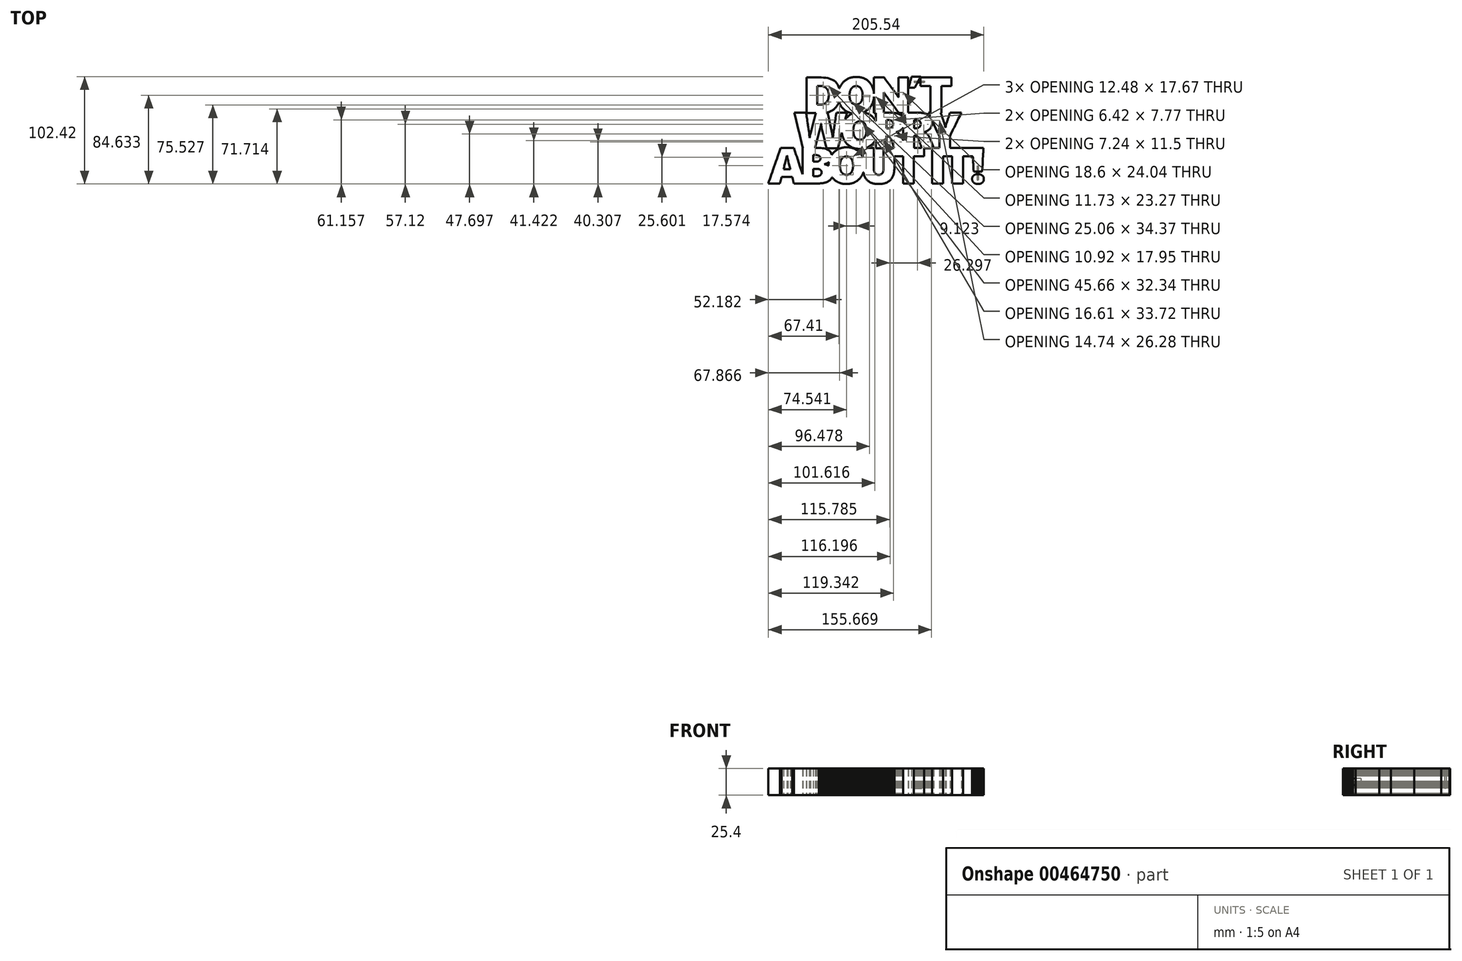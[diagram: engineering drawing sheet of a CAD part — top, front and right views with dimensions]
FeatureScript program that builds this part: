
annotation { "Feature Type Name" : "Feature", "Feature Type Description" : "" }
export const myFeature = defineFeature(function(context is Context, id is Id, definition is map)
    precondition{}
    {
        {
            var Q0;
            Q0=qCreatedBy(makeId("Top.planeOp"),FACE);
            cPlane(context, id + "F0", {"entities" : qUnion([Q0]), "cplaneType" : CPlaneType.OFFSET, "offset" : 12.7 * mm, "width" : 152.4 * mm, "height" : 152.4 * mm});
        }
        {
            var Q0;
            Q0=qCreatedBy(makeId("Top.planeOp"),FACE);
            var sketch = newSketch(context, id + "F1", { "sketchPlane" : qUnion([Q0])});
            skLineSegment(sketch, "E0", {"start": v(31.67, 40.7) * mm, "end": v(32.04, 40.7) * mm});
            skLineSegment(sketch, "E1", {"start": v(32.04, 40.7) * mm, "end": v(32.4, 40.7) * mm});
            skLineSegment(sketch, "E2", {"start": v(32.4, 40.7) * mm, "end": v(32.77, 40.7) * mm});
            skLineSegment(sketch, "E3", {"start": v(32.77, 40.7) * mm, "end": v(33.14, 40.7) * mm});
            skLineSegment(sketch, "E4", {"start": v(33.14, 40.7) * mm, "end": v(33.5, 40.7) * mm});
            skLineSegment(sketch, "E5", {"start": v(33.5, 40.7) * mm, "end": v(33.88, 40.7) * mm});
            skLineSegment(sketch, "E6", {"start": v(33.88, 40.7) * mm, "end": v(34.24, 40.7) * mm});
            skLineSegment(sketch, "E7", {"start": v(34.24, 40.7) * mm, "end": v(34.61, 40.7) * mm});
            skLineSegment(sketch, "E8", {"start": v(34.61, 40.7) * mm, "end": v(34.98, 40.7) * mm});
            skLineSegment(sketch, "E9", {"start": v(34.98, 40.7) * mm, "end": v(35.34, 40.7) * mm});
            skLineSegment(sketch, "E10", {"start": v(35.34, 40.7) * mm, "end": v(35.71, 40.7) * mm});
            skLineSegment(sketch, "E11", {"start": v(35.71, 40.7) * mm, "end": v(36.08, 40.7) * mm});
            skLineSegment(sketch, "E12", {"start": v(36.08, 40.7) * mm, "end": v(36.45, 40.7) * mm});
            skLineSegment(sketch, "E13", {"start": v(36.45, 40.7) * mm, "end": v(36.81, 40.7) * mm});
            skLineSegment(sketch, "E14", {"start": v(36.81, 40.7) * mm, "end": v(37.17, 41.35) * mm});
            skLineSegment(sketch, "E15", {"start": v(37.17, 41.35) * mm, "end": v(37.53, 42) * mm});
            skLineSegment(sketch, "E16", {"start": v(37.53, 42) * mm, "end": v(37.88, 42.67) * mm});
            skLineSegment(sketch, "E17", {"start": v(37.88, 42.67) * mm, "end": v(38.24, 43.32) * mm});
            skLineSegment(sketch, "E18", {"start": v(38.24, 43.32) * mm, "end": v(38.6, 43.98) * mm});
            skLineSegment(sketch, "E19", {"start": v(38.6, 43.98) * mm, "end": v(38.95, 44.64) * mm});
            skLineSegment(sketch, "E20", {"start": v(38.95, 44.64) * mm, "end": v(39.31, 45.3) * mm});
            skLineSegment(sketch, "E21", {"start": v(39.31, 45.3) * mm, "end": v(39.67, 45.95) * mm});
            skLineSegment(sketch, "E22", {"start": v(39.67, 45.95) * mm, "end": v(40.02, 46.6) * mm});
            skLineSegment(sketch, "E23", {"start": v(40.02, 46.6) * mm, "end": v(40.38, 47.27) * mm});
            skLineSegment(sketch, "E24", {"start": v(40.38, 47.27) * mm, "end": v(40.74, 47.92) * mm});
            skLineSegment(sketch, "E25", {"start": v(40.74, 47.92) * mm, "end": v(41.1, 48.58) * mm});
            skLineSegment(sketch, "E26", {"start": v(41.1, 48.58) * mm, "end": v(41.45, 49.24) * mm});
            skLineSegment(sketch, "E27", {"start": v(41.45, 49.24) * mm, "end": v(41.8, 49.9) * mm});
            skLineSegment(sketch, "E28", {"start": v(41.8, 49.9) * mm, "end": v(42.16, 50.55) * mm});
            skLineSegment(sketch, "E29", {"start": v(42.16, 50.55) * mm, "end": v(42.52, 51.21) * mm});
            skLineSegment(sketch, "E30", {"start": v(42.52, 51.21) * mm, "end": v(41.98, 51.21) * mm});
            skLineSegment(sketch, "E31", {"start": v(41.98, 51.21) * mm, "end": v(41.44, 51.21) * mm});
            skLineSegment(sketch, "E32", {"start": v(41.44, 51.21) * mm, "end": v(40.9, 51.21) * mm});
            skLineSegment(sketch, "E33", {"start": v(40.9, 51.21) * mm, "end": v(40.35, 51.21) * mm});
            skLineSegment(sketch, "E34", {"start": v(40.35, 51.21) * mm, "end": v(39.81, 51.21) * mm});
            skLineSegment(sketch, "E35", {"start": v(39.81, 51.21) * mm, "end": v(39.27, 51.21) * mm});
            skLineSegment(sketch, "E36", {"start": v(39.27, 51.21) * mm, "end": v(38.73, 51.21) * mm});
            skLineSegment(sketch, "E37", {"start": v(38.73, 51.21) * mm, "end": v(38.19, 51.21) * mm});
            skLineSegment(sketch, "E38", {"start": v(38.19, 51.21) * mm, "end": v(37.64, 51.21) * mm});
            skLineSegment(sketch, "E39", {"start": v(37.64, 51.21) * mm, "end": v(37.1, 51.21) * mm});
            skLineSegment(sketch, "E40", {"start": v(37.1, 51.21) * mm, "end": v(36.56, 51.21) * mm});
            skLineSegment(sketch, "E41", {"start": v(36.56, 51.21) * mm, "end": v(36.02, 51.21) * mm});
            skLineSegment(sketch, "E42", {"start": v(36.02, 51.21) * mm, "end": v(35.48, 51.21) * mm});
            skLineSegment(sketch, "E43", {"start": v(35.48, 51.21) * mm, "end": v(34.94, 51.21) * mm});
            skLineSegment(sketch, "E44", {"start": v(34.94, 51.21) * mm, "end": v(34.4, 51.21) * mm});
            skLineSegment(sketch, "E45", {"start": v(34.4, 51.21) * mm, "end": v(33.85, 51.21) * mm});
            skLineSegment(sketch, "E46", {"start": v(33.85, 51.21) * mm, "end": v(33.67, 50.55) * mm});
            skLineSegment(sketch, "E47", {"start": v(33.67, 50.55) * mm, "end": v(33.49, 49.9) * mm});
            skLineSegment(sketch, "E48", {"start": v(33.49, 49.9) * mm, "end": v(33.3, 49.24) * mm});
            skLineSegment(sketch, "E49", {"start": v(33.3, 49.24) * mm, "end": v(33.12, 48.58) * mm});
            skLineSegment(sketch, "E50", {"start": v(33.12, 48.58) * mm, "end": v(32.94, 47.92) * mm});
            skLineSegment(sketch, "E51", {"start": v(32.94, 47.92) * mm, "end": v(32.76, 47.27) * mm});
            skLineSegment(sketch, "E52", {"start": v(32.76, 47.27) * mm, "end": v(32.58, 46.6) * mm});
            skLineSegment(sketch, "E53", {"start": v(32.58, 46.6) * mm, "end": v(32.4, 45.95) * mm});
            skLineSegment(sketch, "E54", {"start": v(32.4, 45.95) * mm, "end": v(32.21, 45.3) * mm});
            skLineSegment(sketch, "E55", {"start": v(32.21, 45.3) * mm, "end": v(32.03, 44.64) * mm});
            skLineSegment(sketch, "E56", {"start": v(32.03, 44.64) * mm, "end": v(31.85, 43.98) * mm});
            skLineSegment(sketch, "E57", {"start": v(31.85, 43.98) * mm, "end": v(31.67, 43.32) * mm});
            skLineSegment(sketch, "E58", {"start": v(31.67, 43.32) * mm, "end": v(31.49, 42.67) * mm});
            skLineSegment(sketch, "E59", {"start": v(31.49, 42.67) * mm, "end": v(31.3, 42) * mm});
            skLineSegment(sketch, "E60", {"start": v(31.3, 42) * mm, "end": v(31.12, 41.35) * mm});
            skLineSegment(sketch, "E61", {"start": v(31.12, 41.35) * mm, "end": v(30.94, 40.7) * mm});
            skLineSegment(sketch, "E62", {"start": v(30.94, 40.7) * mm, "end": v(31.3, 40.7) * mm});
            skLineSegment(sketch, "E63", {"start": v(31.3, 40.7) * mm, "end": v(31.67, 40.7) * mm});
            skLineSegment(sketch, "E64", {"start": v(92.2, -24.66) * mm, "end": v(92.23, -25.1) * mm});
            skLineSegment(sketch, "E65", {"start": v(92.23, -25.1) * mm, "end": v(92.31, -26.5) * mm});
            skLineSegment(sketch, "E66", {"start": v(92.31, -26.5) * mm, "end": v(92.4, -27.92) * mm});
            skLineSegment(sketch, "E67", {"start": v(92.4, -27.92) * mm, "end": v(92.47, -29.32) * mm});
            skLineSegment(sketch, "E68", {"start": v(92.47, -29.32) * mm, "end": v(92.55, -30.73) * mm});
            skLineSegment(sketch, "E69", {"start": v(92.55, -30.73) * mm, "end": v(92.63, -32.14) * mm});
            skLineSegment(sketch, "E70", {"start": v(92.63, -32.14) * mm, "end": v(92.71, -33.55) * mm});
            skLineSegment(sketch, "E71", {"start": v(92.71, -33.55) * mm, "end": v(92.8, -34.95) * mm});
            skLineSegment(sketch, "E72", {"start": v(92.8, -34.95) * mm, "end": v(92.87, -36.36) * mm});
            skLineSegment(sketch, "E73", {"start": v(92.87, -36.36) * mm, "end": v(92.95, -37.77) * mm});
            skLineSegment(sketch, "E74", {"start": v(92.95, -37.77) * mm, "end": v(93.03, -39.18) * mm});
            skLineSegment(sketch, "E75", {"start": v(93.03, -39.18) * mm, "end": v(93.54, -39.18) * mm});
            skLineSegment(sketch, "E76", {"start": v(93.54, -39.18) * mm, "end": v(94.04, -39.18) * mm});
            skLineSegment(sketch, "E77", {"start": v(94.04, -39.18) * mm, "end": v(94.55, -39.18) * mm});
            skLineSegment(sketch, "E78", {"start": v(94.55, -39.18) * mm, "end": v(95.06, -39.18) * mm});
            skLineSegment(sketch, "E79", {"start": v(95.06, -39.18) * mm, "end": v(95.56, -39.18) * mm});
            skLineSegment(sketch, "E80", {"start": v(95.56, -39.18) * mm, "end": v(96.07, -39.18) * mm});
            skLineSegment(sketch, "E81", {"start": v(96.07, -39.18) * mm, "end": v(96.58, -39.18) * mm});
            skLineSegment(sketch, "E82", {"start": v(96.58, -39.18) * mm, "end": v(97.08, -39.18) * mm});
            skLineSegment(sketch, "E83", {"start": v(97.08, -39.18) * mm, "end": v(97.59, -39.18) * mm});
            skLineSegment(sketch, "E84", {"start": v(97.59, -39.18) * mm, "end": v(98.1, -39.18) * mm});
            skLineSegment(sketch, "E85", {"start": v(98.1, -39.18) * mm, "end": v(98.6, -39.18) * mm});
            skLineSegment(sketch, "E86", {"start": v(98.6, -39.18) * mm, "end": v(99.1, -39.18) * mm});
            skLineSegment(sketch, "E87", {"start": v(99.1, -39.18) * mm, "end": v(99.61, -39.18) * mm});
            skLineSegment(sketch, "E88", {"start": v(99.61, -39.18) * mm, "end": v(100.12, -39.18) * mm});
            skLineSegment(sketch, "E89", {"start": v(100.12, -39.18) * mm, "end": v(100.63, -39.18) * mm});
            skLineSegment(sketch, "E90", {"start": v(100.63, -39.18) * mm, "end": v(101.13, -39.18) * mm});
            skLineSegment(sketch, "E91", {"start": v(101.13, -39.18) * mm, "end": v(101.21, -37.77) * mm});
            skLineSegment(sketch, "E92", {"start": v(101.21, -37.77) * mm, "end": v(101.29, -36.36) * mm});
            skLineSegment(sketch, "E93", {"start": v(101.29, -36.36) * mm, "end": v(101.37, -34.95) * mm});
            skLineSegment(sketch, "E94", {"start": v(101.37, -34.95) * mm, "end": v(101.45, -33.55) * mm});
            skLineSegment(sketch, "E95", {"start": v(101.45, -33.55) * mm, "end": v(101.53, -32.14) * mm});
            skLineSegment(sketch, "E96", {"start": v(101.53, -32.14) * mm, "end": v(101.6, -30.73) * mm});
            skLineSegment(sketch, "E97", {"start": v(101.6, -30.73) * mm, "end": v(101.68, -29.32) * mm});
            skLineSegment(sketch, "E98", {"start": v(101.68, -29.32) * mm, "end": v(101.76, -27.92) * mm});
            skLineSegment(sketch, "E99", {"start": v(101.76, -27.92) * mm, "end": v(101.84, -26.5) * mm});
            skLineSegment(sketch, "E100", {"start": v(101.84, -26.5) * mm, "end": v(101.92, -25.1) * mm});
            skLineSegment(sketch, "E101", {"start": v(101.92, -25.1) * mm, "end": v(102, -23.7) * mm});
            skLineSegment(sketch, "E102", {"start": v(102, -23.7) * mm, "end": v(102.07, -22.28) * mm});
            skLineSegment(sketch, "E103", {"start": v(102.07, -22.28) * mm, "end": v(102.15, -20.88) * mm});
            skLineSegment(sketch, "E104", {"start": v(102.15, -20.88) * mm, "end": v(102.23, -19.47) * mm});
            skLineSegment(sketch, "E105", {"start": v(102.23, -19.47) * mm, "end": v(102.3, -18.06) * mm});
            skLineSegment(sketch, "E106", {"start": v(102.3, -18.06) * mm, "end": v(102.39, -16.65) * mm});
            skLineSegment(sketch, "E107", {"start": v(102.39, -16.65) * mm, "end": v(101.72, -16.65) * mm});
            skLineSegment(sketch, "E108", {"start": v(101.72, -16.65) * mm, "end": v(101.06, -16.65) * mm});
            skLineSegment(sketch, "E109", {"start": v(101.06, -16.65) * mm, "end": v(100.4, -16.65) * mm});
            skLineSegment(sketch, "E110", {"start": v(100.4, -16.65) * mm, "end": v(99.73, -16.65) * mm});
            skLineSegment(sketch, "E111", {"start": v(99.73, -16.65) * mm, "end": v(99.06, -16.65) * mm});
            skLineSegment(sketch, "E112", {"start": v(99.06, -16.65) * mm, "end": v(98.4, -16.65) * mm});
            skLineSegment(sketch, "E113", {"start": v(98.4, -16.65) * mm, "end": v(97.74, -16.65) * mm});
            skLineSegment(sketch, "E114", {"start": v(97.74, -16.65) * mm, "end": v(97.07, -16.65) * mm});
            skLineSegment(sketch, "E115", {"start": v(97.07, -16.65) * mm, "end": v(96.4, -16.65) * mm});
            skLineSegment(sketch, "E116", {"start": v(96.4, -16.65) * mm, "end": v(95.74, -16.65) * mm});
            skLineSegment(sketch, "E117", {"start": v(95.74, -16.65) * mm, "end": v(95.08, -16.65) * mm});
            skLineSegment(sketch, "E118", {"start": v(95.08, -16.65) * mm, "end": v(94.41, -16.65) * mm});
            skLineSegment(sketch, "E119", {"start": v(94.41, -16.65) * mm, "end": v(93.75, -16.65) * mm});
            skLineSegment(sketch, "E120", {"start": v(93.75, -16.65) * mm, "end": v(93.08, -16.65) * mm});
            skLineSegment(sketch, "E121", {"start": v(93.08, -16.65) * mm, "end": v(92.42, -16.65) * mm});
            skLineSegment(sketch, "E122", {"start": v(92.42, -16.65) * mm, "end": v(92.39, -16.65) * mm});
            skLineSegment(sketch, "E123", {"start": v(92.39, -16.65) * mm, "end": v(91.75, -16.65) * mm});
            skLineSegment(sketch, "E124", {"start": v(91.75, -16.65) * mm, "end": v(90.55, -16.65) * mm});
            skLineSegment(sketch, "E125", {"start": v(90.55, -16.65) * mm, "end": v(88.71, -16.65) * mm});
            skLineSegment(sketch, "E126", {"start": v(88.71, -16.65) * mm, "end": v(86.88, -16.65) * mm});
            skLineSegment(sketch, "E127", {"start": v(86.88, -16.65) * mm, "end": v(85.04, -16.65) * mm});
            skLineSegment(sketch, "E128", {"start": v(85.04, -16.65) * mm, "end": v(83.2, -16.65) * mm});
            skLineSegment(sketch, "E129", {"start": v(83.2, -16.65) * mm, "end": v(81.37, -16.65) * mm});
            skLineSegment(sketch, "E130", {"start": v(81.37, -16.65) * mm, "end": v(79.53, -16.65) * mm});
            skLineSegment(sketch, "E131", {"start": v(79.53, -16.65) * mm, "end": v(77.7, -16.65) * mm});
            skLineSegment(sketch, "E132", {"start": v(77.7, -16.65) * mm, "end": v(75.85, -16.65) * mm});
            skLineSegment(sketch, "E133", {"start": v(75.85, -16.65) * mm, "end": v(74.02, -16.65) * mm});
            skLineSegment(sketch, "E134", {"start": v(74.02, -16.65) * mm, "end": v(72.18, -16.65) * mm});
            skLineSegment(sketch, "E135", {"start": v(72.18, -16.65) * mm, "end": v(70.5, -16.65) * mm});
            skLineSegment(sketch, "E136", {"start": v(70.5, -16.65) * mm, "end": v(70.5, -16.35) * mm});
            skLineSegment(sketch, "E137", {"start": v(70.5, -16.35) * mm, "end": v(70.5, -15.61) * mm});
            skLineSegment(sketch, "E138", {"start": v(70.5, -15.61) * mm, "end": v(70.5, -14.88) * mm});
            skLineSegment(sketch, "E139", {"start": v(70.5, -14.88) * mm, "end": v(70.5, -14.14) * mm});
            skLineSegment(sketch, "E140", {"start": v(70.5, -14.14) * mm, "end": v(70.5, -13.4) * mm});
            skLineSegment(sketch, "E141", {"start": v(70.5, -13.4) * mm, "end": v(70.5, -12.67) * mm});
            skLineSegment(sketch, "E142", {"start": v(70.5, -12.67) * mm, "end": v(70.5, -11.93) * mm});
            skLineSegment(sketch, "E143", {"start": v(70.5, -11.93) * mm, "end": v(70.5, -11.2) * mm});
            skLineSegment(sketch, "E144", {"start": v(70.5, -11.2) * mm, "end": v(70.5, -10.45) * mm});
            skLineSegment(sketch, "E145", {"start": v(70.5, -10.45) * mm, "end": v(70.5, -9.72) * mm});
            skLineSegment(sketch, "E146", {"start": v(70.5, -9.72) * mm, "end": v(70.5, -8.98) * mm});
            skLineSegment(sketch, "E147", {"start": v(70.5, -8.98) * mm, "end": v(70.5, -8.24) * mm});
            skLineSegment(sketch, "E148", {"start": v(70.5, -8.24) * mm, "end": v(70.5, -7.5) * mm});
            skLineSegment(sketch, "E149", {"start": v(70.5, -7.5) * mm, "end": v(70.5, -6.77) * mm});
            skLineSegment(sketch, "E150", {"start": v(70.5, -6.77) * mm, "end": v(70.5, -6.03) * mm});
            skLineSegment(sketch, "E151", {"start": v(70.5, -6.03) * mm, "end": v(70.5, -5.3) * mm});
            skLineSegment(sketch, "E152", {"start": v(70.5, -5.3) * mm, "end": v(71.18, -3.9) * mm});
            skLineSegment(sketch, "E153", {"start": v(71.18, -3.9) * mm, "end": v(71.85, -2.52) * mm});
            skLineSegment(sketch, "E154", {"start": v(71.85, -2.52) * mm, "end": v(72.53, -1.14) * mm});
            skLineSegment(sketch, "E155", {"start": v(72.53, -1.14) * mm, "end": v(73.2, 0.25) * mm});
            skLineSegment(sketch, "E156", {"start": v(73.2, 0.25) * mm, "end": v(73.88, 1.63) * mm});
            skLineSegment(sketch, "E157", {"start": v(73.88, 1.63) * mm, "end": v(74.56, 3.02) * mm});
            skLineSegment(sketch, "E158", {"start": v(74.56, 3.02) * mm, "end": v(75.23, 4.4) * mm});
            skLineSegment(sketch, "E159", {"start": v(75.23, 4.4) * mm, "end": v(75.91, 5.8) * mm});
            skLineSegment(sketch, "E160", {"start": v(75.91, 5.8) * mm, "end": v(76.59, 7.18) * mm});
            skLineSegment(sketch, "E161", {"start": v(76.59, 7.18) * mm, "end": v(77.26, 8.56) * mm});
            skLineSegment(sketch, "E162", {"start": v(77.26, 8.56) * mm, "end": v(77.94, 9.95) * mm});
            skLineSegment(sketch, "E163", {"start": v(77.94, 9.95) * mm, "end": v(78.62, 11.33) * mm});
            skLineSegment(sketch, "E164", {"start": v(78.62, 11.33) * mm, "end": v(79.3, 12.72) * mm});
            skLineSegment(sketch, "E165", {"start": v(79.3, 12.72) * mm, "end": v(79.97, 14.1) * mm});
            skLineSegment(sketch, "E166", {"start": v(79.97, 14.1) * mm, "end": v(80.65, 15.5) * mm});
            skLineSegment(sketch, "E167", {"start": v(80.65, 15.5) * mm, "end": v(81.32, 16.88) * mm});
            skLineSegment(sketch, "E168", {"start": v(81.32, 16.88) * mm, "end": v(80.65, 16.88) * mm});
            skLineSegment(sketch, "E169", {"start": v(80.65, 16.88) * mm, "end": v(79.97, 16.88) * mm});
            skLineSegment(sketch, "E170", {"start": v(79.97, 16.88) * mm, "end": v(79.3, 16.88) * mm});
            skLineSegment(sketch, "E171", {"start": v(79.3, 16.88) * mm, "end": v(78.62, 16.88) * mm});
            skLineSegment(sketch, "E172", {"start": v(78.62, 16.88) * mm, "end": v(77.94, 16.88) * mm});
            skLineSegment(sketch, "E173", {"start": v(77.94, 16.88) * mm, "end": v(77.26, 16.88) * mm});
            skLineSegment(sketch, "E174", {"start": v(77.26, 16.88) * mm, "end": v(76.59, 16.88) * mm});
            skLineSegment(sketch, "E175", {"start": v(76.59, 16.88) * mm, "end": v(75.91, 16.88) * mm});
            skLineSegment(sketch, "E176", {"start": v(75.91, 16.88) * mm, "end": v(75.23, 16.88) * mm});
            skLineSegment(sketch, "E177", {"start": v(75.23, 16.88) * mm, "end": v(74.56, 16.88) * mm});
            skLineSegment(sketch, "E178", {"start": v(74.56, 16.88) * mm, "end": v(73.88, 16.88) * mm});
            skLineSegment(sketch, "E179", {"start": v(73.88, 16.88) * mm, "end": v(73.2, 16.88) * mm});
            skLineSegment(sketch, "E180", {"start": v(73.2, 16.88) * mm, "end": v(72.53, 16.88) * mm});
            skLineSegment(sketch, "E181", {"start": v(72.53, 16.88) * mm, "end": v(71.85, 16.88) * mm});
            skLineSegment(sketch, "E182", {"start": v(71.85, 16.88) * mm, "end": v(71.18, 16.88) * mm});
            skLineSegment(sketch, "E183", {"start": v(71.18, 16.88) * mm, "end": v(70.5, 16.88) * mm});
            skLineSegment(sketch, "E184", {"start": v(70.5, 16.88) * mm, "end": v(70.27, 16.2) * mm});
            skLineSegment(sketch, "E185", {"start": v(70.27, 16.2) * mm, "end": v(70.05, 15.52) * mm});
            skLineSegment(sketch, "E186", {"start": v(70.05, 15.52) * mm, "end": v(69.82, 14.84) * mm});
            skLineSegment(sketch, "E187", {"start": v(69.82, 14.84) * mm, "end": v(69.6, 14.16) * mm});
            skLineSegment(sketch, "E188", {"start": v(69.6, 14.16) * mm, "end": v(69.37, 13.48) * mm});
            skLineSegment(sketch, "E189", {"start": v(69.37, 13.48) * mm, "end": v(69.14, 12.8) * mm});
            skLineSegment(sketch, "E190", {"start": v(69.14, 12.8) * mm, "end": v(68.91, 12.12) * mm});
            skLineSegment(sketch, "E191", {"start": v(68.91, 12.12) * mm, "end": v(68.69, 11.44) * mm});
            skLineSegment(sketch, "E192", {"start": v(68.69, 11.44) * mm, "end": v(68.46, 10.76) * mm});
            skLineSegment(sketch, "E193", {"start": v(68.46, 10.76) * mm, "end": v(68.23, 10.08) * mm});
            skLineSegment(sketch, "E194", {"start": v(68.23, 10.08) * mm, "end": v(68, 9.4) * mm});
            skLineSegment(sketch, "E195", {"start": v(68, 9.4) * mm, "end": v(67.78, 8.72) * mm});
            skLineSegment(sketch, "E196", {"start": v(67.78, 8.72) * mm, "end": v(67.56, 8.04) * mm});
            skLineSegment(sketch, "E197", {"start": v(67.56, 8.04) * mm, "end": v(67.33, 7.36) * mm});
            skLineSegment(sketch, "E198", {"start": v(67.33, 7.36) * mm, "end": v(67.1, 6.68) * mm});
            skLineSegment(sketch, "E199", {"start": v(67.1, 6.68) * mm, "end": v(66.88, 6) * mm});
            skLineSegment(sketch, "E200", {"start": v(66.88, 6) * mm, "end": v(66.83, 5.85) * mm});
            skLineSegment(sketch, "E201", {"start": v(66.83, 5.85) * mm, "end": v(66.78, 5.7) * mm});
            skLineSegment(sketch, "E202", {"start": v(66.78, 5.7) * mm, "end": v(66.74, 5.53) * mm});
            skLineSegment(sketch, "E203", {"start": v(66.74, 5.53) * mm, "end": v(66.7, 5.35) * mm});
            skLineSegment(sketch, "E204", {"start": v(66.7, 5.35) * mm, "end": v(66.65, 5.17) * mm});
            skLineSegment(sketch, "E205", {"start": v(66.65, 5.17) * mm, "end": v(66.6, 4.98) * mm});
            skLineSegment(sketch, "E206", {"start": v(66.6, 4.98) * mm, "end": v(66.56, 4.78) * mm});
            skLineSegment(sketch, "E207", {"start": v(66.56, 4.78) * mm, "end": v(66.51, 4.58) * mm});
            skLineSegment(sketch, "E208", {"start": v(66.51, 4.58) * mm, "end": v(66.47, 4.36) * mm});
            skLineSegment(sketch, "E209", {"start": v(66.47, 4.36) * mm, "end": v(66.43, 4.14) * mm});
            skLineSegment(sketch, "E210", {"start": v(66.43, 4.14) * mm, "end": v(66.39, 3.92) * mm});
            skLineSegment(sketch, "E211", {"start": v(66.39, 3.92) * mm, "end": v(66.35, 3.68) * mm});
            skLineSegment(sketch, "E212", {"start": v(66.35, 3.68) * mm, "end": v(66.3, 3.44) * mm});
            skLineSegment(sketch, "E213", {"start": v(66.3, 3.44) * mm, "end": v(66.27, 3.19) * mm});
            skLineSegment(sketch, "E214", {"start": v(66.27, 3.19) * mm, "end": v(66.23, 2.93) * mm});
            skLineSegment(sketch, "E215", {"start": v(66.23, 2.93) * mm, "end": v(66.19, 2.66) * mm});
            skLineSegment(sketch, "E216", {"start": v(66.19, 2.66) * mm, "end": v(66.18, 2.66) * mm});
            skLineSegment(sketch, "E217", {"start": v(66.18, 2.66) * mm, "end": v(66.18, 2.66) * mm});
            skLineSegment(sketch, "E218", {"start": v(66.18, 2.66) * mm, "end": v(66.17, 2.66) * mm});
            skLineSegment(sketch, "E219", {"start": v(66.17, 2.66) * mm, "end": v(66.17, 2.66) * mm});
            skLineSegment(sketch, "E220", {"start": v(66.17, 2.66) * mm, "end": v(66.16, 2.66) * mm});
            skLineSegment(sketch, "E221", {"start": v(66.16, 2.66) * mm, "end": v(66.15, 2.66) * mm});
            skLineSegment(sketch, "E222", {"start": v(66.15, 2.66) * mm, "end": v(66.15, 2.66) * mm});
            skLineSegment(sketch, "E223", {"start": v(66.15, 2.66) * mm, "end": v(66.14, 2.66) * mm});
            skLineSegment(sketch, "E224", {"start": v(66.14, 2.66) * mm, "end": v(66.14, 2.66) * mm});
            skLineSegment(sketch, "E225", {"start": v(66.14, 2.66) * mm, "end": v(66.13, 2.66) * mm});
            skLineSegment(sketch, "E226", {"start": v(66.13, 2.66) * mm, "end": v(66.12, 2.66) * mm});
            skLineSegment(sketch, "E227", {"start": v(66.12, 2.66) * mm, "end": v(66.12, 2.66) * mm});
            skLineSegment(sketch, "E228", {"start": v(66.12, 2.66) * mm, "end": v(66.11, 2.66) * mm});
            skLineSegment(sketch, "E229", {"start": v(66.11, 2.66) * mm, "end": v(66.1, 2.66) * mm});
            skLineSegment(sketch, "E230", {"start": v(66.1, 2.66) * mm, "end": v(66.1, 2.66) * mm});
            skLineSegment(sketch, "E231", {"start": v(66.1, 2.66) * mm, "end": v(66.07, 2.77) * mm});
            skLineSegment(sketch, "E232", {"start": v(66.07, 2.77) * mm, "end": v(66.05, 2.87) * mm});
            skLineSegment(sketch, "E233", {"start": v(66.05, 2.87) * mm, "end": v(66.02, 2.97) * mm});
            skLineSegment(sketch, "E234", {"start": v(66.02, 2.97) * mm, "end": v(66, 3.08) * mm});
            skLineSegment(sketch, "E235", {"start": v(66, 3.08) * mm, "end": v(65.98, 3.18) * mm});
            skLineSegment(sketch, "E236", {"start": v(65.98, 3.18) * mm, "end": v(65.96, 3.28) * mm});
            skLineSegment(sketch, "E237", {"start": v(65.96, 3.28) * mm, "end": v(65.93, 3.39) * mm});
            skLineSegment(sketch, "E238", {"start": v(65.93, 3.39) * mm, "end": v(65.91, 3.49) * mm});
            skLineSegment(sketch, "E239", {"start": v(65.91, 3.49) * mm, "end": v(65.9, 3.59) * mm});
            skLineSegment(sketch, "E240", {"start": v(65.9, 3.59) * mm, "end": v(65.87, 3.7) * mm});
            skLineSegment(sketch, "E241", {"start": v(65.87, 3.7) * mm, "end": v(65.85, 3.8) * mm});
            skLineSegment(sketch, "E242", {"start": v(65.85, 3.8) * mm, "end": v(65.83, 3.9) * mm});
            skLineSegment(sketch, "E243", {"start": v(65.83, 3.9) * mm, "end": v(65.8, 4) * mm});
            skLineSegment(sketch, "E244", {"start": v(65.8, 4) * mm, "end": v(65.79, 4.1) * mm});
            skLineSegment(sketch, "E245", {"start": v(65.79, 4.1) * mm, "end": v(65.77, 4.2) * mm});
            skLineSegment(sketch, "E246", {"start": v(65.77, 4.2) * mm, "end": v(65.75, 4.3) * mm});
            skLineSegment(sketch, "E247", {"start": v(65.75, 4.3) * mm, "end": v(65.73, 4.4) * mm});
            skLineSegment(sketch, "E248", {"start": v(65.73, 4.4) * mm, "end": v(65.7, 4.5) * mm});
            skLineSegment(sketch, "E249", {"start": v(65.7, 4.5) * mm, "end": v(65.68, 4.61) * mm});
            skLineSegment(sketch, "E250", {"start": v(65.68, 4.61) * mm, "end": v(65.66, 4.72) * mm});
            skLineSegment(sketch, "E251", {"start": v(65.66, 4.72) * mm, "end": v(65.63, 4.83) * mm});
            skLineSegment(sketch, "E252", {"start": v(65.63, 4.83) * mm, "end": v(65.6, 4.94) * mm});
            skLineSegment(sketch, "E253", {"start": v(65.6, 4.94) * mm, "end": v(65.57, 5.06) * mm});
            skLineSegment(sketch, "E254", {"start": v(65.57, 5.06) * mm, "end": v(65.54, 5.18) * mm});
            skLineSegment(sketch, "E255", {"start": v(65.54, 5.18) * mm, "end": v(65.5, 5.3) * mm});
            skLineSegment(sketch, "E256", {"start": v(65.5, 5.3) * mm, "end": v(65.47, 5.42) * mm});
            skLineSegment(sketch, "E257", {"start": v(65.47, 5.42) * mm, "end": v(65.43, 5.54) * mm});
            skLineSegment(sketch, "E258", {"start": v(65.43, 5.54) * mm, "end": v(65.4, 5.67) * mm});
            skLineSegment(sketch, "E259", {"start": v(65.4, 5.67) * mm, "end": v(65.35, 5.8) * mm});
            skLineSegment(sketch, "E260", {"start": v(65.35, 5.8) * mm, "end": v(65.3, 5.93) * mm});
            skLineSegment(sketch, "E261", {"start": v(65.3, 5.93) * mm, "end": v(65.26, 6.06) * mm});
            skLineSegment(sketch, "E262", {"start": v(65.26, 6.06) * mm, "end": v(65.22, 6.2) * mm});
            skLineSegment(sketch, "E263", {"start": v(65.22, 6.2) * mm, "end": v(64.99, 6.86) * mm});
            skLineSegment(sketch, "E264", {"start": v(64.99, 6.86) * mm, "end": v(64.76, 7.53) * mm});
            skLineSegment(sketch, "E265", {"start": v(64.76, 7.53) * mm, "end": v(64.53, 8.2) * mm});
            skLineSegment(sketch, "E266", {"start": v(64.53, 8.2) * mm, "end": v(64.3, 8.86) * mm});
            skLineSegment(sketch, "E267", {"start": v(64.3, 8.86) * mm, "end": v(64.07, 9.53) * mm});
            skLineSegment(sketch, "E268", {"start": v(64.07, 9.53) * mm, "end": v(63.84, 10.2) * mm});
            skLineSegment(sketch, "E269", {"start": v(63.84, 10.2) * mm, "end": v(63.61, 10.87) * mm});
            skLineSegment(sketch, "E270", {"start": v(63.61, 10.87) * mm, "end": v(63.38, 11.53) * mm});
            skLineSegment(sketch, "E271", {"start": v(63.38, 11.53) * mm, "end": v(63.15, 12.2) * mm});
            skLineSegment(sketch, "E272", {"start": v(63.15, 12.2) * mm, "end": v(62.92, 12.87) * mm});
            skLineSegment(sketch, "E273", {"start": v(62.92, 12.87) * mm, "end": v(62.7, 13.54) * mm});
            skLineSegment(sketch, "E274", {"start": v(62.7, 13.54) * mm, "end": v(62.46, 14.2) * mm});
            skLineSegment(sketch, "E275", {"start": v(62.46, 14.2) * mm, "end": v(62.23, 14.87) * mm});
            skLineSegment(sketch, "E276", {"start": v(62.23, 14.87) * mm, "end": v(62, 15.54) * mm});
            skLineSegment(sketch, "E277", {"start": v(62, 15.54) * mm, "end": v(61.78, 16.2) * mm});
            skLineSegment(sketch, "E278", {"start": v(61.78, 16.2) * mm, "end": v(61.7, 16.44) * mm});
            skLineSegment(sketch, "E279", {"start": v(61.7, 16.44) * mm, "end": v(62.2, 16.44) * mm});
            skLineSegment(sketch, "E280", {"start": v(62.2, 16.44) * mm, "end": v(62.2, 18.06) * mm});
            skLineSegment(sketch, "E281", {"start": v(62.2, 18.06) * mm, "end": v(62.2, 19.69) * mm});
            skLineSegment(sketch, "E282", {"start": v(62.2, 19.69) * mm, "end": v(62.2, 21.3) * mm});
            skLineSegment(sketch, "E283", {"start": v(62.2, 21.3) * mm, "end": v(62.2, 22.93) * mm});
            skLineSegment(sketch, "E284", {"start": v(62.2, 22.93) * mm, "end": v(62.2, 24.55) * mm});
            skLineSegment(sketch, "E285", {"start": v(62.2, 24.55) * mm, "end": v(62.2, 26.18) * mm});
            skLineSegment(sketch, "E286", {"start": v(62.2, 26.18) * mm, "end": v(62.2, 27.8) * mm});
            skLineSegment(sketch, "E287", {"start": v(62.2, 27.8) * mm, "end": v(62.2, 29.42) * mm});
            skLineSegment(sketch, "E288", {"start": v(62.2, 29.42) * mm, "end": v(62.2, 31.04) * mm});
            skLineSegment(sketch, "E289", {"start": v(62.2, 31.04) * mm, "end": v(62.2, 32.66) * mm});
            skLineSegment(sketch, "E290", {"start": v(62.2, 32.66) * mm, "end": v(62.2, 34.29) * mm});
            skLineSegment(sketch, "E291", {"start": v(62.2, 34.29) * mm, "end": v(62.2, 35.9) * mm});
            skLineSegment(sketch, "E292", {"start": v(62.2, 35.9) * mm, "end": v(62.2, 37.53) * mm});
            skLineSegment(sketch, "E293", {"start": v(62.2, 37.53) * mm, "end": v(62.2, 39.15) * mm});
            skLineSegment(sketch, "E294", {"start": v(62.2, 39.15) * mm, "end": v(62.2, 40.78) * mm});
            skLineSegment(sketch, "E295", {"start": v(62.2, 40.78) * mm, "end": v(62.2, 42.4) * mm});
            skLineSegment(sketch, "E296", {"start": v(62.2, 42.4) * mm, "end": v(62.8, 42.4) * mm});
            skLineSegment(sketch, "E297", {"start": v(62.8, 42.4) * mm, "end": v(63.4, 42.4) * mm});
            skLineSegment(sketch, "E298", {"start": v(63.4, 42.4) * mm, "end": v(64, 42.4) * mm});
            skLineSegment(sketch, "E299", {"start": v(64, 42.4) * mm, "end": v(64.61, 42.4) * mm});
            skLineSegment(sketch, "E300", {"start": v(64.61, 42.4) * mm, "end": v(65.21, 42.4) * mm});
            skLineSegment(sketch, "E301", {"start": v(65.21, 42.4) * mm, "end": v(65.81, 42.4) * mm});
            skLineSegment(sketch, "E302", {"start": v(65.81, 42.4) * mm, "end": v(66.41, 42.4) * mm});
            skLineSegment(sketch, "E303", {"start": v(66.41, 42.4) * mm, "end": v(67.01, 42.4) * mm});
            skLineSegment(sketch, "E304", {"start": v(67.01, 42.4) * mm, "end": v(67.62, 42.4) * mm});
            skLineSegment(sketch, "E305", {"start": v(67.62, 42.4) * mm, "end": v(68.22, 42.4) * mm});
            skLineSegment(sketch, "E306", {"start": v(68.22, 42.4) * mm, "end": v(68.82, 42.4) * mm});
            skLineSegment(sketch, "E307", {"start": v(68.82, 42.4) * mm, "end": v(69.42, 42.4) * mm});
            skLineSegment(sketch, "E308", {"start": v(69.42, 42.4) * mm, "end": v(70.02, 42.4) * mm});
            skLineSegment(sketch, "E309", {"start": v(70.02, 42.4) * mm, "end": v(70.62, 42.4) * mm});
            skLineSegment(sketch, "E310", {"start": v(70.62, 42.4) * mm, "end": v(71.22, 42.4) * mm});
            skLineSegment(sketch, "E311", {"start": v(71.22, 42.4) * mm, "end": v(71.82, 42.4) * mm});
            skLineSegment(sketch, "E312", {"start": v(71.82, 42.4) * mm, "end": v(71.82, 42.9) * mm});
            skLineSegment(sketch, "E313", {"start": v(71.82, 42.9) * mm, "end": v(71.82, 43.4) * mm});
            skLineSegment(sketch, "E314", {"start": v(71.82, 43.4) * mm, "end": v(71.82, 43.9) * mm});
            skLineSegment(sketch, "E315", {"start": v(71.82, 43.9) * mm, "end": v(71.82, 44.4) * mm});
            skLineSegment(sketch, "E316", {"start": v(71.82, 44.4) * mm, "end": v(71.82, 44.9) * mm});
            skLineSegment(sketch, "E317", {"start": v(71.82, 44.9) * mm, "end": v(71.82, 45.4) * mm});
            skLineSegment(sketch, "E318", {"start": v(71.82, 45.4) * mm, "end": v(71.82, 45.9) * mm});
            skLineSegment(sketch, "E319", {"start": v(71.82, 45.9) * mm, "end": v(71.82, 46.4) * mm});
            skLineSegment(sketch, "E320", {"start": v(71.82, 46.4) * mm, "end": v(71.82, 46.9) * mm});
            skLineSegment(sketch, "E321", {"start": v(71.82, 46.9) * mm, "end": v(71.82, 47.4) * mm});
            skLineSegment(sketch, "E322", {"start": v(71.82, 47.4) * mm, "end": v(71.82, 47.9) * mm});
            skLineSegment(sketch, "E323", {"start": v(71.82, 47.9) * mm, "end": v(71.82, 48.4) * mm});
            skLineSegment(sketch, "E324", {"start": v(71.82, 48.4) * mm, "end": v(71.82, 48.9) * mm});
            skLineSegment(sketch, "E325", {"start": v(71.82, 48.9) * mm, "end": v(71.82, 49.4) * mm});
            skLineSegment(sketch, "E326", {"start": v(71.82, 49.4) * mm, "end": v(71.82, 49.9) * mm});
            skLineSegment(sketch, "E327", {"start": v(71.82, 49.9) * mm, "end": v(71.82, 50.4) * mm});
            skLineSegment(sketch, "E328", {"start": v(71.82, 50.4) * mm, "end": v(69.99, 50.4) * mm});
            skLineSegment(sketch, "E329", {"start": v(69.99, 50.4) * mm, "end": v(68.15, 50.4) * mm});
            skLineSegment(sketch, "E330", {"start": v(68.15, 50.4) * mm, "end": v(66.31, 50.4) * mm});
            skLineSegment(sketch, "E331", {"start": v(66.31, 50.4) * mm, "end": v(64.47, 50.4) * mm});
            skLineSegment(sketch, "E332", {"start": v(64.47, 50.4) * mm, "end": v(62.64, 50.4) * mm});
            skLineSegment(sketch, "E333", {"start": v(62.64, 50.4) * mm, "end": v(60.8, 50.4) * mm});
            skLineSegment(sketch, "E334", {"start": v(60.8, 50.4) * mm, "end": v(58.96, 50.4) * mm});
            skLineSegment(sketch, "E335", {"start": v(58.96, 50.4) * mm, "end": v(57.13, 50.4) * mm});
            skLineSegment(sketch, "E336", {"start": v(57.13, 50.4) * mm, "end": v(55.29, 50.4) * mm});
            skLineSegment(sketch, "E337", {"start": v(55.29, 50.4) * mm, "end": v(53.45, 50.4) * mm});
            skLineSegment(sketch, "E338", {"start": v(53.45, 50.4) * mm, "end": v(51.61, 50.4) * mm});
            skLineSegment(sketch, "E339", {"start": v(51.61, 50.4) * mm, "end": v(49.78, 50.4) * mm});
            skLineSegment(sketch, "E340", {"start": v(49.78, 50.4) * mm, "end": v(47.94, 50.4) * mm});
            skLineSegment(sketch, "E341", {"start": v(47.94, 50.4) * mm, "end": v(46.1, 50.4) * mm});
            skLineSegment(sketch, "E342", {"start": v(46.1, 50.4) * mm, "end": v(44.27, 50.4) * mm});
            skLineSegment(sketch, "E343", {"start": v(44.27, 50.4) * mm, "end": v(42.43, 50.4) * mm});
            skLineSegment(sketch, "E344", {"start": v(42.43, 50.4) * mm, "end": v(42.43, 49.9) * mm});
            skLineSegment(sketch, "E345", {"start": v(42.43, 49.9) * mm, "end": v(42.43, 49.4) * mm});
            skLineSegment(sketch, "E346", {"start": v(42.43, 49.4) * mm, "end": v(42.43, 48.9) * mm});
            skLineSegment(sketch, "E347", {"start": v(42.43, 48.9) * mm, "end": v(42.43, 48.4) * mm});
            skLineSegment(sketch, "E348", {"start": v(42.43, 48.4) * mm, "end": v(42.43, 47.9) * mm});
            skLineSegment(sketch, "E349", {"start": v(42.43, 47.9) * mm, "end": v(42.43, 47.4) * mm});
            skLineSegment(sketch, "E350", {"start": v(42.43, 47.4) * mm, "end": v(42.43, 46.9) * mm});
            skLineSegment(sketch, "E351", {"start": v(42.43, 46.9) * mm, "end": v(42.43, 46.4) * mm});
            skLineSegment(sketch, "E352", {"start": v(42.43, 46.4) * mm, "end": v(42.43, 45.9) * mm});
            skLineSegment(sketch, "E353", {"start": v(42.43, 45.9) * mm, "end": v(42.43, 45.4) * mm});
            skLineSegment(sketch, "E354", {"start": v(42.43, 45.4) * mm, "end": v(42.43, 44.9) * mm});
            skLineSegment(sketch, "E355", {"start": v(42.43, 44.9) * mm, "end": v(42.43, 44.4) * mm});
            skLineSegment(sketch, "E356", {"start": v(42.43, 44.4) * mm, "end": v(42.43, 43.9) * mm});
            skLineSegment(sketch, "E357", {"start": v(42.43, 43.9) * mm, "end": v(42.43, 43.4) * mm});
            skLineSegment(sketch, "E358", {"start": v(42.43, 43.4) * mm, "end": v(42.43, 42.9) * mm});
            skLineSegment(sketch, "E359", {"start": v(42.43, 42.9) * mm, "end": v(42.43, 42.4) * mm});
            skLineSegment(sketch, "E360", {"start": v(42.43, 42.4) * mm, "end": v(43.02, 42.4) * mm});
            skLineSegment(sketch, "E361", {"start": v(43.02, 42.4) * mm, "end": v(43.62, 42.4) * mm});
            skLineSegment(sketch, "E362", {"start": v(43.62, 42.4) * mm, "end": v(44.2, 42.4) * mm});
            skLineSegment(sketch, "E363", {"start": v(44.2, 42.4) * mm, "end": v(44.8, 42.4) * mm});
            skLineSegment(sketch, "E364", {"start": v(44.8, 42.4) * mm, "end": v(45.4, 42.4) * mm});
            skLineSegment(sketch, "E365", {"start": v(45.4, 42.4) * mm, "end": v(46, 42.4) * mm});
            skLineSegment(sketch, "E366", {"start": v(46, 42.4) * mm, "end": v(46.58, 42.4) * mm});
            skLineSegment(sketch, "E367", {"start": v(46.58, 42.4) * mm, "end": v(47.18, 42.4) * mm});
            skLineSegment(sketch, "E368", {"start": v(47.18, 42.4) * mm, "end": v(47.77, 42.4) * mm});
            skLineSegment(sketch, "E369", {"start": v(47.77, 42.4) * mm, "end": v(48.37, 42.4) * mm});
            skLineSegment(sketch, "E370", {"start": v(48.37, 42.4) * mm, "end": v(48.96, 42.4) * mm});
            skLineSegment(sketch, "E371", {"start": v(48.96, 42.4) * mm, "end": v(49.55, 42.4) * mm});
            skLineSegment(sketch, "E372", {"start": v(49.55, 42.4) * mm, "end": v(50.15, 42.4) * mm});
            skLineSegment(sketch, "E373", {"start": v(50.15, 42.4) * mm, "end": v(50.74, 42.4) * mm});
            skLineSegment(sketch, "E374", {"start": v(50.74, 42.4) * mm, "end": v(51.33, 42.4) * mm});
            skLineSegment(sketch, "E375", {"start": v(51.33, 42.4) * mm, "end": v(51.93, 42.4) * mm});
            skLineSegment(sketch, "E376", {"start": v(51.93, 42.4) * mm, "end": v(51.93, 40.78) * mm});
            skLineSegment(sketch, "E377", {"start": v(51.93, 40.78) * mm, "end": v(51.93, 39.15) * mm});
            skLineSegment(sketch, "E378", {"start": v(51.93, 39.15) * mm, "end": v(51.93, 37.53) * mm});
            skLineSegment(sketch, "E379", {"start": v(51.93, 37.53) * mm, "end": v(51.93, 35.9) * mm});
            skLineSegment(sketch, "E380", {"start": v(51.93, 35.9) * mm, "end": v(51.93, 34.29) * mm});
            skLineSegment(sketch, "E381", {"start": v(51.93, 34.29) * mm, "end": v(51.93, 32.66) * mm});
            skLineSegment(sketch, "E382", {"start": v(51.93, 32.66) * mm, "end": v(51.93, 31.04) * mm});
            skLineSegment(sketch, "E383", {"start": v(51.93, 31.04) * mm, "end": v(51.93, 29.42) * mm});
            skLineSegment(sketch, "E384", {"start": v(51.93, 29.42) * mm, "end": v(51.93, 27.8) * mm});
            skLineSegment(sketch, "E385", {"start": v(51.93, 27.8) * mm, "end": v(51.93, 26.18) * mm});
            skLineSegment(sketch, "E386", {"start": v(51.93, 26.18) * mm, "end": v(51.93, 24.55) * mm});
            skLineSegment(sketch, "E387", {"start": v(51.93, 24.55) * mm, "end": v(51.93, 22.93) * mm});
            skLineSegment(sketch, "E388", {"start": v(51.93, 22.93) * mm, "end": v(51.93, 21.3) * mm});
            skLineSegment(sketch, "E389", {"start": v(51.93, 21.3) * mm, "end": v(51.93, 19.69) * mm});
            skLineSegment(sketch, "E390", {"start": v(51.93, 19.69) * mm, "end": v(51.93, 18.06) * mm});
            skLineSegment(sketch, "E391", {"start": v(51.93, 18.06) * mm, "end": v(51.93, 16.88) * mm});
            skLineSegment(sketch, "E392", {"start": v(51.93, 16.88) * mm, "end": v(51.27, 16.88) * mm});
            skLineSegment(sketch, "E393", {"start": v(51.27, 16.88) * mm, "end": v(50.53, 16.88) * mm});
            skLineSegment(sketch, "E394", {"start": v(50.53, 16.88) * mm, "end": v(49.8, 16.88) * mm});
            skLineSegment(sketch, "E395", {"start": v(49.8, 16.88) * mm, "end": v(50.45, 15.48) * mm});
            skLineSegment(sketch, "E396", {"start": v(50.45, 15.48) * mm, "end": v(51.1, 14.09) * mm});
            skLineSegment(sketch, "E397", {"start": v(51.1, 14.09) * mm, "end": v(51.55, 13.15) * mm});
            skLineSegment(sketch, "E398", {"start": v(51.55, 13.15) * mm, "end": v(51.48, 13.23) * mm});
            skLineSegment(sketch, "E399", {"start": v(51.48, 13.23) * mm, "end": v(51.15, 13.59) * mm});
            skLineSegment(sketch, "E400", {"start": v(51.15, 13.59) * mm, "end": v(50.8, 13.92) * mm});
            skLineSegment(sketch, "E401", {"start": v(50.8, 13.92) * mm, "end": v(50.4, 14.24) * mm});
            skLineSegment(sketch, "E402", {"start": v(50.4, 14.24) * mm, "end": v(50, 14.54) * mm});
            skLineSegment(sketch, "E403", {"start": v(50, 14.54) * mm, "end": v(49.55, 14.83) * mm});
            skLineSegment(sketch, "E404", {"start": v(49.55, 14.83) * mm, "end": v(49.09, 15.09) * mm});
            skLineSegment(sketch, "E405", {"start": v(49.09, 15.09) * mm, "end": v(48.59, 15.34) * mm});
            skLineSegment(sketch, "E406", {"start": v(48.59, 15.34) * mm, "end": v(48.06, 15.56) * mm});
            skLineSegment(sketch, "E407", {"start": v(48.06, 15.56) * mm, "end": v(47.5, 15.77) * mm});
            skLineSegment(sketch, "E408", {"start": v(47.5, 15.77) * mm, "end": v(46.92, 15.96) * mm});
            skLineSegment(sketch, "E409", {"start": v(46.92, 15.96) * mm, "end": v(46.3, 16.14) * mm});
            skLineSegment(sketch, "E410", {"start": v(46.3, 16.14) * mm, "end": v(45.66, 16.3) * mm});
            skLineSegment(sketch, "E411", {"start": v(45.66, 16.3) * mm, "end": v(45, 16.43) * mm});
            skLineSegment(sketch, "E412", {"start": v(45, 16.43) * mm, "end": v(44.29, 16.55) * mm});
            skLineSegment(sketch, "E413", {"start": v(44.29, 16.55) * mm, "end": v(43.56, 16.65) * mm});
            skLineSegment(sketch, "E414", {"start": v(43.56, 16.65) * mm, "end": v(42.8, 16.73) * mm});
            skLineSegment(sketch, "E415", {"start": v(42.8, 16.73) * mm, "end": v(42, 16.8) * mm});
            skLineSegment(sketch, "E416", {"start": v(42, 16.8) * mm, "end": v(41.2, 16.84) * mm});
            skLineSegment(sketch, "E417", {"start": v(41.2, 16.84) * mm, "end": v(40.34, 16.87) * mm});
            skLineSegment(sketch, "E418", {"start": v(40.34, 16.87) * mm, "end": v(39.47, 16.88) * mm});
            skLineSegment(sketch, "E419", {"start": v(39.47, 16.88) * mm, "end": v(38.62, 16.88) * mm});
            skLineSegment(sketch, "E420", {"start": v(38.62, 16.88) * mm, "end": v(37.77, 16.88) * mm});
            skLineSegment(sketch, "E421", {"start": v(37.77, 16.88) * mm, "end": v(36.92, 16.88) * mm});
            skLineSegment(sketch, "E422", {"start": v(36.92, 16.88) * mm, "end": v(36.07, 16.88) * mm});
            skLineSegment(sketch, "E423", {"start": v(36.07, 16.88) * mm, "end": v(35.22, 16.88) * mm});
            skLineSegment(sketch, "E424", {"start": v(35.22, 16.88) * mm, "end": v(34.37, 16.88) * mm});
            skLineSegment(sketch, "E425", {"start": v(34.37, 16.88) * mm, "end": v(33.52, 16.88) * mm});
            skLineSegment(sketch, "E426", {"start": v(33.52, 16.88) * mm, "end": v(32.67, 16.88) * mm});
            skLineSegment(sketch, "E427", {"start": v(32.67, 16.88) * mm, "end": v(31.82, 16.88) * mm});
            skLineSegment(sketch, "E428", {"start": v(31.82, 16.88) * mm, "end": v(30.97, 16.88) * mm});
            skLineSegment(sketch, "E429", {"start": v(30.97, 16.88) * mm, "end": v(30.65, 16.88) * mm});
            skLineSegment(sketch, "E430", {"start": v(30.65, 16.88) * mm, "end": v(30.65, 18.56) * mm});
            skLineSegment(sketch, "E431", {"start": v(30.65, 18.56) * mm, "end": v(30.65, 20.69) * mm});
            skLineSegment(sketch, "E432", {"start": v(30.65, 20.69) * mm, "end": v(30.65, 22.8) * mm});
            skLineSegment(sketch, "E433", {"start": v(30.65, 22.8) * mm, "end": v(30.65, 24.93) * mm});
            skLineSegment(sketch, "E434", {"start": v(30.65, 24.93) * mm, "end": v(30.65, 27.05) * mm});
            skLineSegment(sketch, "E435", {"start": v(30.65, 27.05) * mm, "end": v(30.65, 29.18) * mm});
            skLineSegment(sketch, "E436", {"start": v(30.65, 29.18) * mm, "end": v(30.65, 31.3) * mm});
            skLineSegment(sketch, "E437", {"start": v(30.65, 31.3) * mm, "end": v(30.65, 33.42) * mm});
            skLineSegment(sketch, "E438", {"start": v(30.65, 33.42) * mm, "end": v(30.65, 35.55) * mm});
            skLineSegment(sketch, "E439", {"start": v(30.65, 35.55) * mm, "end": v(30.65, 37.67) * mm});
            skLineSegment(sketch, "E440", {"start": v(30.65, 37.67) * mm, "end": v(30.65, 39.8) * mm});
            skLineSegment(sketch, "E441", {"start": v(30.65, 39.8) * mm, "end": v(30.65, 41.91) * mm});
            skLineSegment(sketch, "E442", {"start": v(30.65, 41.91) * mm, "end": v(30.65, 44.04) * mm});
            skLineSegment(sketch, "E443", {"start": v(30.65, 44.04) * mm, "end": v(30.65, 46.16) * mm});
            skLineSegment(sketch, "E444", {"start": v(30.65, 46.16) * mm, "end": v(30.65, 48.28) * mm});
            skLineSegment(sketch, "E445", {"start": v(30.65, 48.28) * mm, "end": v(30.65, 50.4) * mm});
            skLineSegment(sketch, "E446", {"start": v(30.65, 50.4) * mm, "end": v(30.06, 50.4) * mm});
            skLineSegment(sketch, "E447", {"start": v(30.06, 50.4) * mm, "end": v(29.46, 50.4) * mm});
            skLineSegment(sketch, "E448", {"start": v(29.46, 50.4) * mm, "end": v(28.87, 50.4) * mm});
            skLineSegment(sketch, "E449", {"start": v(28.87, 50.4) * mm, "end": v(28.28, 50.4) * mm});
            skLineSegment(sketch, "E450", {"start": v(28.28, 50.4) * mm, "end": v(27.69, 50.4) * mm});
            skLineSegment(sketch, "E451", {"start": v(27.69, 50.4) * mm, "end": v(27.1, 50.4) * mm});
            skLineSegment(sketch, "E452", {"start": v(27.1, 50.4) * mm, "end": v(26.5, 50.4) * mm});
            skLineSegment(sketch, "E453", {"start": v(26.5, 50.4) * mm, "end": v(25.91, 50.4) * mm});
            skLineSegment(sketch, "E454", {"start": v(25.91, 50.4) * mm, "end": v(25.32, 50.4) * mm});
            skLineSegment(sketch, "E455", {"start": v(25.32, 50.4) * mm, "end": v(24.73, 50.4) * mm});
            skLineSegment(sketch, "E456", {"start": v(24.73, 50.4) * mm, "end": v(24.14, 50.4) * mm});
            skLineSegment(sketch, "E457", {"start": v(24.14, 50.4) * mm, "end": v(23.54, 50.4) * mm});
            skLineSegment(sketch, "E458", {"start": v(23.54, 50.4) * mm, "end": v(22.95, 50.4) * mm});
            skLineSegment(sketch, "E459", {"start": v(22.95, 50.4) * mm, "end": v(22.36, 50.4) * mm});
            skLineSegment(sketch, "E460", {"start": v(22.36, 50.4) * mm, "end": v(21.77, 50.4) * mm});
            skLineSegment(sketch, "E461", {"start": v(21.77, 50.4) * mm, "end": v(21.18, 50.4) * mm});
            skLineSegment(sketch, "E462", {"start": v(21.18, 50.4) * mm, "end": v(21.18, 49.45) * mm});
            skLineSegment(sketch, "E463", {"start": v(21.18, 49.45) * mm, "end": v(21.18, 48.5) * mm});
            skLineSegment(sketch, "E464", {"start": v(21.18, 48.5) * mm, "end": v(21.18, 47.55) * mm});
            skLineSegment(sketch, "E465", {"start": v(21.18, 47.55) * mm, "end": v(21.18, 46.6) * mm});
            skLineSegment(sketch, "E466", {"start": v(21.18, 46.6) * mm, "end": v(21.18, 45.65) * mm});
            skLineSegment(sketch, "E467", {"start": v(21.18, 45.65) * mm, "end": v(21.18, 44.7) * mm});
            skLineSegment(sketch, "E468", {"start": v(21.18, 44.7) * mm, "end": v(21.18, 43.74) * mm});
            skLineSegment(sketch, "E469", {"start": v(21.18, 43.74) * mm, "end": v(21.18, 42.8) * mm});
            skLineSegment(sketch, "E470", {"start": v(21.18, 42.8) * mm, "end": v(21.18, 41.84) * mm});
            skLineSegment(sketch, "E471", {"start": v(21.18, 41.84) * mm, "end": v(21.18, 40.89) * mm});
            skLineSegment(sketch, "E472", {"start": v(21.18, 40.89) * mm, "end": v(21.18, 39.93) * mm});
            skLineSegment(sketch, "E473", {"start": v(21.18, 39.93) * mm, "end": v(21.18, 38.98) * mm});
            skLineSegment(sketch, "E474", {"start": v(21.18, 38.98) * mm, "end": v(21.18, 38.03) * mm});
            skLineSegment(sketch, "E475", {"start": v(21.18, 38.03) * mm, "end": v(21.18, 37.08) * mm});
            skLineSegment(sketch, "E476", {"start": v(21.18, 37.08) * mm, "end": v(21.18, 36.13) * mm});
            skLineSegment(sketch, "E477", {"start": v(21.18, 36.13) * mm, "end": v(21.18, 35.18) * mm});
            skLineSegment(sketch, "E478", {"start": v(21.18, 35.18) * mm, "end": v(21.18, 34.86) * mm});
            skLineSegment(sketch, "E479", {"start": v(21.18, 34.86) * mm, "end": v(21.18, 34.56) * mm});
            skLineSegment(sketch, "E480", {"start": v(21.18, 34.56) * mm, "end": v(21.18, 34.27) * mm});
            skLineSegment(sketch, "E481", {"start": v(21.18, 34.27) * mm, "end": v(21.18, 34) * mm});
            skLineSegment(sketch, "E482", {"start": v(21.18, 34) * mm, "end": v(21.19, 33.72) * mm});
            skLineSegment(sketch, "E483", {"start": v(21.19, 33.72) * mm, "end": v(21.2, 33.47) * mm});
            skLineSegment(sketch, "E484", {"start": v(21.2, 33.47) * mm, "end": v(21.2, 33.23) * mm});
            skLineSegment(sketch, "E485", {"start": v(21.2, 33.23) * mm, "end": v(21.21, 33) * mm});
            skLineSegment(sketch, "E486", {"start": v(21.21, 33) * mm, "end": v(21.22, 32.78) * mm});
            skLineSegment(sketch, "E487", {"start": v(21.22, 32.78) * mm, "end": v(21.23, 32.57) * mm});
            skLineSegment(sketch, "E488", {"start": v(21.23, 32.57) * mm, "end": v(21.24, 32.37) * mm});
            skLineSegment(sketch, "E489", {"start": v(21.24, 32.37) * mm, "end": v(21.26, 32.2) * mm});
            skLineSegment(sketch, "E490", {"start": v(21.26, 32.2) * mm, "end": v(21.27, 32.02) * mm});
            skLineSegment(sketch, "E491", {"start": v(21.27, 32.02) * mm, "end": v(21.28, 31.86) * mm});
            skLineSegment(sketch, "E492", {"start": v(21.28, 31.86) * mm, "end": v(21.3, 31.71) * mm});
            skLineSegment(sketch, "E493", {"start": v(21.3, 31.71) * mm, "end": v(21.32, 31.58) * mm});
            skLineSegment(sketch, "E494", {"start": v(21.32, 31.58) * mm, "end": v(21.31, 31.58) * mm});
            skLineSegment(sketch, "E495", {"start": v(21.31, 31.58) * mm, "end": v(21.3, 31.58) * mm});
            skLineSegment(sketch, "E496", {"start": v(21.3, 31.58) * mm, "end": v(21.3, 31.58) * mm});
            skLineSegment(sketch, "E497", {"start": v(21.3, 31.58) * mm, "end": v(21.29, 31.58) * mm});
            skLineSegment(sketch, "E498", {"start": v(21.29, 31.58) * mm, "end": v(21.28, 31.58) * mm});
            skLineSegment(sketch, "E499", {"start": v(21.28, 31.58) * mm, "end": v(21.28, 31.58) * mm});
            skLineSegment(sketch, "E500", {"start": v(21.28, 31.58) * mm, "end": v(21.27, 31.58) * mm});
            skLineSegment(sketch, "E501", {"start": v(21.27, 31.58) * mm, "end": v(21.26, 31.58) * mm});
            skLineSegment(sketch, "E502", {"start": v(21.26, 31.58) * mm, "end": v(21.26, 31.58) * mm});
            skLineSegment(sketch, "E503", {"start": v(21.26, 31.58) * mm, "end": v(21.25, 31.58) * mm});
            skLineSegment(sketch, "E504", {"start": v(21.25, 31.58) * mm, "end": v(21.25, 31.58) * mm});
            skLineSegment(sketch, "E505", {"start": v(21.25, 31.58) * mm, "end": v(21.24, 31.58) * mm});
            skLineSegment(sketch, "E506", {"start": v(21.24, 31.58) * mm, "end": v(21.23, 31.58) * mm});
            skLineSegment(sketch, "E507", {"start": v(21.23, 31.58) * mm, "end": v(21.23, 31.58) * mm});
            skLineSegment(sketch, "E508", {"start": v(21.23, 31.58) * mm, "end": v(21.22, 31.58) * mm});
            skLineSegment(sketch, "E509", {"start": v(21.22, 31.58) * mm, "end": v(21.2, 31.62) * mm});
            skLineSegment(sketch, "E510", {"start": v(21.2, 31.62) * mm, "end": v(21.18, 31.66) * mm});
            skLineSegment(sketch, "E511", {"start": v(21.18, 31.66) * mm, "end": v(21.16, 31.7) * mm});
            skLineSegment(sketch, "E512", {"start": v(21.16, 31.7) * mm, "end": v(21.14, 31.75) * mm});
            skLineSegment(sketch, "E513", {"start": v(21.14, 31.75) * mm, "end": v(21.12, 31.8) * mm});
            skLineSegment(sketch, "E514", {"start": v(21.12, 31.8) * mm, "end": v(21.1, 31.84) * mm});
            skLineSegment(sketch, "E515", {"start": v(21.1, 31.84) * mm, "end": v(21.07, 31.88) * mm});
            skLineSegment(sketch, "E516", {"start": v(21.07, 31.88) * mm, "end": v(21.05, 31.93) * mm});
            skLineSegment(sketch, "E517", {"start": v(21.05, 31.93) * mm, "end": v(21.02, 31.98) * mm});
            skLineSegment(sketch, "E518", {"start": v(21.02, 31.98) * mm, "end": v(21, 32.03) * mm});
            skLineSegment(sketch, "E519", {"start": v(21, 32.03) * mm, "end": v(20.97, 32.08) * mm});
            skLineSegment(sketch, "E520", {"start": v(20.97, 32.08) * mm, "end": v(20.94, 32.13) * mm});
            skLineSegment(sketch, "E521", {"start": v(20.94, 32.13) * mm, "end": v(20.9, 32.18) * mm});
            skLineSegment(sketch, "E522", {"start": v(20.9, 32.18) * mm, "end": v(20.87, 32.23) * mm});
            skLineSegment(sketch, "E523", {"start": v(20.87, 32.23) * mm, "end": v(20.84, 32.28) * mm});
            skLineSegment(sketch, "E524", {"start": v(20.84, 32.28) * mm, "end": v(20.8, 32.33) * mm});
            skLineSegment(sketch, "E525", {"start": v(20.8, 32.33) * mm, "end": v(20.77, 32.39) * mm});
            skLineSegment(sketch, "E526", {"start": v(20.77, 32.39) * mm, "end": v(20.74, 32.44) * mm});
            skLineSegment(sketch, "E527", {"start": v(20.74, 32.44) * mm, "end": v(20.7, 32.5) * mm});
            skLineSegment(sketch, "E528", {"start": v(20.7, 32.5) * mm, "end": v(20.67, 32.55) * mm});
            skLineSegment(sketch, "E529", {"start": v(20.67, 32.55) * mm, "end": v(20.63, 32.6) * mm});
            skLineSegment(sketch, "E530", {"start": v(20.63, 32.6) * mm, "end": v(20.6, 32.66) * mm});
            skLineSegment(sketch, "E531", {"start": v(20.6, 32.66) * mm, "end": v(20.56, 32.71) * mm});
            skLineSegment(sketch, "E532", {"start": v(20.56, 32.71) * mm, "end": v(20.53, 32.77) * mm});
            skLineSegment(sketch, "E533", {"start": v(20.53, 32.77) * mm, "end": v(20.5, 32.82) * mm});
            skLineSegment(sketch, "E534", {"start": v(20.5, 32.82) * mm, "end": v(20.45, 32.88) * mm});
            skLineSegment(sketch, "E535", {"start": v(20.45, 32.88) * mm, "end": v(20.42, 32.93) * mm});
            skLineSegment(sketch, "E536", {"start": v(20.42, 32.93) * mm, "end": v(20.38, 32.99) * mm});
            skLineSegment(sketch, "E537", {"start": v(20.38, 32.99) * mm, "end": v(20.34, 33.04) * mm});
            skLineSegment(sketch, "E538", {"start": v(20.34, 33.04) * mm, "end": v(20.3, 33.1) * mm});
            skLineSegment(sketch, "E539", {"start": v(20.3, 33.1) * mm, "end": v(20.27, 33.15) * mm});
            skLineSegment(sketch, "E540", {"start": v(20.27, 33.15) * mm, "end": v(20.23, 33.2) * mm});
            skLineSegment(sketch, "E541", {"start": v(20.23, 33.2) * mm, "end": v(20.19, 33.27) * mm});
            skLineSegment(sketch, "E542", {"start": v(20.19, 33.27) * mm, "end": v(20.15, 33.32) * mm});
            skLineSegment(sketch, "E543", {"start": v(20.15, 33.32) * mm, "end": v(20.11, 33.38) * mm});
            skLineSegment(sketch, "E544", {"start": v(20.11, 33.38) * mm, "end": v(20.07, 33.43) * mm});
            skLineSegment(sketch, "E545", {"start": v(20.07, 33.43) * mm, "end": v(20.04, 33.49) * mm});
            skLineSegment(sketch, "E546", {"start": v(20.04, 33.49) * mm, "end": v(20, 33.54) * mm});
            skLineSegment(sketch, "E547", {"start": v(20, 33.54) * mm, "end": v(19.96, 33.6) * mm});
            skLineSegment(sketch, "E548", {"start": v(19.96, 33.6) * mm, "end": v(19.92, 33.65) * mm});
            skLineSegment(sketch, "E549", {"start": v(19.92, 33.65) * mm, "end": v(19.88, 33.7) * mm});
            skLineSegment(sketch, "E550", {"start": v(19.88, 33.7) * mm, "end": v(19.84, 33.76) * mm});
            skLineSegment(sketch, "E551", {"start": v(19.84, 33.76) * mm, "end": v(19.8, 33.82) * mm});
            skLineSegment(sketch, "E552", {"start": v(19.8, 33.82) * mm, "end": v(19.77, 33.87) * mm});
            skLineSegment(sketch, "E553", {"start": v(19.77, 33.87) * mm, "end": v(19.73, 33.93) * mm});
            skLineSegment(sketch, "E554", {"start": v(19.73, 33.93) * mm, "end": v(19.69, 33.98) * mm});
            skLineSegment(sketch, "E555", {"start": v(19.69, 33.98) * mm, "end": v(19.65, 34.03) * mm});
            skLineSegment(sketch, "E556", {"start": v(19.65, 34.03) * mm, "end": v(19.61, 34.09) * mm});
            skLineSegment(sketch, "E557", {"start": v(19.61, 34.09) * mm, "end": v(19.57, 34.14) * mm});
            skLineSegment(sketch, "E558", {"start": v(19.57, 34.14) * mm, "end": v(19.54, 34.2) * mm});
            skLineSegment(sketch, "E559", {"start": v(19.54, 34.2) * mm, "end": v(19.5, 34.24) * mm});
            skLineSegment(sketch, "E560", {"start": v(19.5, 34.24) * mm, "end": v(19.46, 34.3) * mm});
            skLineSegment(sketch, "E561", {"start": v(19.46, 34.3) * mm, "end": v(19.43, 34.34) * mm});
            skLineSegment(sketch, "E562", {"start": v(19.43, 34.34) * mm, "end": v(19.4, 34.39) * mm});
            skLineSegment(sketch, "E563", {"start": v(19.4, 34.39) * mm, "end": v(19.36, 34.44) * mm});
            skLineSegment(sketch, "E564", {"start": v(19.36, 34.44) * mm, "end": v(19.33, 34.48) * mm});
            skLineSegment(sketch, "E565", {"start": v(19.33, 34.48) * mm, "end": v(19.3, 34.53) * mm});
            skLineSegment(sketch, "E566", {"start": v(19.3, 34.53) * mm, "end": v(19.26, 34.57) * mm});
            skLineSegment(sketch, "E567", {"start": v(19.26, 34.57) * mm, "end": v(19.23, 34.62) * mm});
            skLineSegment(sketch, "E568", {"start": v(19.23, 34.62) * mm, "end": v(19.2, 34.66) * mm});
            skLineSegment(sketch, "E569", {"start": v(19.2, 34.66) * mm, "end": v(19.17, 34.7) * mm});
            skLineSegment(sketch, "E570", {"start": v(19.17, 34.7) * mm, "end": v(19.15, 34.74) * mm});
            skLineSegment(sketch, "E571", {"start": v(19.15, 34.74) * mm, "end": v(19.12, 34.78) * mm});
            skLineSegment(sketch, "E572", {"start": v(19.12, 34.78) * mm, "end": v(19.1, 34.82) * mm});
            skLineSegment(sketch, "E573", {"start": v(19.1, 34.82) * mm, "end": v(18.37, 35.8) * mm});
            skLineSegment(sketch, "E574", {"start": v(18.37, 35.8) * mm, "end": v(17.65, 36.77) * mm});
            skLineSegment(sketch, "E575", {"start": v(17.65, 36.77) * mm, "end": v(16.94, 37.74) * mm});
            skLineSegment(sketch, "E576", {"start": v(16.94, 37.74) * mm, "end": v(16.22, 38.72) * mm});
            skLineSegment(sketch, "E577", {"start": v(16.22, 38.72) * mm, "end": v(15.5, 39.7) * mm});
            skLineSegment(sketch, "E578", {"start": v(15.5, 39.7) * mm, "end": v(14.78, 40.66) * mm});
            skLineSegment(sketch, "E579", {"start": v(14.78, 40.66) * mm, "end": v(14.07, 41.64) * mm});
            skLineSegment(sketch, "E580", {"start": v(14.07, 41.64) * mm, "end": v(13.35, 42.61) * mm});
            skLineSegment(sketch, "E581", {"start": v(13.35, 42.61) * mm, "end": v(12.63, 43.59) * mm});
            skLineSegment(sketch, "E582", {"start": v(12.63, 43.59) * mm, "end": v(11.91, 44.56) * mm});
            skLineSegment(sketch, "E583", {"start": v(11.91, 44.56) * mm, "end": v(11.2, 45.53) * mm});
            skLineSegment(sketch, "E584", {"start": v(11.2, 45.53) * mm, "end": v(10.48, 46.5) * mm});
            skLineSegment(sketch, "E585", {"start": v(10.48, 46.5) * mm, "end": v(9.76, 47.48) * mm});
            skLineSegment(sketch, "E586", {"start": v(9.76, 47.48) * mm, "end": v(9.04, 48.46) * mm});
            skLineSegment(sketch, "E587", {"start": v(9.04, 48.46) * mm, "end": v(8.32, 49.43) * mm});
            skLineSegment(sketch, "E588", {"start": v(8.32, 49.43) * mm, "end": v(7.6, 50.4) * mm});
            skLineSegment(sketch, "E589", {"start": v(7.6, 50.4) * mm, "end": v(7, 50.4) * mm});
            skLineSegment(sketch, "E590", {"start": v(7, 50.4) * mm, "end": v(6.4, 50.4) * mm});
            skLineSegment(sketch, "E591", {"start": v(6.4, 50.4) * mm, "end": v(5.8, 50.4) * mm});
            skLineSegment(sketch, "E592", {"start": v(5.8, 50.4) * mm, "end": v(5.19, 50.4) * mm});
            skLineSegment(sketch, "E593", {"start": v(5.19, 50.4) * mm, "end": v(4.58, 50.4) * mm});
            skLineSegment(sketch, "E594", {"start": v(4.58, 50.4) * mm, "end": v(3.98, 50.4) * mm});
            skLineSegment(sketch, "E595", {"start": v(3.98, 50.4) * mm, "end": v(3.38, 50.4) * mm});
            skLineSegment(sketch, "E596", {"start": v(3.38, 50.4) * mm, "end": v(2.77, 50.4) * mm});
            skLineSegment(sketch, "E597", {"start": v(2.77, 50.4) * mm, "end": v(2.17, 50.4) * mm});
            skLineSegment(sketch, "E598", {"start": v(2.17, 50.4) * mm, "end": v(1.56, 50.4) * mm});
            skLineSegment(sketch, "E599", {"start": v(1.56, 50.4) * mm, "end": v(0.96, 50.4) * mm});
            skLineSegment(sketch, "E600", {"start": v(0.96, 50.4) * mm, "end": v(0.36, 50.4) * mm});
            skLineSegment(sketch, "E601", {"start": v(0.36, 50.4) * mm, "end": v(-0.25, 50.4) * mm});
            skLineSegment(sketch, "E602", {"start": v(-0.25, 50.4) * mm, "end": v(-0.85, 50.4) * mm});
            skLineSegment(sketch, "E603", {"start": v(-0.85, 50.4) * mm, "end": v(-1.46, 50.4) * mm});
            skLineSegment(sketch, "E604", {"start": v(-1.46, 50.4) * mm, "end": v(-2.06, 50.4) * mm});
            skLineSegment(sketch, "E605", {"start": v(-2.06, 50.4) * mm, "end": v(-2.06, 48.28) * mm});
            skLineSegment(sketch, "E606", {"start": v(-2.06, 48.28) * mm, "end": v(-2.06, 46.16) * mm});
            skLineSegment(sketch, "E607", {"start": v(-2.06, 46.16) * mm, "end": v(-2.06, 44.04) * mm});
            skLineSegment(sketch, "E608", {"start": v(-2.06, 44.04) * mm, "end": v(-2.06, 41.91) * mm});
            skLineSegment(sketch, "E609", {"start": v(-2.06, 41.91) * mm, "end": v(-2.06, 39.8) * mm});
            skLineSegment(sketch, "E610", {"start": v(-2.06, 39.8) * mm, "end": v(-2.06, 37.67) * mm});
            skLineSegment(sketch, "E611", {"start": v(-2.06, 37.67) * mm, "end": v(-2.06, 35.55) * mm});
            skLineSegment(sketch, "E612", {"start": v(-2.06, 35.55) * mm, "end": v(-2.06, 34.92) * mm});
            skLineSegment(sketch, "E613", {"start": v(-2.06, 34.92) * mm, "end": v(-2.1, 35.39) * mm});
            skLineSegment(sketch, "E614", {"start": v(-2.1, 35.39) * mm, "end": v(-2.15, 36) * mm});
            skLineSegment(sketch, "E615", {"start": v(-2.15, 36) * mm, "end": v(-2.22, 36.6) * mm});
            skLineSegment(sketch, "E616", {"start": v(-2.22, 36.6) * mm, "end": v(-2.31, 37.19) * mm});
            skLineSegment(sketch, "E617", {"start": v(-2.31, 37.19) * mm, "end": v(-2.42, 37.77) * mm});
            skLineSegment(sketch, "E618", {"start": v(-2.42, 37.77) * mm, "end": v(-2.54, 38.34) * mm});
            skLineSegment(sketch, "E619", {"start": v(-2.54, 38.34) * mm, "end": v(-2.68, 38.9) * mm});
            skLineSegment(sketch, "E620", {"start": v(-2.68, 38.9) * mm, "end": v(-2.84, 39.46) * mm});
            skLineSegment(sketch, "E621", {"start": v(-2.84, 39.46) * mm, "end": v(-3, 40.01) * mm});
            skLineSegment(sketch, "E622", {"start": v(-3, 40.01) * mm, "end": v(-3.2, 40.55) * mm});
            skLineSegment(sketch, "E623", {"start": v(-3.2, 40.55) * mm, "end": v(-3.4, 41.08) * mm});
            skLineSegment(sketch, "E624", {"start": v(-3.4, 41.08) * mm, "end": v(-3.62, 41.6) * mm});
            skLineSegment(sketch, "E625", {"start": v(-3.62, 41.6) * mm, "end": v(-3.86, 42.12) * mm});
            skLineSegment(sketch, "E626", {"start": v(-3.86, 42.12) * mm, "end": v(-4.11, 42.62) * mm});
            skLineSegment(sketch, "E627", {"start": v(-4.11, 42.62) * mm, "end": v(-4.38, 43.12) * mm});
            skLineSegment(sketch, "E628", {"start": v(-4.38, 43.12) * mm, "end": v(-4.66, 43.6) * mm});
            skLineSegment(sketch, "E629", {"start": v(-4.66, 43.6) * mm, "end": v(-4.96, 44.06) * mm});
            skLineSegment(sketch, "E630", {"start": v(-4.96, 44.06) * mm, "end": v(-5.27, 44.52) * mm});
            skLineSegment(sketch, "E631", {"start": v(-5.27, 44.52) * mm, "end": v(-5.6, 44.95) * mm});
            skLineSegment(sketch, "E632", {"start": v(-5.6, 44.95) * mm, "end": v(-5.93, 45.38) * mm});
            skLineSegment(sketch, "E633", {"start": v(-5.93, 45.38) * mm, "end": v(-6.28, 45.78) * mm});
            skLineSegment(sketch, "E634", {"start": v(-6.28, 45.78) * mm, "end": v(-6.65, 46.18) * mm});
            skLineSegment(sketch, "E635", {"start": v(-6.65, 46.18) * mm, "end": v(-7.03, 46.56) * mm});
            skLineSegment(sketch, "E636", {"start": v(-7.03, 46.56) * mm, "end": v(-7.42, 46.92) * mm});
            skLineSegment(sketch, "E637", {"start": v(-7.42, 46.92) * mm, "end": v(-7.82, 47.27) * mm});
            skLineSegment(sketch, "E638", {"start": v(-7.82, 47.27) * mm, "end": v(-8.24, 47.6) * mm});
            skLineSegment(sketch, "E639", {"start": v(-8.24, 47.6) * mm, "end": v(-8.68, 47.93) * mm});
            skLineSegment(sketch, "E640", {"start": v(-8.68, 47.93) * mm, "end": v(-9.12, 48.24) * mm});
            skLineSegment(sketch, "E641", {"start": v(-9.12, 48.24) * mm, "end": v(-9.58, 48.53) * mm});
            skLineSegment(sketch, "E642", {"start": v(-9.58, 48.53) * mm, "end": v(-10.06, 48.8) * mm});
            skLineSegment(sketch, "E643", {"start": v(-10.06, 48.8) * mm, "end": v(-10.54, 49.07) * mm});
            skLineSegment(sketch, "E644", {"start": v(-10.54, 49.07) * mm, "end": v(-11.04, 49.31) * mm});
            skLineSegment(sketch, "E645", {"start": v(-11.04, 49.31) * mm, "end": v(-11.54, 49.54) * mm});
            skLineSegment(sketch, "E646", {"start": v(-11.54, 49.54) * mm, "end": v(-12.05, 49.75) * mm});
            skLineSegment(sketch, "E647", {"start": v(-12.05, 49.75) * mm, "end": v(-12.56, 49.95) * mm});
            skLineSegment(sketch, "E648", {"start": v(-12.56, 49.95) * mm, "end": v(-13.09, 50.13) * mm});
            skLineSegment(sketch, "E649", {"start": v(-13.09, 50.13) * mm, "end": v(-13.62, 50.29) * mm});
            skLineSegment(sketch, "E650", {"start": v(-13.62, 50.29) * mm, "end": v(-14.16, 50.43) * mm});
            skLineSegment(sketch, "E651", {"start": v(-14.16, 50.43) * mm, "end": v(-14.71, 50.56) * mm});
            skLineSegment(sketch, "E652", {"start": v(-14.71, 50.56) * mm, "end": v(-15.27, 50.67) * mm});
            skLineSegment(sketch, "E653", {"start": v(-15.27, 50.67) * mm, "end": v(-15.84, 50.76) * mm});
            skLineSegment(sketch, "E654", {"start": v(-15.84, 50.76) * mm, "end": v(-16.41, 50.84) * mm});
            skLineSegment(sketch, "E655", {"start": v(-16.41, 50.84) * mm, "end": v(-17, 50.9) * mm});
            skLineSegment(sketch, "E656", {"start": v(-17, 50.9) * mm, "end": v(-17.58, 50.94) * mm});
            skLineSegment(sketch, "E657", {"start": v(-17.58, 50.94) * mm, "end": v(-18.18, 50.96) * mm});
            skLineSegment(sketch, "E658", {"start": v(-18.18, 50.96) * mm, "end": v(-18.79, 50.97) * mm});
            skLineSegment(sketch, "E659", {"start": v(-18.79, 50.97) * mm, "end": v(-19.42, 50.96) * mm});
            skLineSegment(sketch, "E660", {"start": v(-19.42, 50.96) * mm, "end": v(-20.04, 50.94) * mm});
            skLineSegment(sketch, "E661", {"start": v(-20.04, 50.94) * mm, "end": v(-20.65, 50.9) * mm});
            skLineSegment(sketch, "E662", {"start": v(-20.65, 50.9) * mm, "end": v(-21.25, 50.83) * mm});
            skLineSegment(sketch, "E663", {"start": v(-21.25, 50.83) * mm, "end": v(-21.85, 50.75) * mm});
            skLineSegment(sketch, "E664", {"start": v(-21.85, 50.75) * mm, "end": v(-22.43, 50.66) * mm});
            skLineSegment(sketch, "E665", {"start": v(-22.43, 50.66) * mm, "end": v(-23.01, 50.54) * mm});
            skLineSegment(sketch, "E666", {"start": v(-23.01, 50.54) * mm, "end": v(-23.58, 50.4) * mm});
            skLineSegment(sketch, "E667", {"start": v(-23.58, 50.4) * mm, "end": v(-24.14, 50.26) * mm});
            skLineSegment(sketch, "E668", {"start": v(-24.14, 50.26) * mm, "end": v(-24.7, 50.09) * mm});
            skLineSegment(sketch, "E669", {"start": v(-24.7, 50.09) * mm, "end": v(-25.24, 49.9) * mm});
            skLineSegment(sketch, "E670", {"start": v(-25.24, 49.9) * mm, "end": v(-25.78, 49.7) * mm});
            skLineSegment(sketch, "E671", {"start": v(-25.78, 49.7) * mm, "end": v(-26.3, 49.48) * mm});
            skLineSegment(sketch, "E672", {"start": v(-26.3, 49.48) * mm, "end": v(-26.82, 49.24) * mm});
            skLineSegment(sketch, "E673", {"start": v(-26.82, 49.24) * mm, "end": v(-27.33, 48.99) * mm});
            skLineSegment(sketch, "E674", {"start": v(-27.33, 48.99) * mm, "end": v(-27.83, 48.71) * mm});
            skLineSegment(sketch, "E675", {"start": v(-27.83, 48.71) * mm, "end": v(-28.32, 48.42) * mm});
            skLineSegment(sketch, "E676", {"start": v(-28.32, 48.42) * mm, "end": v(-28.8, 48.12) * mm});
            skLineSegment(sketch, "E677", {"start": v(-28.8, 48.12) * mm, "end": v(-29.26, 47.8) * mm});
            skLineSegment(sketch, "E678", {"start": v(-29.26, 47.8) * mm, "end": v(-29.71, 47.46) * mm});
            skLineSegment(sketch, "E679", {"start": v(-29.71, 47.46) * mm, "end": v(-30.15, 47.11) * mm});
            skLineSegment(sketch, "E680", {"start": v(-30.15, 47.11) * mm, "end": v(-30.57, 46.75) * mm});
            skLineSegment(sketch, "E681", {"start": v(-30.57, 46.75) * mm, "end": v(-30.98, 46.37) * mm});
            skLineSegment(sketch, "E682", {"start": v(-30.98, 46.37) * mm, "end": v(-31.37, 45.98) * mm});
            skLineSegment(sketch, "E683", {"start": v(-31.37, 45.98) * mm, "end": v(-31.75, 45.57) * mm});
            skLineSegment(sketch, "E684", {"start": v(-31.75, 45.57) * mm, "end": v(-32.11, 45.15) * mm});
            skLineSegment(sketch, "E685", {"start": v(-32.11, 45.15) * mm, "end": v(-32.47, 44.71) * mm});
            skLineSegment(sketch, "E686", {"start": v(-32.47, 44.71) * mm, "end": v(-32.8, 44.26) * mm});
            skLineSegment(sketch, "E687", {"start": v(-32.8, 44.26) * mm, "end": v(-33.13, 43.8) * mm});
            skLineSegment(sketch, "E688", {"start": v(-33.13, 43.8) * mm, "end": v(-33.44, 43.31) * mm});
            skLineSegment(sketch, "E689", {"start": v(-33.44, 43.31) * mm, "end": v(-33.73, 42.82) * mm});
            skLineSegment(sketch, "E690", {"start": v(-33.73, 42.82) * mm, "end": v(-34.02, 42.3) * mm});
            skLineSegment(sketch, "E691", {"start": v(-34.02, 42.3) * mm, "end": v(-34.28, 41.78) * mm});
            skLineSegment(sketch, "E692", {"start": v(-34.28, 41.78) * mm, "end": v(-34.53, 41.25) * mm});
            skLineSegment(sketch, "E693", {"start": v(-34.53, 41.25) * mm, "end": v(-34.76, 40.71) * mm});
            skLineSegment(sketch, "E694", {"start": v(-34.76, 40.71) * mm, "end": v(-34.98, 40.17) * mm});
            skLineSegment(sketch, "E695", {"start": v(-34.98, 40.17) * mm, "end": v(-35.04, 39.99) * mm});
            skLineSegment(sketch, "E696", {"start": v(-35.04, 39.99) * mm, "end": v(-35.38, 41.1) * mm});
            skLineSegment(sketch, "E697", {"start": v(-35.38, 41.1) * mm, "end": v(-36.01, 42.58) * mm});
            skLineSegment(sketch, "E698", {"start": v(-36.01, 42.58) * mm, "end": v(-36.78, 43.94) * mm});
            skLineSegment(sketch, "E699", {"start": v(-36.78, 43.94) * mm, "end": v(-37.7, 45.17) * mm});
            skLineSegment(sketch, "E700", {"start": v(-37.7, 45.17) * mm, "end": v(-38.75, 46.27) * mm});
            skLineSegment(sketch, "E701", {"start": v(-38.75, 46.27) * mm, "end": v(-39.94, 47.24) * mm});
            skLineSegment(sketch, "E702", {"start": v(-39.94, 47.24) * mm, "end": v(-41.27, 48.08) * mm});
            skLineSegment(sketch, "E703", {"start": v(-41.27, 48.08) * mm, "end": v(-42.74, 48.79) * mm});
            skLineSegment(sketch, "E704", {"start": v(-42.74, 48.79) * mm, "end": v(-44.36, 49.37) * mm});
            skLineSegment(sketch, "E705", {"start": v(-44.36, 49.37) * mm, "end": v(-46.1, 49.82) * mm});
            skLineSegment(sketch, "E706", {"start": v(-46.1, 49.82) * mm, "end": v(-48, 50.15) * mm});
            skLineSegment(sketch, "E707", {"start": v(-48, 50.15) * mm, "end": v(-50.04, 50.34) * mm});
            skLineSegment(sketch, "E708", {"start": v(-50.04, 50.34) * mm, "end": v(-52.21, 50.4) * mm});
            skLineSegment(sketch, "E709", {"start": v(-52.21, 50.4) * mm, "end": v(-53.09, 50.4) * mm});
            skLineSegment(sketch, "E710", {"start": v(-53.09, 50.4) * mm, "end": v(-53.97, 50.4) * mm});
            skLineSegment(sketch, "E711", {"start": v(-53.97, 50.4) * mm, "end": v(-54.85, 50.4) * mm});
            skLineSegment(sketch, "E712", {"start": v(-54.85, 50.4) * mm, "end": v(-55.73, 50.4) * mm});
            skLineSegment(sketch, "E713", {"start": v(-55.73, 50.4) * mm, "end": v(-56.6, 50.4) * mm});
            skLineSegment(sketch, "E714", {"start": v(-56.6, 50.4) * mm, "end": v(-57.49, 50.4) * mm});
            skLineSegment(sketch, "E715", {"start": v(-57.49, 50.4) * mm, "end": v(-58.37, 50.4) * mm});
            skLineSegment(sketch, "E716", {"start": v(-58.37, 50.4) * mm, "end": v(-59.25, 50.4) * mm});
            skLineSegment(sketch, "E717", {"start": v(-59.25, 50.4) * mm, "end": v(-60.12, 50.4) * mm});
            skLineSegment(sketch, "E718", {"start": v(-60.12, 50.4) * mm, "end": v(-61, 50.4) * mm});
            skLineSegment(sketch, "E719", {"start": v(-61, 50.4) * mm, "end": v(-61.88, 50.4) * mm});
            skLineSegment(sketch, "E720", {"start": v(-61.88, 50.4) * mm, "end": v(-62.76, 50.4) * mm});
            skLineSegment(sketch, "E721", {"start": v(-62.76, 50.4) * mm, "end": v(-63.64, 50.4) * mm});
            skLineSegment(sketch, "E722", {"start": v(-63.64, 50.4) * mm, "end": v(-64.52, 50.4) * mm});
            skLineSegment(sketch, "E723", {"start": v(-64.52, 50.4) * mm, "end": v(-65.4, 50.4) * mm});
            skLineSegment(sketch, "E724", {"start": v(-65.4, 50.4) * mm, "end": v(-66.28, 50.4) * mm});
            skLineSegment(sketch, "E725", {"start": v(-66.28, 50.4) * mm, "end": v(-66.28, 48.28) * mm});
            skLineSegment(sketch, "E726", {"start": v(-66.28, 48.28) * mm, "end": v(-66.28, 46.16) * mm});
            skLineSegment(sketch, "E727", {"start": v(-66.28, 46.16) * mm, "end": v(-66.28, 44.04) * mm});
            skLineSegment(sketch, "E728", {"start": v(-66.28, 44.04) * mm, "end": v(-66.28, 41.91) * mm});
            skLineSegment(sketch, "E729", {"start": v(-66.28, 41.91) * mm, "end": v(-66.28, 39.8) * mm});
            skLineSegment(sketch, "E730", {"start": v(-66.28, 39.8) * mm, "end": v(-66.28, 37.67) * mm});
            skLineSegment(sketch, "E731", {"start": v(-66.28, 37.67) * mm, "end": v(-66.28, 35.55) * mm});
            skLineSegment(sketch, "E732", {"start": v(-66.28, 35.55) * mm, "end": v(-66.28, 33.42) * mm});
            skLineSegment(sketch, "E733", {"start": v(-66.28, 33.42) * mm, "end": v(-66.28, 31.3) * mm});
            skLineSegment(sketch, "E734", {"start": v(-66.28, 31.3) * mm, "end": v(-66.28, 29.18) * mm});
            skLineSegment(sketch, "E735", {"start": v(-66.28, 29.18) * mm, "end": v(-66.28, 27.05) * mm});
            skLineSegment(sketch, "E736", {"start": v(-66.28, 27.05) * mm, "end": v(-66.28, 24.93) * mm});
            skLineSegment(sketch, "E737", {"start": v(-66.28, 24.93) * mm, "end": v(-66.28, 22.8) * mm});
            skLineSegment(sketch, "E738", {"start": v(-66.28, 22.8) * mm, "end": v(-66.28, 20.69) * mm});
            skLineSegment(sketch, "E739", {"start": v(-66.28, 20.69) * mm, "end": v(-66.28, 18.56) * mm});
            skLineSegment(sketch, "E740", {"start": v(-66.28, 18.56) * mm, "end": v(-66.28, 16.44) * mm});
            skLineSegment(sketch, "E741", {"start": v(-66.28, 16.44) * mm, "end": v(-65.38, 16.44) * mm});
            skLineSegment(sketch, "E742", {"start": v(-65.38, 16.44) * mm, "end": v(-64.48, 16.44) * mm});
            skLineSegment(sketch, "E743", {"start": v(-64.48, 16.44) * mm, "end": v(-63.58, 16.44) * mm});
            skLineSegment(sketch, "E744", {"start": v(-63.58, 16.44) * mm, "end": v(-62.69, 16.44) * mm});
            skLineSegment(sketch, "E745", {"start": v(-62.69, 16.44) * mm, "end": v(-61.79, 16.44) * mm});
            skLineSegment(sketch, "E746", {"start": v(-61.79, 16.44) * mm, "end": v(-60.89, 16.44) * mm});
            skLineSegment(sketch, "E747", {"start": v(-60.89, 16.44) * mm, "end": v(-59.99, 16.44) * mm});
            skLineSegment(sketch, "E748", {"start": v(-59.99, 16.44) * mm, "end": v(-59.1, 16.44) * mm});
            skLineSegment(sketch, "E749", {"start": v(-59.1, 16.44) * mm, "end": v(-58.2, 16.44) * mm});
            skLineSegment(sketch, "E750", {"start": v(-58.2, 16.44) * mm, "end": v(-57.5, 16.44) * mm});
            skLineSegment(sketch, "E751", {"start": v(-57.5, 16.44) * mm, "end": v(-57.7, 15.64) * mm});
            skLineSegment(sketch, "E752", {"start": v(-57.7, 15.64) * mm, "end": v(-58.03, 14.4) * mm});
            skLineSegment(sketch, "E753", {"start": v(-58.03, 14.4) * mm, "end": v(-58.36, 13.15) * mm});
            skLineSegment(sketch, "E754", {"start": v(-58.36, 13.15) * mm, "end": v(-58.69, 11.91) * mm});
            skLineSegment(sketch, "E755", {"start": v(-58.69, 11.91) * mm, "end": v(-59.01, 10.67) * mm});
            skLineSegment(sketch, "E756", {"start": v(-59.01, 10.67) * mm, "end": v(-59.34, 9.43) * mm});
            skLineSegment(sketch, "E757", {"start": v(-59.34, 9.43) * mm, "end": v(-59.67, 8.2) * mm});
            skLineSegment(sketch, "E758", {"start": v(-59.67, 8.2) * mm, "end": v(-60, 6.95) * mm});
            skLineSegment(sketch, "E759", {"start": v(-60, 6.95) * mm, "end": v(-60.32, 5.71) * mm});
            skLineSegment(sketch, "E760", {"start": v(-60.32, 5.71) * mm, "end": v(-60.65, 4.47) * mm});
            skLineSegment(sketch, "E761", {"start": v(-60.65, 4.47) * mm, "end": v(-60.98, 3.23) * mm});
            skLineSegment(sketch, "E762", {"start": v(-60.98, 3.23) * mm, "end": v(-61.3, 1.99) * mm});
            skLineSegment(sketch, "E763", {"start": v(-61.3, 1.99) * mm, "end": v(-61.63, 0.75) * mm});
            skLineSegment(sketch, "E764", {"start": v(-61.63, 0.75) * mm, "end": v(-61.96, -0.5) * mm});
            skLineSegment(sketch, "E765", {"start": v(-61.96, -0.5) * mm, "end": v(-62.29, -1.73) * mm});
            skLineSegment(sketch, "E766", {"start": v(-62.29, -1.73) * mm, "end": v(-62.61, -2.97) * mm});
            skLineSegment(sketch, "E767", {"start": v(-62.61, -2.97) * mm, "end": v(-62.64, -3.07) * mm});
            skLineSegment(sketch, "E768", {"start": v(-62.64, -3.07) * mm, "end": v(-62.67, -3.17) * mm});
            skLineSegment(sketch, "E769", {"start": v(-62.67, -3.17) * mm, "end": v(-62.7, -3.27) * mm});
            skLineSegment(sketch, "E770", {"start": v(-62.7, -3.27) * mm, "end": v(-62.72, -3.39) * mm});
            skLineSegment(sketch, "E771", {"start": v(-62.72, -3.39) * mm, "end": v(-62.75, -3.5) * mm});
            skLineSegment(sketch, "E772", {"start": v(-62.75, -3.5) * mm, "end": v(-62.78, -3.63) * mm});
            skLineSegment(sketch, "E773", {"start": v(-62.78, -3.63) * mm, "end": v(-62.8, -3.76) * mm});
            skLineSegment(sketch, "E774", {"start": v(-62.8, -3.76) * mm, "end": v(-62.83, -3.9) * mm});
            skLineSegment(sketch, "E775", {"start": v(-62.83, -3.9) * mm, "end": v(-62.86, -4.03) * mm});
            skLineSegment(sketch, "E776", {"start": v(-62.86, -4.03) * mm, "end": v(-62.89, -4.18) * mm});
            skLineSegment(sketch, "E777", {"start": v(-62.89, -4.18) * mm, "end": v(-62.92, -4.33) * mm});
            skLineSegment(sketch, "E778", {"start": v(-62.92, -4.33) * mm, "end": v(-62.95, -4.5) * mm});
            skLineSegment(sketch, "E779", {"start": v(-62.95, -4.5) * mm, "end": v(-62.97, -4.66) * mm});
            skLineSegment(sketch, "E780", {"start": v(-62.97, -4.66) * mm, "end": v(-63, -4.83) * mm});
            skLineSegment(sketch, "E781", {"start": v(-63, -4.83) * mm, "end": v(-63.03, -5) * mm});
            skLineSegment(sketch, "E782", {"start": v(-63.03, -5) * mm, "end": v(-63.06, -5.19) * mm});
            skLineSegment(sketch, "E783", {"start": v(-63.06, -5.19) * mm, "end": v(-63.1, -5.37) * mm});
            skLineSegment(sketch, "E784", {"start": v(-63.1, -5.37) * mm, "end": v(-63.12, -5.54) * mm});
            skLineSegment(sketch, "E785", {"start": v(-63.12, -5.54) * mm, "end": v(-63.14, -5.71) * mm});
            skLineSegment(sketch, "E786", {"start": v(-63.14, -5.71) * mm, "end": v(-63.17, -5.87) * mm});
            skLineSegment(sketch, "E787", {"start": v(-63.17, -5.87) * mm, "end": v(-63.2, -6.03) * mm});
            skLineSegment(sketch, "E788", {"start": v(-63.2, -6.03) * mm, "end": v(-63.21, -6.18) * mm});
            skLineSegment(sketch, "E789", {"start": v(-63.21, -6.18) * mm, "end": v(-63.23, -6.32) * mm});
            skLineSegment(sketch, "E790", {"start": v(-63.23, -6.32) * mm, "end": v(-63.25, -6.45) * mm});
            skLineSegment(sketch, "E791", {"start": v(-63.25, -6.45) * mm, "end": v(-63.27, -6.58) * mm});
            skLineSegment(sketch, "E792", {"start": v(-63.27, -6.58) * mm, "end": v(-63.28, -6.7) * mm});
            skLineSegment(sketch, "E793", {"start": v(-63.28, -6.7) * mm, "end": v(-63.3, -6.81) * mm});
            skLineSegment(sketch, "E794", {"start": v(-63.3, -6.81) * mm, "end": v(-63.31, -6.92) * mm});
            skLineSegment(sketch, "E795", {"start": v(-63.31, -6.92) * mm, "end": v(-63.32, -7.02) * mm});
            skLineSegment(sketch, "E796", {"start": v(-63.32, -7.02) * mm, "end": v(-63.33, -7.12) * mm});
            skLineSegment(sketch, "E797", {"start": v(-63.33, -7.12) * mm, "end": v(-63.34, -7.2) * mm});
            skLineSegment(sketch, "E798", {"start": v(-63.34, -7.2) * mm, "end": v(-63.35, -7.28) * mm});
            skLineSegment(sketch, "E799", {"start": v(-63.35, -7.28) * mm, "end": v(-63.36, -7.28) * mm});
            skLineSegment(sketch, "E800", {"start": v(-63.36, -7.28) * mm, "end": v(-63.36, -7.28) * mm});
            skLineSegment(sketch, "E801", {"start": v(-63.36, -7.28) * mm, "end": v(-63.37, -7.28) * mm});
            skLineSegment(sketch, "E802", {"start": v(-63.37, -7.28) * mm, "end": v(-63.38, -7.28) * mm});
            skLineSegment(sketch, "E803", {"start": v(-63.38, -7.28) * mm, "end": v(-63.4, -7.28) * mm});
            skLineSegment(sketch, "E804", {"start": v(-63.4, -7.28) * mm, "end": v(-63.4, -7.28) * mm});
            skLineSegment(sketch, "E805", {"start": v(-63.4, -7.28) * mm, "end": v(-63.42, -7.28) * mm});
            skLineSegment(sketch, "E806", {"start": v(-63.42, -7.28) * mm, "end": v(-63.43, -7.28) * mm});
            skLineSegment(sketch, "E807", {"start": v(-63.43, -7.28) * mm, "end": v(-63.44, -7.28) * mm});
            skLineSegment(sketch, "E808", {"start": v(-63.44, -7.28) * mm, "end": v(-63.44, -7.28) * mm});
            skLineSegment(sketch, "E809", {"start": v(-63.44, -7.28) * mm, "end": v(-63.45, -7.28) * mm});
            skLineSegment(sketch, "E810", {"start": v(-63.45, -7.28) * mm, "end": v(-63.46, -7.28) * mm});
            skLineSegment(sketch, "E811", {"start": v(-63.46, -7.28) * mm, "end": v(-63.47, -7.28) * mm});
            skLineSegment(sketch, "E812", {"start": v(-63.47, -7.28) * mm, "end": v(-63.48, -7.28) * mm});
            skLineSegment(sketch, "E813", {"start": v(-63.48, -7.28) * mm, "end": v(-63.49, -7.28) * mm});
            skLineSegment(sketch, "E814", {"start": v(-63.49, -7.28) * mm, "end": v(-63.5, -7.16) * mm});
            skLineSegment(sketch, "E815", {"start": v(-63.5, -7.16) * mm, "end": v(-63.5, -7.04) * mm});
            skLineSegment(sketch, "E816", {"start": v(-63.5, -7.04) * mm, "end": v(-63.52, -6.91) * mm});
            skLineSegment(sketch, "E817", {"start": v(-63.52, -6.91) * mm, "end": v(-63.52, -6.8) * mm});
            skLineSegment(sketch, "E818", {"start": v(-63.52, -6.8) * mm, "end": v(-63.53, -6.67) * mm});
            skLineSegment(sketch, "E819", {"start": v(-63.53, -6.67) * mm, "end": v(-63.54, -6.55) * mm});
            skLineSegment(sketch, "E820", {"start": v(-63.54, -6.55) * mm, "end": v(-63.55, -6.42) * mm});
            skLineSegment(sketch, "E821", {"start": v(-63.55, -6.42) * mm, "end": v(-63.56, -6.3) * mm});
            skLineSegment(sketch, "E822", {"start": v(-63.56, -6.3) * mm, "end": v(-63.57, -6.18) * mm});
            skLineSegment(sketch, "E823", {"start": v(-63.57, -6.18) * mm, "end": v(-63.58, -6.05) * mm});
            skLineSegment(sketch, "E824", {"start": v(-63.58, -6.05) * mm, "end": v(-63.59, -5.93) * mm});
            skLineSegment(sketch, "E825", {"start": v(-63.59, -5.93) * mm, "end": v(-63.6, -5.8) * mm});
            skLineSegment(sketch, "E826", {"start": v(-63.6, -5.8) * mm, "end": v(-63.6, -5.69) * mm});
            skLineSegment(sketch, "E827", {"start": v(-63.6, -5.69) * mm, "end": v(-63.61, -5.56) * mm});
            skLineSegment(sketch, "E828", {"start": v(-63.61, -5.56) * mm, "end": v(-63.62, -5.44) * mm});
            skLineSegment(sketch, "E829", {"start": v(-63.62, -5.44) * mm, "end": v(-63.63, -5.32) * mm});
            skLineSegment(sketch, "E830", {"start": v(-63.63, -5.32) * mm, "end": v(-63.65, -5.1) * mm});
            skLineSegment(sketch, "E831", {"start": v(-63.65, -5.1) * mm, "end": v(-63.67, -4.88) * mm});
            skLineSegment(sketch, "E832", {"start": v(-63.67, -4.88) * mm, "end": v(-63.68, -4.68) * mm});
            skLineSegment(sketch, "E833", {"start": v(-63.68, -4.68) * mm, "end": v(-63.7, -4.5) * mm});
            skLineSegment(sketch, "E834", {"start": v(-63.7, -4.5) * mm, "end": v(-63.71, -4.32) * mm});
            skLineSegment(sketch, "E835", {"start": v(-63.71, -4.32) * mm, "end": v(-63.73, -4.15) * mm});
            skLineSegment(sketch, "E836", {"start": v(-63.73, -4.15) * mm, "end": v(-63.74, -4) * mm});
            skLineSegment(sketch, "E837", {"start": v(-63.74, -4) * mm, "end": v(-63.76, -3.85) * mm});
            skLineSegment(sketch, "E838", {"start": v(-63.76, -3.85) * mm, "end": v(-63.77, -3.72) * mm});
            skLineSegment(sketch, "E839", {"start": v(-63.77, -3.72) * mm, "end": v(-63.78, -3.6) * mm});
            skLineSegment(sketch, "E840", {"start": v(-63.78, -3.6) * mm, "end": v(-63.8, -3.5) * mm});
            skLineSegment(sketch, "E841", {"start": v(-63.8, -3.5) * mm, "end": v(-63.8, -3.4) * mm});
            skLineSegment(sketch, "E842", {"start": v(-63.8, -3.4) * mm, "end": v(-63.81, -3.3) * mm});
            skLineSegment(sketch, "E843", {"start": v(-63.81, -3.3) * mm, "end": v(-63.83, -3.23) * mm});
            skLineSegment(sketch, "E844", {"start": v(-63.83, -3.23) * mm, "end": v(-63.83, -3.17) * mm});
            skLineSegment(sketch, "E845", {"start": v(-63.83, -3.17) * mm, "end": v(-63.84, -3.11) * mm});
            skLineSegment(sketch, "E846", {"start": v(-63.84, -3.11) * mm, "end": v(-64.02, -1.87) * mm});
            skLineSegment(sketch, "E847", {"start": v(-64.02, -1.87) * mm, "end": v(-64.2, -0.62) * mm});
            skLineSegment(sketch, "E848", {"start": v(-64.2, -0.62) * mm, "end": v(-64.38, 0.63) * mm});
            skLineSegment(sketch, "E849", {"start": v(-64.38, 0.63) * mm, "end": v(-64.55, 1.88) * mm});
            skLineSegment(sketch, "E850", {"start": v(-64.55, 1.88) * mm, "end": v(-64.73, 3.13) * mm});
            skLineSegment(sketch, "E851", {"start": v(-64.73, 3.13) * mm, "end": v(-64.9, 4.38) * mm});
            skLineSegment(sketch, "E852", {"start": v(-64.9, 4.38) * mm, "end": v(-65.09, 5.63) * mm});
            skLineSegment(sketch, "E853", {"start": v(-65.09, 5.63) * mm, "end": v(-65.27, 6.88) * mm});
            skLineSegment(sketch, "E854", {"start": v(-65.27, 6.88) * mm, "end": v(-65.44, 8.13) * mm});
            skLineSegment(sketch, "E855", {"start": v(-65.44, 8.13) * mm, "end": v(-65.62, 9.38) * mm});
            skLineSegment(sketch, "E856", {"start": v(-65.62, 9.38) * mm, "end": v(-65.8, 10.63) * mm});
            skLineSegment(sketch, "E857", {"start": v(-65.8, 10.63) * mm, "end": v(-65.98, 11.88) * mm});
            skLineSegment(sketch, "E858", {"start": v(-65.98, 11.88) * mm, "end": v(-66.15, 13.13) * mm});
            skLineSegment(sketch, "E859", {"start": v(-66.15, 13.13) * mm, "end": v(-66.33, 14.38) * mm});
            skLineSegment(sketch, "E860", {"start": v(-66.33, 14.38) * mm, "end": v(-66.5, 15.63) * mm});
            skLineSegment(sketch, "E861", {"start": v(-66.5, 15.63) * mm, "end": v(-66.69, 16.88) * mm});
            skLineSegment(sketch, "E862", {"start": v(-66.69, 16.88) * mm, "end": v(-67.39, 16.88) * mm});
            skLineSegment(sketch, "E863", {"start": v(-67.39, 16.88) * mm, "end": v(-68.09, 16.88) * mm});
            skLineSegment(sketch, "E864", {"start": v(-68.09, 16.88) * mm, "end": v(-68.8, 16.88) * mm});
            skLineSegment(sketch, "E865", {"start": v(-68.8, 16.88) * mm, "end": v(-69.5, 16.88) * mm});
            skLineSegment(sketch, "E866", {"start": v(-69.5, 16.88) * mm, "end": v(-70.2, 16.88) * mm});
            skLineSegment(sketch, "E867", {"start": v(-70.2, 16.88) * mm, "end": v(-70.9, 16.88) * mm});
            skLineSegment(sketch, "E868", {"start": v(-70.9, 16.88) * mm, "end": v(-71.6, 16.88) * mm});
            skLineSegment(sketch, "E869", {"start": v(-71.6, 16.88) * mm, "end": v(-72.3, 16.88) * mm});
            skLineSegment(sketch, "E870", {"start": v(-72.3, 16.88) * mm, "end": v(-73, 16.88) * mm});
            skLineSegment(sketch, "E871", {"start": v(-73, 16.88) * mm, "end": v(-73.7, 16.88) * mm});
            skLineSegment(sketch, "E872", {"start": v(-73.7, 16.88) * mm, "end": v(-74.4, 16.88) * mm});
            skLineSegment(sketch, "E873", {"start": v(-74.4, 16.88) * mm, "end": v(-75.1, 16.88) * mm});
            skLineSegment(sketch, "E874", {"start": v(-75.1, 16.88) * mm, "end": v(-75.8, 16.88) * mm});
            skLineSegment(sketch, "E875", {"start": v(-75.8, 16.88) * mm, "end": v(-76.5, 16.88) * mm});
            skLineSegment(sketch, "E876", {"start": v(-76.5, 16.88) * mm, "end": v(-77.21, 16.88) * mm});
            skLineSegment(sketch, "E877", {"start": v(-77.21, 16.88) * mm, "end": v(-77.91, 16.88) * mm});
            skLineSegment(sketch, "E878", {"start": v(-77.91, 16.88) * mm, "end": v(-77.4, 14.75) * mm});
            skLineSegment(sketch, "E879", {"start": v(-77.4, 14.75) * mm, "end": v(-76.9, 12.63) * mm});
            skLineSegment(sketch, "E880", {"start": v(-76.9, 12.63) * mm, "end": v(-76.4, 10.5) * mm});
            skLineSegment(sketch, "E881", {"start": v(-76.4, 10.5) * mm, "end": v(-75.89, 8.38) * mm});
            skLineSegment(sketch, "E882", {"start": v(-75.89, 8.38) * mm, "end": v(-75.38, 6.26) * mm});
            skLineSegment(sketch, "E883", {"start": v(-75.38, 6.26) * mm, "end": v(-74.88, 4.14) * mm});
            skLineSegment(sketch, "E884", {"start": v(-74.88, 4.14) * mm, "end": v(-74.37, 2.02) * mm});
            skLineSegment(sketch, "E885", {"start": v(-74.37, 2.02) * mm, "end": v(-73.86, -0.1) * mm});
            skLineSegment(sketch, "E886", {"start": v(-73.86, -0.1) * mm, "end": v(-73.36, -2.23) * mm});
            skLineSegment(sketch, "E887", {"start": v(-73.36, -2.23) * mm, "end": v(-72.85, -4.35) * mm});
            skLineSegment(sketch, "E888", {"start": v(-72.85, -4.35) * mm, "end": v(-72.34, -6.47) * mm});
            skLineSegment(sketch, "E889", {"start": v(-72.34, -6.47) * mm, "end": v(-71.84, -8.6) * mm});
            skLineSegment(sketch, "E890", {"start": v(-71.84, -8.6) * mm, "end": v(-71.33, -10.72) * mm});
            skLineSegment(sketch, "E891", {"start": v(-71.33, -10.72) * mm, "end": v(-70.83, -12.84) * mm});
            skLineSegment(sketch, "E892", {"start": v(-70.83, -12.84) * mm, "end": v(-70.32, -14.97) * mm});
            skLineSegment(sketch, "E893", {"start": v(-70.32, -14.97) * mm, "end": v(-69.92, -16.65) * mm});
            skLineSegment(sketch, "E894", {"start": v(-69.92, -16.65) * mm, "end": v(-70.17, -16.65) * mm});
            skLineSegment(sketch, "E895", {"start": v(-70.17, -16.65) * mm, "end": v(-70.17, -18.78) * mm});
            skLineSegment(sketch, "E896", {"start": v(-70.17, -18.78) * mm, "end": v(-70.17, -20.9) * mm});
            skLineSegment(sketch, "E897", {"start": v(-70.17, -20.9) * mm, "end": v(-70.17, -23.02) * mm});
            skLineSegment(sketch, "E898", {"start": v(-70.17, -23.02) * mm, "end": v(-70.17, -25.14) * mm});
            skLineSegment(sketch, "E899", {"start": v(-70.17, -25.14) * mm, "end": v(-70.17, -27.27) * mm});
            skLineSegment(sketch, "E900", {"start": v(-70.17, -27.27) * mm, "end": v(-70.17, -29.4) * mm});
            skLineSegment(sketch, "E901", {"start": v(-70.17, -29.4) * mm, "end": v(-70.17, -31.51) * mm});
            skLineSegment(sketch, "E902", {"start": v(-70.17, -31.51) * mm, "end": v(-70.17, -33.64) * mm});
            skLineSegment(sketch, "E903", {"start": v(-70.17, -33.64) * mm, "end": v(-70.17, -35.76) * mm});
            skLineSegment(sketch, "E904", {"start": v(-70.17, -35.76) * mm, "end": v(-70.17, -37.88) * mm});
            skLineSegment(sketch, "E905", {"start": v(-70.17, -37.88) * mm, "end": v(-70.17, -40) * mm});
            skLineSegment(sketch, "E906", {"start": v(-70.17, -40) * mm, "end": v(-70.17, -41.95) * mm});
            skLineSegment(sketch, "E907", {"start": v(-70.17, -41.95) * mm, "end": v(-70.8, -40) * mm});
            skLineSegment(sketch, "E908", {"start": v(-70.8, -40) * mm, "end": v(-71.49, -37.88) * mm});
            skLineSegment(sketch, "E909", {"start": v(-71.49, -37.88) * mm, "end": v(-72.18, -35.76) * mm});
            skLineSegment(sketch, "E910", {"start": v(-72.18, -35.76) * mm, "end": v(-72.86, -33.64) * mm});
            skLineSegment(sketch, "E911", {"start": v(-72.86, -33.64) * mm, "end": v(-73.55, -31.51) * mm});
            skLineSegment(sketch, "E912", {"start": v(-73.55, -31.51) * mm, "end": v(-74.24, -29.4) * mm});
            skLineSegment(sketch, "E913", {"start": v(-74.24, -29.4) * mm, "end": v(-74.93, -27.27) * mm});
            skLineSegment(sketch, "E914", {"start": v(-74.93, -27.27) * mm, "end": v(-75.62, -25.14) * mm});
            skLineSegment(sketch, "E915", {"start": v(-75.62, -25.14) * mm, "end": v(-76.3, -23.02) * mm});
            skLineSegment(sketch, "E916", {"start": v(-76.3, -23.02) * mm, "end": v(-77, -20.9) * mm});
            skLineSegment(sketch, "E917", {"start": v(-77, -20.9) * mm, "end": v(-77.68, -18.78) * mm});
            skLineSegment(sketch, "E918", {"start": v(-77.68, -18.78) * mm, "end": v(-78.37, -16.65) * mm});
            skLineSegment(sketch, "E919", {"start": v(-78.37, -16.65) * mm, "end": v(-79.16, -16.65) * mm});
            skLineSegment(sketch, "E920", {"start": v(-79.16, -16.65) * mm, "end": v(-79.96, -16.65) * mm});
            skLineSegment(sketch, "E921", {"start": v(-79.96, -16.65) * mm, "end": v(-80.75, -16.65) * mm});
            skLineSegment(sketch, "E922", {"start": v(-80.75, -16.65) * mm, "end": v(-81.55, -16.65) * mm});
            skLineSegment(sketch, "E923", {"start": v(-81.55, -16.65) * mm, "end": v(-82.34, -16.65) * mm});
            skLineSegment(sketch, "E924", {"start": v(-82.34, -16.65) * mm, "end": v(-83.13, -16.65) * mm});
            skLineSegment(sketch, "E925", {"start": v(-83.13, -16.65) * mm, "end": v(-83.93, -16.65) * mm});
            skLineSegment(sketch, "E926", {"start": v(-83.93, -16.65) * mm, "end": v(-84.72, -16.65) * mm});
            skLineSegment(sketch, "E927", {"start": v(-84.72, -16.65) * mm, "end": v(-85.51, -16.65) * mm});
            skLineSegment(sketch, "E928", {"start": v(-85.51, -16.65) * mm, "end": v(-86.3, -16.65) * mm});
            skLineSegment(sketch, "E929", {"start": v(-86.3, -16.65) * mm, "end": v(-87.1, -16.65) * mm});
            skLineSegment(sketch, "E930", {"start": v(-87.1, -16.65) * mm, "end": v(-87.9, -16.65) * mm});
            skLineSegment(sketch, "E931", {"start": v(-87.9, -16.65) * mm, "end": v(-88.69, -16.65) * mm});
            skLineSegment(sketch, "E932", {"start": v(-88.69, -16.65) * mm, "end": v(-89.48, -16.65) * mm});
            skLineSegment(sketch, "E933", {"start": v(-89.48, -16.65) * mm, "end": v(-90.27, -16.65) * mm});
            skLineSegment(sketch, "E934", {"start": v(-90.27, -16.65) * mm, "end": v(-91.07, -16.65) * mm});
            skLineSegment(sketch, "E935", {"start": v(-91.07, -16.65) * mm, "end": v(-91.8, -18.78) * mm});
            skLineSegment(sketch, "E936", {"start": v(-91.8, -18.78) * mm, "end": v(-92.53, -20.9) * mm});
            skLineSegment(sketch, "E937", {"start": v(-92.53, -20.9) * mm, "end": v(-93.26, -23.02) * mm});
            skLineSegment(sketch, "E938", {"start": v(-93.26, -23.02) * mm, "end": v(-94, -25.14) * mm});
            skLineSegment(sketch, "E939", {"start": v(-94, -25.14) * mm, "end": v(-94.72, -27.27) * mm});
            skLineSegment(sketch, "E940", {"start": v(-94.72, -27.27) * mm, "end": v(-95.45, -29.4) * mm});
            skLineSegment(sketch, "E941", {"start": v(-95.45, -29.4) * mm, "end": v(-96.19, -31.51) * mm});
            skLineSegment(sketch, "E942", {"start": v(-96.19, -31.51) * mm, "end": v(-96.92, -33.64) * mm});
            skLineSegment(sketch, "E943", {"start": v(-96.92, -33.64) * mm, "end": v(-97.65, -35.76) * mm});
            skLineSegment(sketch, "E944", {"start": v(-97.65, -35.76) * mm, "end": v(-98.38, -37.88) * mm});
            skLineSegment(sketch, "E945", {"start": v(-98.38, -37.88) * mm, "end": v(-99.11, -40) * mm});
            skLineSegment(sketch, "E946", {"start": v(-99.11, -40) * mm, "end": v(-99.84, -42.13) * mm});
            skLineSegment(sketch, "E947", {"start": v(-99.84, -42.13) * mm, "end": v(-100.57, -44.25) * mm});
            skLineSegment(sketch, "E948", {"start": v(-100.57, -44.25) * mm, "end": v(-101.3, -46.37) * mm});
            skLineSegment(sketch, "E949", {"start": v(-101.3, -46.37) * mm, "end": v(-102.04, -48.5) * mm});
            skLineSegment(sketch, "E950", {"start": v(-102.04, -48.5) * mm, "end": v(-102.77, -50.62) * mm});
            skLineSegment(sketch, "E951", {"start": v(-102.77, -50.62) * mm, "end": v(-102.08, -50.62) * mm});
            skLineSegment(sketch, "E952", {"start": v(-102.08, -50.62) * mm, "end": v(-101.38, -50.62) * mm});
            skLineSegment(sketch, "E953", {"start": v(-101.38, -50.62) * mm, "end": v(-100.7, -50.62) * mm});
            skLineSegment(sketch, "E954", {"start": v(-100.7, -50.62) * mm, "end": v(-100, -50.62) * mm});
            skLineSegment(sketch, "E955", {"start": v(-100, -50.62) * mm, "end": v(-99.31, -50.62) * mm});
            skLineSegment(sketch, "E956", {"start": v(-99.31, -50.62) * mm, "end": v(-98.62, -50.62) * mm});
            skLineSegment(sketch, "E957", {"start": v(-98.62, -50.62) * mm, "end": v(-97.93, -50.62) * mm});
            skLineSegment(sketch, "E958", {"start": v(-97.93, -50.62) * mm, "end": v(-97.24, -50.62) * mm});
            skLineSegment(sketch, "E959", {"start": v(-97.24, -50.62) * mm, "end": v(-96.55, -50.62) * mm});
            skLineSegment(sketch, "E960", {"start": v(-96.55, -50.62) * mm, "end": v(-95.85, -50.62) * mm});
            skLineSegment(sketch, "E961", {"start": v(-95.85, -50.62) * mm, "end": v(-95.16, -50.62) * mm});
            skLineSegment(sketch, "E962", {"start": v(-95.16, -50.62) * mm, "end": v(-94.47, -50.62) * mm});
            skLineSegment(sketch, "E963", {"start": v(-94.47, -50.62) * mm, "end": v(-93.78, -50.62) * mm});
            skLineSegment(sketch, "E964", {"start": v(-93.78, -50.62) * mm, "end": v(-93.09, -50.62) * mm});
            skLineSegment(sketch, "E965", {"start": v(-93.09, -50.62) * mm, "end": v(-92.4, -50.62) * mm});
            skLineSegment(sketch, "E966", {"start": v(-92.4, -50.62) * mm, "end": v(-91.7, -50.62) * mm});
            skLineSegment(sketch, "E967", {"start": v(-91.7, -50.62) * mm, "end": v(-91.6, -50.23) * mm});
            skLineSegment(sketch, "E968", {"start": v(-91.6, -50.23) * mm, "end": v(-91.5, -49.84) * mm});
            skLineSegment(sketch, "E969", {"start": v(-91.5, -49.84) * mm, "end": v(-91.4, -49.45) * mm});
            skLineSegment(sketch, "E970", {"start": v(-91.4, -49.45) * mm, "end": v(-91.3, -49.05) * mm});
            skLineSegment(sketch, "E971", {"start": v(-91.3, -49.05) * mm, "end": v(-91.2, -48.66) * mm});
            skLineSegment(sketch, "E972", {"start": v(-91.2, -48.66) * mm, "end": v(-91.1, -48.27) * mm});
            skLineSegment(sketch, "E973", {"start": v(-91.1, -48.27) * mm, "end": v(-91, -47.88) * mm});
            skLineSegment(sketch, "E974", {"start": v(-91, -47.88) * mm, "end": v(-90.9, -47.5) * mm});
            skLineSegment(sketch, "E975", {"start": v(-90.9, -47.5) * mm, "end": v(-90.8, -47.1) * mm});
            skLineSegment(sketch, "E976", {"start": v(-90.8, -47.1) * mm, "end": v(-90.7, -46.71) * mm});
            skLineSegment(sketch, "E977", {"start": v(-90.7, -46.71) * mm, "end": v(-90.6, -46.32) * mm});
            skLineSegment(sketch, "E978", {"start": v(-90.6, -46.32) * mm, "end": v(-90.5, -45.93) * mm});
            skLineSegment(sketch, "E979", {"start": v(-90.5, -45.93) * mm, "end": v(-90.4, -45.54) * mm});
            skLineSegment(sketch, "E980", {"start": v(-90.4, -45.54) * mm, "end": v(-90.3, -45.15) * mm});
            skLineSegment(sketch, "E981", {"start": v(-90.3, -45.15) * mm, "end": v(-90.2, -44.76) * mm});
            skLineSegment(sketch, "E982", {"start": v(-90.2, -44.76) * mm, "end": v(-90.1, -44.37) * mm});
            skLineSegment(sketch, "E983", {"start": v(-90.1, -44.37) * mm, "end": v(-89.46, -44.37) * mm});
            skLineSegment(sketch, "E984", {"start": v(-89.46, -44.37) * mm, "end": v(-88.83, -44.37) * mm});
            skLineSegment(sketch, "E985", {"start": v(-88.83, -44.37) * mm, "end": v(-88.2, -44.37) * mm});
            skLineSegment(sketch, "E986", {"start": v(-88.2, -44.37) * mm, "end": v(-87.56, -44.37) * mm});
            skLineSegment(sketch, "E987", {"start": v(-87.56, -44.37) * mm, "end": v(-86.93, -44.37) * mm});
            skLineSegment(sketch, "E988", {"start": v(-86.93, -44.37) * mm, "end": v(-86.3, -44.37) * mm});
            skLineSegment(sketch, "E989", {"start": v(-86.3, -44.37) * mm, "end": v(-85.66, -44.37) * mm});
            skLineSegment(sketch, "E990", {"start": v(-85.66, -44.37) * mm, "end": v(-85.03, -44.37) * mm});
            skLineSegment(sketch, "E991", {"start": v(-85.03, -44.37) * mm, "end": v(-84.4, -44.37) * mm});
            skLineSegment(sketch, "E992", {"start": v(-84.4, -44.37) * mm, "end": v(-83.76, -44.37) * mm});
            skLineSegment(sketch, "E993", {"start": v(-83.76, -44.37) * mm, "end": v(-83.13, -44.37) * mm});
            skLineSegment(sketch, "E994", {"start": v(-83.13, -44.37) * mm, "end": v(-82.5, -44.37) * mm});
            skLineSegment(sketch, "E995", {"start": v(-82.5, -44.37) * mm, "end": v(-81.86, -44.37) * mm});
            skLineSegment(sketch, "E996", {"start": v(-81.86, -44.37) * mm, "end": v(-81.23, -44.37) * mm});
            skLineSegment(sketch, "E997", {"start": v(-81.23, -44.37) * mm, "end": v(-80.6, -44.37) * mm});
            skLineSegment(sketch, "E998", {"start": v(-80.6, -44.37) * mm, "end": v(-79.96, -44.37) * mm});
            skLineSegment(sketch, "E999", {"start": v(-79.96, -44.37) * mm, "end": v(-79.87, -44.76) * mm});
            skLineSegment(sketch, "E1000", {"start": v(-79.87, -44.76) * mm, "end": v(-79.77, -45.15) * mm});
            skLineSegment(sketch, "E1001", {"start": v(-79.77, -45.15) * mm, "end": v(-79.68, -45.54) * mm});
            skLineSegment(sketch, "E1002", {"start": v(-79.68, -45.54) * mm, "end": v(-79.59, -45.93) * mm});
            skLineSegment(sketch, "E1003", {"start": v(-79.59, -45.93) * mm, "end": v(-79.5, -46.32) * mm});
            skLineSegment(sketch, "E1004", {"start": v(-79.5, -46.32) * mm, "end": v(-79.4, -46.71) * mm});
            skLineSegment(sketch, "E1005", {"start": v(-79.4, -46.71) * mm, "end": v(-79.3, -47.1) * mm});
            skLineSegment(sketch, "E1006", {"start": v(-79.3, -47.1) * mm, "end": v(-79.21, -47.5) * mm});
            skLineSegment(sketch, "E1007", {"start": v(-79.21, -47.5) * mm, "end": v(-79.12, -47.88) * mm});
            skLineSegment(sketch, "E1008", {"start": v(-79.12, -47.88) * mm, "end": v(-79.03, -48.27) * mm});
            skLineSegment(sketch, "E1009", {"start": v(-79.03, -48.27) * mm, "end": v(-78.93, -48.66) * mm});
            skLineSegment(sketch, "E1010", {"start": v(-78.93, -48.66) * mm, "end": v(-78.84, -49.05) * mm});
            skLineSegment(sketch, "E1011", {"start": v(-78.84, -49.05) * mm, "end": v(-78.75, -49.45) * mm});
            skLineSegment(sketch, "E1012", {"start": v(-78.75, -49.45) * mm, "end": v(-78.65, -49.84) * mm});
            skLineSegment(sketch, "E1013", {"start": v(-78.65, -49.84) * mm, "end": v(-78.56, -50.23) * mm});
            skLineSegment(sketch, "E1014", {"start": v(-78.56, -50.23) * mm, "end": v(-78.47, -50.62) * mm});
            skLineSegment(sketch, "E1015", {"start": v(-78.47, -50.62) * mm, "end": v(-77.77, -50.62) * mm});
            skLineSegment(sketch, "E1016", {"start": v(-77.77, -50.62) * mm, "end": v(-77.08, -50.62) * mm});
            skLineSegment(sketch, "E1017", {"start": v(-77.08, -50.62) * mm, "end": v(-76.38, -50.62) * mm});
            skLineSegment(sketch, "E1018", {"start": v(-76.38, -50.62) * mm, "end": v(-75.69, -50.62) * mm});
            skLineSegment(sketch, "E1019", {"start": v(-75.69, -50.62) * mm, "end": v(-75, -50.62) * mm});
            skLineSegment(sketch, "E1020", {"start": v(-75, -50.62) * mm, "end": v(-74.3, -50.62) * mm});
            skLineSegment(sketch, "E1021", {"start": v(-74.3, -50.62) * mm, "end": v(-73.6, -50.62) * mm});
            skLineSegment(sketch, "E1022", {"start": v(-73.6, -50.62) * mm, "end": v(-72.91, -50.62) * mm});
            skLineSegment(sketch, "E1023", {"start": v(-72.91, -50.62) * mm, "end": v(-72.22, -50.62) * mm});
            skLineSegment(sketch, "E1024", {"start": v(-72.22, -50.62) * mm, "end": v(-71.52, -50.62) * mm});
            skLineSegment(sketch, "E1025", {"start": v(-71.52, -50.62) * mm, "end": v(-70.83, -50.62) * mm});
            skLineSegment(sketch, "E1026", {"start": v(-70.83, -50.62) * mm, "end": v(-70.17, -50.62) * mm});
            skLineSegment(sketch, "E1027", {"start": v(-70.17, -50.62) * mm, "end": v(-70.13, -50.62) * mm});
            skLineSegment(sketch, "E1028", {"start": v(-70.13, -50.62) * mm, "end": v(-69.44, -50.62) * mm});
            skLineSegment(sketch, "E1029", {"start": v(-69.44, -50.62) * mm, "end": v(-69.2, -50.62) * mm});
            skLineSegment(sketch, "E1030", {"start": v(-69.2, -50.62) * mm, "end": v(-68.75, -50.62) * mm});
            skLineSegment(sketch, "E1031", {"start": v(-68.75, -50.62) * mm, "end": v(-68.23, -50.62) * mm});
            skLineSegment(sketch, "E1032", {"start": v(-68.23, -50.62) * mm, "end": v(-68.05, -50.62) * mm});
            skLineSegment(sketch, "E1033", {"start": v(-68.05, -50.62) * mm, "end": v(-67.36, -50.62) * mm});
            skLineSegment(sketch, "E1034", {"start": v(-67.36, -50.62) * mm, "end": v(-67.27, -50.62) * mm});
            skLineSegment(sketch, "E1035", {"start": v(-67.27, -50.62) * mm, "end": v(-66.3, -50.62) * mm});
            skLineSegment(sketch, "E1036", {"start": v(-66.3, -50.62) * mm, "end": v(-65.33, -50.62) * mm});
            skLineSegment(sketch, "E1037", {"start": v(-65.33, -50.62) * mm, "end": v(-64.36, -50.62) * mm});
            skLineSegment(sketch, "E1038", {"start": v(-64.36, -50.62) * mm, "end": v(-63.4, -50.62) * mm});
            skLineSegment(sketch, "E1039", {"start": v(-63.4, -50.62) * mm, "end": v(-62.42, -50.62) * mm});
            skLineSegment(sketch, "E1040", {"start": v(-62.42, -50.62) * mm, "end": v(-61.46, -50.62) * mm});
            skLineSegment(sketch, "E1041", {"start": v(-61.46, -50.62) * mm, "end": v(-60.49, -50.62) * mm});
            skLineSegment(sketch, "E1042", {"start": v(-60.49, -50.62) * mm, "end": v(-59.52, -50.62) * mm});
            skLineSegment(sketch, "E1043", {"start": v(-59.52, -50.62) * mm, "end": v(-58.55, -50.62) * mm});
            skLineSegment(sketch, "E1044", {"start": v(-58.55, -50.62) * mm, "end": v(-57.58, -50.62) * mm});
            skLineSegment(sketch, "E1045", {"start": v(-57.58, -50.62) * mm, "end": v(-56.62, -50.62) * mm});
            skLineSegment(sketch, "E1046", {"start": v(-56.62, -50.62) * mm, "end": v(-55.65, -50.62) * mm});
            skLineSegment(sketch, "E1047", {"start": v(-55.65, -50.62) * mm, "end": v(-54.68, -50.62) * mm});
            skLineSegment(sketch, "E1048", {"start": v(-54.68, -50.62) * mm, "end": v(-53.88, -50.6) * mm});
            skLineSegment(sketch, "E1049", {"start": v(-53.88, -50.6) * mm, "end": v(-53.1, -50.58) * mm});
            skLineSegment(sketch, "E1050", {"start": v(-53.1, -50.58) * mm, "end": v(-52.34, -50.52) * mm});
            skLineSegment(sketch, "E1051", {"start": v(-52.34, -50.52) * mm, "end": v(-51.61, -50.45) * mm});
            skLineSegment(sketch, "E1052", {"start": v(-51.61, -50.45) * mm, "end": v(-50.9, -50.35) * mm});
            skLineSegment(sketch, "E1053", {"start": v(-50.9, -50.35) * mm, "end": v(-50.22, -50.24) * mm});
            skLineSegment(sketch, "E1054", {"start": v(-50.22, -50.24) * mm, "end": v(-49.56, -50.1) * mm});
            skLineSegment(sketch, "E1055", {"start": v(-49.56, -50.1) * mm, "end": v(-48.92, -49.94) * mm});
            skLineSegment(sketch, "E1056", {"start": v(-48.92, -49.94) * mm, "end": v(-48.3, -49.76) * mm});
            skLineSegment(sketch, "E1057", {"start": v(-48.3, -49.76) * mm, "end": v(-47.71, -49.56) * mm});
            skLineSegment(sketch, "E1058", {"start": v(-47.71, -49.56) * mm, "end": v(-47.15, -49.34) * mm});
            skLineSegment(sketch, "E1059", {"start": v(-47.15, -49.34) * mm, "end": v(-46.6, -49.1) * mm});
            skLineSegment(sketch, "E1060", {"start": v(-46.6, -49.1) * mm, "end": v(-46.08, -48.83) * mm});
            skLineSegment(sketch, "E1061", {"start": v(-46.08, -48.83) * mm, "end": v(-45.58, -48.54) * mm});
            skLineSegment(sketch, "E1062", {"start": v(-45.58, -48.54) * mm, "end": v(-45.11, -48.23) * mm});
            skLineSegment(sketch, "E1063", {"start": v(-45.11, -48.23) * mm, "end": v(-44.66, -47.9) * mm});
            skLineSegment(sketch, "E1064", {"start": v(-44.66, -47.9) * mm, "end": v(-44.24, -47.56) * mm});
            skLineSegment(sketch, "E1065", {"start": v(-44.24, -47.56) * mm, "end": v(-43.84, -47.2) * mm});
            skLineSegment(sketch, "E1066", {"start": v(-43.84, -47.2) * mm, "end": v(-43.47, -46.8) * mm});
            skLineSegment(sketch, "E1067", {"start": v(-43.47, -46.8) * mm, "end": v(-43.13, -46.4) * mm});
            skLineSegment(sketch, "E1068", {"start": v(-43.13, -46.4) * mm, "end": v(-42.81, -45.99) * mm});
            skLineSegment(sketch, "E1069", {"start": v(-42.81, -45.99) * mm, "end": v(-42.52, -45.55) * mm});
            skLineSegment(sketch, "E1070", {"start": v(-42.52, -45.55) * mm, "end": v(-42.26, -45.1) * mm});
            skLineSegment(sketch, "E1071", {"start": v(-42.26, -45.1) * mm, "end": v(-42.06, -44.68) * mm});
            skLineSegment(sketch, "E1072", {"start": v(-42.06, -44.68) * mm, "end": v(-41.96, -44.8) * mm});
            skLineSegment(sketch, "E1073", {"start": v(-41.96, -44.8) * mm, "end": v(-41.63, -45.23) * mm});
            skLineSegment(sketch, "E1074", {"start": v(-41.63, -45.23) * mm, "end": v(-41.28, -45.65) * mm});
            skLineSegment(sketch, "E1075", {"start": v(-41.28, -45.65) * mm, "end": v(-40.92, -46.05) * mm});
            skLineSegment(sketch, "E1076", {"start": v(-40.92, -46.05) * mm, "end": v(-40.55, -46.44) * mm});
            skLineSegment(sketch, "E1077", {"start": v(-40.55, -46.44) * mm, "end": v(-40.16, -46.81) * mm});
            skLineSegment(sketch, "E1078", {"start": v(-40.16, -46.81) * mm, "end": v(-39.76, -47.17) * mm});
            skLineSegment(sketch, "E1079", {"start": v(-39.76, -47.17) * mm, "end": v(-39.34, -47.52) * mm});
            skLineSegment(sketch, "E1080", {"start": v(-39.34, -47.52) * mm, "end": v(-38.91, -47.85) * mm});
            skLineSegment(sketch, "E1081", {"start": v(-38.91, -47.85) * mm, "end": v(-38.47, -48.17) * mm});
            skLineSegment(sketch, "E1082", {"start": v(-38.47, -48.17) * mm, "end": v(-38.02, -48.47) * mm});
            skLineSegment(sketch, "E1083", {"start": v(-38.02, -48.47) * mm, "end": v(-37.55, -48.77) * mm});
            skLineSegment(sketch, "E1084", {"start": v(-37.55, -48.77) * mm, "end": v(-37.06, -49.04) * mm});
            skLineSegment(sketch, "E1085", {"start": v(-37.06, -49.04) * mm, "end": v(-36.57, -49.3) * mm});
            skLineSegment(sketch, "E1086", {"start": v(-36.57, -49.3) * mm, "end": v(-36.07, -49.55) * mm});
            skLineSegment(sketch, "E1087", {"start": v(-36.07, -49.55) * mm, "end": v(-35.56, -49.78) * mm});
            skLineSegment(sketch, "E1088", {"start": v(-35.56, -49.78) * mm, "end": v(-35.05, -50) * mm});
            skLineSegment(sketch, "E1089", {"start": v(-35.05, -50) * mm, "end": v(-34.53, -50.19) * mm});
            skLineSegment(sketch, "E1090", {"start": v(-34.53, -50.19) * mm, "end": v(-34, -50.36) * mm});
            skLineSegment(sketch, "E1091", {"start": v(-34, -50.36) * mm, "end": v(-33.47, -50.52) * mm});
            skLineSegment(sketch, "E1092", {"start": v(-33.47, -50.52) * mm, "end": v(-32.93, -50.67) * mm});
            skLineSegment(sketch, "E1093", {"start": v(-32.93, -50.67) * mm, "end": v(-32.38, -50.8) * mm});
            skLineSegment(sketch, "E1094", {"start": v(-32.38, -50.8) * mm, "end": v(-31.83, -50.9) * mm});
            skLineSegment(sketch, "E1095", {"start": v(-31.83, -50.9) * mm, "end": v(-31.26, -51) * mm});
            skLineSegment(sketch, "E1096", {"start": v(-31.26, -51) * mm, "end": v(-30.7, -51.07) * mm});
            skLineSegment(sketch, "E1097", {"start": v(-30.7, -51.07) * mm, "end": v(-30.12, -51.13) * mm});
            skLineSegment(sketch, "E1098", {"start": v(-30.12, -51.13) * mm, "end": v(-29.54, -51.18) * mm});
            skLineSegment(sketch, "E1099", {"start": v(-29.54, -51.18) * mm, "end": v(-28.95, -51.2) * mm});
            skLineSegment(sketch, "E1100", {"start": v(-28.95, -51.2) * mm, "end": v(-28.36, -51.21) * mm});
            skLineSegment(sketch, "E1101", {"start": v(-28.36, -51.21) * mm, "end": v(-27.75, -51.2) * mm});
            skLineSegment(sketch, "E1102", {"start": v(-27.75, -51.2) * mm, "end": v(-27.15, -51.18) * mm});
            skLineSegment(sketch, "E1103", {"start": v(-27.15, -51.18) * mm, "end": v(-26.55, -51.13) * mm});
            skLineSegment(sketch, "E1104", {"start": v(-26.55, -51.13) * mm, "end": v(-25.97, -51.07) * mm});
            skLineSegment(sketch, "E1105", {"start": v(-25.97, -51.07) * mm, "end": v(-25.39, -51) * mm});
            skLineSegment(sketch, "E1106", {"start": v(-25.39, -51) * mm, "end": v(-24.82, -50.9) * mm});
            skLineSegment(sketch, "E1107", {"start": v(-24.82, -50.9) * mm, "end": v(-24.25, -50.78) * mm});
            skLineSegment(sketch, "E1108", {"start": v(-24.25, -50.78) * mm, "end": v(-23.7, -50.65) * mm});
            skLineSegment(sketch, "E1109", {"start": v(-23.7, -50.65) * mm, "end": v(-23.14, -50.5) * mm});
            skLineSegment(sketch, "E1110", {"start": v(-23.14, -50.5) * mm, "end": v(-22.6, -50.34) * mm});
            skLineSegment(sketch, "E1111", {"start": v(-22.6, -50.34) * mm, "end": v(-22.07, -50.15) * mm});
            skLineSegment(sketch, "E1112", {"start": v(-22.07, -50.15) * mm, "end": v(-21.54, -49.95) * mm});
            skLineSegment(sketch, "E1113", {"start": v(-21.54, -49.95) * mm, "end": v(-21.02, -49.73) * mm});
            skLineSegment(sketch, "E1114", {"start": v(-21.02, -49.73) * mm, "end": v(-20.5, -49.5) * mm});
            skLineSegment(sketch, "E1115", {"start": v(-20.5, -49.5) * mm, "end": v(-20, -49.24) * mm});
            skLineSegment(sketch, "E1116", {"start": v(-20, -49.24) * mm, "end": v(-19.5, -48.97) * mm});
            skLineSegment(sketch, "E1117", {"start": v(-19.5, -48.97) * mm, "end": v(-19.01, -48.69) * mm});
            skLineSegment(sketch, "E1118", {"start": v(-19.01, -48.69) * mm, "end": v(-18.54, -48.38) * mm});
            skLineSegment(sketch, "E1119", {"start": v(-18.54, -48.38) * mm, "end": v(-18.08, -48.07) * mm});
            skLineSegment(sketch, "E1120", {"start": v(-18.08, -48.07) * mm, "end": v(-17.63, -47.74) * mm});
            skLineSegment(sketch, "E1121", {"start": v(-17.63, -47.74) * mm, "end": v(-17.2, -47.4) * mm});
            skLineSegment(sketch, "E1122", {"start": v(-17.2, -47.4) * mm, "end": v(-16.78, -47.04) * mm});
            skLineSegment(sketch, "E1123", {"start": v(-16.78, -47.04) * mm, "end": v(-16.38, -46.67) * mm});
            skLineSegment(sketch, "E1124", {"start": v(-16.38, -46.67) * mm, "end": v(-15.98, -46.28) * mm});
            skLineSegment(sketch, "E1125", {"start": v(-15.98, -46.28) * mm, "end": v(-15.6, -45.88) * mm});
            skLineSegment(sketch, "E1126", {"start": v(-15.6, -45.88) * mm, "end": v(-15.24, -45.47) * mm});
            skLineSegment(sketch, "E1127", {"start": v(-15.24, -45.47) * mm, "end": v(-14.9, -45.04) * mm});
            skLineSegment(sketch, "E1128", {"start": v(-14.9, -45.04) * mm, "end": v(-14.55, -44.6) * mm});
            skLineSegment(sketch, "E1129", {"start": v(-14.55, -44.6) * mm, "end": v(-14.23, -44.15) * mm});
            skLineSegment(sketch, "E1130", {"start": v(-14.23, -44.15) * mm, "end": v(-13.92, -43.68) * mm});
            skLineSegment(sketch, "E1131", {"start": v(-13.92, -43.68) * mm, "end": v(-13.62, -43.2) * mm});
            skLineSegment(sketch, "E1132", {"start": v(-13.62, -43.2) * mm, "end": v(-13.34, -42.7) * mm});
            skLineSegment(sketch, "E1133", {"start": v(-13.34, -42.7) * mm, "end": v(-13.08, -42.19) * mm});
            skLineSegment(sketch, "E1134", {"start": v(-13.08, -42.19) * mm, "end": v(-12.83, -41.67) * mm});
            skLineSegment(sketch, "E1135", {"start": v(-12.83, -41.67) * mm, "end": v(-12.6, -41.14) * mm});
            skLineSegment(sketch, "E1136", {"start": v(-12.6, -41.14) * mm, "end": v(-12.38, -40.6) * mm});
            skLineSegment(sketch, "E1137", {"start": v(-12.38, -40.6) * mm, "end": v(-12.18, -40.07) * mm});
            skLineSegment(sketch, "E1138", {"start": v(-12.18, -40.07) * mm, "end": v(-12.15, -39.97) * mm});
            skLineSegment(sketch, "E1139", {"start": v(-12.15, -39.97) * mm, "end": v(-12, -40.72) * mm});
            skLineSegment(sketch, "E1140", {"start": v(-12, -40.72) * mm, "end": v(-11.81, -41.5) * mm});
            skLineSegment(sketch, "E1141", {"start": v(-11.81, -41.5) * mm, "end": v(-11.6, -42.27) * mm});
            skLineSegment(sketch, "E1142", {"start": v(-11.6, -42.27) * mm, "end": v(-11.34, -43) * mm});
            skLineSegment(sketch, "E1143", {"start": v(-11.34, -43) * mm, "end": v(-11.07, -43.7) * mm});
            skLineSegment(sketch, "E1144", {"start": v(-11.07, -43.7) * mm, "end": v(-10.76, -44.37) * mm});
            skLineSegment(sketch, "E1145", {"start": v(-10.76, -44.37) * mm, "end": v(-10.42, -45) * mm});
            skLineSegment(sketch, "E1146", {"start": v(-10.42, -45) * mm, "end": v(-10.05, -45.61) * mm});
            skLineSegment(sketch, "E1147", {"start": v(-10.05, -45.61) * mm, "end": v(-9.66, -46.19) * mm});
            skLineSegment(sketch, "E1148", {"start": v(-9.66, -46.19) * mm, "end": v(-9.23, -46.73) * mm});
            skLineSegment(sketch, "E1149", {"start": v(-9.23, -46.73) * mm, "end": v(-8.78, -47.24) * mm});
            skLineSegment(sketch, "E1150", {"start": v(-8.78, -47.24) * mm, "end": v(-8.3, -47.72) * mm});
            skLineSegment(sketch, "E1151", {"start": v(-8.3, -47.72) * mm, "end": v(-7.78, -48.17) * mm});
            skLineSegment(sketch, "E1152", {"start": v(-7.78, -48.17) * mm, "end": v(-7.25, -48.6) * mm});
            skLineSegment(sketch, "E1153", {"start": v(-7.25, -48.6) * mm, "end": v(-6.68, -48.98) * mm});
            skLineSegment(sketch, "E1154", {"start": v(-6.68, -48.98) * mm, "end": v(-6.1, -49.34) * mm});
            skLineSegment(sketch, "E1155", {"start": v(-6.1, -49.34) * mm, "end": v(-5.47, -49.66) * mm});
            skLineSegment(sketch, "E1156", {"start": v(-5.47, -49.66) * mm, "end": v(-4.82, -49.96) * mm});
            skLineSegment(sketch, "E1157", {"start": v(-4.82, -49.96) * mm, "end": v(-4.15, -50.22) * mm});
            skLineSegment(sketch, "E1158", {"start": v(-4.15, -50.22) * mm, "end": v(-3.45, -50.45) * mm});
            skLineSegment(sketch, "E1159", {"start": v(-3.45, -50.45) * mm, "end": v(-2.72, -50.65) * mm});
            skLineSegment(sketch, "E1160", {"start": v(-2.72, -50.65) * mm, "end": v(-1.96, -50.82) * mm});
            skLineSegment(sketch, "E1161", {"start": v(-1.96, -50.82) * mm, "end": v(-1.18, -50.96) * mm});
            skLineSegment(sketch, "E1162", {"start": v(-1.18, -50.96) * mm, "end": v(-0.37, -51.07) * mm});
            skLineSegment(sketch, "E1163", {"start": v(-0.37, -51.07) * mm, "end": v(0.47, -51.15) * mm});
            skLineSegment(sketch, "E1164", {"start": v(0.47, -51.15) * mm, "end": v(1.33, -51.2) * mm});
            skLineSegment(sketch, "E1165", {"start": v(1.33, -51.2) * mm, "end": v(2.22, -51.21) * mm});
            skLineSegment(sketch, "E1166", {"start": v(2.22, -51.21) * mm, "end": v(3.18, -51.2) * mm});
            skLineSegment(sketch, "E1167", {"start": v(3.18, -51.2) * mm, "end": v(4.1, -51.15) * mm});
            skLineSegment(sketch, "E1168", {"start": v(4.1, -51.15) * mm, "end": v(5, -51.07) * mm});
            skLineSegment(sketch, "E1169", {"start": v(5, -51.07) * mm, "end": v(5.86, -50.96) * mm});
            skLineSegment(sketch, "E1170", {"start": v(5.86, -50.96) * mm, "end": v(6.68, -50.82) * mm});
            skLineSegment(sketch, "E1171", {"start": v(6.68, -50.82) * mm, "end": v(7.48, -50.65) * mm});
            skLineSegment(sketch, "E1172", {"start": v(7.48, -50.65) * mm, "end": v(8.25, -50.45) * mm});
            skLineSegment(sketch, "E1173", {"start": v(8.25, -50.45) * mm, "end": v(8.98, -50.22) * mm});
            skLineSegment(sketch, "E1174", {"start": v(8.98, -50.22) * mm, "end": v(9.69, -49.96) * mm});
            skLineSegment(sketch, "E1175", {"start": v(9.69, -49.96) * mm, "end": v(10.36, -49.66) * mm});
            skLineSegment(sketch, "E1176", {"start": v(10.36, -49.66) * mm, "end": v(11, -49.34) * mm});
            skLineSegment(sketch, "E1177", {"start": v(11, -49.34) * mm, "end": v(11.6, -48.98) * mm});
            skLineSegment(sketch, "E1178", {"start": v(11.6, -48.98) * mm, "end": v(12.18, -48.6) * mm});
            skLineSegment(sketch, "E1179", {"start": v(12.18, -48.6) * mm, "end": v(12.73, -48.17) * mm});
            skLineSegment(sketch, "E1180", {"start": v(12.73, -48.17) * mm, "end": v(13.24, -47.72) * mm});
            skLineSegment(sketch, "E1181", {"start": v(13.24, -47.72) * mm, "end": v(13.72, -47.24) * mm});
            skLineSegment(sketch, "E1182", {"start": v(13.72, -47.24) * mm, "end": v(14.17, -46.73) * mm});
            skLineSegment(sketch, "E1183", {"start": v(14.17, -46.73) * mm, "end": v(14.6, -46.19) * mm});
            skLineSegment(sketch, "E1184", {"start": v(14.6, -46.19) * mm, "end": v(15, -45.6) * mm});
            skLineSegment(sketch, "E1185", {"start": v(15, -45.6) * mm, "end": v(15.36, -45) * mm});
            skLineSegment(sketch, "E1186", {"start": v(15.36, -45) * mm, "end": v(15.7, -44.35) * mm});
            skLineSegment(sketch, "E1187", {"start": v(15.7, -44.35) * mm, "end": v(16, -43.68) * mm});
            skLineSegment(sketch, "E1188", {"start": v(16, -43.68) * mm, "end": v(16.27, -42.97) * mm});
            skLineSegment(sketch, "E1189", {"start": v(16.27, -42.97) * mm, "end": v(16.52, -42.22) * mm});
            skLineSegment(sketch, "E1190", {"start": v(16.52, -42.22) * mm, "end": v(16.74, -41.45) * mm});
            skLineSegment(sketch, "E1191", {"start": v(16.74, -41.45) * mm, "end": v(16.93, -40.64) * mm});
            skLineSegment(sketch, "E1192", {"start": v(16.93, -40.64) * mm, "end": v(17.09, -39.8) * mm});
            skLineSegment(sketch, "E1193", {"start": v(17.09, -39.8) * mm, "end": v(17.22, -38.93) * mm});
            skLineSegment(sketch, "E1194", {"start": v(17.22, -38.93) * mm, "end": v(17.32, -38.02) * mm});
            skLineSegment(sketch, "E1195", {"start": v(17.32, -38.02) * mm, "end": v(17.4, -37.08) * mm});
            skLineSegment(sketch, "E1196", {"start": v(17.4, -37.08) * mm, "end": v(17.44, -36.1) * mm});
            skLineSegment(sketch, "E1197", {"start": v(17.44, -36.1) * mm, "end": v(17.45, -35.1) * mm});
            skLineSegment(sketch, "E1198", {"start": v(17.45, -35.1) * mm, "end": v(17.45, -33.95) * mm});
            skLineSegment(sketch, "E1199", {"start": v(17.45, -33.95) * mm, "end": v(17.45, -32.8) * mm});
            skLineSegment(sketch, "E1200", {"start": v(17.45, -32.8) * mm, "end": v(17.45, -31.64) * mm});
            skLineSegment(sketch, "E1201", {"start": v(17.45, -31.64) * mm, "end": v(17.45, -30.5) * mm});
            skLineSegment(sketch, "E1202", {"start": v(17.45, -30.5) * mm, "end": v(17.45, -29.34) * mm});
            skLineSegment(sketch, "E1203", {"start": v(17.45, -29.34) * mm, "end": v(17.45, -28.19) * mm});
            skLineSegment(sketch, "E1204", {"start": v(17.45, -28.19) * mm, "end": v(17.45, -27.03) * mm});
            skLineSegment(sketch, "E1205", {"start": v(17.45, -27.03) * mm, "end": v(17.45, -25.88) * mm});
            skLineSegment(sketch, "E1206", {"start": v(17.45, -25.88) * mm, "end": v(17.45, -24.73) * mm});
            skLineSegment(sketch, "E1207", {"start": v(17.45, -24.73) * mm, "end": v(17.45, -24.66) * mm});
            skLineSegment(sketch, "E1208", {"start": v(17.45, -24.66) * mm, "end": v(17.48, -24.66) * mm});
            skLineSegment(sketch, "E1209", {"start": v(17.48, -24.66) * mm, "end": v(18.08, -24.66) * mm});
            skLineSegment(sketch, "E1210", {"start": v(18.08, -24.66) * mm, "end": v(18.67, -24.66) * mm});
            skLineSegment(sketch, "E1211", {"start": v(18.67, -24.66) * mm, "end": v(19.27, -24.66) * mm});
            skLineSegment(sketch, "E1212", {"start": v(19.27, -24.66) * mm, "end": v(19.86, -24.66) * mm});
            skLineSegment(sketch, "E1213", {"start": v(19.86, -24.66) * mm, "end": v(20.45, -24.66) * mm});
            skLineSegment(sketch, "E1214", {"start": v(20.45, -24.66) * mm, "end": v(21.05, -24.66) * mm});
            skLineSegment(sketch, "E1215", {"start": v(21.05, -24.66) * mm, "end": v(21.64, -24.66) * mm});
            skLineSegment(sketch, "E1216", {"start": v(21.64, -24.66) * mm, "end": v(22.23, -24.66) * mm});
            skLineSegment(sketch, "E1217", {"start": v(22.23, -24.66) * mm, "end": v(22.83, -24.66) * mm});
            skLineSegment(sketch, "E1218", {"start": v(22.83, -24.66) * mm, "end": v(23.42, -24.66) * mm});
            skLineSegment(sketch, "E1219", {"start": v(23.42, -24.66) * mm, "end": v(24.01, -24.66) * mm});
            skLineSegment(sketch, "E1220", {"start": v(24.01, -24.66) * mm, "end": v(24.6, -24.66) * mm});
            skLineSegment(sketch, "E1221", {"start": v(24.6, -24.66) * mm, "end": v(25.2, -24.66) * mm});
            skLineSegment(sketch, "E1222", {"start": v(25.2, -24.66) * mm, "end": v(25.8, -24.66) * mm});
            skLineSegment(sketch, "E1223", {"start": v(25.8, -24.66) * mm, "end": v(25.8, -26.28) * mm});
            skLineSegment(sketch, "E1224", {"start": v(25.8, -26.28) * mm, "end": v(25.8, -27.9) * mm});
            skLineSegment(sketch, "E1225", {"start": v(25.8, -27.9) * mm, "end": v(25.8, -29.53) * mm});
            skLineSegment(sketch, "E1226", {"start": v(25.8, -29.53) * mm, "end": v(25.8, -31.15) * mm});
            skLineSegment(sketch, "E1227", {"start": v(25.8, -31.15) * mm, "end": v(25.8, -32.77) * mm});
            skLineSegment(sketch, "E1228", {"start": v(25.8, -32.77) * mm, "end": v(25.8, -34.4) * mm});
            skLineSegment(sketch, "E1229", {"start": v(25.8, -34.4) * mm, "end": v(25.8, -36.02) * mm});
            skLineSegment(sketch, "E1230", {"start": v(25.8, -36.02) * mm, "end": v(25.8, -37.64) * mm});
            skLineSegment(sketch, "E1231", {"start": v(25.8, -37.64) * mm, "end": v(25.8, -39.26) * mm});
            skLineSegment(sketch, "E1232", {"start": v(25.8, -39.26) * mm, "end": v(25.8, -40.88) * mm});
            skLineSegment(sketch, "E1233", {"start": v(25.8, -40.88) * mm, "end": v(25.8, -42.5) * mm});
            skLineSegment(sketch, "E1234", {"start": v(25.8, -42.5) * mm, "end": v(25.8, -44.13) * mm});
            skLineSegment(sketch, "E1235", {"start": v(25.8, -44.13) * mm, "end": v(25.8, -45.75) * mm});
            skLineSegment(sketch, "E1236", {"start": v(25.8, -45.75) * mm, "end": v(25.8, -47.37) * mm});
            skLineSegment(sketch, "E1237", {"start": v(25.8, -47.37) * mm, "end": v(25.8, -49) * mm});
            skLineSegment(sketch, "E1238", {"start": v(25.8, -49) * mm, "end": v(25.8, -50.62) * mm});
            skLineSegment(sketch, "E1239", {"start": v(25.8, -50.62) * mm, "end": v(26.44, -50.62) * mm});
            skLineSegment(sketch, "E1240", {"start": v(26.44, -50.62) * mm, "end": v(27.08, -50.62) * mm});
            skLineSegment(sketch, "E1241", {"start": v(27.08, -50.62) * mm, "end": v(27.72, -50.62) * mm});
            skLineSegment(sketch, "E1242", {"start": v(27.72, -50.62) * mm, "end": v(28.37, -50.62) * mm});
            skLineSegment(sketch, "E1243", {"start": v(28.37, -50.62) * mm, "end": v(29, -50.62) * mm});
            skLineSegment(sketch, "E1244", {"start": v(29, -50.62) * mm, "end": v(29.65, -50.62) * mm});
            skLineSegment(sketch, "E1245", {"start": v(29.65, -50.62) * mm, "end": v(30.3, -50.62) * mm});
            skLineSegment(sketch, "E1246", {"start": v(30.3, -50.62) * mm, "end": v(30.94, -50.62) * mm});
            skLineSegment(sketch, "E1247", {"start": v(30.94, -50.62) * mm, "end": v(31.58, -50.62) * mm});
            skLineSegment(sketch, "E1248", {"start": v(31.58, -50.62) * mm, "end": v(32.22, -50.62) * mm});
            skLineSegment(sketch, "E1249", {"start": v(32.22, -50.62) * mm, "end": v(32.86, -50.62) * mm});
            skLineSegment(sketch, "E1250", {"start": v(32.86, -50.62) * mm, "end": v(33.5, -50.62) * mm});
            skLineSegment(sketch, "E1251", {"start": v(33.5, -50.62) * mm, "end": v(34.15, -50.62) * mm});
            skLineSegment(sketch, "E1252", {"start": v(34.15, -50.62) * mm, "end": v(34.79, -50.62) * mm});
            skLineSegment(sketch, "E1253", {"start": v(34.79, -50.62) * mm, "end": v(35.43, -50.62) * mm});
            skLineSegment(sketch, "E1254", {"start": v(35.43, -50.62) * mm, "end": v(36.07, -50.62) * mm});
            skLineSegment(sketch, "E1255", {"start": v(36.07, -50.62) * mm, "end": v(36.07, -49) * mm});
            skLineSegment(sketch, "E1256", {"start": v(36.07, -49) * mm, "end": v(36.07, -47.37) * mm});
            skLineSegment(sketch, "E1257", {"start": v(36.07, -47.37) * mm, "end": v(36.07, -45.75) * mm});
            skLineSegment(sketch, "E1258", {"start": v(36.07, -45.75) * mm, "end": v(36.07, -44.13) * mm});
            skLineSegment(sketch, "E1259", {"start": v(36.07, -44.13) * mm, "end": v(36.07, -42.5) * mm});
            skLineSegment(sketch, "E1260", {"start": v(36.07, -42.5) * mm, "end": v(36.07, -40.88) * mm});
            skLineSegment(sketch, "E1261", {"start": v(36.07, -40.88) * mm, "end": v(36.07, -39.26) * mm});
            skLineSegment(sketch, "E1262", {"start": v(36.07, -39.26) * mm, "end": v(36.07, -37.64) * mm});
            skLineSegment(sketch, "E1263", {"start": v(36.07, -37.64) * mm, "end": v(36.07, -36.02) * mm});
            skLineSegment(sketch, "E1264", {"start": v(36.07, -36.02) * mm, "end": v(36.07, -34.4) * mm});
            skLineSegment(sketch, "E1265", {"start": v(36.07, -34.4) * mm, "end": v(36.07, -32.77) * mm});
            skLineSegment(sketch, "E1266", {"start": v(36.07, -32.77) * mm, "end": v(36.07, -31.15) * mm});
            skLineSegment(sketch, "E1267", {"start": v(36.07, -31.15) * mm, "end": v(36.07, -29.53) * mm});
            skLineSegment(sketch, "E1268", {"start": v(36.07, -29.53) * mm, "end": v(36.07, -27.9) * mm});
            skLineSegment(sketch, "E1269", {"start": v(36.07, -27.9) * mm, "end": v(36.07, -26.28) * mm});
            skLineSegment(sketch, "E1270", {"start": v(36.07, -26.28) * mm, "end": v(36.07, -24.66) * mm});
            skLineSegment(sketch, "E1271", {"start": v(36.07, -24.66) * mm, "end": v(36.68, -24.66) * mm});
            skLineSegment(sketch, "E1272", {"start": v(36.68, -24.66) * mm, "end": v(37.28, -24.66) * mm});
            skLineSegment(sketch, "E1273", {"start": v(37.28, -24.66) * mm, "end": v(37.88, -24.66) * mm});
            skLineSegment(sketch, "E1274", {"start": v(37.88, -24.66) * mm, "end": v(38.48, -24.66) * mm});
            skLineSegment(sketch, "E1275", {"start": v(38.48, -24.66) * mm, "end": v(39.08, -24.66) * mm});
            skLineSegment(sketch, "E1276", {"start": v(39.08, -24.66) * mm, "end": v(39.68, -24.66) * mm});
            skLineSegment(sketch, "E1277", {"start": v(39.68, -24.66) * mm, "end": v(40.28, -24.66) * mm});
            skLineSegment(sketch, "E1278", {"start": v(40.28, -24.66) * mm, "end": v(40.88, -24.66) * mm});
            skLineSegment(sketch, "E1279", {"start": v(40.88, -24.66) * mm, "end": v(41.48, -24.66) * mm});
            skLineSegment(sketch, "E1280", {"start": v(41.48, -24.66) * mm, "end": v(42.08, -24.66) * mm});
            skLineSegment(sketch, "E1281", {"start": v(42.08, -24.66) * mm, "end": v(42.69, -24.66) * mm});
            skLineSegment(sketch, "E1282", {"start": v(42.69, -24.66) * mm, "end": v(43.29, -24.66) * mm});
            skLineSegment(sketch, "E1283", {"start": v(43.29, -24.66) * mm, "end": v(43.89, -24.66) * mm});
            skLineSegment(sketch, "E1284", {"start": v(43.89, -24.66) * mm, "end": v(44.49, -24.66) * mm});
            skLineSegment(sketch, "E1285", {"start": v(44.49, -24.66) * mm, "end": v(45.09, -24.66) * mm});
            skLineSegment(sketch, "E1286", {"start": v(45.09, -24.66) * mm, "end": v(45.7, -24.66) * mm});
            skLineSegment(sketch, "E1287", {"start": v(45.7, -24.66) * mm, "end": v(45.7, -24.16) * mm});
            skLineSegment(sketch, "E1288", {"start": v(45.7, -24.16) * mm, "end": v(45.7, -23.66) * mm});
            skLineSegment(sketch, "E1289", {"start": v(45.7, -23.66) * mm, "end": v(45.7, -23.16) * mm});
            skLineSegment(sketch, "E1290", {"start": v(45.7, -23.16) * mm, "end": v(45.7, -22.66) * mm});
            skLineSegment(sketch, "E1291", {"start": v(45.7, -22.66) * mm, "end": v(45.7, -22.16) * mm});
            skLineSegment(sketch, "E1292", {"start": v(45.7, -22.16) * mm, "end": v(45.7, -21.66) * mm});
            skLineSegment(sketch, "E1293", {"start": v(45.7, -21.66) * mm, "end": v(45.7, -21.16) * mm});
            skLineSegment(sketch, "E1294", {"start": v(45.7, -21.16) * mm, "end": v(45.7, -20.66) * mm});
            skLineSegment(sketch, "E1295", {"start": v(45.7, -20.66) * mm, "end": v(45.7, -20.16) * mm});
            skLineSegment(sketch, "E1296", {"start": v(45.7, -20.16) * mm, "end": v(45.7, -19.66) * mm});
            skLineSegment(sketch, "E1297", {"start": v(45.7, -19.66) * mm, "end": v(45.7, -19.16) * mm});
            skLineSegment(sketch, "E1298", {"start": v(45.7, -19.16) * mm, "end": v(45.7, -18.66) * mm});
            skLineSegment(sketch, "E1299", {"start": v(45.7, -18.66) * mm, "end": v(45.7, -18.15) * mm});
            skLineSegment(sketch, "E1300", {"start": v(45.7, -18.15) * mm, "end": v(45.7, -17.65) * mm});
            skLineSegment(sketch, "E1301", {"start": v(45.7, -17.65) * mm, "end": v(45.7, -17.15) * mm});
            skLineSegment(sketch, "E1302", {"start": v(45.7, -17.15) * mm, "end": v(45.7, -17.09) * mm});
            skLineSegment(sketch, "E1303", {"start": v(45.7, -17.09) * mm, "end": v(46.38, -17.09) * mm});
            skLineSegment(sketch, "E1304", {"start": v(46.38, -17.09) * mm, "end": v(47.1, -17.09) * mm});
            skLineSegment(sketch, "E1305", {"start": v(47.1, -17.09) * mm, "end": v(47.82, -17.09) * mm});
            skLineSegment(sketch, "E1306", {"start": v(47.82, -17.09) * mm, "end": v(48.54, -17.09) * mm});
            skLineSegment(sketch, "E1307", {"start": v(48.54, -17.09) * mm, "end": v(49.26, -17.09) * mm});
            skLineSegment(sketch, "E1308", {"start": v(49.26, -17.09) * mm, "end": v(49.98, -17.09) * mm});
            skLineSegment(sketch, "E1309", {"start": v(49.98, -17.09) * mm, "end": v(50.7, -17.09) * mm});
            skLineSegment(sketch, "E1310", {"start": v(50.7, -17.09) * mm, "end": v(51.42, -17.09) * mm});
            skLineSegment(sketch, "E1311", {"start": v(51.42, -17.09) * mm, "end": v(52.14, -17.09) * mm});
            skLineSegment(sketch, "E1312", {"start": v(52.14, -17.09) * mm, "end": v(52.86, -17.09) * mm});
            skLineSegment(sketch, "E1313", {"start": v(52.86, -17.09) * mm, "end": v(53.54, -17.09) * mm});
            skLineSegment(sketch, "E1314", {"start": v(53.54, -17.09) * mm, "end": v(53.54, -18.78) * mm});
            skLineSegment(sketch, "E1315", {"start": v(53.54, -18.78) * mm, "end": v(53.54, -20.9) * mm});
            skLineSegment(sketch, "E1316", {"start": v(53.54, -20.9) * mm, "end": v(53.54, -23.02) * mm});
            skLineSegment(sketch, "E1317", {"start": v(53.54, -23.02) * mm, "end": v(53.54, -25.14) * mm});
            skLineSegment(sketch, "E1318", {"start": v(53.54, -25.14) * mm, "end": v(53.54, -27.27) * mm});
            skLineSegment(sketch, "E1319", {"start": v(53.54, -27.27) * mm, "end": v(53.54, -29.4) * mm});
            skLineSegment(sketch, "E1320", {"start": v(53.54, -29.4) * mm, "end": v(53.54, -31.51) * mm});
            skLineSegment(sketch, "E1321", {"start": v(53.54, -31.51) * mm, "end": v(53.54, -33.64) * mm});
            skLineSegment(sketch, "E1322", {"start": v(53.54, -33.64) * mm, "end": v(53.54, -35.76) * mm});
            skLineSegment(sketch, "E1323", {"start": v(53.54, -35.76) * mm, "end": v(53.54, -37.88) * mm});
            skLineSegment(sketch, "E1324", {"start": v(53.54, -37.88) * mm, "end": v(53.54, -40) * mm});
            skLineSegment(sketch, "E1325", {"start": v(53.54, -40) * mm, "end": v(53.54, -42.13) * mm});
            skLineSegment(sketch, "E1326", {"start": v(53.54, -42.13) * mm, "end": v(53.54, -44.25) * mm});
            skLineSegment(sketch, "E1327", {"start": v(53.54, -44.25) * mm, "end": v(53.54, -46.37) * mm});
            skLineSegment(sketch, "E1328", {"start": v(53.54, -46.37) * mm, "end": v(53.54, -48.5) * mm});
            skLineSegment(sketch, "E1329", {"start": v(53.54, -48.5) * mm, "end": v(53.54, -50.62) * mm});
            skLineSegment(sketch, "E1330", {"start": v(53.54, -50.62) * mm, "end": v(54.18, -50.62) * mm});
            skLineSegment(sketch, "E1331", {"start": v(54.18, -50.62) * mm, "end": v(54.82, -50.62) * mm});
            skLineSegment(sketch, "E1332", {"start": v(54.82, -50.62) * mm, "end": v(55.46, -50.62) * mm});
            skLineSegment(sketch, "E1333", {"start": v(55.46, -50.62) * mm, "end": v(56.1, -50.62) * mm});
            skLineSegment(sketch, "E1334", {"start": v(56.1, -50.62) * mm, "end": v(56.74, -50.62) * mm});
            skLineSegment(sketch, "E1335", {"start": v(56.74, -50.62) * mm, "end": v(57.38, -50.62) * mm});
            skLineSegment(sketch, "E1336", {"start": v(57.38, -50.62) * mm, "end": v(58.02, -50.62) * mm});
            skLineSegment(sketch, "E1337", {"start": v(58.02, -50.62) * mm, "end": v(58.66, -50.62) * mm});
            skLineSegment(sketch, "E1338", {"start": v(58.66, -50.62) * mm, "end": v(59.3, -50.62) * mm});
            skLineSegment(sketch, "E1339", {"start": v(59.3, -50.62) * mm, "end": v(59.94, -50.62) * mm});
            skLineSegment(sketch, "E1340", {"start": v(59.94, -50.62) * mm, "end": v(60.57, -50.62) * mm});
            skLineSegment(sketch, "E1341", {"start": v(60.57, -50.62) * mm, "end": v(61.21, -50.62) * mm});
            skLineSegment(sketch, "E1342", {"start": v(61.21, -50.62) * mm, "end": v(61.85, -50.62) * mm});
            skLineSegment(sketch, "E1343", {"start": v(61.85, -50.62) * mm, "end": v(62.5, -50.62) * mm});
            skLineSegment(sketch, "E1344", {"start": v(62.5, -50.62) * mm, "end": v(63.13, -50.62) * mm});
            skLineSegment(sketch, "E1345", {"start": v(63.13, -50.62) * mm, "end": v(63.77, -50.62) * mm});
            skLineSegment(sketch, "E1346", {"start": v(63.77, -50.62) * mm, "end": v(63.77, -48.5) * mm});
            skLineSegment(sketch, "E1347", {"start": v(63.77, -48.5) * mm, "end": v(63.77, -46.37) * mm});
            skLineSegment(sketch, "E1348", {"start": v(63.77, -46.37) * mm, "end": v(63.77, -44.25) * mm});
            skLineSegment(sketch, "E1349", {"start": v(63.77, -44.25) * mm, "end": v(63.77, -42.13) * mm});
            skLineSegment(sketch, "E1350", {"start": v(63.77, -42.13) * mm, "end": v(63.77, -40) * mm});
            skLineSegment(sketch, "E1351", {"start": v(63.77, -40) * mm, "end": v(63.77, -37.88) * mm});
            skLineSegment(sketch, "E1352", {"start": v(63.77, -37.88) * mm, "end": v(63.77, -35.76) * mm});
            skLineSegment(sketch, "E1353", {"start": v(63.77, -35.76) * mm, "end": v(63.77, -33.64) * mm});
            skLineSegment(sketch, "E1354", {"start": v(63.77, -33.64) * mm, "end": v(63.77, -31.51) * mm});
            skLineSegment(sketch, "E1355", {"start": v(63.77, -31.51) * mm, "end": v(63.77, -29.4) * mm});
            skLineSegment(sketch, "E1356", {"start": v(63.77, -29.4) * mm, "end": v(63.77, -27.27) * mm});
            skLineSegment(sketch, "E1357", {"start": v(63.77, -27.27) * mm, "end": v(63.77, -25.14) * mm});
            skLineSegment(sketch, "E1358", {"start": v(63.77, -25.14) * mm, "end": v(63.77, -24.66) * mm});
            skLineSegment(sketch, "E1359", {"start": v(63.77, -24.66) * mm, "end": v(64.18, -24.66) * mm});
            skLineSegment(sketch, "E1360", {"start": v(64.18, -24.66) * mm, "end": v(64.78, -24.66) * mm});
            skLineSegment(sketch, "E1361", {"start": v(64.78, -24.66) * mm, "end": v(65.37, -24.66) * mm});
            skLineSegment(sketch, "E1362", {"start": v(65.37, -24.66) * mm, "end": v(65.96, -24.66) * mm});
            skLineSegment(sketch, "E1363", {"start": v(65.96, -24.66) * mm, "end": v(66.56, -24.66) * mm});
            skLineSegment(sketch, "E1364", {"start": v(66.56, -24.66) * mm, "end": v(67.15, -24.66) * mm});
            skLineSegment(sketch, "E1365", {"start": v(67.15, -24.66) * mm, "end": v(67.74, -24.66) * mm});
            skLineSegment(sketch, "E1366", {"start": v(67.74, -24.66) * mm, "end": v(68.34, -24.66) * mm});
            skLineSegment(sketch, "E1367", {"start": v(68.34, -24.66) * mm, "end": v(68.93, -24.66) * mm});
            skLineSegment(sketch, "E1368", {"start": v(68.93, -24.66) * mm, "end": v(69.52, -24.66) * mm});
            skLineSegment(sketch, "E1369", {"start": v(69.52, -24.66) * mm, "end": v(70.12, -24.66) * mm});
            skLineSegment(sketch, "E1370", {"start": v(70.12, -24.66) * mm, "end": v(70.71, -24.66) * mm});
            skLineSegment(sketch, "E1371", {"start": v(70.71, -24.66) * mm, "end": v(71.3, -24.66) * mm});
            skLineSegment(sketch, "E1372", {"start": v(71.3, -24.66) * mm, "end": v(71.9, -24.66) * mm});
            skLineSegment(sketch, "E1373", {"start": v(71.9, -24.66) * mm, "end": v(72.5, -24.66) * mm});
            skLineSegment(sketch, "E1374", {"start": v(72.5, -24.66) * mm, "end": v(72.5, -26.28) * mm});
            skLineSegment(sketch, "E1375", {"start": v(72.5, -26.28) * mm, "end": v(72.5, -27.9) * mm});
            skLineSegment(sketch, "E1376", {"start": v(72.5, -27.9) * mm, "end": v(72.5, -29.53) * mm});
            skLineSegment(sketch, "E1377", {"start": v(72.5, -29.53) * mm, "end": v(72.5, -31.15) * mm});
            skLineSegment(sketch, "E1378", {"start": v(72.5, -31.15) * mm, "end": v(72.5, -32.77) * mm});
            skLineSegment(sketch, "E1379", {"start": v(72.5, -32.77) * mm, "end": v(72.5, -34.4) * mm});
            skLineSegment(sketch, "E1380", {"start": v(72.5, -34.4) * mm, "end": v(72.5, -36.02) * mm});
            skLineSegment(sketch, "E1381", {"start": v(72.5, -36.02) * mm, "end": v(72.5, -37.64) * mm});
            skLineSegment(sketch, "E1382", {"start": v(72.5, -37.64) * mm, "end": v(72.5, -39.26) * mm});
            skLineSegment(sketch, "E1383", {"start": v(72.5, -39.26) * mm, "end": v(72.5, -40.88) * mm});
            skLineSegment(sketch, "E1384", {"start": v(72.5, -40.88) * mm, "end": v(72.5, -42.5) * mm});
            skLineSegment(sketch, "E1385", {"start": v(72.5, -42.5) * mm, "end": v(72.5, -44.13) * mm});
            skLineSegment(sketch, "E1386", {"start": v(72.5, -44.13) * mm, "end": v(72.5, -45.75) * mm});
            skLineSegment(sketch, "E1387", {"start": v(72.5, -45.75) * mm, "end": v(72.5, -47.37) * mm});
            skLineSegment(sketch, "E1388", {"start": v(72.5, -47.37) * mm, "end": v(72.5, -49) * mm});
            skLineSegment(sketch, "E1389", {"start": v(72.5, -49) * mm, "end": v(72.5, -50.62) * mm});
            skLineSegment(sketch, "E1390", {"start": v(72.5, -50.62) * mm, "end": v(73.14, -50.62) * mm});
            skLineSegment(sketch, "E1391", {"start": v(73.14, -50.62) * mm, "end": v(73.78, -50.62) * mm});
            skLineSegment(sketch, "E1392", {"start": v(73.78, -50.62) * mm, "end": v(74.42, -50.62) * mm});
            skLineSegment(sketch, "E1393", {"start": v(74.42, -50.62) * mm, "end": v(75.06, -50.62) * mm});
            skLineSegment(sketch, "E1394", {"start": v(75.06, -50.62) * mm, "end": v(75.7, -50.62) * mm});
            skLineSegment(sketch, "E1395", {"start": v(75.7, -50.62) * mm, "end": v(76.35, -50.62) * mm});
            skLineSegment(sketch, "E1396", {"start": v(76.35, -50.62) * mm, "end": v(76.99, -50.62) * mm});
            skLineSegment(sketch, "E1397", {"start": v(76.99, -50.62) * mm, "end": v(77.63, -50.62) * mm});
            skLineSegment(sketch, "E1398", {"start": v(77.63, -50.62) * mm, "end": v(78.27, -50.62) * mm});
            skLineSegment(sketch, "E1399", {"start": v(78.27, -50.62) * mm, "end": v(78.92, -50.62) * mm});
            skLineSegment(sketch, "E1400", {"start": v(78.92, -50.62) * mm, "end": v(79.56, -50.62) * mm});
            skLineSegment(sketch, "E1401", {"start": v(79.56, -50.62) * mm, "end": v(80.2, -50.62) * mm});
            skLineSegment(sketch, "E1402", {"start": v(80.2, -50.62) * mm, "end": v(80.84, -50.62) * mm});
            skLineSegment(sketch, "E1403", {"start": v(80.84, -50.62) * mm, "end": v(81.49, -50.62) * mm});
            skLineSegment(sketch, "E1404", {"start": v(81.49, -50.62) * mm, "end": v(82.13, -50.62) * mm});
            skLineSegment(sketch, "E1405", {"start": v(82.13, -50.62) * mm, "end": v(82.77, -50.62) * mm});
            skLineSegment(sketch, "E1406", {"start": v(82.77, -50.62) * mm, "end": v(82.77, -49) * mm});
            skLineSegment(sketch, "E1407", {"start": v(82.77, -49) * mm, "end": v(82.77, -47.37) * mm});
            skLineSegment(sketch, "E1408", {"start": v(82.77, -47.37) * mm, "end": v(82.77, -45.75) * mm});
            skLineSegment(sketch, "E1409", {"start": v(82.77, -45.75) * mm, "end": v(82.77, -44.13) * mm});
            skLineSegment(sketch, "E1410", {"start": v(82.77, -44.13) * mm, "end": v(82.77, -42.5) * mm});
            skLineSegment(sketch, "E1411", {"start": v(82.77, -42.5) * mm, "end": v(82.77, -40.88) * mm});
            skLineSegment(sketch, "E1412", {"start": v(82.77, -40.88) * mm, "end": v(82.77, -39.26) * mm});
            skLineSegment(sketch, "E1413", {"start": v(82.77, -39.26) * mm, "end": v(82.77, -37.64) * mm});
            skLineSegment(sketch, "E1414", {"start": v(82.77, -37.64) * mm, "end": v(82.77, -36.02) * mm});
            skLineSegment(sketch, "E1415", {"start": v(82.77, -36.02) * mm, "end": v(82.77, -34.4) * mm});
            skLineSegment(sketch, "E1416", {"start": v(82.77, -34.4) * mm, "end": v(82.77, -32.77) * mm});
            skLineSegment(sketch, "E1417", {"start": v(82.77, -32.77) * mm, "end": v(82.77, -31.15) * mm});
            skLineSegment(sketch, "E1418", {"start": v(82.77, -31.15) * mm, "end": v(82.77, -29.53) * mm});
            skLineSegment(sketch, "E1419", {"start": v(82.77, -29.53) * mm, "end": v(82.77, -27.9) * mm});
            skLineSegment(sketch, "E1420", {"start": v(82.77, -27.9) * mm, "end": v(82.77, -26.28) * mm});
            skLineSegment(sketch, "E1421", {"start": v(82.77, -26.28) * mm, "end": v(82.77, -24.66) * mm});
            skLineSegment(sketch, "E1422", {"start": v(82.77, -24.66) * mm, "end": v(83.37, -24.66) * mm});
            skLineSegment(sketch, "E1423", {"start": v(83.37, -24.66) * mm, "end": v(83.97, -24.66) * mm});
            skLineSegment(sketch, "E1424", {"start": v(83.97, -24.66) * mm, "end": v(84.58, -24.66) * mm});
            skLineSegment(sketch, "E1425", {"start": v(84.58, -24.66) * mm, "end": v(85.18, -24.66) * mm});
            skLineSegment(sketch, "E1426", {"start": v(85.18, -24.66) * mm, "end": v(85.78, -24.66) * mm});
            skLineSegment(sketch, "E1427", {"start": v(85.78, -24.66) * mm, "end": v(86.38, -24.66) * mm});
            skLineSegment(sketch, "E1428", {"start": v(86.38, -24.66) * mm, "end": v(86.98, -24.66) * mm});
            skLineSegment(sketch, "E1429", {"start": v(86.98, -24.66) * mm, "end": v(87.58, -24.66) * mm});
            skLineSegment(sketch, "E1430", {"start": v(87.58, -24.66) * mm, "end": v(88.18, -24.66) * mm});
            skLineSegment(sketch, "E1431", {"start": v(88.18, -24.66) * mm, "end": v(88.78, -24.66) * mm});
            skLineSegment(sketch, "E1432", {"start": v(88.78, -24.66) * mm, "end": v(89.38, -24.66) * mm});
            skLineSegment(sketch, "E1433", {"start": v(89.38, -24.66) * mm, "end": v(89.98, -24.66) * mm});
            skLineSegment(sketch, "E1434", {"start": v(89.98, -24.66) * mm, "end": v(90.59, -24.66) * mm});
            skLineSegment(sketch, "E1435", {"start": v(90.59, -24.66) * mm, "end": v(91.19, -24.66) * mm});
            skLineSegment(sketch, "E1436", {"start": v(91.19, -24.66) * mm, "end": v(91.79, -24.66) * mm});
            skLineSegment(sketch, "E1437", {"start": v(91.79, -24.66) * mm, "end": v(92.2, -24.66) * mm});
            skLineSegment(sketch, "E1438", {"start": v(-82.26, -37.1) * mm, "end": v(-82.66, -37.1) * mm});
            skLineSegment(sketch, "E1439", {"start": v(-82.66, -37.1) * mm, "end": v(-83.07, -37.1) * mm});
            skLineSegment(sketch, "E1440", {"start": v(-83.07, -37.1) * mm, "end": v(-83.48, -37.1) * mm});
            skLineSegment(sketch, "E1441", {"start": v(-83.48, -37.1) * mm, "end": v(-83.88, -37.1) * mm});
            skLineSegment(sketch, "E1442", {"start": v(-83.88, -37.1) * mm, "end": v(-84.29, -37.1) * mm});
            skLineSegment(sketch, "E1443", {"start": v(-84.29, -37.1) * mm, "end": v(-84.7, -37.1) * mm});
            skLineSegment(sketch, "E1444", {"start": v(-84.7, -37.1) * mm, "end": v(-85.1, -37.1) * mm});
            skLineSegment(sketch, "E1445", {"start": v(-85.1, -37.1) * mm, "end": v(-85.5, -37.1) * mm});
            skLineSegment(sketch, "E1446", {"start": v(-85.5, -37.1) * mm, "end": v(-85.9, -37.1) * mm});
            skLineSegment(sketch, "E1447", {"start": v(-85.9, -37.1) * mm, "end": v(-86.31, -37.1) * mm});
            skLineSegment(sketch, "E1448", {"start": v(-86.31, -37.1) * mm, "end": v(-86.72, -37.1) * mm});
            skLineSegment(sketch, "E1449", {"start": v(-86.72, -37.1) * mm, "end": v(-87.13, -37.1) * mm});
            skLineSegment(sketch, "E1450", {"start": v(-87.13, -37.1) * mm, "end": v(-87.53, -37.1) * mm});
            skLineSegment(sketch, "E1451", {"start": v(-87.53, -37.1) * mm, "end": v(-87.94, -37.1) * mm});
            skLineSegment(sketch, "E1452", {"start": v(-87.94, -37.1) * mm, "end": v(-88.34, -37.1) * mm});
            skLineSegment(sketch, "E1453", {"start": v(-88.34, -37.1) * mm, "end": v(-88.03, -35.9) * mm});
            skLineSegment(sketch, "E1454", {"start": v(-88.03, -35.9) * mm, "end": v(-87.73, -34.76) * mm});
            skLineSegment(sketch, "E1455", {"start": v(-87.73, -34.76) * mm, "end": v(-87.46, -33.7) * mm});
            skLineSegment(sketch, "E1456", {"start": v(-87.46, -33.7) * mm, "end": v(-87.2, -32.7) * mm});
            skLineSegment(sketch, "E1457", {"start": v(-87.2, -32.7) * mm, "end": v(-86.95, -31.76) * mm});
            skLineSegment(sketch, "E1458", {"start": v(-86.95, -31.76) * mm, "end": v(-86.73, -30.9) * mm});
            skLineSegment(sketch, "E1459", {"start": v(-86.73, -30.9) * mm, "end": v(-86.52, -30.1) * mm});
            skLineSegment(sketch, "E1460", {"start": v(-86.52, -30.1) * mm, "end": v(-86.34, -29.36) * mm});
            skLineSegment(sketch, "E1461", {"start": v(-86.34, -29.36) * mm, "end": v(-86.17, -28.7) * mm});
            skLineSegment(sketch, "E1462", {"start": v(-86.17, -28.7) * mm, "end": v(-86.01, -28.1) * mm});
            skLineSegment(sketch, "E1463", {"start": v(-86.01, -28.1) * mm, "end": v(-85.88, -27.57) * mm});
            skLineSegment(sketch, "E1464", {"start": v(-85.88, -27.57) * mm, "end": v(-85.76, -27.1) * mm});
            skLineSegment(sketch, "E1465", {"start": v(-85.76, -27.1) * mm, "end": v(-85.66, -26.7) * mm});
            skLineSegment(sketch, "E1466", {"start": v(-85.66, -26.7) * mm, "end": v(-85.58, -26.37) * mm});
            skLineSegment(sketch, "E1467", {"start": v(-85.58, -26.37) * mm, "end": v(-85.52, -26.11) * mm});
            skLineSegment(sketch, "E1468", {"start": v(-85.52, -26.11) * mm, "end": v(-85.48, -25.91) * mm});
            skLineSegment(sketch, "E1469", {"start": v(-85.48, -25.91) * mm, "end": v(-85.44, -25.75) * mm});
            skLineSegment(sketch, "E1470", {"start": v(-85.44, -25.75) * mm, "end": v(-85.4, -25.6) * mm});
            skLineSegment(sketch, "E1471", {"start": v(-85.4, -25.6) * mm, "end": v(-85.38, -25.45) * mm});
            skLineSegment(sketch, "E1472", {"start": v(-85.38, -25.45) * mm, "end": v(-85.35, -25.3) * mm});
            skLineSegment(sketch, "E1473", {"start": v(-85.35, -25.3) * mm, "end": v(-85.32, -25.17) * mm});
            skLineSegment(sketch, "E1474", {"start": v(-85.32, -25.17) * mm, "end": v(-85.3, -25.04) * mm});
            skLineSegment(sketch, "E1475", {"start": v(-85.3, -25.04) * mm, "end": v(-85.27, -24.92) * mm});
            skLineSegment(sketch, "E1476", {"start": v(-85.27, -24.92) * mm, "end": v(-85.25, -24.8) * mm});
            skLineSegment(sketch, "E1477", {"start": v(-85.25, -24.8) * mm, "end": v(-85.23, -24.68) * mm});
            skLineSegment(sketch, "E1478", {"start": v(-85.23, -24.68) * mm, "end": v(-85.21, -24.57) * mm});
            skLineSegment(sketch, "E1479", {"start": v(-85.21, -24.57) * mm, "end": v(-85.2, -24.47) * mm});
            skLineSegment(sketch, "E1480", {"start": v(-85.2, -24.47) * mm, "end": v(-85.18, -24.37) * mm});
            skLineSegment(sketch, "E1481", {"start": v(-85.18, -24.37) * mm, "end": v(-85.17, -24.28) * mm});
            skLineSegment(sketch, "E1482", {"start": v(-85.17, -24.28) * mm, "end": v(-85.16, -24.2) * mm});
            skLineSegment(sketch, "E1483", {"start": v(-85.16, -24.2) * mm, "end": v(-85.15, -24.12) * mm});
            skLineSegment(sketch, "E1484", {"start": v(-85.15, -24.12) * mm, "end": v(-85.15, -24.04) * mm});
            skLineSegment(sketch, "E1485", {"start": v(-85.15, -24.04) * mm, "end": v(-85.13, -24.04) * mm});
            skLineSegment(sketch, "E1486", {"start": v(-85.13, -24.04) * mm, "end": v(-85.12, -24.04) * mm});
            skLineSegment(sketch, "E1487", {"start": v(-85.12, -24.04) * mm, "end": v(-85.1, -24.04) * mm});
            skLineSegment(sketch, "E1488", {"start": v(-85.1, -24.04) * mm, "end": v(-85.09, -24.04) * mm});
            skLineSegment(sketch, "E1489", {"start": v(-85.09, -24.04) * mm, "end": v(-85.07, -24.04) * mm});
            skLineSegment(sketch, "E1490", {"start": v(-85.07, -24.04) * mm, "end": v(-85.06, -24.04) * mm});
            skLineSegment(sketch, "E1491", {"start": v(-85.06, -24.04) * mm, "end": v(-85.04, -24.04) * mm});
            skLineSegment(sketch, "E1492", {"start": v(-85.04, -24.04) * mm, "end": v(-85.03, -24.04) * mm});
            skLineSegment(sketch, "E1493", {"start": v(-85.03, -24.04) * mm, "end": v(-85.01, -24.04) * mm});
            skLineSegment(sketch, "E1494", {"start": v(-85.01, -24.04) * mm, "end": v(-85, -24.04) * mm});
            skLineSegment(sketch, "E1495", {"start": v(-85, -24.04) * mm, "end": v(-84.98, -24.04) * mm});
            skLineSegment(sketch, "E1496", {"start": v(-84.98, -24.04) * mm, "end": v(-84.97, -24.04) * mm});
            skLineSegment(sketch, "E1497", {"start": v(-84.97, -24.04) * mm, "end": v(-84.95, -24.04) * mm});
            skLineSegment(sketch, "E1498", {"start": v(-84.95, -24.04) * mm, "end": v(-84.94, -24.04) * mm});
            skLineSegment(sketch, "E1499", {"start": v(-84.94, -24.04) * mm, "end": v(-84.92, -24.04) * mm});
            skLineSegment(sketch, "E1500", {"start": v(-84.92, -24.04) * mm, "end": v(-84.9, -24.04) * mm});
            skLineSegment(sketch, "E1501", {"start": v(-84.9, -24.04) * mm, "end": v(-84.88, -24.27) * mm});
            skLineSegment(sketch, "E1502", {"start": v(-84.88, -24.27) * mm, "end": v(-84.86, -24.5) * mm});
            skLineSegment(sketch, "E1503", {"start": v(-84.86, -24.5) * mm, "end": v(-84.83, -24.72) * mm});
            skLineSegment(sketch, "E1504", {"start": v(-84.83, -24.72) * mm, "end": v(-84.8, -24.95) * mm});
            skLineSegment(sketch, "E1505", {"start": v(-84.8, -24.95) * mm, "end": v(-84.76, -25.18) * mm});
            skLineSegment(sketch, "E1506", {"start": v(-84.76, -25.18) * mm, "end": v(-84.72, -25.41) * mm});
            skLineSegment(sketch, "E1507", {"start": v(-84.72, -25.41) * mm, "end": v(-84.68, -25.65) * mm});
            skLineSegment(sketch, "E1508", {"start": v(-84.68, -25.65) * mm, "end": v(-84.64, -25.89) * mm});
            skLineSegment(sketch, "E1509", {"start": v(-84.64, -25.89) * mm, "end": v(-84.6, -26.12) * mm});
            skLineSegment(sketch, "E1510", {"start": v(-84.6, -26.12) * mm, "end": v(-84.55, -26.37) * mm});
            skLineSegment(sketch, "E1511", {"start": v(-84.55, -26.37) * mm, "end": v(-84.5, -26.6) * mm});
            skLineSegment(sketch, "E1512", {"start": v(-84.5, -26.6) * mm, "end": v(-84.45, -26.85) * mm});
            skLineSegment(sketch, "E1513", {"start": v(-84.45, -26.85) * mm, "end": v(-84.4, -27.1) * mm});
            skLineSegment(sketch, "E1514", {"start": v(-84.4, -27.1) * mm, "end": v(-84.34, -27.35) * mm});
            skLineSegment(sketch, "E1515", {"start": v(-84.34, -27.35) * mm, "end": v(-84.28, -27.6) * mm});
            skLineSegment(sketch, "E1516", {"start": v(-84.28, -27.6) * mm, "end": v(-84.22, -27.86) * mm});
            skLineSegment(sketch, "E1517", {"start": v(-84.22, -27.86) * mm, "end": v(-84.07, -28.43) * mm});
            skLineSegment(sketch, "E1518", {"start": v(-84.07, -28.43) * mm, "end": v(-83.93, -29.01) * mm});
            skLineSegment(sketch, "E1519", {"start": v(-83.93, -29.01) * mm, "end": v(-83.78, -29.59) * mm});
            skLineSegment(sketch, "E1520", {"start": v(-83.78, -29.59) * mm, "end": v(-83.63, -30.17) * mm});
            skLineSegment(sketch, "E1521", {"start": v(-83.63, -30.17) * mm, "end": v(-83.48, -30.74) * mm});
            skLineSegment(sketch, "E1522", {"start": v(-83.48, -30.74) * mm, "end": v(-83.33, -31.32) * mm});
            skLineSegment(sketch, "E1523", {"start": v(-83.33, -31.32) * mm, "end": v(-83.19, -31.9) * mm});
            skLineSegment(sketch, "E1524", {"start": v(-83.19, -31.9) * mm, "end": v(-83.04, -32.48) * mm});
            skLineSegment(sketch, "E1525", {"start": v(-83.04, -32.48) * mm, "end": v(-82.89, -33.05) * mm});
            skLineSegment(sketch, "E1526", {"start": v(-82.89, -33.05) * mm, "end": v(-82.74, -33.63) * mm});
            skLineSegment(sketch, "E1527", {"start": v(-82.74, -33.63) * mm, "end": v(-82.6, -34.2) * mm});
            skLineSegment(sketch, "E1528", {"start": v(-82.6, -34.2) * mm, "end": v(-82.45, -34.78) * mm});
            skLineSegment(sketch, "E1529", {"start": v(-82.45, -34.78) * mm, "end": v(-82.3, -35.36) * mm});
            skLineSegment(sketch, "E1530", {"start": v(-82.3, -35.36) * mm, "end": v(-82.15, -35.94) * mm});
            skLineSegment(sketch, "E1531", {"start": v(-82.15, -35.94) * mm, "end": v(-82, -36.52) * mm});
            skLineSegment(sketch, "E1532", {"start": v(-82, -36.52) * mm, "end": v(-81.85, -37.1) * mm});
            skLineSegment(sketch, "E1533", {"start": v(-81.85, -37.1) * mm, "end": v(-82.26, -37.1) * mm});
            skLineSegment(sketch, "E1534", {"start": v(36.1, 2.51) * mm, "end": v(36.1, 3) * mm});
            skLineSegment(sketch, "E1535", {"start": v(36.1, 3) * mm, "end": v(36.1, 3.48) * mm});
            skLineSegment(sketch, "E1536", {"start": v(36.1, 3.48) * mm, "end": v(36.1, 3.97) * mm});
            skLineSegment(sketch, "E1537", {"start": v(36.1, 3.97) * mm, "end": v(36.1, 4.45) * mm});
            skLineSegment(sketch, "E1538", {"start": v(36.1, 4.45) * mm, "end": v(36.1, 4.94) * mm});
            skLineSegment(sketch, "E1539", {"start": v(36.1, 4.94) * mm, "end": v(36.1, 5.42) * mm});
            skLineSegment(sketch, "E1540", {"start": v(36.1, 5.42) * mm, "end": v(36.1, 5.9) * mm});
            skLineSegment(sketch, "E1541", {"start": v(36.1, 5.9) * mm, "end": v(36.1, 6.4) * mm});
            skLineSegment(sketch, "E1542", {"start": v(36.1, 6.4) * mm, "end": v(36.1, 6.88) * mm});
            skLineSegment(sketch, "E1543", {"start": v(36.1, 6.88) * mm, "end": v(36.1, 7.37) * mm});
            skLineSegment(sketch, "E1544", {"start": v(36.1, 7.37) * mm, "end": v(36.1, 7.85) * mm});
            skLineSegment(sketch, "E1545", {"start": v(36.1, 7.85) * mm, "end": v(36.1, 8.34) * mm});
            skLineSegment(sketch, "E1546", {"start": v(36.1, 8.34) * mm, "end": v(36.1, 8.82) * mm});
            skLineSegment(sketch, "E1547", {"start": v(36.1, 8.82) * mm, "end": v(36.1, 9.3) * mm});
            skLineSegment(sketch, "E1548", {"start": v(36.1, 9.3) * mm, "end": v(36.1, 9.8) * mm});
            skLineSegment(sketch, "E1549", {"start": v(36.1, 9.8) * mm, "end": v(36.23, 9.8) * mm});
            skLineSegment(sketch, "E1550", {"start": v(36.23, 9.8) * mm, "end": v(36.37, 9.8) * mm});
            skLineSegment(sketch, "E1551", {"start": v(36.37, 9.8) * mm, "end": v(36.5, 9.8) * mm});
            skLineSegment(sketch, "E1552", {"start": v(36.5, 9.8) * mm, "end": v(36.63, 9.8) * mm});
            skLineSegment(sketch, "E1553", {"start": v(36.63, 9.8) * mm, "end": v(36.76, 9.8) * mm});
            skLineSegment(sketch, "E1554", {"start": v(36.76, 9.8) * mm, "end": v(36.9, 9.8) * mm});
            skLineSegment(sketch, "E1555", {"start": v(36.9, 9.8) * mm, "end": v(37.03, 9.8) * mm});
            skLineSegment(sketch, "E1556", {"start": v(37.03, 9.8) * mm, "end": v(37.16, 9.8) * mm});
            skLineSegment(sketch, "E1557", {"start": v(37.16, 9.8) * mm, "end": v(37.29, 9.8) * mm});
            skLineSegment(sketch, "E1558", {"start": v(37.29, 9.8) * mm, "end": v(37.42, 9.8) * mm});
            skLineSegment(sketch, "E1559", {"start": v(37.42, 9.8) * mm, "end": v(37.55, 9.8) * mm});
            skLineSegment(sketch, "E1560", {"start": v(37.55, 9.8) * mm, "end": v(37.68, 9.8) * mm});
            skLineSegment(sketch, "E1561", {"start": v(37.68, 9.8) * mm, "end": v(37.82, 9.8) * mm});
            skLineSegment(sketch, "E1562", {"start": v(37.82, 9.8) * mm, "end": v(37.95, 9.8) * mm});
            skLineSegment(sketch, "E1563", {"start": v(37.95, 9.8) * mm, "end": v(38.08, 9.8) * mm});
            skLineSegment(sketch, "E1564", {"start": v(38.08, 9.8) * mm, "end": v(38.21, 9.8) * mm});
            skLineSegment(sketch, "E1565", {"start": v(38.21, 9.8) * mm, "end": v(38.48, 9.8) * mm});
            skLineSegment(sketch, "E1566", {"start": v(38.48, 9.8) * mm, "end": v(38.75, 9.78) * mm});
            skLineSegment(sketch, "E1567", {"start": v(38.75, 9.78) * mm, "end": v(39, 9.76) * mm});
            skLineSegment(sketch, "E1568", {"start": v(39, 9.76) * mm, "end": v(39.25, 9.73) * mm});
            skLineSegment(sketch, "E1569", {"start": v(39.25, 9.73) * mm, "end": v(39.49, 9.7) * mm});
            skLineSegment(sketch, "E1570", {"start": v(39.49, 9.7) * mm, "end": v(39.71, 9.65) * mm});
            skLineSegment(sketch, "E1571", {"start": v(39.71, 9.65) * mm, "end": v(39.93, 9.6) * mm});
            skLineSegment(sketch, "E1572", {"start": v(39.93, 9.6) * mm, "end": v(40.14, 9.55) * mm});
            skLineSegment(sketch, "E1573", {"start": v(40.14, 9.55) * mm, "end": v(40.34, 9.48) * mm});
            skLineSegment(sketch, "E1574", {"start": v(40.34, 9.48) * mm, "end": v(40.53, 9.4) * mm});
            skLineSegment(sketch, "E1575", {"start": v(40.53, 9.4) * mm, "end": v(40.71, 9.32) * mm});
            skLineSegment(sketch, "E1576", {"start": v(40.71, 9.32) * mm, "end": v(40.88, 9.23) * mm});
            skLineSegment(sketch, "E1577", {"start": v(40.88, 9.23) * mm, "end": v(41.05, 9.14) * mm});
            skLineSegment(sketch, "E1578", {"start": v(41.05, 9.14) * mm, "end": v(41.2, 9.03) * mm});
            skLineSegment(sketch, "E1579", {"start": v(41.2, 9.03) * mm, "end": v(41.34, 8.92) * mm});
            skLineSegment(sketch, "E1580", {"start": v(41.34, 8.92) * mm, "end": v(41.48, 8.8) * mm});
            skLineSegment(sketch, "E1581", {"start": v(41.48, 8.8) * mm, "end": v(41.6, 8.67) * mm});
            skLineSegment(sketch, "E1582", {"start": v(41.6, 8.67) * mm, "end": v(41.72, 8.54) * mm});
            skLineSegment(sketch, "E1583", {"start": v(41.72, 8.54) * mm, "end": v(41.83, 8.4) * mm});
            skLineSegment(sketch, "E1584", {"start": v(41.83, 8.4) * mm, "end": v(41.94, 8.26) * mm});
            skLineSegment(sketch, "E1585", {"start": v(41.94, 8.26) * mm, "end": v(42.03, 8.1) * mm});
            skLineSegment(sketch, "E1586", {"start": v(42.03, 8.1) * mm, "end": v(42.11, 7.95) * mm});
            skLineSegment(sketch, "E1587", {"start": v(42.11, 7.95) * mm, "end": v(42.2, 7.8) * mm});
            skLineSegment(sketch, "E1588", {"start": v(42.2, 7.8) * mm, "end": v(42.26, 7.63) * mm});
            skLineSegment(sketch, "E1589", {"start": v(42.26, 7.63) * mm, "end": v(42.32, 7.46) * mm});
            skLineSegment(sketch, "E1590", {"start": v(42.32, 7.46) * mm, "end": v(42.38, 7.28) * mm});
            skLineSegment(sketch, "E1591", {"start": v(42.38, 7.28) * mm, "end": v(42.42, 7.1) * mm});
            skLineSegment(sketch, "E1592", {"start": v(42.42, 7.1) * mm, "end": v(42.46, 6.9) * mm});
            skLineSegment(sketch, "E1593", {"start": v(42.46, 6.9) * mm, "end": v(42.49, 6.71) * mm});
            skLineSegment(sketch, "E1594", {"start": v(42.49, 6.71) * mm, "end": v(42.5, 6.51) * mm});
            skLineSegment(sketch, "E1595", {"start": v(42.5, 6.51) * mm, "end": v(42.52, 6.3) * mm});
            skLineSegment(sketch, "E1596", {"start": v(42.52, 6.3) * mm, "end": v(42.52, 6.1) * mm});
            skLineSegment(sketch, "E1597", {"start": v(42.52, 6.1) * mm, "end": v(42.52, 5.88) * mm});
            skLineSegment(sketch, "E1598", {"start": v(42.52, 5.88) * mm, "end": v(42.5, 5.67) * mm});
            skLineSegment(sketch, "E1599", {"start": v(42.5, 5.67) * mm, "end": v(42.48, 5.46) * mm});
            skLineSegment(sketch, "E1600", {"start": v(42.48, 5.46) * mm, "end": v(42.44, 5.26) * mm});
            skLineSegment(sketch, "E1601", {"start": v(42.44, 5.26) * mm, "end": v(42.4, 5.06) * mm});
            skLineSegment(sketch, "E1602", {"start": v(42.4, 5.06) * mm, "end": v(42.35, 4.87) * mm});
            skLineSegment(sketch, "E1603", {"start": v(42.35, 4.87) * mm, "end": v(42.28, 4.68) * mm});
            skLineSegment(sketch, "E1604", {"start": v(42.28, 4.68) * mm, "end": v(42.2, 4.5) * mm});
            skLineSegment(sketch, "E1605", {"start": v(42.2, 4.5) * mm, "end": v(42.12, 4.31) * mm});
            skLineSegment(sketch, "E1606", {"start": v(42.12, 4.31) * mm, "end": v(42.03, 4.14) * mm});
            skLineSegment(sketch, "E1607", {"start": v(42.03, 4.14) * mm, "end": v(41.93, 3.97) * mm});
            skLineSegment(sketch, "E1608", {"start": v(41.93, 3.97) * mm, "end": v(41.82, 3.8) * mm});
            skLineSegment(sketch, "E1609", {"start": v(41.82, 3.8) * mm, "end": v(41.7, 3.64) * mm});
            skLineSegment(sketch, "E1610", {"start": v(41.7, 3.64) * mm, "end": v(41.56, 3.49) * mm});
            skLineSegment(sketch, "E1611", {"start": v(41.56, 3.49) * mm, "end": v(41.42, 3.33) * mm});
            skLineSegment(sketch, "E1612", {"start": v(41.42, 3.33) * mm, "end": v(41.27, 3.19) * mm});
            skLineSegment(sketch, "E1613", {"start": v(41.27, 3.19) * mm, "end": v(41.1, 3.05) * mm});
            skLineSegment(sketch, "E1614", {"start": v(41.1, 3.05) * mm, "end": v(40.94, 2.91) * mm});
            skLineSegment(sketch, "E1615", {"start": v(40.94, 2.91) * mm, "end": v(40.77, 2.8) * mm});
            skLineSegment(sketch, "E1616", {"start": v(40.77, 2.8) * mm, "end": v(40.59, 2.68) * mm});
            skLineSegment(sketch, "E1617", {"start": v(40.59, 2.68) * mm, "end": v(40.4, 2.57) * mm});
            skLineSegment(sketch, "E1618", {"start": v(40.4, 2.57) * mm, "end": v(40.21, 2.48) * mm});
            skLineSegment(sketch, "E1619", {"start": v(40.21, 2.48) * mm, "end": v(40.01, 2.4) * mm});
            skLineSegment(sketch, "E1620", {"start": v(40.01, 2.4) * mm, "end": v(39.8, 2.32) * mm});
            skLineSegment(sketch, "E1621", {"start": v(39.8, 2.32) * mm, "end": v(39.6, 2.25) * mm});
            skLineSegment(sketch, "E1622", {"start": v(39.6, 2.25) * mm, "end": v(39.38, 2.19) * mm});
            skLineSegment(sketch, "E1623", {"start": v(39.38, 2.19) * mm, "end": v(39.16, 2.14) * mm});
            skLineSegment(sketch, "E1624", {"start": v(39.16, 2.14) * mm, "end": v(38.93, 2.1) * mm});
            skLineSegment(sketch, "E1625", {"start": v(38.93, 2.1) * mm, "end": v(38.7, 2.07) * mm});
            skLineSegment(sketch, "E1626", {"start": v(38.7, 2.07) * mm, "end": v(38.45, 2.04) * mm});
            skLineSegment(sketch, "E1627", {"start": v(38.45, 2.04) * mm, "end": v(38.2, 2.03) * mm});
            skLineSegment(sketch, "E1628", {"start": v(38.2, 2.03) * mm, "end": v(37.95, 2.03) * mm});
            skLineSegment(sketch, "E1629", {"start": v(37.95, 2.03) * mm, "end": v(37.84, 2.03) * mm});
            skLineSegment(sketch, "E1630", {"start": v(37.84, 2.03) * mm, "end": v(37.72, 2.03) * mm});
            skLineSegment(sketch, "E1631", {"start": v(37.72, 2.03) * mm, "end": v(37.6, 2.03) * mm});
            skLineSegment(sketch, "E1632", {"start": v(37.6, 2.03) * mm, "end": v(37.49, 2.03) * mm});
            skLineSegment(sketch, "E1633", {"start": v(37.49, 2.03) * mm, "end": v(37.37, 2.03) * mm});
            skLineSegment(sketch, "E1634", {"start": v(37.37, 2.03) * mm, "end": v(37.26, 2.03) * mm});
            skLineSegment(sketch, "E1635", {"start": v(37.26, 2.03) * mm, "end": v(37.14, 2.03) * mm});
            skLineSegment(sketch, "E1636", {"start": v(37.14, 2.03) * mm, "end": v(37.03, 2.03) * mm});
            skLineSegment(sketch, "E1637", {"start": v(37.03, 2.03) * mm, "end": v(36.91, 2.03) * mm});
            skLineSegment(sketch, "E1638", {"start": v(36.91, 2.03) * mm, "end": v(36.8, 2.03) * mm});
            skLineSegment(sketch, "E1639", {"start": v(36.8, 2.03) * mm, "end": v(36.68, 2.03) * mm});
            skLineSegment(sketch, "E1640", {"start": v(36.68, 2.03) * mm, "end": v(36.57, 2.03) * mm});
            skLineSegment(sketch, "E1641", {"start": v(36.57, 2.03) * mm, "end": v(36.45, 2.03) * mm});
            skLineSegment(sketch, "E1642", {"start": v(36.45, 2.03) * mm, "end": v(36.33, 2.03) * mm});
            skLineSegment(sketch, "E1643", {"start": v(36.33, 2.03) * mm, "end": v(36.22, 2.03) * mm});
            skLineSegment(sketch, "E1644", {"start": v(36.22, 2.03) * mm, "end": v(36.1, 2.03) * mm});
            skLineSegment(sketch, "E1645", {"start": v(36.1, 2.03) * mm, "end": v(36.1, 2.51) * mm});
            skLineSegment(sketch, "E1646", {"start": v(25.87, 2.02) * mm, "end": v(25.87, -0.1) * mm});
            skLineSegment(sketch, "E1647", {"start": v(25.87, -0.1) * mm, "end": v(25.87, -2.23) * mm});
            skLineSegment(sketch, "E1648", {"start": v(25.87, -2.23) * mm, "end": v(25.87, -4.35) * mm});
            skLineSegment(sketch, "E1649", {"start": v(25.87, -4.35) * mm, "end": v(25.87, -6.47) * mm});
            skLineSegment(sketch, "E1650", {"start": v(25.87, -6.47) * mm, "end": v(25.87, -8.6) * mm});
            skLineSegment(sketch, "E1651", {"start": v(25.87, -8.6) * mm, "end": v(25.87, -9.69) * mm});
            skLineSegment(sketch, "E1652", {"start": v(25.87, -9.69) * mm, "end": v(25.8, -9.52) * mm});
            skLineSegment(sketch, "E1653", {"start": v(25.8, -9.52) * mm, "end": v(25.6, -8.98) * mm});
            skLineSegment(sketch, "E1654", {"start": v(25.6, -8.98) * mm, "end": v(25.4, -8.44) * mm});
            skLineSegment(sketch, "E1655", {"start": v(25.4, -8.44) * mm, "end": v(25.25, -8.08) * mm});
            skLineSegment(sketch, "E1656", {"start": v(25.25, -8.08) * mm, "end": v(25.1, -7.73) * mm});
            skLineSegment(sketch, "E1657", {"start": v(25.1, -7.73) * mm, "end": v(24.95, -7.4) * mm});
            skLineSegment(sketch, "E1658", {"start": v(24.95, -7.4) * mm, "end": v(24.8, -7.07) * mm});
            skLineSegment(sketch, "E1659", {"start": v(24.8, -7.07) * mm, "end": v(24.65, -6.75) * mm});
            skLineSegment(sketch, "E1660", {"start": v(24.65, -6.75) * mm, "end": v(24.5, -6.44) * mm});
            skLineSegment(sketch, "E1661", {"start": v(24.5, -6.44) * mm, "end": v(24.34, -6.15) * mm});
            skLineSegment(sketch, "E1662", {"start": v(24.34, -6.15) * mm, "end": v(24.18, -5.87) * mm});
            skLineSegment(sketch, "E1663", {"start": v(24.18, -5.87) * mm, "end": v(24.02, -5.6) * mm});
            skLineSegment(sketch, "E1664", {"start": v(24.02, -5.6) * mm, "end": v(23.85, -5.34) * mm});
            skLineSegment(sketch, "E1665", {"start": v(23.85, -5.34) * mm, "end": v(23.69, -5.09) * mm});
            skLineSegment(sketch, "E1666", {"start": v(23.69, -5.09) * mm, "end": v(23.52, -4.85) * mm});
            skLineSegment(sketch, "E1667", {"start": v(23.52, -4.85) * mm, "end": v(23.35, -4.62) * mm});
            skLineSegment(sketch, "E1668", {"start": v(23.35, -4.62) * mm, "end": v(23.17, -4.41) * mm});
            skLineSegment(sketch, "E1669", {"start": v(23.17, -4.41) * mm, "end": v(23, -4.2) * mm});
            skLineSegment(sketch, "E1670", {"start": v(23, -4.2) * mm, "end": v(22.82, -4.01) * mm});
            skLineSegment(sketch, "E1671", {"start": v(22.82, -4.01) * mm, "end": v(22.64, -3.83) * mm});
            skLineSegment(sketch, "E1672", {"start": v(22.64, -3.83) * mm, "end": v(22.45, -3.65) * mm});
            skLineSegment(sketch, "E1673", {"start": v(22.45, -3.65) * mm, "end": v(22.26, -3.48) * mm});
            skLineSegment(sketch, "E1674", {"start": v(22.26, -3.48) * mm, "end": v(22.06, -3.32) * mm});
            skLineSegment(sketch, "E1675", {"start": v(22.06, -3.32) * mm, "end": v(21.85, -3.16) * mm});
            skLineSegment(sketch, "E1676", {"start": v(21.85, -3.16) * mm, "end": v(21.64, -3.01) * mm});
            skLineSegment(sketch, "E1677", {"start": v(21.64, -3.01) * mm, "end": v(21.43, -2.87) * mm});
            skLineSegment(sketch, "E1678", {"start": v(21.43, -2.87) * mm, "end": v(21.2, -2.73) * mm});
            skLineSegment(sketch, "E1679", {"start": v(21.2, -2.73) * mm, "end": v(20.98, -2.6) * mm});
            skLineSegment(sketch, "E1680", {"start": v(20.98, -2.6) * mm, "end": v(20.75, -2.47) * mm});
            skLineSegment(sketch, "E1681", {"start": v(20.75, -2.47) * mm, "end": v(20.5, -2.35) * mm});
            skLineSegment(sketch, "E1682", {"start": v(20.5, -2.35) * mm, "end": v(20.27, -2.24) * mm});
            skLineSegment(sketch, "E1683", {"start": v(20.27, -2.24) * mm, "end": v(20.02, -2.14) * mm});
            skLineSegment(sketch, "E1684", {"start": v(20.02, -2.14) * mm, "end": v(19.76, -2.04) * mm});
            skLineSegment(sketch, "E1685", {"start": v(19.76, -2.04) * mm, "end": v(19.5, -1.95) * mm});
            skLineSegment(sketch, "E1686", {"start": v(19.5, -1.95) * mm, "end": v(19.23, -1.86) * mm});
            skLineSegment(sketch, "E1687", {"start": v(19.23, -1.86) * mm, "end": v(19.23, -1.85) * mm});
            skLineSegment(sketch, "E1688", {"start": v(19.23, -1.85) * mm, "end": v(19.23, -1.85) * mm});
            skLineSegment(sketch, "E1689", {"start": v(19.23, -1.85) * mm, "end": v(19.23, -1.84) * mm});
            skLineSegment(sketch, "E1690", {"start": v(19.23, -1.84) * mm, "end": v(19.23, -1.84) * mm});
            skLineSegment(sketch, "E1691", {"start": v(19.23, -1.84) * mm, "end": v(19.23, -1.83) * mm});
            skLineSegment(sketch, "E1692", {"start": v(19.23, -1.83) * mm, "end": v(19.23, -1.82) * mm});
            skLineSegment(sketch, "E1693", {"start": v(19.23, -1.82) * mm, "end": v(19.23, -1.82) * mm});
            skLineSegment(sketch, "E1694", {"start": v(19.23, -1.82) * mm, "end": v(19.23, -1.81) * mm});
            skLineSegment(sketch, "E1695", {"start": v(19.23, -1.81) * mm, "end": v(19.23, -1.8) * mm});
            skLineSegment(sketch, "E1696", {"start": v(19.23, -1.8) * mm, "end": v(19.23, -1.8) * mm});
            skLineSegment(sketch, "E1697", {"start": v(19.23, -1.8) * mm, "end": v(19.23, -1.79) * mm});
            skLineSegment(sketch, "E1698", {"start": v(19.23, -1.79) * mm, "end": v(19.23, -1.78) * mm});
            skLineSegment(sketch, "E1699", {"start": v(19.23, -1.78) * mm, "end": v(19.23, -1.78) * mm});
            skLineSegment(sketch, "E1700", {"start": v(19.23, -1.78) * mm, "end": v(19.23, -1.77) * mm});
            skLineSegment(sketch, "E1701", {"start": v(19.23, -1.77) * mm, "end": v(19.23, -1.76) * mm});
            skLineSegment(sketch, "E1702", {"start": v(19.23, -1.76) * mm, "end": v(19.71, -1.63) * mm});
            skLineSegment(sketch, "E1703", {"start": v(19.71, -1.63) * mm, "end": v(20.18, -1.48) * mm});
            skLineSegment(sketch, "E1704", {"start": v(20.18, -1.48) * mm, "end": v(20.63, -1.32) * mm});
            skLineSegment(sketch, "E1705", {"start": v(20.63, -1.32) * mm, "end": v(21.07, -1.15) * mm});
            skLineSegment(sketch, "E1706", {"start": v(21.07, -1.15) * mm, "end": v(21.49, -0.97) * mm});
            skLineSegment(sketch, "E1707", {"start": v(21.49, -0.97) * mm, "end": v(21.9, -0.78) * mm});
            skLineSegment(sketch, "E1708", {"start": v(21.9, -0.78) * mm, "end": v(22.28, -0.58) * mm});
            skLineSegment(sketch, "E1709", {"start": v(22.28, -0.58) * mm, "end": v(22.66, -0.37) * mm});
            skLineSegment(sketch, "E1710", {"start": v(22.66, -0.37) * mm, "end": v(23.02, -0.15) * mm});
            skLineSegment(sketch, "E1711", {"start": v(23.02, -0.15) * mm, "end": v(23.36, 0.08) * mm});
            skLineSegment(sketch, "E1712", {"start": v(23.36, 0.08) * mm, "end": v(23.7, 0.32) * mm});
            skLineSegment(sketch, "E1713", {"start": v(23.7, 0.32) * mm, "end": v(24, 0.57) * mm});
            skLineSegment(sketch, "E1714", {"start": v(24, 0.57) * mm, "end": v(24.3, 0.83) * mm});
            skLineSegment(sketch, "E1715", {"start": v(24.3, 0.83) * mm, "end": v(24.6, 1.1) * mm});
            skLineSegment(sketch, "E1716", {"start": v(24.6, 1.1) * mm, "end": v(24.86, 1.38) * mm});
            skLineSegment(sketch, "E1717", {"start": v(24.86, 1.38) * mm, "end": v(25.12, 1.67) * mm});
            skLineSegment(sketch, "E1718", {"start": v(25.12, 1.67) * mm, "end": v(25.36, 1.97) * mm});
            skLineSegment(sketch, "E1719", {"start": v(25.36, 1.97) * mm, "end": v(25.58, 2.28) * mm});
            skLineSegment(sketch, "E1720", {"start": v(25.58, 2.28) * mm, "end": v(25.8, 2.6) * mm});
            skLineSegment(sketch, "E1721", {"start": v(25.8, 2.6) * mm, "end": v(25.87, 2.73) * mm});
            skLineSegment(sketch, "E1722", {"start": v(25.87, 2.73) * mm, "end": v(25.87, 2.02) * mm});
            skLineSegment(sketch, "E1723", {"start": v(7.28, 36.34) * mm, "end": v(7.28, 36.34) * mm});
            skLineSegment(sketch, "E1724", {"start": v(7.28, 36.34) * mm, "end": v(7.29, 36.34) * mm});
            skLineSegment(sketch, "E1725", {"start": v(7.29, 36.34) * mm, "end": v(7.3, 36.34) * mm});
            skLineSegment(sketch, "E1726", {"start": v(7.3, 36.34) * mm, "end": v(7.3, 36.34) * mm});
            skLineSegment(sketch, "E1727", {"start": v(7.3, 36.34) * mm, "end": v(7.31, 36.34) * mm});
            skLineSegment(sketch, "E1728", {"start": v(7.31, 36.34) * mm, "end": v(7.32, 36.34) * mm});
            skLineSegment(sketch, "E1729", {"start": v(7.32, 36.34) * mm, "end": v(7.33, 36.34) * mm});
            skLineSegment(sketch, "E1730", {"start": v(7.33, 36.34) * mm, "end": v(7.33, 36.34) * mm});
            skLineSegment(sketch, "E1731", {"start": v(7.33, 36.34) * mm, "end": v(7.34, 36.34) * mm});
            skLineSegment(sketch, "E1732", {"start": v(7.34, 36.34) * mm, "end": v(7.34, 36.34) * mm});
            skLineSegment(sketch, "E1733", {"start": v(7.34, 36.34) * mm, "end": v(7.35, 36.34) * mm});
            skLineSegment(sketch, "E1734", {"start": v(7.35, 36.34) * mm, "end": v(7.35, 36.34) * mm});
            skLineSegment(sketch, "E1735", {"start": v(7.35, 36.34) * mm, "end": v(7.36, 36.34) * mm});
            skLineSegment(sketch, "E1736", {"start": v(7.36, 36.34) * mm, "end": v(7.37, 36.34) * mm});
            skLineSegment(sketch, "E1737", {"start": v(7.37, 36.34) * mm, "end": v(7.48, 36.14) * mm});
            skLineSegment(sketch, "E1738", {"start": v(7.48, 36.14) * mm, "end": v(7.6, 35.94) * mm});
            skLineSegment(sketch, "E1739", {"start": v(7.6, 35.94) * mm, "end": v(7.72, 35.74) * mm});
            skLineSegment(sketch, "E1740", {"start": v(7.72, 35.74) * mm, "end": v(7.85, 35.53) * mm});
            skLineSegment(sketch, "E1741", {"start": v(7.85, 35.53) * mm, "end": v(7.98, 35.32) * mm});
            skLineSegment(sketch, "E1742", {"start": v(7.98, 35.32) * mm, "end": v(8.11, 35.11) * mm});
            skLineSegment(sketch, "E1743", {"start": v(8.11, 35.11) * mm, "end": v(8.25, 34.9) * mm});
            skLineSegment(sketch, "E1744", {"start": v(8.25, 34.9) * mm, "end": v(8.4, 34.68) * mm});
            skLineSegment(sketch, "E1745", {"start": v(8.4, 34.68) * mm, "end": v(8.54, 34.46) * mm});
            skLineSegment(sketch, "E1746", {"start": v(8.54, 34.46) * mm, "end": v(8.7, 34.23) * mm});
            skLineSegment(sketch, "E1747", {"start": v(8.7, 34.23) * mm, "end": v(8.85, 34) * mm});
            skLineSegment(sketch, "E1748", {"start": v(8.85, 34) * mm, "end": v(9, 33.78) * mm});
            skLineSegment(sketch, "E1749", {"start": v(9, 33.78) * mm, "end": v(9.17, 33.55) * mm});
            skLineSegment(sketch, "E1750", {"start": v(9.17, 33.55) * mm, "end": v(9.34, 33.31) * mm});
            skLineSegment(sketch, "E1751", {"start": v(9.34, 33.31) * mm, "end": v(9.51, 33.07) * mm});
            skLineSegment(sketch, "E1752", {"start": v(9.51, 33.07) * mm, "end": v(9.69, 32.83) * mm});
            skLineSegment(sketch, "E1753", {"start": v(9.69, 32.83) * mm, "end": v(10.44, 31.8) * mm});
            skLineSegment(sketch, "E1754", {"start": v(10.44, 31.8) * mm, "end": v(11.19, 30.78) * mm});
            skLineSegment(sketch, "E1755", {"start": v(11.19, 30.78) * mm, "end": v(11.94, 29.76) * mm});
            skLineSegment(sketch, "E1756", {"start": v(11.94, 29.76) * mm, "end": v(12.68, 28.73) * mm});
            skLineSegment(sketch, "E1757", {"start": v(12.68, 28.73) * mm, "end": v(13.43, 27.7) * mm});
            skLineSegment(sketch, "E1758", {"start": v(13.43, 27.7) * mm, "end": v(14.18, 26.68) * mm});
            skLineSegment(sketch, "E1759", {"start": v(14.18, 26.68) * mm, "end": v(14.93, 25.66) * mm});
            skLineSegment(sketch, "E1760", {"start": v(14.93, 25.66) * mm, "end": v(15.68, 24.64) * mm});
            skLineSegment(sketch, "E1761", {"start": v(15.68, 24.64) * mm, "end": v(16.43, 23.61) * mm});
            skLineSegment(sketch, "E1762", {"start": v(16.43, 23.61) * mm, "end": v(17.18, 22.59) * mm});
            skLineSegment(sketch, "E1763", {"start": v(17.18, 22.59) * mm, "end": v(17.93, 21.56) * mm});
            skLineSegment(sketch, "E1764", {"start": v(17.93, 21.56) * mm, "end": v(18.68, 20.54) * mm});
            skLineSegment(sketch, "E1765", {"start": v(18.68, 20.54) * mm, "end": v(19.43, 19.51) * mm});
            skLineSegment(sketch, "E1766", {"start": v(19.43, 19.51) * mm, "end": v(20.17, 18.49) * mm});
            skLineSegment(sketch, "E1767", {"start": v(20.17, 18.49) * mm, "end": v(20.92, 17.47) * mm});
            skLineSegment(sketch, "E1768", {"start": v(20.92, 17.47) * mm, "end": v(21.67, 16.44) * mm});
            skLineSegment(sketch, "E1769", {"start": v(21.67, 16.44) * mm, "end": v(22.23, 16.44) * mm});
            skLineSegment(sketch, "E1770", {"start": v(22.23, 16.44) * mm, "end": v(22.8, 16.44) * mm});
            skLineSegment(sketch, "E1771", {"start": v(22.8, 16.44) * mm, "end": v(23.36, 16.44) * mm});
            skLineSegment(sketch, "E1772", {"start": v(23.36, 16.44) * mm, "end": v(23.92, 16.44) * mm});
            skLineSegment(sketch, "E1773", {"start": v(23.92, 16.44) * mm, "end": v(24.48, 16.44) * mm});
            skLineSegment(sketch, "E1774", {"start": v(24.48, 16.44) * mm, "end": v(25.04, 16.44) * mm});
            skLineSegment(sketch, "E1775", {"start": v(25.04, 16.44) * mm, "end": v(25.6, 16.44) * mm});
            skLineSegment(sketch, "E1776", {"start": v(25.6, 16.44) * mm, "end": v(25.87, 16.44) * mm});
            skLineSegment(sketch, "E1777", {"start": v(25.87, 16.44) * mm, "end": v(25.87, 14.75) * mm});
            skLineSegment(sketch, "E1778", {"start": v(25.87, 14.75) * mm, "end": v(25.87, 12.63) * mm});
            skLineSegment(sketch, "E1779", {"start": v(25.87, 12.63) * mm, "end": v(25.87, 12.3) * mm});
            skLineSegment(sketch, "E1780", {"start": v(25.87, 12.3) * mm, "end": v(25.77, 12.46) * mm});
            skLineSegment(sketch, "E1781", {"start": v(25.77, 12.46) * mm, "end": v(25.49, 12.86) * mm});
            skLineSegment(sketch, "E1782", {"start": v(25.49, 12.86) * mm, "end": v(25.18, 13.23) * mm});
            skLineSegment(sketch, "E1783", {"start": v(25.18, 13.23) * mm, "end": v(24.85, 13.59) * mm});
            skLineSegment(sketch, "E1784", {"start": v(24.85, 13.59) * mm, "end": v(24.5, 13.92) * mm});
            skLineSegment(sketch, "E1785", {"start": v(24.5, 13.92) * mm, "end": v(24.1, 14.24) * mm});
            skLineSegment(sketch, "E1786", {"start": v(24.1, 14.24) * mm, "end": v(23.7, 14.54) * mm});
            skLineSegment(sketch, "E1787", {"start": v(23.7, 14.54) * mm, "end": v(23.26, 14.83) * mm});
            skLineSegment(sketch, "E1788", {"start": v(23.26, 14.83) * mm, "end": v(22.79, 15.09) * mm});
            skLineSegment(sketch, "E1789", {"start": v(22.79, 15.09) * mm, "end": v(22.3, 15.34) * mm});
            skLineSegment(sketch, "E1790", {"start": v(22.3, 15.34) * mm, "end": v(21.76, 15.56) * mm});
            skLineSegment(sketch, "E1791", {"start": v(21.76, 15.56) * mm, "end": v(21.2, 15.77) * mm});
            skLineSegment(sketch, "E1792", {"start": v(21.2, 15.77) * mm, "end": v(20.62, 15.96) * mm});
            skLineSegment(sketch, "E1793", {"start": v(20.62, 15.96) * mm, "end": v(20, 16.14) * mm});
            skLineSegment(sketch, "E1794", {"start": v(20, 16.14) * mm, "end": v(19.37, 16.3) * mm});
            skLineSegment(sketch, "E1795", {"start": v(19.37, 16.3) * mm, "end": v(18.7, 16.43) * mm});
            skLineSegment(sketch, "E1796", {"start": v(18.7, 16.43) * mm, "end": v(18, 16.55) * mm});
            skLineSegment(sketch, "E1797", {"start": v(18, 16.55) * mm, "end": v(17.26, 16.65) * mm});
            skLineSegment(sketch, "E1798", {"start": v(17.26, 16.65) * mm, "end": v(16.5, 16.73) * mm});
            skLineSegment(sketch, "E1799", {"start": v(16.5, 16.73) * mm, "end": v(15.71, 16.8) * mm});
            skLineSegment(sketch, "E1800", {"start": v(15.71, 16.8) * mm, "end": v(14.9, 16.84) * mm});
            skLineSegment(sketch, "E1801", {"start": v(14.9, 16.84) * mm, "end": v(14.05, 16.87) * mm});
            skLineSegment(sketch, "E1802", {"start": v(14.05, 16.87) * mm, "end": v(13.17, 16.88) * mm});
            skLineSegment(sketch, "E1803", {"start": v(13.17, 16.88) * mm, "end": v(12.32, 16.88) * mm});
            skLineSegment(sketch, "E1804", {"start": v(12.32, 16.88) * mm, "end": v(11.47, 16.88) * mm});
            skLineSegment(sketch, "E1805", {"start": v(11.47, 16.88) * mm, "end": v(10.62, 16.88) * mm});
            skLineSegment(sketch, "E1806", {"start": v(10.62, 16.88) * mm, "end": v(9.77, 16.88) * mm});
            skLineSegment(sketch, "E1807", {"start": v(9.77, 16.88) * mm, "end": v(8.92, 16.88) * mm});
            skLineSegment(sketch, "E1808", {"start": v(8.92, 16.88) * mm, "end": v(8.07, 16.88) * mm});
            skLineSegment(sketch, "E1809", {"start": v(8.07, 16.88) * mm, "end": v(7.41, 16.88) * mm});
            skLineSegment(sketch, "E1810", {"start": v(7.41, 16.88) * mm, "end": v(7.41, 17.33) * mm});
            skLineSegment(sketch, "E1811", {"start": v(7.41, 17.33) * mm, "end": v(7.41, 18.22) * mm});
            skLineSegment(sketch, "E1812", {"start": v(7.41, 18.22) * mm, "end": v(7.41, 19.11) * mm});
            skLineSegment(sketch, "E1813", {"start": v(7.41, 19.11) * mm, "end": v(7.41, 20) * mm});
            skLineSegment(sketch, "E1814", {"start": v(7.41, 20) * mm, "end": v(7.41, 20.9) * mm});
            skLineSegment(sketch, "E1815", {"start": v(7.41, 20.9) * mm, "end": v(7.41, 21.79) * mm});
            skLineSegment(sketch, "E1816", {"start": v(7.41, 21.79) * mm, "end": v(7.41, 22.68) * mm});
            skLineSegment(sketch, "E1817", {"start": v(7.41, 22.68) * mm, "end": v(7.41, 23.57) * mm});
            skLineSegment(sketch, "E1818", {"start": v(7.41, 23.57) * mm, "end": v(7.41, 24.46) * mm});
            skLineSegment(sketch, "E1819", {"start": v(7.41, 24.46) * mm, "end": v(7.41, 25.35) * mm});
            skLineSegment(sketch, "E1820", {"start": v(7.41, 25.35) * mm, "end": v(7.41, 26.24) * mm});
            skLineSegment(sketch, "E1821", {"start": v(7.41, 26.24) * mm, "end": v(7.41, 27.13) * mm});
            skLineSegment(sketch, "E1822", {"start": v(7.41, 27.13) * mm, "end": v(7.41, 28.03) * mm});
            skLineSegment(sketch, "E1823", {"start": v(7.41, 28.03) * mm, "end": v(7.41, 28.92) * mm});
            skLineSegment(sketch, "E1824", {"start": v(7.41, 28.92) * mm, "end": v(7.41, 29.8) * mm});
            skLineSegment(sketch, "E1825", {"start": v(7.41, 29.8) * mm, "end": v(7.41, 30.7) * mm});
            skLineSegment(sketch, "E1826", {"start": v(7.41, 30.7) * mm, "end": v(7.41, 31.09) * mm});
            skLineSegment(sketch, "E1827", {"start": v(7.41, 31.09) * mm, "end": v(7.41, 31.47) * mm});
            skLineSegment(sketch, "E1828", {"start": v(7.41, 31.47) * mm, "end": v(7.4, 31.85) * mm});
            skLineSegment(sketch, "E1829", {"start": v(7.4, 31.85) * mm, "end": v(7.4, 32.22) * mm});
            skLineSegment(sketch, "E1830", {"start": v(7.4, 32.22) * mm, "end": v(7.4, 32.6) * mm});
            skLineSegment(sketch, "E1831", {"start": v(7.4, 32.6) * mm, "end": v(7.4, 32.96) * mm});
            skLineSegment(sketch, "E1832", {"start": v(7.4, 32.96) * mm, "end": v(7.39, 33.32) * mm});
            skLineSegment(sketch, "E1833", {"start": v(7.39, 33.32) * mm, "end": v(7.38, 33.67) * mm});
            skLineSegment(sketch, "E1834", {"start": v(7.38, 33.67) * mm, "end": v(7.37, 34.02) * mm});
            skLineSegment(sketch, "E1835", {"start": v(7.37, 34.02) * mm, "end": v(7.36, 34.37) * mm});
            skLineSegment(sketch, "E1836", {"start": v(7.36, 34.37) * mm, "end": v(7.35, 34.7) * mm});
            skLineSegment(sketch, "E1837", {"start": v(7.35, 34.7) * mm, "end": v(7.33, 35.04) * mm});
            skLineSegment(sketch, "E1838", {"start": v(7.33, 35.04) * mm, "end": v(7.32, 35.37) * mm});
            skLineSegment(sketch, "E1839", {"start": v(7.32, 35.37) * mm, "end": v(7.3, 35.7) * mm});
            skLineSegment(sketch, "E1840", {"start": v(7.3, 35.7) * mm, "end": v(7.29, 36.02) * mm});
            skLineSegment(sketch, "E1841", {"start": v(7.29, 36.02) * mm, "end": v(7.27, 36.34) * mm});
            skLineSegment(sketch, "E1842", {"start": v(7.27, 36.34) * mm, "end": v(7.28, 36.34) * mm});
            skLineSegment(sketch, "E1843", {"start": v(16.22, 6.1) * mm, "end": v(16.22, 5.88) * mm});
            skLineSegment(sketch, "E1844", {"start": v(16.22, 5.88) * mm, "end": v(16.2, 5.67) * mm});
            skLineSegment(sketch, "E1845", {"start": v(16.2, 5.67) * mm, "end": v(16.18, 5.46) * mm});
            skLineSegment(sketch, "E1846", {"start": v(16.18, 5.46) * mm, "end": v(16.15, 5.26) * mm});
            skLineSegment(sketch, "E1847", {"start": v(16.15, 5.26) * mm, "end": v(16.1, 5.06) * mm});
            skLineSegment(sketch, "E1848", {"start": v(16.1, 5.06) * mm, "end": v(16.05, 4.87) * mm});
            skLineSegment(sketch, "E1849", {"start": v(16.05, 4.87) * mm, "end": v(15.98, 4.68) * mm});
            skLineSegment(sketch, "E1850", {"start": v(15.98, 4.68) * mm, "end": v(15.91, 4.5) * mm});
            skLineSegment(sketch, "E1851", {"start": v(15.91, 4.5) * mm, "end": v(15.83, 4.31) * mm});
            skLineSegment(sketch, "E1852", {"start": v(15.83, 4.31) * mm, "end": v(15.73, 4.14) * mm});
            skLineSegment(sketch, "E1853", {"start": v(15.73, 4.14) * mm, "end": v(15.63, 3.97) * mm});
            skLineSegment(sketch, "E1854", {"start": v(15.63, 3.97) * mm, "end": v(15.52, 3.8) * mm});
            skLineSegment(sketch, "E1855", {"start": v(15.52, 3.8) * mm, "end": v(15.4, 3.64) * mm});
            skLineSegment(sketch, "E1856", {"start": v(15.4, 3.64) * mm, "end": v(15.26, 3.49) * mm});
            skLineSegment(sketch, "E1857", {"start": v(15.26, 3.49) * mm, "end": v(15.12, 3.33) * mm});
            skLineSegment(sketch, "E1858", {"start": v(15.12, 3.33) * mm, "end": v(14.97, 3.19) * mm});
            skLineSegment(sketch, "E1859", {"start": v(14.97, 3.19) * mm, "end": v(14.8, 3.05) * mm});
            skLineSegment(sketch, "E1860", {"start": v(14.8, 3.05) * mm, "end": v(14.64, 2.91) * mm});
            skLineSegment(sketch, "E1861", {"start": v(14.64, 2.91) * mm, "end": v(14.47, 2.8) * mm});
            skLineSegment(sketch, "E1862", {"start": v(14.47, 2.8) * mm, "end": v(14.3, 2.68) * mm});
            skLineSegment(sketch, "E1863", {"start": v(14.3, 2.68) * mm, "end": v(14.1, 2.57) * mm});
            skLineSegment(sketch, "E1864", {"start": v(14.1, 2.57) * mm, "end": v(13.91, 2.48) * mm});
            skLineSegment(sketch, "E1865", {"start": v(13.91, 2.48) * mm, "end": v(13.72, 2.4) * mm});
            skLineSegment(sketch, "E1866", {"start": v(13.72, 2.4) * mm, "end": v(13.51, 2.32) * mm});
            skLineSegment(sketch, "E1867", {"start": v(13.51, 2.32) * mm, "end": v(13.3, 2.25) * mm});
            skLineSegment(sketch, "E1868", {"start": v(13.3, 2.25) * mm, "end": v(13.09, 2.19) * mm});
            skLineSegment(sketch, "E1869", {"start": v(13.09, 2.19) * mm, "end": v(12.86, 2.14) * mm});
            skLineSegment(sketch, "E1870", {"start": v(12.86, 2.14) * mm, "end": v(12.63, 2.1) * mm});
            skLineSegment(sketch, "E1871", {"start": v(12.63, 2.1) * mm, "end": v(12.4, 2.07) * mm});
            skLineSegment(sketch, "E1872", {"start": v(12.4, 2.07) * mm, "end": v(12.16, 2.04) * mm});
            skLineSegment(sketch, "E1873", {"start": v(12.16, 2.04) * mm, "end": v(11.9, 2.03) * mm});
            skLineSegment(sketch, "E1874", {"start": v(11.9, 2.03) * mm, "end": v(11.65, 2.03) * mm});
            skLineSegment(sketch, "E1875", {"start": v(11.65, 2.03) * mm, "end": v(11.54, 2.03) * mm});
            skLineSegment(sketch, "E1876", {"start": v(11.54, 2.03) * mm, "end": v(11.42, 2.03) * mm});
            skLineSegment(sketch, "E1877", {"start": v(11.42, 2.03) * mm, "end": v(11.3, 2.03) * mm});
            skLineSegment(sketch, "E1878", {"start": v(11.3, 2.03) * mm, "end": v(11.2, 2.03) * mm});
            skLineSegment(sketch, "E1879", {"start": v(11.2, 2.03) * mm, "end": v(11.08, 2.03) * mm});
            skLineSegment(sketch, "E1880", {"start": v(11.08, 2.03) * mm, "end": v(10.96, 2.03) * mm});
            skLineSegment(sketch, "E1881", {"start": v(10.96, 2.03) * mm, "end": v(10.85, 2.03) * mm});
            skLineSegment(sketch, "E1882", {"start": v(10.85, 2.03) * mm, "end": v(10.73, 2.03) * mm});
            skLineSegment(sketch, "E1883", {"start": v(10.73, 2.03) * mm, "end": v(10.61, 2.03) * mm});
            skLineSegment(sketch, "E1884", {"start": v(10.61, 2.03) * mm, "end": v(10.5, 2.03) * mm});
            skLineSegment(sketch, "E1885", {"start": v(10.5, 2.03) * mm, "end": v(10.38, 2.03) * mm});
            skLineSegment(sketch, "E1886", {"start": v(10.38, 2.03) * mm, "end": v(10.27, 2.03) * mm});
            skLineSegment(sketch, "E1887", {"start": v(10.27, 2.03) * mm, "end": v(10.15, 2.03) * mm});
            skLineSegment(sketch, "E1888", {"start": v(10.15, 2.03) * mm, "end": v(10.04, 2.03) * mm});
            skLineSegment(sketch, "E1889", {"start": v(10.04, 2.03) * mm, "end": v(9.92, 2.03) * mm});
            skLineSegment(sketch, "E1890", {"start": v(9.92, 2.03) * mm, "end": v(9.8, 2.03) * mm});
            skLineSegment(sketch, "E1891", {"start": v(9.8, 2.03) * mm, "end": v(9.8, 2.51) * mm});
            skLineSegment(sketch, "E1892", {"start": v(9.8, 2.51) * mm, "end": v(9.8, 3) * mm});
            skLineSegment(sketch, "E1893", {"start": v(9.8, 3) * mm, "end": v(9.8, 3.48) * mm});
            skLineSegment(sketch, "E1894", {"start": v(9.8, 3.48) * mm, "end": v(9.8, 3.97) * mm});
            skLineSegment(sketch, "E1895", {"start": v(9.8, 3.97) * mm, "end": v(9.8, 4.45) * mm});
            skLineSegment(sketch, "E1896", {"start": v(9.8, 4.45) * mm, "end": v(9.8, 4.94) * mm});
            skLineSegment(sketch, "E1897", {"start": v(9.8, 4.94) * mm, "end": v(9.8, 5.42) * mm});
            skLineSegment(sketch, "E1898", {"start": v(9.8, 5.42) * mm, "end": v(9.8, 5.9) * mm});
            skLineSegment(sketch, "E1899", {"start": v(9.8, 5.9) * mm, "end": v(9.8, 6.4) * mm});
            skLineSegment(sketch, "E1900", {"start": v(9.8, 6.4) * mm, "end": v(9.8, 6.88) * mm});
            skLineSegment(sketch, "E1901", {"start": v(9.8, 6.88) * mm, "end": v(9.8, 7.37) * mm});
            skLineSegment(sketch, "E1902", {"start": v(9.8, 7.37) * mm, "end": v(9.8, 7.85) * mm});
            skLineSegment(sketch, "E1903", {"start": v(9.8, 7.85) * mm, "end": v(9.8, 8.34) * mm});
            skLineSegment(sketch, "E1904", {"start": v(9.8, 8.34) * mm, "end": v(9.8, 8.82) * mm});
            skLineSegment(sketch, "E1905", {"start": v(9.8, 8.82) * mm, "end": v(9.8, 9.3) * mm});
            skLineSegment(sketch, "E1906", {"start": v(9.8, 9.3) * mm, "end": v(9.8, 9.8) * mm});
            skLineSegment(sketch, "E1907", {"start": v(9.8, 9.8) * mm, "end": v(9.94, 9.8) * mm});
            skLineSegment(sketch, "E1908", {"start": v(9.94, 9.8) * mm, "end": v(10.07, 9.8) * mm});
            skLineSegment(sketch, "E1909", {"start": v(10.07, 9.8) * mm, "end": v(10.2, 9.8) * mm});
            skLineSegment(sketch, "E1910", {"start": v(10.2, 9.8) * mm, "end": v(10.33, 9.8) * mm});
            skLineSegment(sketch, "E1911", {"start": v(10.33, 9.8) * mm, "end": v(10.46, 9.8) * mm});
            skLineSegment(sketch, "E1912", {"start": v(10.46, 9.8) * mm, "end": v(10.6, 9.8) * mm});
            skLineSegment(sketch, "E1913", {"start": v(10.6, 9.8) * mm, "end": v(10.73, 9.8) * mm});
            skLineSegment(sketch, "E1914", {"start": v(10.73, 9.8) * mm, "end": v(10.86, 9.8) * mm});
            skLineSegment(sketch, "E1915", {"start": v(10.86, 9.8) * mm, "end": v(11, 9.8) * mm});
            skLineSegment(sketch, "E1916", {"start": v(11, 9.8) * mm, "end": v(11.12, 9.8) * mm});
            skLineSegment(sketch, "E1917", {"start": v(11.12, 9.8) * mm, "end": v(11.26, 9.8) * mm});
            skLineSegment(sketch, "E1918", {"start": v(11.26, 9.8) * mm, "end": v(11.39, 9.8) * mm});
            skLineSegment(sketch, "E1919", {"start": v(11.39, 9.8) * mm, "end": v(11.52, 9.8) * mm});
            skLineSegment(sketch, "E1920", {"start": v(11.52, 9.8) * mm, "end": v(11.65, 9.8) * mm});
            skLineSegment(sketch, "E1921", {"start": v(11.65, 9.8) * mm, "end": v(11.78, 9.8) * mm});
            skLineSegment(sketch, "E1922", {"start": v(11.78, 9.8) * mm, "end": v(11.91, 9.8) * mm});
            skLineSegment(sketch, "E1923", {"start": v(11.91, 9.8) * mm, "end": v(12.19, 9.8) * mm});
            skLineSegment(sketch, "E1924", {"start": v(12.19, 9.8) * mm, "end": v(12.45, 9.78) * mm});
            skLineSegment(sketch, "E1925", {"start": v(12.45, 9.78) * mm, "end": v(12.7, 9.76) * mm});
            skLineSegment(sketch, "E1926", {"start": v(12.7, 9.76) * mm, "end": v(12.95, 9.73) * mm});
            skLineSegment(sketch, "E1927", {"start": v(12.95, 9.73) * mm, "end": v(13.19, 9.7) * mm});
            skLineSegment(sketch, "E1928", {"start": v(13.19, 9.7) * mm, "end": v(13.42, 9.65) * mm});
            skLineSegment(sketch, "E1929", {"start": v(13.42, 9.65) * mm, "end": v(13.64, 9.6) * mm});
            skLineSegment(sketch, "E1930", {"start": v(13.64, 9.6) * mm, "end": v(13.84, 9.55) * mm});
            skLineSegment(sketch, "E1931", {"start": v(13.84, 9.55) * mm, "end": v(14.04, 9.48) * mm});
            skLineSegment(sketch, "E1932", {"start": v(14.04, 9.48) * mm, "end": v(14.23, 9.4) * mm});
            skLineSegment(sketch, "E1933", {"start": v(14.23, 9.4) * mm, "end": v(14.42, 9.32) * mm});
            skLineSegment(sketch, "E1934", {"start": v(14.42, 9.32) * mm, "end": v(14.59, 9.23) * mm});
            skLineSegment(sketch, "E1935", {"start": v(14.59, 9.23) * mm, "end": v(14.75, 9.14) * mm});
            skLineSegment(sketch, "E1936", {"start": v(14.75, 9.14) * mm, "end": v(14.9, 9.03) * mm});
            skLineSegment(sketch, "E1937", {"start": v(14.9, 9.03) * mm, "end": v(15.05, 8.92) * mm});
            skLineSegment(sketch, "E1938", {"start": v(15.05, 8.92) * mm, "end": v(15.18, 8.8) * mm});
            skLineSegment(sketch, "E1939", {"start": v(15.18, 8.8) * mm, "end": v(15.3, 8.67) * mm});
            skLineSegment(sketch, "E1940", {"start": v(15.3, 8.67) * mm, "end": v(15.43, 8.54) * mm});
            skLineSegment(sketch, "E1941", {"start": v(15.43, 8.54) * mm, "end": v(15.54, 8.4) * mm});
            skLineSegment(sketch, "E1942", {"start": v(15.54, 8.4) * mm, "end": v(15.64, 8.26) * mm});
            skLineSegment(sketch, "E1943", {"start": v(15.64, 8.26) * mm, "end": v(15.73, 8.1) * mm});
            skLineSegment(sketch, "E1944", {"start": v(15.73, 8.1) * mm, "end": v(15.82, 7.95) * mm});
            skLineSegment(sketch, "E1945", {"start": v(15.82, 7.95) * mm, "end": v(15.9, 7.8) * mm});
            skLineSegment(sketch, "E1946", {"start": v(15.9, 7.8) * mm, "end": v(15.96, 7.63) * mm});
            skLineSegment(sketch, "E1947", {"start": v(15.96, 7.63) * mm, "end": v(16.03, 7.46) * mm});
            skLineSegment(sketch, "E1948", {"start": v(16.03, 7.46) * mm, "end": v(16.08, 7.28) * mm});
            skLineSegment(sketch, "E1949", {"start": v(16.08, 7.28) * mm, "end": v(16.12, 7.1) * mm});
            skLineSegment(sketch, "E1950", {"start": v(16.12, 7.1) * mm, "end": v(16.16, 6.9) * mm});
            skLineSegment(sketch, "E1951", {"start": v(16.16, 6.9) * mm, "end": v(16.19, 6.71) * mm});
            skLineSegment(sketch, "E1952", {"start": v(16.19, 6.71) * mm, "end": v(16.2, 6.51) * mm});
            skLineSegment(sketch, "E1953", {"start": v(16.2, 6.51) * mm, "end": v(16.22, 6.3) * mm});
            skLineSegment(sketch, "E1954", {"start": v(16.22, 6.3) * mm, "end": v(16.22, 6.1) * mm});
            skLineSegment(sketch, "E1955", {"start": v(-11.9, 17.33) * mm, "end": v(-11.38, 17.56) * mm});
            skLineSegment(sketch, "E1956", {"start": v(-11.38, 17.56) * mm, "end": v(-10.88, 17.82) * mm});
            skLineSegment(sketch, "E1957", {"start": v(-10.88, 17.82) * mm, "end": v(-10.38, 18.09) * mm});
            skLineSegment(sketch, "E1958", {"start": v(-10.38, 18.09) * mm, "end": v(-9.9, 18.37) * mm});
            skLineSegment(sketch, "E1959", {"start": v(-9.9, 18.37) * mm, "end": v(-9.42, 18.67) * mm});
            skLineSegment(sketch, "E1960", {"start": v(-9.42, 18.67) * mm, "end": v(-8.96, 18.99) * mm});
            skLineSegment(sketch, "E1961", {"start": v(-8.96, 18.99) * mm, "end": v(-8.51, 19.32) * mm});
            skLineSegment(sketch, "E1962", {"start": v(-8.51, 19.32) * mm, "end": v(-8.08, 19.66) * mm});
            skLineSegment(sketch, "E1963", {"start": v(-8.08, 19.66) * mm, "end": v(-7.66, 20.02) * mm});
            skLineSegment(sketch, "E1964", {"start": v(-7.66, 20.02) * mm, "end": v(-7.25, 20.39) * mm});
            skLineSegment(sketch, "E1965", {"start": v(-7.25, 20.39) * mm, "end": v(-6.86, 20.77) * mm});
            skLineSegment(sketch, "E1966", {"start": v(-6.86, 20.77) * mm, "end": v(-6.48, 21.17) * mm});
            skLineSegment(sketch, "E1967", {"start": v(-6.48, 21.17) * mm, "end": v(-6.12, 21.59) * mm});
            skLineSegment(sketch, "E1968", {"start": v(-6.12, 21.59) * mm, "end": v(-5.77, 22.02) * mm});
            skLineSegment(sketch, "E1969", {"start": v(-5.77, 22.02) * mm, "end": v(-5.43, 22.46) * mm});
            skLineSegment(sketch, "E1970", {"start": v(-5.43, 22.46) * mm, "end": v(-5.1, 22.91) * mm});
            skLineSegment(sketch, "E1971", {"start": v(-5.1, 22.91) * mm, "end": v(-4.8, 23.38) * mm});
            skLineSegment(sketch, "E1972", {"start": v(-4.8, 23.38) * mm, "end": v(-4.5, 23.87) * mm});
            skLineSegment(sketch, "E1973", {"start": v(-4.5, 23.87) * mm, "end": v(-4.22, 24.36) * mm});
            skLineSegment(sketch, "E1974", {"start": v(-4.22, 24.36) * mm, "end": v(-3.95, 24.87) * mm});
            skLineSegment(sketch, "E1975", {"start": v(-3.95, 24.87) * mm, "end": v(-3.7, 25.39) * mm});
            skLineSegment(sketch, "E1976", {"start": v(-3.7, 25.39) * mm, "end": v(-3.47, 25.92) * mm});
            skLineSegment(sketch, "E1977", {"start": v(-3.47, 25.92) * mm, "end": v(-3.26, 26.45) * mm});
            skLineSegment(sketch, "E1978", {"start": v(-3.26, 26.45) * mm, "end": v(-3.06, 27) * mm});
            skLineSegment(sketch, "E1979", {"start": v(-3.06, 27) * mm, "end": v(-2.88, 27.54) * mm});
            skLineSegment(sketch, "E1980", {"start": v(-2.88, 27.54) * mm, "end": v(-2.71, 28.1) * mm});
            skLineSegment(sketch, "E1981", {"start": v(-2.71, 28.1) * mm, "end": v(-2.57, 28.67) * mm});
            skLineSegment(sketch, "E1982", {"start": v(-2.57, 28.67) * mm, "end": v(-2.44, 29.25) * mm});
            skLineSegment(sketch, "E1983", {"start": v(-2.44, 29.25) * mm, "end": v(-2.33, 29.83) * mm});
            skLineSegment(sketch, "E1984", {"start": v(-2.33, 29.83) * mm, "end": v(-2.23, 30.43) * mm});
            skLineSegment(sketch, "E1985", {"start": v(-2.23, 30.43) * mm, "end": v(-2.15, 31.03) * mm});
            skLineSegment(sketch, "E1986", {"start": v(-2.15, 31.03) * mm, "end": v(-2.1, 31.64) * mm});
            skLineSegment(sketch, "E1987", {"start": v(-2.1, 31.64) * mm, "end": v(-2.06, 32.14) * mm});
            skLineSegment(sketch, "E1988", {"start": v(-2.06, 32.14) * mm, "end": v(-2.06, 31.3) * mm});
            skLineSegment(sketch, "E1989", {"start": v(-2.06, 31.3) * mm, "end": v(-2.06, 29.18) * mm});
            skLineSegment(sketch, "E1990", {"start": v(-2.06, 29.18) * mm, "end": v(-2.06, 27.05) * mm});
            skLineSegment(sketch, "E1991", {"start": v(-2.06, 27.05) * mm, "end": v(-2.06, 24.93) * mm});
            skLineSegment(sketch, "E1992", {"start": v(-2.06, 24.93) * mm, "end": v(-2.06, 22.8) * mm});
            skLineSegment(sketch, "E1993", {"start": v(-2.06, 22.8) * mm, "end": v(-2.06, 20.69) * mm});
            skLineSegment(sketch, "E1994", {"start": v(-2.06, 20.69) * mm, "end": v(-2.06, 18.56) * mm});
            skLineSegment(sketch, "E1995", {"start": v(-2.06, 18.56) * mm, "end": v(-2.06, 16.44) * mm});
            skLineSegment(sketch, "E1996", {"start": v(-2.06, 16.44) * mm, "end": v(-1.47, 16.44) * mm});
            skLineSegment(sketch, "E1997", {"start": v(-1.47, 16.44) * mm, "end": v(-0.88, 16.44) * mm});
            skLineSegment(sketch, "E1998", {"start": v(-0.88, 16.44) * mm, "end": v(-0.43, 16.44) * mm});
            skLineSegment(sketch, "E1999", {"start": v(-0.43, 16.44) * mm, "end": v(-0.43, 14.75) * mm});
            skLineSegment(sketch, "E2000", {"start": v(-0.43, 14.75) * mm, "end": v(-0.43, 12.63) * mm});
            skLineSegment(sketch, "E2001", {"start": v(-0.43, 12.63) * mm, "end": v(-0.43, 10.5) * mm});
            skLineSegment(sketch, "E2002", {"start": v(-0.43, 10.5) * mm, "end": v(-0.43, 8.87) * mm});
            skLineSegment(sketch, "E2003", {"start": v(-0.43, 8.87) * mm, "end": v(-0.54, 9.1) * mm});
            skLineSegment(sketch, "E2004", {"start": v(-0.54, 9.1) * mm, "end": v(-0.8, 9.59) * mm});
            skLineSegment(sketch, "E2005", {"start": v(-0.8, 9.59) * mm, "end": v(-1.1, 10.07) * mm});
            skLineSegment(sketch, "E2006", {"start": v(-1.1, 10.07) * mm, "end": v(-1.39, 10.54) * mm});
            skLineSegment(sketch, "E2007", {"start": v(-1.39, 10.54) * mm, "end": v(-1.7, 10.99) * mm});
            skLineSegment(sketch, "E2008", {"start": v(-1.7, 10.99) * mm, "end": v(-2.02, 11.42) * mm});
            skLineSegment(sketch, "E2009", {"start": v(-2.02, 11.42) * mm, "end": v(-2.36, 11.85) * mm});
            skLineSegment(sketch, "E2010", {"start": v(-2.36, 11.85) * mm, "end": v(-2.7, 12.25) * mm});
            skLineSegment(sketch, "E2011", {"start": v(-2.7, 12.25) * mm, "end": v(-3.07, 12.65) * mm});
            skLineSegment(sketch, "E2012", {"start": v(-3.07, 12.65) * mm, "end": v(-3.45, 13.03) * mm});
            skLineSegment(sketch, "E2013", {"start": v(-3.45, 13.03) * mm, "end": v(-3.84, 13.4) * mm});
            skLineSegment(sketch, "E2014", {"start": v(-3.84, 13.4) * mm, "end": v(-4.25, 13.74) * mm});
            skLineSegment(sketch, "E2015", {"start": v(-4.25, 13.74) * mm, "end": v(-4.67, 14.08) * mm});
            skLineSegment(sketch, "E2016", {"start": v(-4.67, 14.08) * mm, "end": v(-5.1, 14.4) * mm});
            skLineSegment(sketch, "E2017", {"start": v(-5.1, 14.4) * mm, "end": v(-5.55, 14.7) * mm});
            skLineSegment(sketch, "E2018", {"start": v(-5.55, 14.7) * mm, "end": v(-6, 15) * mm});
            skLineSegment(sketch, "E2019", {"start": v(-6, 15) * mm, "end": v(-6.48, 15.28) * mm});
            skLineSegment(sketch, "E2020", {"start": v(-6.48, 15.28) * mm, "end": v(-6.97, 15.54) * mm});
            skLineSegment(sketch, "E2021", {"start": v(-6.97, 15.54) * mm, "end": v(-7.46, 15.78) * mm});
            skLineSegment(sketch, "E2022", {"start": v(-7.46, 15.78) * mm, "end": v(-7.96, 16.01) * mm});
            skLineSegment(sketch, "E2023", {"start": v(-7.96, 16.01) * mm, "end": v(-8.47, 16.23) * mm});
            skLineSegment(sketch, "E2024", {"start": v(-8.47, 16.23) * mm, "end": v(-9, 16.42) * mm});
            skLineSegment(sketch, "E2025", {"start": v(-9, 16.42) * mm, "end": v(-9.52, 16.6) * mm});
            skLineSegment(sketch, "E2026", {"start": v(-9.52, 16.6) * mm, "end": v(-10.05, 16.76) * mm});
            skLineSegment(sketch, "E2027", {"start": v(-10.05, 16.76) * mm, "end": v(-10.6, 16.9) * mm});
            skLineSegment(sketch, "E2028", {"start": v(-10.6, 16.9) * mm, "end": v(-11.14, 17.03) * mm});
            skLineSegment(sketch, "E2029", {"start": v(-11.14, 17.03) * mm, "end": v(-11.7, 17.14) * mm});
            skLineSegment(sketch, "E2030", {"start": v(-11.7, 17.14) * mm, "end": v(-12.16, 17.22) * mm});
            skLineSegment(sketch, "E2031", {"start": v(-12.16, 17.22) * mm, "end": v(-11.9, 17.33) * mm});
            skLineSegment(sketch, "E2032", {"start": v(-9.54, -3.07) * mm, "end": v(-9.6, -3.35) * mm});
            skLineSegment(sketch, "E2033", {"start": v(-9.6, -3.35) * mm, "end": v(-9.66, -3.63) * mm});
            skLineSegment(sketch, "E2034", {"start": v(-9.66, -3.63) * mm, "end": v(-9.73, -3.9) * mm});
            skLineSegment(sketch, "E2035", {"start": v(-9.73, -3.9) * mm, "end": v(-9.8, -4.16) * mm});
            skLineSegment(sketch, "E2036", {"start": v(-9.8, -4.16) * mm, "end": v(-9.89, -4.42) * mm});
            skLineSegment(sketch, "E2037", {"start": v(-9.89, -4.42) * mm, "end": v(-9.98, -4.67) * mm});
            skLineSegment(sketch, "E2038", {"start": v(-9.98, -4.67) * mm, "end": v(-10.07, -4.91) * mm});
            skLineSegment(sketch, "E2039", {"start": v(-10.07, -4.91) * mm, "end": v(-10.17, -5.15) * mm});
            skLineSegment(sketch, "E2040", {"start": v(-10.17, -5.15) * mm, "end": v(-10.28, -5.39) * mm});
            skLineSegment(sketch, "E2041", {"start": v(-10.28, -5.39) * mm, "end": v(-10.39, -5.61) * mm});
            skLineSegment(sketch, "E2042", {"start": v(-10.39, -5.61) * mm, "end": v(-10.5, -5.83) * mm});
            skLineSegment(sketch, "E2043", {"start": v(-10.5, -5.83) * mm, "end": v(-10.62, -6.04) * mm});
            skLineSegment(sketch, "E2044", {"start": v(-10.62, -6.04) * mm, "end": v(-10.75, -6.24) * mm});
            skLineSegment(sketch, "E2045", {"start": v(-10.75, -6.24) * mm, "end": v(-10.88, -6.44) * mm});
            skLineSegment(sketch, "E2046", {"start": v(-10.88, -6.44) * mm, "end": v(-11.01, -6.63) * mm});
            skLineSegment(sketch, "E2047", {"start": v(-11.01, -6.63) * mm, "end": v(-11.15, -6.81) * mm});
            skLineSegment(sketch, "E2048", {"start": v(-11.15, -6.81) * mm, "end": v(-11.3, -7) * mm});
            skLineSegment(sketch, "E2049", {"start": v(-11.3, -7) * mm, "end": v(-11.45, -7.16) * mm});
            skLineSegment(sketch, "E2050", {"start": v(-11.45, -7.16) * mm, "end": v(-11.6, -7.32) * mm});
            skLineSegment(sketch, "E2051", {"start": v(-11.6, -7.32) * mm, "end": v(-11.76, -7.48) * mm});
            skLineSegment(sketch, "E2052", {"start": v(-11.76, -7.48) * mm, "end": v(-11.93, -7.62) * mm});
            skLineSegment(sketch, "E2053", {"start": v(-11.93, -7.62) * mm, "end": v(-12.1, -7.77) * mm});
            skLineSegment(sketch, "E2054", {"start": v(-12.1, -7.77) * mm, "end": v(-12.27, -7.9) * mm});
            skLineSegment(sketch, "E2055", {"start": v(-12.27, -7.9) * mm, "end": v(-12.45, -8.03) * mm});
            skLineSegment(sketch, "E2056", {"start": v(-12.45, -8.03) * mm, "end": v(-12.64, -8.14) * mm});
            skLineSegment(sketch, "E2057", {"start": v(-12.64, -8.14) * mm, "end": v(-12.82, -8.25) * mm});
            skLineSegment(sketch, "E2058", {"start": v(-12.82, -8.25) * mm, "end": v(-13, -8.35) * mm});
            skLineSegment(sketch, "E2059", {"start": v(-13, -8.35) * mm, "end": v(-13.2, -8.45) * mm});
            skLineSegment(sketch, "E2060", {"start": v(-13.2, -8.45) * mm, "end": v(-13.4, -8.53) * mm});
            skLineSegment(sketch, "E2061", {"start": v(-13.4, -8.53) * mm, "end": v(-13.59, -8.61) * mm});
            skLineSegment(sketch, "E2062", {"start": v(-13.59, -8.61) * mm, "end": v(-13.78, -8.68) * mm});
            skLineSegment(sketch, "E2063", {"start": v(-13.78, -8.68) * mm, "end": v(-13.99, -8.74) * mm});
            skLineSegment(sketch, "E2064", {"start": v(-13.99, -8.74) * mm, "end": v(-14.2, -8.8) * mm});
            skLineSegment(sketch, "E2065", {"start": v(-14.2, -8.8) * mm, "end": v(-14.4, -8.84) * mm});
            skLineSegment(sketch, "E2066", {"start": v(-14.4, -8.84) * mm, "end": v(-14.6, -8.88) * mm});
            skLineSegment(sketch, "E2067", {"start": v(-14.6, -8.88) * mm, "end": v(-14.82, -8.9) * mm});
            skLineSegment(sketch, "E2068", {"start": v(-14.82, -8.9) * mm, "end": v(-15.03, -8.92) * mm});
            skLineSegment(sketch, "E2069", {"start": v(-15.03, -8.92) * mm, "end": v(-15.25, -8.94) * mm});
            skLineSegment(sketch, "E2070", {"start": v(-15.25, -8.94) * mm, "end": v(-15.47, -8.94) * mm});
            skLineSegment(sketch, "E2071", {"start": v(-15.47, -8.94) * mm, "end": v(-15.83, -8.93) * mm});
            skLineSegment(sketch, "E2072", {"start": v(-15.83, -8.93) * mm, "end": v(-16.18, -8.9) * mm});
            skLineSegment(sketch, "E2073", {"start": v(-16.18, -8.9) * mm, "end": v(-16.52, -8.86) * mm});
            skLineSegment(sketch, "E2074", {"start": v(-16.52, -8.86) * mm, "end": v(-16.85, -8.8) * mm});
            skLineSegment(sketch, "E2075", {"start": v(-16.85, -8.8) * mm, "end": v(-17.17, -8.71) * mm});
            skLineSegment(sketch, "E2076", {"start": v(-17.17, -8.71) * mm, "end": v(-17.49, -8.61) * mm});
            skLineSegment(sketch, "E2077", {"start": v(-17.49, -8.61) * mm, "end": v(-17.79, -8.5) * mm});
            skLineSegment(sketch, "E2078", {"start": v(-17.79, -8.5) * mm, "end": v(-18.08, -8.36) * mm});
            skLineSegment(sketch, "E2079", {"start": v(-18.08, -8.36) * mm, "end": v(-18.36, -8.2) * mm});
            skLineSegment(sketch, "E2080", {"start": v(-18.36, -8.2) * mm, "end": v(-18.64, -8.03) * mm});
            skLineSegment(sketch, "E2081", {"start": v(-18.64, -8.03) * mm, "end": v(-18.9, -7.84) * mm});
            skLineSegment(sketch, "E2082", {"start": v(-18.9, -7.84) * mm, "end": v(-19.16, -7.64) * mm});
            skLineSegment(sketch, "E2083", {"start": v(-19.16, -7.64) * mm, "end": v(-19.4, -7.4) * mm});
            skLineSegment(sketch, "E2084", {"start": v(-19.4, -7.4) * mm, "end": v(-19.64, -7.16) * mm});
            skLineSegment(sketch, "E2085", {"start": v(-19.64, -7.16) * mm, "end": v(-19.86, -6.9) * mm});
            skLineSegment(sketch, "E2086", {"start": v(-19.86, -6.9) * mm, "end": v(-20.08, -6.62) * mm});
            skLineSegment(sketch, "E2087", {"start": v(-20.08, -6.62) * mm, "end": v(-20.28, -6.32) * mm});
            skLineSegment(sketch, "E2088", {"start": v(-20.28, -6.32) * mm, "end": v(-20.48, -6.01) * mm});
            skLineSegment(sketch, "E2089", {"start": v(-20.48, -6.01) * mm, "end": v(-20.65, -5.69) * mm});
            skLineSegment(sketch, "E2090", {"start": v(-20.65, -5.69) * mm, "end": v(-20.82, -5.35) * mm});
            skLineSegment(sketch, "E2091", {"start": v(-20.82, -5.35) * mm, "end": v(-20.97, -5) * mm});
            skLineSegment(sketch, "E2092", {"start": v(-20.97, -5) * mm, "end": v(-21.11, -4.62) * mm});
            skLineSegment(sketch, "E2093", {"start": v(-21.11, -4.62) * mm, "end": v(-21.24, -4.24) * mm});
            skLineSegment(sketch, "E2094", {"start": v(-21.24, -4.24) * mm, "end": v(-21.35, -3.84) * mm});
            skLineSegment(sketch, "E2095", {"start": v(-21.35, -3.84) * mm, "end": v(-21.45, -3.43) * mm});
            skLineSegment(sketch, "E2096", {"start": v(-21.45, -3.43) * mm, "end": v(-21.53, -3) * mm});
            skLineSegment(sketch, "E2097", {"start": v(-21.53, -3) * mm, "end": v(-21.6, -2.57) * mm});
            skLineSegment(sketch, "E2098", {"start": v(-21.6, -2.57) * mm, "end": v(-21.67, -2.11) * mm});
            skLineSegment(sketch, "E2099", {"start": v(-21.67, -2.11) * mm, "end": v(-21.71, -1.64) * mm});
            skLineSegment(sketch, "E2100", {"start": v(-21.71, -1.64) * mm, "end": v(-21.75, -1.16) * mm});
            skLineSegment(sketch, "E2101", {"start": v(-21.75, -1.16) * mm, "end": v(-21.77, -0.66) * mm});
            skLineSegment(sketch, "E2102", {"start": v(-21.77, -0.66) * mm, "end": v(-21.77, -0.15) * mm});
            skLineSegment(sketch, "E2103", {"start": v(-21.77, -0.15) * mm, "end": v(-21.77, 0.37) * mm});
            skLineSegment(sketch, "E2104", {"start": v(-21.77, 0.37) * mm, "end": v(-21.75, 0.88) * mm});
            skLineSegment(sketch, "E2105", {"start": v(-21.75, 0.88) * mm, "end": v(-21.71, 1.37) * mm});
            skLineSegment(sketch, "E2106", {"start": v(-21.71, 1.37) * mm, "end": v(-21.67, 1.85) * mm});
            skLineSegment(sketch, "E2107", {"start": v(-21.67, 1.85) * mm, "end": v(-21.6, 2.3) * mm});
            skLineSegment(sketch, "E2108", {"start": v(-21.6, 2.3) * mm, "end": v(-21.53, 2.76) * mm});
            skLineSegment(sketch, "E2109", {"start": v(-21.53, 2.76) * mm, "end": v(-21.45, 3.19) * mm});
            skLineSegment(sketch, "E2110", {"start": v(-21.45, 3.19) * mm, "end": v(-21.35, 3.6) * mm});
            skLineSegment(sketch, "E2111", {"start": v(-21.35, 3.6) * mm, "end": v(-21.23, 4) * mm});
            skLineSegment(sketch, "E2112", {"start": v(-21.23, 4) * mm, "end": v(-21.1, 4.4) * mm});
            skLineSegment(sketch, "E2113", {"start": v(-21.1, 4.4) * mm, "end": v(-20.97, 4.77) * mm});
            skLineSegment(sketch, "E2114", {"start": v(-20.97, 4.77) * mm, "end": v(-20.81, 5.13) * mm});
            skLineSegment(sketch, "E2115", {"start": v(-20.81, 5.13) * mm, "end": v(-20.65, 5.47) * mm});
            skLineSegment(sketch, "E2116", {"start": v(-20.65, 5.47) * mm, "end": v(-20.47, 5.8) * mm});
            skLineSegment(sketch, "E2117", {"start": v(-20.47, 5.8) * mm, "end": v(-20.27, 6.1) * mm});
            skLineSegment(sketch, "E2118", {"start": v(-20.27, 6.1) * mm, "end": v(-20.07, 6.4) * mm});
            skLineSegment(sketch, "E2119", {"start": v(-20.07, 6.4) * mm, "end": v(-19.85, 6.69) * mm});
            skLineSegment(sketch, "E2120", {"start": v(-19.85, 6.69) * mm, "end": v(-19.62, 6.95) * mm});
            skLineSegment(sketch, "E2121", {"start": v(-19.62, 6.95) * mm, "end": v(-19.38, 7.2) * mm});
            skLineSegment(sketch, "E2122", {"start": v(-19.38, 7.2) * mm, "end": v(-19.13, 7.42) * mm});
            skLineSegment(sketch, "E2123", {"start": v(-19.13, 7.42) * mm, "end": v(-18.87, 7.63) * mm});
            skLineSegment(sketch, "E2124", {"start": v(-18.87, 7.63) * mm, "end": v(-18.6, 7.82) * mm});
            skLineSegment(sketch, "E2125", {"start": v(-18.6, 7.82) * mm, "end": v(-18.32, 8) * mm});
            skLineSegment(sketch, "E2126", {"start": v(-18.32, 8) * mm, "end": v(-18.02, 8.15) * mm});
            skLineSegment(sketch, "E2127", {"start": v(-18.02, 8.15) * mm, "end": v(-17.72, 8.28) * mm});
            skLineSegment(sketch, "E2128", {"start": v(-17.72, 8.28) * mm, "end": v(-17.4, 8.4) * mm});
            skLineSegment(sketch, "E2129", {"start": v(-17.4, 8.4) * mm, "end": v(-17.08, 8.5) * mm});
            skLineSegment(sketch, "E2130", {"start": v(-17.08, 8.5) * mm, "end": v(-16.75, 8.58) * mm});
            skLineSegment(sketch, "E2131", {"start": v(-16.75, 8.58) * mm, "end": v(-16.4, 8.65) * mm});
            skLineSegment(sketch, "E2132", {"start": v(-16.4, 8.65) * mm, "end": v(-16.05, 8.7) * mm});
            skLineSegment(sketch, "E2133", {"start": v(-16.05, 8.7) * mm, "end": v(-15.68, 8.72) * mm});
            skLineSegment(sketch, "E2134", {"start": v(-15.68, 8.72) * mm, "end": v(-15.3, 8.73) * mm});
            skLineSegment(sketch, "E2135", {"start": v(-15.3, 8.73) * mm, "end": v(-14.96, 8.72) * mm});
            skLineSegment(sketch, "E2136", {"start": v(-14.96, 8.72) * mm, "end": v(-14.63, 8.7) * mm});
            skLineSegment(sketch, "E2137", {"start": v(-14.63, 8.7) * mm, "end": v(-14.3, 8.64) * mm});
            skLineSegment(sketch, "E2138", {"start": v(-14.3, 8.64) * mm, "end": v(-13.98, 8.58) * mm});
            skLineSegment(sketch, "E2139", {"start": v(-13.98, 8.58) * mm, "end": v(-13.68, 8.5) * mm});
            skLineSegment(sketch, "E2140", {"start": v(-13.68, 8.5) * mm, "end": v(-13.38, 8.39) * mm});
            skLineSegment(sketch, "E2141", {"start": v(-13.38, 8.39) * mm, "end": v(-13.09, 8.27) * mm});
            skLineSegment(sketch, "E2142", {"start": v(-13.09, 8.27) * mm, "end": v(-12.8, 8.12) * mm});
            skLineSegment(sketch, "E2143", {"start": v(-12.8, 8.12) * mm, "end": v(-12.54, 7.96) * mm});
            skLineSegment(sketch, "E2144", {"start": v(-12.54, 7.96) * mm, "end": v(-12.28, 7.78) * mm});
            skLineSegment(sketch, "E2145", {"start": v(-12.28, 7.78) * mm, "end": v(-12.02, 7.59) * mm});
            skLineSegment(sketch, "E2146", {"start": v(-12.02, 7.59) * mm, "end": v(-11.78, 7.37) * mm});
            skLineSegment(sketch, "E2147", {"start": v(-11.78, 7.37) * mm, "end": v(-11.55, 7.13) * mm});
            skLineSegment(sketch, "E2148", {"start": v(-11.55, 7.13) * mm, "end": v(-11.32, 6.88) * mm});
            skLineSegment(sketch, "E2149", {"start": v(-11.32, 6.88) * mm, "end": v(-11.1, 6.6) * mm});
            skLineSegment(sketch, "E2150", {"start": v(-11.1, 6.6) * mm, "end": v(-10.9, 6.31) * mm});
            skLineSegment(sketch, "E2151", {"start": v(-10.9, 6.31) * mm, "end": v(-10.7, 6) * mm});
            skLineSegment(sketch, "E2152", {"start": v(-10.7, 6) * mm, "end": v(-10.52, 5.68) * mm});
            skLineSegment(sketch, "E2153", {"start": v(-10.52, 5.68) * mm, "end": v(-10.35, 5.34) * mm});
            skLineSegment(sketch, "E2154", {"start": v(-10.35, 5.34) * mm, "end": v(-10.2, 5) * mm});
            skLineSegment(sketch, "E2155", {"start": v(-10.2, 5) * mm, "end": v(-10.05, 4.63) * mm});
            skLineSegment(sketch, "E2156", {"start": v(-10.05, 4.63) * mm, "end": v(-9.92, 4.25) * mm});
            skLineSegment(sketch, "E2157", {"start": v(-9.92, 4.25) * mm, "end": v(-9.8, 3.86) * mm});
            skLineSegment(sketch, "E2158", {"start": v(-9.8, 3.86) * mm, "end": v(-9.7, 3.45) * mm});
            skLineSegment(sketch, "E2159", {"start": v(-9.7, 3.45) * mm, "end": v(-9.6, 3.03) * mm});
            skLineSegment(sketch, "E2160", {"start": v(-9.6, 3.03) * mm, "end": v(-9.52, 2.6) * mm});
            skLineSegment(sketch, "E2161", {"start": v(-9.52, 2.6) * mm, "end": v(-9.45, 2.15) * mm});
            skLineSegment(sketch, "E2162", {"start": v(-9.45, 2.15) * mm, "end": v(-9.4, 1.69) * mm});
            skLineSegment(sketch, "E2163", {"start": v(-9.4, 1.69) * mm, "end": v(-9.35, 1.21) * mm});
            skLineSegment(sketch, "E2164", {"start": v(-9.35, 1.21) * mm, "end": v(-9.32, 0.72) * mm});
            skLineSegment(sketch, "E2165", {"start": v(-9.32, 0.72) * mm, "end": v(-9.3, 0.22) * mm});
            skLineSegment(sketch, "E2166", {"start": v(-9.3, 0.22) * mm, "end": v(-9.3, -0.3) * mm});
            skLineSegment(sketch, "E2167", {"start": v(-9.3, -0.3) * mm, "end": v(-9.3, -0.63) * mm});
            skLineSegment(sketch, "E2168", {"start": v(-9.3, -0.63) * mm, "end": v(-9.3, -0.95) * mm});
            skLineSegment(sketch, "E2169", {"start": v(-9.3, -0.95) * mm, "end": v(-9.32, -1.27) * mm});
            skLineSegment(sketch, "E2170", {"start": v(-9.32, -1.27) * mm, "end": v(-9.34, -1.59) * mm});
            skLineSegment(sketch, "E2171", {"start": v(-9.34, -1.59) * mm, "end": v(-9.37, -1.9) * mm});
            skLineSegment(sketch, "E2172", {"start": v(-9.37, -1.9) * mm, "end": v(-9.4, -2.2) * mm});
            skLineSegment(sketch, "E2173", {"start": v(-9.4, -2.2) * mm, "end": v(-9.44, -2.5) * mm});
            skLineSegment(sketch, "E2174", {"start": v(-9.44, -2.5) * mm, "end": v(-9.49, -2.79) * mm});
            skLineSegment(sketch, "E2175", {"start": v(-9.49, -2.79) * mm, "end": v(-9.54, -3.07) * mm});
            skLineSegment(sketch, "E2176", {"start": v(-25.34, 33.9) * mm, "end": v(-25.32, 34.4) * mm});
            skLineSegment(sketch, "E2177", {"start": v(-25.32, 34.4) * mm, "end": v(-25.29, 34.9) * mm});
            skLineSegment(sketch, "E2178", {"start": v(-25.29, 34.9) * mm, "end": v(-25.24, 35.38) * mm});
            skLineSegment(sketch, "E2179", {"start": v(-25.24, 35.38) * mm, "end": v(-25.18, 35.84) * mm});
            skLineSegment(sketch, "E2180", {"start": v(-25.18, 35.84) * mm, "end": v(-25.1, 36.29) * mm});
            skLineSegment(sketch, "E2181", {"start": v(-25.1, 36.29) * mm, "end": v(-25.02, 36.72) * mm});
            skLineSegment(sketch, "E2182", {"start": v(-25.02, 36.72) * mm, "end": v(-24.92, 37.14) * mm});
            skLineSegment(sketch, "E2183", {"start": v(-24.92, 37.14) * mm, "end": v(-24.8, 37.54) * mm});
            skLineSegment(sketch, "E2184", {"start": v(-24.8, 37.54) * mm, "end": v(-24.68, 37.93) * mm});
            skLineSegment(sketch, "E2185", {"start": v(-24.68, 37.93) * mm, "end": v(-24.54, 38.3) * mm});
            skLineSegment(sketch, "E2186", {"start": v(-24.54, 38.3) * mm, "end": v(-24.39, 38.66) * mm});
            skLineSegment(sketch, "E2187", {"start": v(-24.39, 38.66) * mm, "end": v(-24.22, 39) * mm});
            skLineSegment(sketch, "E2188", {"start": v(-24.22, 39) * mm, "end": v(-24.04, 39.33) * mm});
            skLineSegment(sketch, "E2189", {"start": v(-24.04, 39.33) * mm, "end": v(-23.85, 39.64) * mm});
            skLineSegment(sketch, "E2190", {"start": v(-23.85, 39.64) * mm, "end": v(-23.64, 39.94) * mm});
            skLineSegment(sketch, "E2191", {"start": v(-23.64, 39.94) * mm, "end": v(-23.42, 40.22) * mm});
            skLineSegment(sketch, "E2192", {"start": v(-23.42, 40.22) * mm, "end": v(-23.2, 40.48) * mm});
            skLineSegment(sketch, "E2193", {"start": v(-23.2, 40.48) * mm, "end": v(-22.95, 40.72) * mm});
            skLineSegment(sketch, "E2194", {"start": v(-22.95, 40.72) * mm, "end": v(-22.7, 40.95) * mm});
            skLineSegment(sketch, "E2195", {"start": v(-22.7, 40.95) * mm, "end": v(-22.44, 41.16) * mm});
            skLineSegment(sketch, "E2196", {"start": v(-22.44, 41.16) * mm, "end": v(-22.17, 41.35) * mm});
            skLineSegment(sketch, "E2197", {"start": v(-22.17, 41.35) * mm, "end": v(-21.9, 41.52) * mm});
            skLineSegment(sketch, "E2198", {"start": v(-21.9, 41.52) * mm, "end": v(-21.6, 41.68) * mm});
            skLineSegment(sketch, "E2199", {"start": v(-21.6, 41.68) * mm, "end": v(-21.3, 41.81) * mm});
            skLineSegment(sketch, "E2200", {"start": v(-21.3, 41.81) * mm, "end": v(-20.98, 41.93) * mm});
            skLineSegment(sketch, "E2201", {"start": v(-20.98, 41.93) * mm, "end": v(-20.66, 42.03) * mm});
            skLineSegment(sketch, "E2202", {"start": v(-20.66, 42.03) * mm, "end": v(-20.32, 42.11) * mm});
            skLineSegment(sketch, "E2203", {"start": v(-20.32, 42.11) * mm, "end": v(-19.98, 42.18) * mm});
            skLineSegment(sketch, "E2204", {"start": v(-19.98, 42.18) * mm, "end": v(-19.62, 42.22) * mm});
            skLineSegment(sketch, "E2205", {"start": v(-19.62, 42.22) * mm, "end": v(-19.26, 42.25) * mm});
            skLineSegment(sketch, "E2206", {"start": v(-19.26, 42.25) * mm, "end": v(-18.88, 42.26) * mm});
            skLineSegment(sketch, "E2207", {"start": v(-18.88, 42.26) * mm, "end": v(-18.54, 42.25) * mm});
            skLineSegment(sketch, "E2208", {"start": v(-18.54, 42.25) * mm, "end": v(-18.2, 42.22) * mm});
            skLineSegment(sketch, "E2209", {"start": v(-18.2, 42.22) * mm, "end": v(-17.87, 42.17) * mm});
            skLineSegment(sketch, "E2210", {"start": v(-17.87, 42.17) * mm, "end": v(-17.56, 42.1) * mm});
            skLineSegment(sketch, "E2211", {"start": v(-17.56, 42.1) * mm, "end": v(-17.25, 42.02) * mm});
            skLineSegment(sketch, "E2212", {"start": v(-17.25, 42.02) * mm, "end": v(-16.95, 41.92) * mm});
            skLineSegment(sketch, "E2213", {"start": v(-16.95, 41.92) * mm, "end": v(-16.66, 41.8) * mm});
            skLineSegment(sketch, "E2214", {"start": v(-16.66, 41.8) * mm, "end": v(-16.38, 41.65) * mm});
            skLineSegment(sketch, "E2215", {"start": v(-16.38, 41.65) * mm, "end": v(-16.11, 41.5) * mm});
            skLineSegment(sketch, "E2216", {"start": v(-16.11, 41.5) * mm, "end": v(-15.85, 41.31) * mm});
            skLineSegment(sketch, "E2217", {"start": v(-15.85, 41.31) * mm, "end": v(-15.6, 41.12) * mm});
            skLineSegment(sketch, "E2218", {"start": v(-15.6, 41.12) * mm, "end": v(-15.36, 40.9) * mm});
            skLineSegment(sketch, "E2219", {"start": v(-15.36, 40.9) * mm, "end": v(-15.12, 40.66) * mm});
            skLineSegment(sketch, "E2220", {"start": v(-15.12, 40.66) * mm, "end": v(-14.9, 40.4) * mm});
            skLineSegment(sketch, "E2221", {"start": v(-14.9, 40.4) * mm, "end": v(-14.68, 40.13) * mm});
            skLineSegment(sketch, "E2222", {"start": v(-14.68, 40.13) * mm, "end": v(-14.48, 39.84) * mm});
            skLineSegment(sketch, "E2223", {"start": v(-14.48, 39.84) * mm, "end": v(-14.28, 39.53) * mm});
            skLineSegment(sketch, "E2224", {"start": v(-14.28, 39.53) * mm, "end": v(-14.1, 39.2) * mm});
            skLineSegment(sketch, "E2225", {"start": v(-14.1, 39.2) * mm, "end": v(-13.93, 38.87) * mm});
            skLineSegment(sketch, "E2226", {"start": v(-13.93, 38.87) * mm, "end": v(-13.77, 38.52) * mm});
            skLineSegment(sketch, "E2227", {"start": v(-13.77, 38.52) * mm, "end": v(-13.63, 38.16) * mm});
            skLineSegment(sketch, "E2228", {"start": v(-13.63, 38.16) * mm, "end": v(-13.5, 37.78) * mm});
            skLineSegment(sketch, "E2229", {"start": v(-13.5, 37.78) * mm, "end": v(-13.37, 37.39) * mm});
            skLineSegment(sketch, "E2230", {"start": v(-13.37, 37.39) * mm, "end": v(-13.27, 36.98) * mm});
            skLineSegment(sketch, "E2231", {"start": v(-13.27, 36.98) * mm, "end": v(-13.17, 36.56) * mm});
            skLineSegment(sketch, "E2232", {"start": v(-13.17, 36.56) * mm, "end": v(-13.1, 36.13) * mm});
            skLineSegment(sketch, "E2233", {"start": v(-13.1, 36.13) * mm, "end": v(-13.02, 35.68) * mm});
            skLineSegment(sketch, "E2234", {"start": v(-13.02, 35.68) * mm, "end": v(-12.97, 35.22) * mm});
            skLineSegment(sketch, "E2235", {"start": v(-12.97, 35.22) * mm, "end": v(-12.92, 34.74) * mm});
            skLineSegment(sketch, "E2236", {"start": v(-12.92, 34.74) * mm, "end": v(-12.9, 34.25) * mm});
            skLineSegment(sketch, "E2237", {"start": v(-12.9, 34.25) * mm, "end": v(-12.87, 33.75) * mm});
            skLineSegment(sketch, "E2238", {"start": v(-12.87, 33.75) * mm, "end": v(-12.87, 33.23) * mm});
            skLineSegment(sketch, "E2239", {"start": v(-12.87, 33.23) * mm, "end": v(-12.87, 32.9) * mm});
            skLineSegment(sketch, "E2240", {"start": v(-12.87, 32.9) * mm, "end": v(-12.88, 32.58) * mm});
            skLineSegment(sketch, "E2241", {"start": v(-12.88, 32.58) * mm, "end": v(-12.9, 32.26) * mm});
            skLineSegment(sketch, "E2242", {"start": v(-12.9, 32.26) * mm, "end": v(-12.91, 31.94) * mm});
            skLineSegment(sketch, "E2243", {"start": v(-12.91, 31.94) * mm, "end": v(-12.94, 31.63) * mm});
            skLineSegment(sketch, "E2244", {"start": v(-12.94, 31.63) * mm, "end": v(-12.97, 31.33) * mm});
            skLineSegment(sketch, "E2245", {"start": v(-12.97, 31.33) * mm, "end": v(-13.01, 31.03) * mm});
            skLineSegment(sketch, "E2246", {"start": v(-13.01, 31.03) * mm, "end": v(-13.06, 30.74) * mm});
            skLineSegment(sketch, "E2247", {"start": v(-13.06, 30.74) * mm, "end": v(-13.11, 30.45) * mm});
            skLineSegment(sketch, "E2248", {"start": v(-13.11, 30.45) * mm, "end": v(-13.17, 30.17) * mm});
            skLineSegment(sketch, "E2249", {"start": v(-13.17, 30.17) * mm, "end": v(-13.23, 29.9) * mm});
            skLineSegment(sketch, "E2250", {"start": v(-13.23, 29.9) * mm, "end": v(-13.3, 29.63) * mm});
            skLineSegment(sketch, "E2251", {"start": v(-13.3, 29.63) * mm, "end": v(-13.38, 29.37) * mm});
            skLineSegment(sketch, "E2252", {"start": v(-13.38, 29.37) * mm, "end": v(-13.46, 29.11) * mm});
            skLineSegment(sketch, "E2253", {"start": v(-13.46, 29.11) * mm, "end": v(-13.55, 28.86) * mm});
            skLineSegment(sketch, "E2254", {"start": v(-13.55, 28.86) * mm, "end": v(-13.65, 28.61) * mm});
            skLineSegment(sketch, "E2255", {"start": v(-13.65, 28.61) * mm, "end": v(-13.75, 28.38) * mm});
            skLineSegment(sketch, "E2256", {"start": v(-13.75, 28.38) * mm, "end": v(-13.85, 28.14) * mm});
            skLineSegment(sketch, "E2257", {"start": v(-13.85, 28.14) * mm, "end": v(-13.96, 27.92) * mm});
            skLineSegment(sketch, "E2258", {"start": v(-13.96, 27.92) * mm, "end": v(-14.08, 27.7) * mm});
            skLineSegment(sketch, "E2259", {"start": v(-14.08, 27.7) * mm, "end": v(-14.2, 27.49) * mm});
            skLineSegment(sketch, "E2260", {"start": v(-14.2, 27.49) * mm, "end": v(-14.32, 27.28) * mm});
            skLineSegment(sketch, "E2261", {"start": v(-14.32, 27.28) * mm, "end": v(-14.45, 27.09) * mm});
            skLineSegment(sketch, "E2262", {"start": v(-14.45, 27.09) * mm, "end": v(-14.59, 26.9) * mm});
            skLineSegment(sketch, "E2263", {"start": v(-14.59, 26.9) * mm, "end": v(-14.73, 26.71) * mm});
            skLineSegment(sketch, "E2264", {"start": v(-14.73, 26.71) * mm, "end": v(-14.87, 26.54) * mm});
            skLineSegment(sketch, "E2265", {"start": v(-14.87, 26.54) * mm, "end": v(-15.02, 26.37) * mm});
            skLineSegment(sketch, "E2266", {"start": v(-15.02, 26.37) * mm, "end": v(-15.18, 26.2) * mm});
            skLineSegment(sketch, "E2267", {"start": v(-15.18, 26.2) * mm, "end": v(-15.34, 26.05) * mm});
            skLineSegment(sketch, "E2268", {"start": v(-15.34, 26.05) * mm, "end": v(-15.5, 25.9) * mm});
            skLineSegment(sketch, "E2269", {"start": v(-15.5, 25.9) * mm, "end": v(-15.67, 25.76) * mm});
            skLineSegment(sketch, "E2270", {"start": v(-15.67, 25.76) * mm, "end": v(-15.85, 25.63) * mm});
            skLineSegment(sketch, "E2271", {"start": v(-15.85, 25.63) * mm, "end": v(-16.03, 25.5) * mm});
            skLineSegment(sketch, "E2272", {"start": v(-16.03, 25.5) * mm, "end": v(-16.21, 25.39) * mm});
            skLineSegment(sketch, "E2273", {"start": v(-16.21, 25.39) * mm, "end": v(-16.4, 25.28) * mm});
            skLineSegment(sketch, "E2274", {"start": v(-16.4, 25.28) * mm, "end": v(-16.58, 25.17) * mm});
            skLineSegment(sketch, "E2275", {"start": v(-16.58, 25.17) * mm, "end": v(-16.77, 25.08) * mm});
            skLineSegment(sketch, "E2276", {"start": v(-16.77, 25.08) * mm, "end": v(-16.97, 25) * mm});
            skLineSegment(sketch, "E2277", {"start": v(-16.97, 25) * mm, "end": v(-17.16, 24.92) * mm});
            skLineSegment(sketch, "E2278", {"start": v(-17.16, 24.92) * mm, "end": v(-17.36, 24.85) * mm});
            skLineSegment(sketch, "E2279", {"start": v(-17.36, 24.85) * mm, "end": v(-17.56, 24.79) * mm});
            skLineSegment(sketch, "E2280", {"start": v(-17.56, 24.79) * mm, "end": v(-17.76, 24.73) * mm});
            skLineSegment(sketch, "E2281", {"start": v(-17.76, 24.73) * mm, "end": v(-17.97, 24.7) * mm});
            skLineSegment(sketch, "E2282", {"start": v(-17.97, 24.7) * mm, "end": v(-18.18, 24.65) * mm});
            skLineSegment(sketch, "E2283", {"start": v(-18.18, 24.65) * mm, "end": v(-18.4, 24.62) * mm});
            skLineSegment(sketch, "E2284", {"start": v(-18.4, 24.62) * mm, "end": v(-18.6, 24.6) * mm});
            skLineSegment(sketch, "E2285", {"start": v(-18.6, 24.6) * mm, "end": v(-18.83, 24.6) * mm});
            skLineSegment(sketch, "E2286", {"start": v(-18.83, 24.6) * mm, "end": v(-19.05, 24.59) * mm});
            skLineSegment(sketch, "E2287", {"start": v(-19.05, 24.59) * mm, "end": v(-19.4, 24.6) * mm});
            skLineSegment(sketch, "E2288", {"start": v(-19.4, 24.6) * mm, "end": v(-19.76, 24.62) * mm});
            skLineSegment(sketch, "E2289", {"start": v(-19.76, 24.62) * mm, "end": v(-20.1, 24.67) * mm});
            skLineSegment(sketch, "E2290", {"start": v(-20.1, 24.67) * mm, "end": v(-20.43, 24.73) * mm});
            skLineSegment(sketch, "E2291", {"start": v(-20.43, 24.73) * mm, "end": v(-20.75, 24.81) * mm});
            skLineSegment(sketch, "E2292", {"start": v(-20.75, 24.81) * mm, "end": v(-21.06, 24.91) * mm});
            skLineSegment(sketch, "E2293", {"start": v(-21.06, 24.91) * mm, "end": v(-21.36, 25.03) * mm});
            skLineSegment(sketch, "E2294", {"start": v(-21.36, 25.03) * mm, "end": v(-21.66, 25.17) * mm});
            skLineSegment(sketch, "E2295", {"start": v(-21.66, 25.17) * mm, "end": v(-21.94, 25.32) * mm});
            skLineSegment(sketch, "E2296", {"start": v(-21.94, 25.32) * mm, "end": v(-22.21, 25.5) * mm});
            skLineSegment(sketch, "E2297", {"start": v(-22.21, 25.5) * mm, "end": v(-22.48, 25.69) * mm});
            skLineSegment(sketch, "E2298", {"start": v(-22.48, 25.69) * mm, "end": v(-22.73, 25.9) * mm});
            skLineSegment(sketch, "E2299", {"start": v(-22.73, 25.9) * mm, "end": v(-22.98, 26.12) * mm});
            skLineSegment(sketch, "E2300", {"start": v(-22.98, 26.12) * mm, "end": v(-23.21, 26.37) * mm});
            skLineSegment(sketch, "E2301", {"start": v(-23.21, 26.37) * mm, "end": v(-23.44, 26.63) * mm});
            skLineSegment(sketch, "E2302", {"start": v(-23.44, 26.63) * mm, "end": v(-23.65, 26.9) * mm});
            skLineSegment(sketch, "E2303", {"start": v(-23.65, 26.9) * mm, "end": v(-23.86, 27.2) * mm});
            skLineSegment(sketch, "E2304", {"start": v(-23.86, 27.2) * mm, "end": v(-24.05, 27.52) * mm});
            skLineSegment(sketch, "E2305", {"start": v(-24.05, 27.52) * mm, "end": v(-24.23, 27.84) * mm});
            skLineSegment(sketch, "E2306", {"start": v(-24.23, 27.84) * mm, "end": v(-24.4, 28.18) * mm});
            skLineSegment(sketch, "E2307", {"start": v(-24.4, 28.18) * mm, "end": v(-24.55, 28.54) * mm});
            skLineSegment(sketch, "E2308", {"start": v(-24.55, 28.54) * mm, "end": v(-24.69, 28.9) * mm});
            skLineSegment(sketch, "E2309", {"start": v(-24.69, 28.9) * mm, "end": v(-24.81, 29.29) * mm});
            skLineSegment(sketch, "E2310", {"start": v(-24.81, 29.29) * mm, "end": v(-24.92, 29.69) * mm});
            skLineSegment(sketch, "E2311", {"start": v(-24.92, 29.69) * mm, "end": v(-25.02, 30.1) * mm});
            skLineSegment(sketch, "E2312", {"start": v(-25.02, 30.1) * mm, "end": v(-25.1, 30.52) * mm});
            skLineSegment(sketch, "E2313", {"start": v(-25.1, 30.52) * mm, "end": v(-25.18, 30.96) * mm});
            skLineSegment(sketch, "E2314", {"start": v(-25.18, 30.96) * mm, "end": v(-25.24, 31.42) * mm});
            skLineSegment(sketch, "E2315", {"start": v(-25.24, 31.42) * mm, "end": v(-25.29, 31.89) * mm});
            skLineSegment(sketch, "E2316", {"start": v(-25.29, 31.89) * mm, "end": v(-25.32, 32.37) * mm});
            skLineSegment(sketch, "E2317", {"start": v(-25.32, 32.37) * mm, "end": v(-25.34, 32.86) * mm});
            skLineSegment(sketch, "E2318", {"start": v(-25.34, 32.86) * mm, "end": v(-25.35, 33.38) * mm});
            skLineSegment(sketch, "E2319", {"start": v(-25.35, 33.38) * mm, "end": v(-25.34, 33.9) * mm});
            skLineSegment(sketch, "E2320", {"start": v(-44.17, 17.86) * mm, "end": v(-43.64, 18.1) * mm});
            skLineSegment(sketch, "E2321", {"start": v(-43.64, 18.1) * mm, "end": v(-43.13, 18.33) * mm});
            skLineSegment(sketch, "E2322", {"start": v(-43.13, 18.33) * mm, "end": v(-42.62, 18.6) * mm});
            skLineSegment(sketch, "E2323", {"start": v(-42.62, 18.6) * mm, "end": v(-42.12, 18.87) * mm});
            skLineSegment(sketch, "E2324", {"start": v(-42.12, 18.87) * mm, "end": v(-41.64, 19.16) * mm});
            skLineSegment(sketch, "E2325", {"start": v(-41.64, 19.16) * mm, "end": v(-41.17, 19.47) * mm});
            skLineSegment(sketch, "E2326", {"start": v(-41.17, 19.47) * mm, "end": v(-40.72, 19.79) * mm});
            skLineSegment(sketch, "E2327", {"start": v(-40.72, 19.79) * mm, "end": v(-40.28, 20.12) * mm});
            skLineSegment(sketch, "E2328", {"start": v(-40.28, 20.12) * mm, "end": v(-39.86, 20.47) * mm});
            skLineSegment(sketch, "E2329", {"start": v(-39.86, 20.47) * mm, "end": v(-39.45, 20.83) * mm});
            skLineSegment(sketch, "E2330", {"start": v(-39.45, 20.83) * mm, "end": v(-39.06, 21.2) * mm});
            skLineSegment(sketch, "E2331", {"start": v(-39.06, 21.2) * mm, "end": v(-38.68, 21.6) * mm});
            skLineSegment(sketch, "E2332", {"start": v(-38.68, 21.6) * mm, "end": v(-38.31, 22) * mm});
            skLineSegment(sketch, "E2333", {"start": v(-38.31, 22) * mm, "end": v(-37.96, 22.42) * mm});
            skLineSegment(sketch, "E2334", {"start": v(-37.96, 22.42) * mm, "end": v(-37.62, 22.85) * mm});
            skLineSegment(sketch, "E2335", {"start": v(-37.62, 22.85) * mm, "end": v(-37.3, 23.3) * mm});
            skLineSegment(sketch, "E2336", {"start": v(-37.3, 23.3) * mm, "end": v(-37, 23.76) * mm});
            skLineSegment(sketch, "E2337", {"start": v(-37, 23.76) * mm, "end": v(-36.7, 24.23) * mm});
            skLineSegment(sketch, "E2338", {"start": v(-36.7, 24.23) * mm, "end": v(-36.42, 24.72) * mm});
            skLineSegment(sketch, "E2339", {"start": v(-36.42, 24.72) * mm, "end": v(-36.16, 25.22) * mm});
            skLineSegment(sketch, "E2340", {"start": v(-36.16, 25.22) * mm, "end": v(-35.92, 25.73) * mm});
            skLineSegment(sketch, "E2341", {"start": v(-35.92, 25.73) * mm, "end": v(-35.69, 26.25) * mm});
            skLineSegment(sketch, "E2342", {"start": v(-35.69, 26.25) * mm, "end": v(-35.48, 26.78) * mm});
            skLineSegment(sketch, "E2343", {"start": v(-35.48, 26.78) * mm, "end": v(-35.35, 27.13) * mm});
            skLineSegment(sketch, "E2344", {"start": v(-35.35, 27.13) * mm, "end": v(-35.19, 26.65) * mm});
            skLineSegment(sketch, "E2345", {"start": v(-35.19, 26.65) * mm, "end": v(-35, 26.13) * mm});
            skLineSegment(sketch, "E2346", {"start": v(-35, 26.13) * mm, "end": v(-34.78, 25.6) * mm});
            skLineSegment(sketch, "E2347", {"start": v(-34.78, 25.6) * mm, "end": v(-34.55, 25.1) * mm});
            skLineSegment(sketch, "E2348", {"start": v(-34.55, 25.1) * mm, "end": v(-34.3, 24.6) * mm});
            skLineSegment(sketch, "E2349", {"start": v(-34.3, 24.6) * mm, "end": v(-34.04, 24.1) * mm});
            skLineSegment(sketch, "E2350", {"start": v(-34.04, 24.1) * mm, "end": v(-33.76, 23.62) * mm});
            skLineSegment(sketch, "E2351", {"start": v(-33.76, 23.62) * mm, "end": v(-33.47, 23.15) * mm});
            skLineSegment(sketch, "E2352", {"start": v(-33.47, 23.15) * mm, "end": v(-33.16, 22.7) * mm});
            skLineSegment(sketch, "E2353", {"start": v(-33.16, 22.7) * mm, "end": v(-32.84, 22.25) * mm});
            skLineSegment(sketch, "E2354", {"start": v(-32.84, 22.25) * mm, "end": v(-32.5, 21.82) * mm});
            skLineSegment(sketch, "E2355", {"start": v(-32.5, 21.82) * mm, "end": v(-32.16, 21.4) * mm});
            skLineSegment(sketch, "E2356", {"start": v(-32.16, 21.4) * mm, "end": v(-31.8, 21) * mm});
            skLineSegment(sketch, "E2357", {"start": v(-31.8, 21) * mm, "end": v(-31.43, 20.62) * mm});
            skLineSegment(sketch, "E2358", {"start": v(-31.43, 20.62) * mm, "end": v(-31.04, 20.25) * mm});
            skLineSegment(sketch, "E2359", {"start": v(-31.04, 20.25) * mm, "end": v(-30.64, 19.89) * mm});
            skLineSegment(sketch, "E2360", {"start": v(-30.64, 19.89) * mm, "end": v(-30.22, 19.54) * mm});
            skLineSegment(sketch, "E2361", {"start": v(-30.22, 19.54) * mm, "end": v(-29.8, 19.2) * mm});
            skLineSegment(sketch, "E2362", {"start": v(-29.8, 19.2) * mm, "end": v(-29.35, 18.89) * mm});
            skLineSegment(sketch, "E2363", {"start": v(-29.35, 18.89) * mm, "end": v(-28.9, 18.58) * mm});
            skLineSegment(sketch, "E2364", {"start": v(-28.9, 18.58) * mm, "end": v(-28.42, 18.3) * mm});
            skLineSegment(sketch, "E2365", {"start": v(-28.42, 18.3) * mm, "end": v(-27.94, 18.02) * mm});
            skLineSegment(sketch, "E2366", {"start": v(-27.94, 18.02) * mm, "end": v(-27.45, 17.75) * mm});
            skLineSegment(sketch, "E2367", {"start": v(-27.45, 17.75) * mm, "end": v(-26.95, 17.5) * mm});
            skLineSegment(sketch, "E2368", {"start": v(-26.95, 17.5) * mm, "end": v(-26.44, 17.28) * mm});
            skLineSegment(sketch, "E2369", {"start": v(-26.44, 17.28) * mm, "end": v(-25.93, 17.07) * mm});
            skLineSegment(sketch, "E2370", {"start": v(-25.93, 17.07) * mm, "end": v(-25.4, 16.87) * mm});
            skLineSegment(sketch, "E2371", {"start": v(-25.4, 16.87) * mm, "end": v(-24.88, 16.7) * mm});
            skLineSegment(sketch, "E2372", {"start": v(-24.88, 16.7) * mm, "end": v(-24.35, 16.53) * mm});
            skLineSegment(sketch, "E2373", {"start": v(-24.35, 16.53) * mm, "end": v(-23.8, 16.4) * mm});
            skLineSegment(sketch, "E2374", {"start": v(-23.8, 16.4) * mm, "end": v(-23.26, 16.26) * mm});
            skLineSegment(sketch, "E2375", {"start": v(-23.26, 16.26) * mm, "end": v(-22.7, 16.15) * mm});
            skLineSegment(sketch, "E2376", {"start": v(-22.7, 16.15) * mm, "end": v(-22.38, 16.1) * mm});
            skLineSegment(sketch, "E2377", {"start": v(-22.38, 16.1) * mm, "end": v(-22.73, 15.95) * mm});
            skLineSegment(sketch, "E2378", {"start": v(-22.73, 15.95) * mm, "end": v(-23.25, 15.71) * mm});
            skLineSegment(sketch, "E2379", {"start": v(-23.25, 15.71) * mm, "end": v(-23.76, 15.46) * mm});
            skLineSegment(sketch, "E2380", {"start": v(-23.76, 15.46) * mm, "end": v(-24.26, 15.18) * mm});
            skLineSegment(sketch, "E2381", {"start": v(-24.26, 15.18) * mm, "end": v(-24.75, 14.9) * mm});
            skLineSegment(sketch, "E2382", {"start": v(-24.75, 14.9) * mm, "end": v(-25.23, 14.59) * mm});
            skLineSegment(sketch, "E2383", {"start": v(-25.23, 14.59) * mm, "end": v(-25.69, 14.27) * mm});
            skLineSegment(sketch, "E2384", {"start": v(-25.69, 14.27) * mm, "end": v(-26.14, 13.93) * mm});
            skLineSegment(sketch, "E2385", {"start": v(-26.14, 13.93) * mm, "end": v(-26.57, 13.58) * mm});
            skLineSegment(sketch, "E2386", {"start": v(-26.57, 13.58) * mm, "end": v(-27, 13.22) * mm});
            skLineSegment(sketch, "E2387", {"start": v(-27, 13.22) * mm, "end": v(-27.4, 12.84) * mm});
            skLineSegment(sketch, "E2388", {"start": v(-27.4, 12.84) * mm, "end": v(-27.8, 12.45) * mm});
            skLineSegment(sketch, "E2389", {"start": v(-27.8, 12.45) * mm, "end": v(-28.17, 12.04) * mm});
            skLineSegment(sketch, "E2390", {"start": v(-28.17, 12.04) * mm, "end": v(-28.54, 11.62) * mm});
            skLineSegment(sketch, "E2391", {"start": v(-28.54, 11.62) * mm, "end": v(-28.9, 11.18) * mm});
            skLineSegment(sketch, "E2392", {"start": v(-28.9, 11.18) * mm, "end": v(-29.23, 10.73) * mm});
            skLineSegment(sketch, "E2393", {"start": v(-29.23, 10.73) * mm, "end": v(-29.41, 10.46) * mm});
            skLineSegment(sketch, "E2394", {"start": v(-29.41, 10.46) * mm, "end": v(-29.4, 10.5) * mm});
            skLineSegment(sketch, "E2395", {"start": v(-29.4, 10.5) * mm, "end": v(-28.87, 12.63) * mm});
            skLineSegment(sketch, "E2396", {"start": v(-28.87, 12.63) * mm, "end": v(-28.33, 14.75) * mm});
            skLineSegment(sketch, "E2397", {"start": v(-28.33, 14.75) * mm, "end": v(-27.8, 16.88) * mm});
            skLineSegment(sketch, "E2398", {"start": v(-27.8, 16.88) * mm, "end": v(-28.43, 16.88) * mm});
            skLineSegment(sketch, "E2399", {"start": v(-28.43, 16.88) * mm, "end": v(-29.06, 16.88) * mm});
            skLineSegment(sketch, "E2400", {"start": v(-29.06, 16.88) * mm, "end": v(-29.69, 16.88) * mm});
            skLineSegment(sketch, "E2401", {"start": v(-29.69, 16.88) * mm, "end": v(-30.32, 16.88) * mm});
            skLineSegment(sketch, "E2402", {"start": v(-30.32, 16.88) * mm, "end": v(-30.95, 16.88) * mm});
            skLineSegment(sketch, "E2403", {"start": v(-30.95, 16.88) * mm, "end": v(-31.58, 16.88) * mm});
            skLineSegment(sketch, "E2404", {"start": v(-31.58, 16.88) * mm, "end": v(-32.2, 16.88) * mm});
            skLineSegment(sketch, "E2405", {"start": v(-32.2, 16.88) * mm, "end": v(-32.84, 16.88) * mm});
            skLineSegment(sketch, "E2406", {"start": v(-32.84, 16.88) * mm, "end": v(-33.47, 16.88) * mm});
            skLineSegment(sketch, "E2407", {"start": v(-33.47, 16.88) * mm, "end": v(-34.1, 16.88) * mm});
            skLineSegment(sketch, "E2408", {"start": v(-34.1, 16.88) * mm, "end": v(-34.73, 16.88) * mm});
            skLineSegment(sketch, "E2409", {"start": v(-34.73, 16.88) * mm, "end": v(-35.36, 16.88) * mm});
            skLineSegment(sketch, "E2410", {"start": v(-35.36, 16.88) * mm, "end": v(-36, 16.88) * mm});
            skLineSegment(sketch, "E2411", {"start": v(-36, 16.88) * mm, "end": v(-36.62, 16.88) * mm});
            skLineSegment(sketch, "E2412", {"start": v(-36.62, 16.88) * mm, "end": v(-37.25, 16.88) * mm});
            skLineSegment(sketch, "E2413", {"start": v(-37.25, 16.88) * mm, "end": v(-37.89, 16.88) * mm});
            skLineSegment(sketch, "E2414", {"start": v(-37.89, 16.88) * mm, "end": v(-38.07, 15.63) * mm});
            skLineSegment(sketch, "E2415", {"start": v(-38.07, 15.63) * mm, "end": v(-38.26, 14.38) * mm});
            skLineSegment(sketch, "E2416", {"start": v(-38.26, 14.38) * mm, "end": v(-38.44, 13.13) * mm});
            skLineSegment(sketch, "E2417", {"start": v(-38.44, 13.13) * mm, "end": v(-38.63, 11.88) * mm});
            skLineSegment(sketch, "E2418", {"start": v(-38.63, 11.88) * mm, "end": v(-38.81, 10.63) * mm});
            skLineSegment(sketch, "E2419", {"start": v(-38.81, 10.63) * mm, "end": v(-39, 9.38) * mm});
            skLineSegment(sketch, "E2420", {"start": v(-39, 9.38) * mm, "end": v(-39.18, 8.13) * mm});
            skLineSegment(sketch, "E2421", {"start": v(-39.18, 8.13) * mm, "end": v(-39.37, 6.88) * mm});
            skLineSegment(sketch, "E2422", {"start": v(-39.37, 6.88) * mm, "end": v(-39.55, 5.63) * mm});
            skLineSegment(sketch, "E2423", {"start": v(-39.55, 5.63) * mm, "end": v(-39.74, 4.38) * mm});
            skLineSegment(sketch, "E2424", {"start": v(-39.74, 4.38) * mm, "end": v(-39.92, 3.13) * mm});
            skLineSegment(sketch, "E2425", {"start": v(-39.92, 3.13) * mm, "end": v(-40.1, 1.88) * mm});
            skLineSegment(sketch, "E2426", {"start": v(-40.1, 1.88) * mm, "end": v(-40.3, 0.63) * mm});
            skLineSegment(sketch, "E2427", {"start": v(-40.3, 0.63) * mm, "end": v(-40.48, -0.62) * mm});
            skLineSegment(sketch, "E2428", {"start": v(-40.48, -0.62) * mm, "end": v(-40.66, -1.87) * mm});
            skLineSegment(sketch, "E2429", {"start": v(-40.66, -1.87) * mm, "end": v(-40.85, -3.11) * mm});
            skLineSegment(sketch, "E2430", {"start": v(-40.85, -3.11) * mm, "end": v(-40.87, -3.32) * mm});
            skLineSegment(sketch, "E2431", {"start": v(-40.87, -3.32) * mm, "end": v(-40.88, -3.53) * mm});
            skLineSegment(sketch, "E2432", {"start": v(-40.88, -3.53) * mm, "end": v(-40.9, -3.73) * mm});
            skLineSegment(sketch, "E2433", {"start": v(-40.9, -3.73) * mm, "end": v(-40.92, -3.94) * mm});
            skLineSegment(sketch, "E2434", {"start": v(-40.92, -3.94) * mm, "end": v(-40.94, -4.14) * mm});
            skLineSegment(sketch, "E2435", {"start": v(-40.94, -4.14) * mm, "end": v(-40.96, -4.35) * mm});
            skLineSegment(sketch, "E2436", {"start": v(-40.96, -4.35) * mm, "end": v(-40.98, -4.55) * mm});
            skLineSegment(sketch, "E2437", {"start": v(-40.98, -4.55) * mm, "end": v(-41, -4.76) * mm});
            skLineSegment(sketch, "E2438", {"start": v(-41, -4.76) * mm, "end": v(-41.02, -4.97) * mm});
            skLineSegment(sketch, "E2439", {"start": v(-41.02, -4.97) * mm, "end": v(-41.04, -5.17) * mm});
            skLineSegment(sketch, "E2440", {"start": v(-41.04, -5.17) * mm, "end": v(-41.06, -5.38) * mm});
            skLineSegment(sketch, "E2441", {"start": v(-41.06, -5.38) * mm, "end": v(-41.08, -5.58) * mm});
            skLineSegment(sketch, "E2442", {"start": v(-41.08, -5.58) * mm, "end": v(-41.1, -5.79) * mm});
            skLineSegment(sketch, "E2443", {"start": v(-41.1, -5.79) * mm, "end": v(-41.12, -6) * mm});
            skLineSegment(sketch, "E2444", {"start": v(-41.12, -6) * mm, "end": v(-41.13, -6.2) * mm});
            skLineSegment(sketch, "E2445", {"start": v(-41.13, -6.2) * mm, "end": v(-41.15, -6.4) * mm});
            skLineSegment(sketch, "E2446", {"start": v(-41.15, -6.4) * mm, "end": v(-41.16, -6.46) * mm});
            skLineSegment(sketch, "E2447", {"start": v(-41.16, -6.46) * mm, "end": v(-41.16, -6.51) * mm});
            skLineSegment(sketch, "E2448", {"start": v(-41.16, -6.51) * mm, "end": v(-41.17, -6.56) * mm});
            skLineSegment(sketch, "E2449", {"start": v(-41.17, -6.56) * mm, "end": v(-41.17, -6.61) * mm});
            skLineSegment(sketch, "E2450", {"start": v(-41.17, -6.61) * mm, "end": v(-41.18, -6.67) * mm});
            skLineSegment(sketch, "E2451", {"start": v(-41.18, -6.67) * mm, "end": v(-41.18, -6.72) * mm});
            skLineSegment(sketch, "E2452", {"start": v(-41.18, -6.72) * mm, "end": v(-41.18, -6.77) * mm});
            skLineSegment(sketch, "E2453", {"start": v(-41.18, -6.77) * mm, "end": v(-41.19, -6.82) * mm});
            skLineSegment(sketch, "E2454", {"start": v(-41.19, -6.82) * mm, "end": v(-41.2, -6.87) * mm});
            skLineSegment(sketch, "E2455", {"start": v(-41.2, -6.87) * mm, "end": v(-41.2, -6.92) * mm});
            skLineSegment(sketch, "E2456", {"start": v(-41.2, -6.92) * mm, "end": v(-41.2, -6.98) * mm});
            skLineSegment(sketch, "E2457", {"start": v(-41.2, -6.98) * mm, "end": v(-41.2, -7.03) * mm});
            skLineSegment(sketch, "E2458", {"start": v(-41.2, -7.03) * mm, "end": v(-41.21, -7.08) * mm});
            skLineSegment(sketch, "E2459", {"start": v(-41.21, -7.08) * mm, "end": v(-41.22, -7.13) * mm});
            skLineSegment(sketch, "E2460", {"start": v(-41.22, -7.13) * mm, "end": v(-41.22, -7.18) * mm});
            skLineSegment(sketch, "E2461", {"start": v(-41.22, -7.18) * mm, "end": v(-41.22, -7.24) * mm});
            skLineSegment(sketch, "E2462", {"start": v(-41.22, -7.24) * mm, "end": v(-41.23, -7.24) * mm});
            skLineSegment(sketch, "E2463", {"start": v(-41.23, -7.24) * mm, "end": v(-41.24, -7.24) * mm});
            skLineSegment(sketch, "E2464", {"start": v(-41.24, -7.24) * mm, "end": v(-41.24, -7.24) * mm});
            skLineSegment(sketch, "E2465", {"start": v(-41.24, -7.24) * mm, "end": v(-41.25, -7.24) * mm});
            skLineSegment(sketch, "E2466", {"start": v(-41.25, -7.24) * mm, "end": v(-41.25, -7.24) * mm});
            skLineSegment(sketch, "E2467", {"start": v(-41.25, -7.24) * mm, "end": v(-41.26, -7.24) * mm});
            skLineSegment(sketch, "E2468", {"start": v(-41.26, -7.24) * mm, "end": v(-41.27, -7.24) * mm});
            skLineSegment(sketch, "E2469", {"start": v(-41.27, -7.24) * mm, "end": v(-41.27, -7.24) * mm});
            skLineSegment(sketch, "E2470", {"start": v(-41.27, -7.24) * mm, "end": v(-41.28, -7.24) * mm});
            skLineSegment(sketch, "E2471", {"start": v(-41.28, -7.24) * mm, "end": v(-41.28, -7.24) * mm});
            skLineSegment(sketch, "E2472", {"start": v(-41.28, -7.24) * mm, "end": v(-41.29, -7.24) * mm});
            skLineSegment(sketch, "E2473", {"start": v(-41.29, -7.24) * mm, "end": v(-41.3, -7.24) * mm});
            skLineSegment(sketch, "E2474", {"start": v(-41.3, -7.24) * mm, "end": v(-41.3, -7.24) * mm});
            skLineSegment(sketch, "E2475", {"start": v(-41.3, -7.24) * mm, "end": v(-41.31, -7.24) * mm});
            skLineSegment(sketch, "E2476", {"start": v(-41.31, -7.24) * mm, "end": v(-41.32, -7.24) * mm});
            skLineSegment(sketch, "E2477", {"start": v(-41.32, -7.24) * mm, "end": v(-41.33, -7.11) * mm});
            skLineSegment(sketch, "E2478", {"start": v(-41.33, -7.11) * mm, "end": v(-41.35, -6.99) * mm});
            skLineSegment(sketch, "E2479", {"start": v(-41.35, -6.99) * mm, "end": v(-41.36, -6.87) * mm});
            skLineSegment(sketch, "E2480", {"start": v(-41.36, -6.87) * mm, "end": v(-41.38, -6.74) * mm});
            skLineSegment(sketch, "E2481", {"start": v(-41.38, -6.74) * mm, "end": v(-41.4, -6.62) * mm});
            skLineSegment(sketch, "E2482", {"start": v(-41.4, -6.62) * mm, "end": v(-41.4, -6.5) * mm});
            skLineSegment(sketch, "E2483", {"start": v(-41.4, -6.5) * mm, "end": v(-41.42, -6.38) * mm});
            skLineSegment(sketch, "E2484", {"start": v(-41.42, -6.38) * mm, "end": v(-41.44, -6.25) * mm});
            skLineSegment(sketch, "E2485", {"start": v(-41.44, -6.25) * mm, "end": v(-41.45, -6.13) * mm});
            skLineSegment(sketch, "E2486", {"start": v(-41.45, -6.13) * mm, "end": v(-41.47, -6) * mm});
            skLineSegment(sketch, "E2487", {"start": v(-41.47, -6) * mm, "end": v(-41.48, -5.88) * mm});
            skLineSegment(sketch, "E2488", {"start": v(-41.48, -5.88) * mm, "end": v(-41.5, -5.76) * mm});
            skLineSegment(sketch, "E2489", {"start": v(-41.5, -5.76) * mm, "end": v(-41.51, -5.64) * mm});
            skLineSegment(sketch, "E2490", {"start": v(-41.51, -5.64) * mm, "end": v(-41.53, -5.52) * mm});
            skLineSegment(sketch, "E2491", {"start": v(-41.53, -5.52) * mm, "end": v(-41.54, -5.4) * mm});
            skLineSegment(sketch, "E2492", {"start": v(-41.54, -5.4) * mm, "end": v(-41.56, -5.27) * mm});
            skLineSegment(sketch, "E2493", {"start": v(-41.56, -5.27) * mm, "end": v(-41.58, -5.14) * mm});
            skLineSegment(sketch, "E2494", {"start": v(-41.58, -5.14) * mm, "end": v(-41.6, -5.02) * mm});
            skLineSegment(sketch, "E2495", {"start": v(-41.6, -5.02) * mm, "end": v(-41.61, -4.9) * mm});
            skLineSegment(sketch, "E2496", {"start": v(-41.61, -4.9) * mm, "end": v(-41.63, -4.77) * mm});
            skLineSegment(sketch, "E2497", {"start": v(-41.63, -4.77) * mm, "end": v(-41.65, -4.64) * mm});
            skLineSegment(sketch, "E2498", {"start": v(-41.65, -4.64) * mm, "end": v(-41.67, -4.51) * mm});
            skLineSegment(sketch, "E2499", {"start": v(-41.67, -4.51) * mm, "end": v(-41.7, -4.39) * mm});
            skLineSegment(sketch, "E2500", {"start": v(-41.7, -4.39) * mm, "end": v(-41.71, -4.26) * mm});
            skLineSegment(sketch, "E2501", {"start": v(-41.71, -4.26) * mm, "end": v(-41.73, -4.14) * mm});
            skLineSegment(sketch, "E2502", {"start": v(-41.73, -4.14) * mm, "end": v(-41.75, -4.01) * mm});
            skLineSegment(sketch, "E2503", {"start": v(-41.75, -4.01) * mm, "end": v(-41.77, -3.89) * mm});
            skLineSegment(sketch, "E2504", {"start": v(-41.77, -3.89) * mm, "end": v(-41.79, -3.76) * mm});
            skLineSegment(sketch, "E2505", {"start": v(-41.79, -3.76) * mm, "end": v(-41.8, -3.63) * mm});
            skLineSegment(sketch, "E2506", {"start": v(-41.8, -3.63) * mm, "end": v(-41.83, -3.5) * mm});
            skLineSegment(sketch, "E2507", {"start": v(-41.83, -3.5) * mm, "end": v(-41.84, -3.38) * mm});
            skLineSegment(sketch, "E2508", {"start": v(-41.84, -3.38) * mm, "end": v(-41.86, -3.26) * mm});
            skLineSegment(sketch, "E2509", {"start": v(-41.86, -3.26) * mm, "end": v(-42.14, -2) * mm});
            skLineSegment(sketch, "E2510", {"start": v(-42.14, -2) * mm, "end": v(-42.4, -0.74) * mm});
            skLineSegment(sketch, "E2511", {"start": v(-42.4, -0.74) * mm, "end": v(-42.68, 0.52) * mm});
            skLineSegment(sketch, "E2512", {"start": v(-42.68, 0.52) * mm, "end": v(-42.95, 1.78) * mm});
            skLineSegment(sketch, "E2513", {"start": v(-42.95, 1.78) * mm, "end": v(-43.23, 3.03) * mm});
            skLineSegment(sketch, "E2514", {"start": v(-43.23, 3.03) * mm, "end": v(-43.5, 4.3) * mm});
            skLineSegment(sketch, "E2515", {"start": v(-43.5, 4.3) * mm, "end": v(-43.77, 5.55) * mm});
            skLineSegment(sketch, "E2516", {"start": v(-43.77, 5.55) * mm, "end": v(-44.04, 6.8) * mm});
            skLineSegment(sketch, "E2517", {"start": v(-44.04, 6.8) * mm, "end": v(-44.32, 8.07) * mm});
            skLineSegment(sketch, "E2518", {"start": v(-44.32, 8.07) * mm, "end": v(-44.59, 9.33) * mm});
            skLineSegment(sketch, "E2519", {"start": v(-44.59, 9.33) * mm, "end": v(-44.86, 10.58) * mm});
            skLineSegment(sketch, "E2520", {"start": v(-44.86, 10.58) * mm, "end": v(-45.13, 11.84) * mm});
            skLineSegment(sketch, "E2521", {"start": v(-45.13, 11.84) * mm, "end": v(-45.4, 13.1) * mm});
            skLineSegment(sketch, "E2522", {"start": v(-45.4, 13.1) * mm, "end": v(-45.68, 14.36) * mm});
            skLineSegment(sketch, "E2523", {"start": v(-45.68, 14.36) * mm, "end": v(-45.95, 15.62) * mm});
            skLineSegment(sketch, "E2524", {"start": v(-45.95, 15.62) * mm, "end": v(-46.22, 16.88) * mm});
            skLineSegment(sketch, "E2525", {"start": v(-46.22, 16.88) * mm, "end": v(-46.92, 16.88) * mm});
            skLineSegment(sketch, "E2526", {"start": v(-46.92, 16.88) * mm, "end": v(-47.43, 16.88) * mm});
            skLineSegment(sketch, "E2527", {"start": v(-47.43, 16.88) * mm, "end": v(-46.95, 16.98) * mm});
            skLineSegment(sketch, "E2528", {"start": v(-46.95, 16.98) * mm, "end": v(-46.38, 17.12) * mm});
            skLineSegment(sketch, "E2529", {"start": v(-46.38, 17.12) * mm, "end": v(-45.81, 17.28) * mm});
            skLineSegment(sketch, "E2530", {"start": v(-45.81, 17.28) * mm, "end": v(-45.26, 17.46) * mm});
            skLineSegment(sketch, "E2531", {"start": v(-45.26, 17.46) * mm, "end": v(-44.7, 17.65) * mm});
            skLineSegment(sketch, "E2532", {"start": v(-44.7, 17.65) * mm, "end": v(-44.17, 17.86) * mm});
            skLineSegment(sketch, "E2533", {"start": v(-56.05, 25.57) * mm, "end": v(-56.05, 26.7) * mm});
            skLineSegment(sketch, "E2534", {"start": v(-56.05, 26.7) * mm, "end": v(-56.05, 27.81) * mm});
            skLineSegment(sketch, "E2535", {"start": v(-56.05, 27.81) * mm, "end": v(-56.05, 28.93) * mm});
            skLineSegment(sketch, "E2536", {"start": v(-56.05, 28.93) * mm, "end": v(-56.05, 30.06) * mm});
            skLineSegment(sketch, "E2537", {"start": v(-56.05, 30.06) * mm, "end": v(-56.05, 31.18) * mm});
            skLineSegment(sketch, "E2538", {"start": v(-56.05, 31.18) * mm, "end": v(-56.05, 32.3) * mm});
            skLineSegment(sketch, "E2539", {"start": v(-56.05, 32.3) * mm, "end": v(-56.05, 33.42) * mm});
            skLineSegment(sketch, "E2540", {"start": v(-56.05, 33.42) * mm, "end": v(-56.05, 34.54) * mm});
            skLineSegment(sketch, "E2541", {"start": v(-56.05, 34.54) * mm, "end": v(-56.05, 35.67) * mm});
            skLineSegment(sketch, "E2542", {"start": v(-56.05, 35.67) * mm, "end": v(-56.05, 36.79) * mm});
            skLineSegment(sketch, "E2543", {"start": v(-56.05, 36.79) * mm, "end": v(-56.05, 37.91) * mm});
            skLineSegment(sketch, "E2544", {"start": v(-56.05, 37.91) * mm, "end": v(-56.05, 39.03) * mm});
            skLineSegment(sketch, "E2545", {"start": v(-56.05, 39.03) * mm, "end": v(-56.05, 40.16) * mm});
            skLineSegment(sketch, "E2546", {"start": v(-56.05, 40.16) * mm, "end": v(-56.05, 41.28) * mm});
            skLineSegment(sketch, "E2547", {"start": v(-56.05, 41.28) * mm, "end": v(-56.05, 42.4) * mm});
            skLineSegment(sketch, "E2548", {"start": v(-56.05, 42.4) * mm, "end": v(-55.88, 42.4) * mm});
            skLineSegment(sketch, "E2549", {"start": v(-55.88, 42.4) * mm, "end": v(-55.72, 42.4) * mm});
            skLineSegment(sketch, "E2550", {"start": v(-55.72, 42.4) * mm, "end": v(-55.55, 42.4) * mm});
            skLineSegment(sketch, "E2551", {"start": v(-55.55, 42.4) * mm, "end": v(-55.4, 42.4) * mm});
            skLineSegment(sketch, "E2552", {"start": v(-55.4, 42.4) * mm, "end": v(-55.23, 42.4) * mm});
            skLineSegment(sketch, "E2553", {"start": v(-55.23, 42.4) * mm, "end": v(-55.06, 42.4) * mm});
            skLineSegment(sketch, "E2554", {"start": v(-55.06, 42.4) * mm, "end": v(-54.9, 42.4) * mm});
            skLineSegment(sketch, "E2555", {"start": v(-54.9, 42.4) * mm, "end": v(-54.73, 42.4) * mm});
            skLineSegment(sketch, "E2556", {"start": v(-54.73, 42.4) * mm, "end": v(-54.57, 42.4) * mm});
            skLineSegment(sketch, "E2557", {"start": v(-54.57, 42.4) * mm, "end": v(-54.4, 42.4) * mm});
            skLineSegment(sketch, "E2558", {"start": v(-54.4, 42.4) * mm, "end": v(-54.24, 42.4) * mm});
            skLineSegment(sketch, "E2559", {"start": v(-54.24, 42.4) * mm, "end": v(-54.08, 42.4) * mm});
            skLineSegment(sketch, "E2560", {"start": v(-54.08, 42.4) * mm, "end": v(-53.91, 42.4) * mm});
            skLineSegment(sketch, "E2561", {"start": v(-53.91, 42.4) * mm, "end": v(-53.75, 42.4) * mm});
            skLineSegment(sketch, "E2562", {"start": v(-53.75, 42.4) * mm, "end": v(-53.58, 42.4) * mm});
            skLineSegment(sketch, "E2563", {"start": v(-53.58, 42.4) * mm, "end": v(-53.42, 42.4) * mm});
            skLineSegment(sketch, "E2564", {"start": v(-53.42, 42.4) * mm, "end": v(-53.1, 42.4) * mm});
            skLineSegment(sketch, "E2565", {"start": v(-53.1, 42.4) * mm, "end": v(-52.8, 42.38) * mm});
            skLineSegment(sketch, "E2566", {"start": v(-52.8, 42.38) * mm, "end": v(-52.5, 42.36) * mm});
            skLineSegment(sketch, "E2567", {"start": v(-52.5, 42.36) * mm, "end": v(-52.2, 42.33) * mm});
            skLineSegment(sketch, "E2568", {"start": v(-52.2, 42.33) * mm, "end": v(-51.9, 42.3) * mm});
            skLineSegment(sketch, "E2569", {"start": v(-51.9, 42.3) * mm, "end": v(-51.61, 42.25) * mm});
            skLineSegment(sketch, "E2570", {"start": v(-51.61, 42.25) * mm, "end": v(-51.33, 42.2) * mm});
            skLineSegment(sketch, "E2571", {"start": v(-51.33, 42.2) * mm, "end": v(-51.05, 42.13) * mm});
            skLineSegment(sketch, "E2572", {"start": v(-51.05, 42.13) * mm, "end": v(-50.78, 42.05) * mm});
            skLineSegment(sketch, "E2573", {"start": v(-50.78, 42.05) * mm, "end": v(-50.5, 41.97) * mm});
            skLineSegment(sketch, "E2574", {"start": v(-50.5, 41.97) * mm, "end": v(-50.25, 41.88) * mm});
            skLineSegment(sketch, "E2575", {"start": v(-50.25, 41.88) * mm, "end": v(-50, 41.79) * mm});
            skLineSegment(sketch, "E2576", {"start": v(-50, 41.79) * mm, "end": v(-49.74, 41.68) * mm});
            skLineSegment(sketch, "E2577", {"start": v(-49.74, 41.68) * mm, "end": v(-49.5, 41.57) * mm});
            skLineSegment(sketch, "E2578", {"start": v(-49.5, 41.57) * mm, "end": v(-49.25, 41.44) * mm});
            skLineSegment(sketch, "E2579", {"start": v(-49.25, 41.44) * mm, "end": v(-49.01, 41.3) * mm});
            skLineSegment(sketch, "E2580", {"start": v(-49.01, 41.3) * mm, "end": v(-48.78, 41.17) * mm});
            skLineSegment(sketch, "E2581", {"start": v(-48.78, 41.17) * mm, "end": v(-48.56, 41.02) * mm});
            skLineSegment(sketch, "E2582", {"start": v(-48.56, 41.02) * mm, "end": v(-48.34, 40.87) * mm});
            skLineSegment(sketch, "E2583", {"start": v(-48.34, 40.87) * mm, "end": v(-48.13, 40.7) * mm});
            skLineSegment(sketch, "E2584", {"start": v(-48.13, 40.7) * mm, "end": v(-47.93, 40.54) * mm});
            skLineSegment(sketch, "E2585", {"start": v(-47.93, 40.54) * mm, "end": v(-47.73, 40.37) * mm});
            skLineSegment(sketch, "E2586", {"start": v(-47.73, 40.37) * mm, "end": v(-47.54, 40.18) * mm});
            skLineSegment(sketch, "E2587", {"start": v(-47.54, 40.18) * mm, "end": v(-47.36, 40) * mm});
            skLineSegment(sketch, "E2588", {"start": v(-47.36, 40) * mm, "end": v(-47.18, 39.8) * mm});
            skLineSegment(sketch, "E2589", {"start": v(-47.18, 39.8) * mm, "end": v(-47.01, 39.6) * mm});
            skLineSegment(sketch, "E2590", {"start": v(-47.01, 39.6) * mm, "end": v(-46.85, 39.39) * mm});
            skLineSegment(sketch, "E2591", {"start": v(-46.85, 39.39) * mm, "end": v(-46.7, 39.17) * mm});
            skLineSegment(sketch, "E2592", {"start": v(-46.7, 39.17) * mm, "end": v(-46.54, 38.95) * mm});
            skLineSegment(sketch, "E2593", {"start": v(-46.54, 38.95) * mm, "end": v(-46.4, 38.71) * mm});
            skLineSegment(sketch, "E2594", {"start": v(-46.4, 38.71) * mm, "end": v(-46.26, 38.48) * mm});
            skLineSegment(sketch, "E2595", {"start": v(-46.26, 38.48) * mm, "end": v(-46.14, 38.23) * mm});
            skLineSegment(sketch, "E2596", {"start": v(-46.14, 38.23) * mm, "end": v(-46.01, 37.98) * mm});
            skLineSegment(sketch, "E2597", {"start": v(-46.01, 37.98) * mm, "end": v(-45.9, 37.73) * mm});
            skLineSegment(sketch, "E2598", {"start": v(-45.9, 37.73) * mm, "end": v(-45.8, 37.47) * mm});
            skLineSegment(sketch, "E2599", {"start": v(-45.8, 37.47) * mm, "end": v(-45.7, 37.2) * mm});
            skLineSegment(sketch, "E2600", {"start": v(-45.7, 37.2) * mm, "end": v(-45.6, 36.94) * mm});
            skLineSegment(sketch, "E2601", {"start": v(-45.6, 36.94) * mm, "end": v(-45.52, 36.67) * mm});
            skLineSegment(sketch, "E2602", {"start": v(-45.52, 36.67) * mm, "end": v(-45.45, 36.4) * mm});
            skLineSegment(sketch, "E2603", {"start": v(-45.45, 36.4) * mm, "end": v(-45.38, 36.12) * mm});
            skLineSegment(sketch, "E2604", {"start": v(-45.38, 36.12) * mm, "end": v(-45.32, 35.84) * mm});
            skLineSegment(sketch, "E2605", {"start": v(-45.32, 35.84) * mm, "end": v(-45.27, 35.55) * mm});
            skLineSegment(sketch, "E2606", {"start": v(-45.27, 35.55) * mm, "end": v(-45.23, 35.26) * mm});
            skLineSegment(sketch, "E2607", {"start": v(-45.23, 35.26) * mm, "end": v(-45.2, 34.97) * mm});
            skLineSegment(sketch, "E2608", {"start": v(-45.2, 34.97) * mm, "end": v(-45.16, 34.67) * mm});
            skLineSegment(sketch, "E2609", {"start": v(-45.16, 34.67) * mm, "end": v(-45.14, 34.37) * mm});
            skLineSegment(sketch, "E2610", {"start": v(-45.14, 34.37) * mm, "end": v(-45.13, 34.06) * mm});
            skLineSegment(sketch, "E2611", {"start": v(-45.13, 34.06) * mm, "end": v(-45.13, 33.75) * mm});
            skLineSegment(sketch, "E2612", {"start": v(-45.13, 33.75) * mm, "end": v(-45.14, 33.23) * mm});
            skLineSegment(sketch, "E2613", {"start": v(-45.14, 33.23) * mm, "end": v(-45.16, 32.72) * mm});
            skLineSegment(sketch, "E2614", {"start": v(-45.16, 32.72) * mm, "end": v(-45.2, 32.22) * mm});
            skLineSegment(sketch, "E2615", {"start": v(-45.2, 32.22) * mm, "end": v(-45.27, 31.73) * mm});
            skLineSegment(sketch, "E2616", {"start": v(-45.27, 31.73) * mm, "end": v(-45.34, 31.26) * mm});
            skLineSegment(sketch, "E2617", {"start": v(-45.34, 31.26) * mm, "end": v(-45.44, 30.8) * mm});
            skLineSegment(sketch, "E2618", {"start": v(-45.44, 30.8) * mm, "end": v(-45.55, 30.36) * mm});
            skLineSegment(sketch, "E2619", {"start": v(-45.55, 30.36) * mm, "end": v(-45.68, 29.93) * mm});
            skLineSegment(sketch, "E2620", {"start": v(-45.68, 29.93) * mm, "end": v(-45.82, 29.5) * mm});
            skLineSegment(sketch, "E2621", {"start": v(-45.82, 29.5) * mm, "end": v(-45.98, 29.1) * mm});
            skLineSegment(sketch, "E2622", {"start": v(-45.98, 29.1) * mm, "end": v(-46.16, 28.72) * mm});
            skLineSegment(sketch, "E2623", {"start": v(-46.16, 28.72) * mm, "end": v(-46.36, 28.34) * mm});
            skLineSegment(sketch, "E2624", {"start": v(-46.36, 28.34) * mm, "end": v(-46.58, 27.98) * mm});
            skLineSegment(sketch, "E2625", {"start": v(-46.58, 27.98) * mm, "end": v(-46.8, 27.63) * mm});
            skLineSegment(sketch, "E2626", {"start": v(-46.8, 27.63) * mm, "end": v(-47.05, 27.3) * mm});
            skLineSegment(sketch, "E2627", {"start": v(-47.05, 27.3) * mm, "end": v(-47.32, 26.97) * mm});
            skLineSegment(sketch, "E2628", {"start": v(-47.32, 26.97) * mm, "end": v(-47.6, 26.66) * mm});
            skLineSegment(sketch, "E2629", {"start": v(-47.6, 26.66) * mm, "end": v(-47.9, 26.38) * mm});
            skLineSegment(sketch, "E2630", {"start": v(-47.9, 26.38) * mm, "end": v(-48.2, 26.11) * mm});
            skLineSegment(sketch, "E2631", {"start": v(-48.2, 26.11) * mm, "end": v(-48.5, 25.87) * mm});
            skLineSegment(sketch, "E2632", {"start": v(-48.5, 25.87) * mm, "end": v(-48.83, 25.64) * mm});
            skLineSegment(sketch, "E2633", {"start": v(-48.83, 25.64) * mm, "end": v(-49.17, 25.43) * mm});
            skLineSegment(sketch, "E2634", {"start": v(-49.17, 25.43) * mm, "end": v(-49.52, 25.24) * mm});
            skLineSegment(sketch, "E2635", {"start": v(-49.52, 25.24) * mm, "end": v(-49.88, 25.08) * mm});
            skLineSegment(sketch, "E2636", {"start": v(-49.88, 25.08) * mm, "end": v(-50.25, 24.93) * mm});
            skLineSegment(sketch, "E2637", {"start": v(-50.25, 24.93) * mm, "end": v(-50.64, 24.8) * mm});
            skLineSegment(sketch, "E2638", {"start": v(-50.64, 24.8) * mm, "end": v(-51.03, 24.7) * mm});
            skLineSegment(sketch, "E2639", {"start": v(-51.03, 24.7) * mm, "end": v(-51.44, 24.6) * mm});
            skLineSegment(sketch, "E2640", {"start": v(-51.44, 24.6) * mm, "end": v(-51.86, 24.53) * mm});
            skLineSegment(sketch, "E2641", {"start": v(-51.86, 24.53) * mm, "end": v(-52.29, 24.49) * mm});
            skLineSegment(sketch, "E2642", {"start": v(-52.29, 24.49) * mm, "end": v(-52.73, 24.46) * mm});
            skLineSegment(sketch, "E2643", {"start": v(-52.73, 24.46) * mm, "end": v(-53.18, 24.45) * mm});
            skLineSegment(sketch, "E2644", {"start": v(-53.18, 24.45) * mm, "end": v(-53.36, 24.45) * mm});
            skLineSegment(sketch, "E2645", {"start": v(-53.36, 24.45) * mm, "end": v(-53.54, 24.45) * mm});
            skLineSegment(sketch, "E2646", {"start": v(-53.54, 24.45) * mm, "end": v(-53.72, 24.45) * mm});
            skLineSegment(sketch, "E2647", {"start": v(-53.72, 24.45) * mm, "end": v(-53.9, 24.45) * mm});
            skLineSegment(sketch, "E2648", {"start": v(-53.9, 24.45) * mm, "end": v(-54.08, 24.45) * mm});
            skLineSegment(sketch, "E2649", {"start": v(-54.08, 24.45) * mm, "end": v(-54.26, 24.45) * mm});
            skLineSegment(sketch, "E2650", {"start": v(-54.26, 24.45) * mm, "end": v(-54.44, 24.45) * mm});
            skLineSegment(sketch, "E2651", {"start": v(-54.44, 24.45) * mm, "end": v(-54.61, 24.45) * mm});
            skLineSegment(sketch, "E2652", {"start": v(-54.61, 24.45) * mm, "end": v(-54.8, 24.45) * mm});
            skLineSegment(sketch, "E2653", {"start": v(-54.8, 24.45) * mm, "end": v(-54.97, 24.45) * mm});
            skLineSegment(sketch, "E2654", {"start": v(-54.97, 24.45) * mm, "end": v(-55.15, 24.45) * mm});
            skLineSegment(sketch, "E2655", {"start": v(-55.15, 24.45) * mm, "end": v(-55.33, 24.45) * mm});
            skLineSegment(sketch, "E2656", {"start": v(-55.33, 24.45) * mm, "end": v(-55.51, 24.45) * mm});
            skLineSegment(sketch, "E2657", {"start": v(-55.51, 24.45) * mm, "end": v(-55.69, 24.45) * mm});
            skLineSegment(sketch, "E2658", {"start": v(-55.69, 24.45) * mm, "end": v(-55.87, 24.45) * mm});
            skLineSegment(sketch, "E2659", {"start": v(-55.87, 24.45) * mm, "end": v(-56.05, 24.45) * mm});
            skLineSegment(sketch, "E2660", {"start": v(-56.05, 24.45) * mm, "end": v(-56.05, 25.57) * mm});
            skLineSegment(sketch, "E2661", {"start": v(-59.94, -29.52) * mm, "end": v(-59.94, -29.12) * mm});
            skLineSegment(sketch, "E2662", {"start": v(-59.94, -29.12) * mm, "end": v(-59.94, -28.71) * mm});
            skLineSegment(sketch, "E2663", {"start": v(-59.94, -28.71) * mm, "end": v(-59.94, -28.31) * mm});
            skLineSegment(sketch, "E2664", {"start": v(-59.94, -28.31) * mm, "end": v(-59.94, -27.91) * mm});
            skLineSegment(sketch, "E2665", {"start": v(-59.94, -27.91) * mm, "end": v(-59.94, -27.51) * mm});
            skLineSegment(sketch, "E2666", {"start": v(-59.94, -27.51) * mm, "end": v(-59.94, -27.1) * mm});
            skLineSegment(sketch, "E2667", {"start": v(-59.94, -27.1) * mm, "end": v(-59.94, -26.7) * mm});
            skLineSegment(sketch, "E2668", {"start": v(-59.94, -26.7) * mm, "end": v(-59.94, -26.3) * mm});
            skLineSegment(sketch, "E2669", {"start": v(-59.94, -26.3) * mm, "end": v(-59.94, -25.9) * mm});
            skLineSegment(sketch, "E2670", {"start": v(-59.94, -25.9) * mm, "end": v(-59.94, -25.5) * mm});
            skLineSegment(sketch, "E2671", {"start": v(-59.94, -25.5) * mm, "end": v(-59.94, -25.1) * mm});
            skLineSegment(sketch, "E2672", {"start": v(-59.94, -25.1) * mm, "end": v(-59.94, -24.7) * mm});
            skLineSegment(sketch, "E2673", {"start": v(-59.94, -24.7) * mm, "end": v(-59.94, -24.3) * mm});
            skLineSegment(sketch, "E2674", {"start": v(-59.94, -24.3) * mm, "end": v(-59.94, -23.9) * mm});
            skLineSegment(sketch, "E2675", {"start": v(-59.94, -23.9) * mm, "end": v(-59.94, -23.5) * mm});
            skLineSegment(sketch, "E2676", {"start": v(-59.94, -23.5) * mm, "end": v(-59.82, -23.5) * mm});
            skLineSegment(sketch, "E2677", {"start": v(-59.82, -23.5) * mm, "end": v(-59.7, -23.5) * mm});
            skLineSegment(sketch, "E2678", {"start": v(-59.7, -23.5) * mm, "end": v(-59.58, -23.5) * mm});
            skLineSegment(sketch, "E2679", {"start": v(-59.58, -23.5) * mm, "end": v(-59.46, -23.5) * mm});
            skLineSegment(sketch, "E2680", {"start": v(-59.46, -23.5) * mm, "end": v(-59.35, -23.5) * mm});
            skLineSegment(sketch, "E2681", {"start": v(-59.35, -23.5) * mm, "end": v(-59.23, -23.5) * mm});
            skLineSegment(sketch, "E2682", {"start": v(-59.23, -23.5) * mm, "end": v(-59.1, -23.5) * mm});
            skLineSegment(sketch, "E2683", {"start": v(-59.1, -23.5) * mm, "end": v(-59, -23.5) * mm});
            skLineSegment(sketch, "E2684", {"start": v(-59, -23.5) * mm, "end": v(-58.87, -23.5) * mm});
            skLineSegment(sketch, "E2685", {"start": v(-58.87, -23.5) * mm, "end": v(-58.75, -23.5) * mm});
            skLineSegment(sketch, "E2686", {"start": v(-58.75, -23.5) * mm, "end": v(-58.64, -23.5) * mm});
            skLineSegment(sketch, "E2687", {"start": v(-58.64, -23.5) * mm, "end": v(-58.52, -23.5) * mm});
            skLineSegment(sketch, "E2688", {"start": v(-58.52, -23.5) * mm, "end": v(-58.4, -23.5) * mm});
            skLineSegment(sketch, "E2689", {"start": v(-58.4, -23.5) * mm, "end": v(-58.28, -23.5) * mm});
            skLineSegment(sketch, "E2690", {"start": v(-58.28, -23.5) * mm, "end": v(-58.16, -23.5) * mm});
            skLineSegment(sketch, "E2691", {"start": v(-58.16, -23.5) * mm, "end": v(-58.04, -23.5) * mm});
            skLineSegment(sketch, "E2692", {"start": v(-58.04, -23.5) * mm, "end": v(-57.44, -23.51) * mm});
            skLineSegment(sketch, "E2693", {"start": v(-57.44, -23.51) * mm, "end": v(-56.88, -23.55) * mm});
            skLineSegment(sketch, "E2694", {"start": v(-56.88, -23.55) * mm, "end": v(-56.36, -23.6) * mm});
            skLineSegment(sketch, "E2695", {"start": v(-56.36, -23.6) * mm, "end": v(-55.88, -23.7) * mm});
            skLineSegment(sketch, "E2696", {"start": v(-55.88, -23.7) * mm, "end": v(-55.43, -23.8) * mm});
            skLineSegment(sketch, "E2697", {"start": v(-55.43, -23.8) * mm, "end": v(-55.03, -23.94) * mm});
            skLineSegment(sketch, "E2698", {"start": v(-55.03, -23.94) * mm, "end": v(-54.66, -24.1) * mm});
            skLineSegment(sketch, "E2699", {"start": v(-54.66, -24.1) * mm, "end": v(-54.33, -24.29) * mm});
            skLineSegment(sketch, "E2700", {"start": v(-54.33, -24.29) * mm, "end": v(-54.04, -24.5) * mm});
            skLineSegment(sketch, "E2701", {"start": v(-54.04, -24.5) * mm, "end": v(-53.79, -24.73) * mm});
            skLineSegment(sketch, "E2702", {"start": v(-53.79, -24.73) * mm, "end": v(-53.58, -24.99) * mm});
            skLineSegment(sketch, "E2703", {"start": v(-53.58, -24.99) * mm, "end": v(-53.4, -25.27) * mm});
            skLineSegment(sketch, "E2704", {"start": v(-53.4, -25.27) * mm, "end": v(-53.27, -25.58) * mm});
            skLineSegment(sketch, "E2705", {"start": v(-53.27, -25.58) * mm, "end": v(-53.17, -25.91) * mm});
            skLineSegment(sketch, "E2706", {"start": v(-53.17, -25.91) * mm, "end": v(-53.11, -26.27) * mm});
            skLineSegment(sketch, "E2707", {"start": v(-53.11, -26.27) * mm, "end": v(-53.1, -26.65) * mm});
            skLineSegment(sketch, "E2708", {"start": v(-53.1, -26.65) * mm, "end": v(-53.1, -26.83) * mm});
            skLineSegment(sketch, "E2709", {"start": v(-53.1, -26.83) * mm, "end": v(-53.1, -27) * mm});
            skLineSegment(sketch, "E2710", {"start": v(-53.1, -27) * mm, "end": v(-53.13, -27.17) * mm});
            skLineSegment(sketch, "E2711", {"start": v(-53.13, -27.17) * mm, "end": v(-53.16, -27.34) * mm});
            skLineSegment(sketch, "E2712", {"start": v(-53.16, -27.34) * mm, "end": v(-53.2, -27.5) * mm});
            skLineSegment(sketch, "E2713", {"start": v(-53.2, -27.5) * mm, "end": v(-53.25, -27.66) * mm});
            skLineSegment(sketch, "E2714", {"start": v(-53.25, -27.66) * mm, "end": v(-53.3, -27.81) * mm});
            skLineSegment(sketch, "E2715", {"start": v(-53.3, -27.81) * mm, "end": v(-53.37, -27.96) * mm});
            skLineSegment(sketch, "E2716", {"start": v(-53.37, -27.96) * mm, "end": v(-53.44, -28.1) * mm});
            skLineSegment(sketch, "E2717", {"start": v(-53.44, -28.1) * mm, "end": v(-53.52, -28.25) * mm});
            skLineSegment(sketch, "E2718", {"start": v(-53.52, -28.25) * mm, "end": v(-53.6, -28.38) * mm});
            skLineSegment(sketch, "E2719", {"start": v(-53.6, -28.38) * mm, "end": v(-53.7, -28.52) * mm});
            skLineSegment(sketch, "E2720", {"start": v(-53.7, -28.52) * mm, "end": v(-53.81, -28.64) * mm});
            skLineSegment(sketch, "E2721", {"start": v(-53.81, -28.64) * mm, "end": v(-53.93, -28.77) * mm});
            skLineSegment(sketch, "E2722", {"start": v(-53.93, -28.77) * mm, "end": v(-54.05, -28.89) * mm});
            skLineSegment(sketch, "E2723", {"start": v(-54.05, -28.89) * mm, "end": v(-54.18, -29) * mm});
            skLineSegment(sketch, "E2724", {"start": v(-54.18, -29) * mm, "end": v(-54.32, -29.12) * mm});
            skLineSegment(sketch, "E2725", {"start": v(-54.32, -29.12) * mm, "end": v(-54.46, -29.22) * mm});
            skLineSegment(sketch, "E2726", {"start": v(-54.46, -29.22) * mm, "end": v(-54.61, -29.32) * mm});
            skLineSegment(sketch, "E2727", {"start": v(-54.61, -29.32) * mm, "end": v(-54.77, -29.4) * mm});
            skLineSegment(sketch, "E2728", {"start": v(-54.77, -29.4) * mm, "end": v(-54.92, -29.49) * mm});
            skLineSegment(sketch, "E2729", {"start": v(-54.92, -29.49) * mm, "end": v(-55.09, -29.56) * mm});
            skLineSegment(sketch, "E2730", {"start": v(-55.09, -29.56) * mm, "end": v(-55.25, -29.63) * mm});
            skLineSegment(sketch, "E2731", {"start": v(-55.25, -29.63) * mm, "end": v(-55.43, -29.69) * mm});
            skLineSegment(sketch, "E2732", {"start": v(-55.43, -29.69) * mm, "end": v(-55.6, -29.74) * mm});
            skLineSegment(sketch, "E2733", {"start": v(-55.6, -29.74) * mm, "end": v(-55.78, -29.79) * mm});
            skLineSegment(sketch, "E2734", {"start": v(-55.78, -29.79) * mm, "end": v(-55.97, -29.83) * mm});
            skLineSegment(sketch, "E2735", {"start": v(-55.97, -29.83) * mm, "end": v(-56.16, -29.86) * mm});
            skLineSegment(sketch, "E2736", {"start": v(-56.16, -29.86) * mm, "end": v(-56.36, -29.89) * mm});
            skLineSegment(sketch, "E2737", {"start": v(-56.36, -29.89) * mm, "end": v(-56.56, -29.9) * mm});
            skLineSegment(sketch, "E2738", {"start": v(-56.56, -29.9) * mm, "end": v(-56.77, -29.91) * mm});
            skLineSegment(sketch, "E2739", {"start": v(-56.77, -29.91) * mm, "end": v(-56.98, -29.92) * mm});
            skLineSegment(sketch, "E2740", {"start": v(-56.98, -29.92) * mm, "end": v(-57.16, -29.92) * mm});
            skLineSegment(sketch, "E2741", {"start": v(-57.16, -29.92) * mm, "end": v(-57.35, -29.92) * mm});
            skLineSegment(sketch, "E2742", {"start": v(-57.35, -29.92) * mm, "end": v(-57.53, -29.92) * mm});
            skLineSegment(sketch, "E2743", {"start": v(-57.53, -29.92) * mm, "end": v(-57.72, -29.92) * mm});
            skLineSegment(sketch, "E2744", {"start": v(-57.72, -29.92) * mm, "end": v(-57.9, -29.92) * mm});
            skLineSegment(sketch, "E2745", {"start": v(-57.9, -29.92) * mm, "end": v(-58.09, -29.92) * mm});
            skLineSegment(sketch, "E2746", {"start": v(-58.09, -29.92) * mm, "end": v(-58.27, -29.92) * mm});
            skLineSegment(sketch, "E2747", {"start": v(-58.27, -29.92) * mm, "end": v(-58.46, -29.92) * mm});
            skLineSegment(sketch, "E2748", {"start": v(-58.46, -29.92) * mm, "end": v(-58.64, -29.92) * mm});
            skLineSegment(sketch, "E2749", {"start": v(-58.64, -29.92) * mm, "end": v(-58.83, -29.92) * mm});
            skLineSegment(sketch, "E2750", {"start": v(-58.83, -29.92) * mm, "end": v(-59.01, -29.92) * mm});
            skLineSegment(sketch, "E2751", {"start": v(-59.01, -29.92) * mm, "end": v(-59.2, -29.92) * mm});
            skLineSegment(sketch, "E2752", {"start": v(-59.2, -29.92) * mm, "end": v(-59.38, -29.92) * mm});
            skLineSegment(sketch, "E2753", {"start": v(-59.38, -29.92) * mm, "end": v(-59.57, -29.92) * mm});
            skLineSegment(sketch, "E2754", {"start": v(-59.57, -29.92) * mm, "end": v(-59.75, -29.92) * mm});
            skLineSegment(sketch, "E2755", {"start": v(-59.75, -29.92) * mm, "end": v(-59.94, -29.92) * mm});
            skLineSegment(sketch, "E2756", {"start": v(-59.94, -29.92) * mm, "end": v(-59.94, -29.52) * mm});
            skLineSegment(sketch, "E2757", {"start": v(-52.03, -40.35) * mm, "end": v(-52.05, -40.55) * mm});
            skLineSegment(sketch, "E2758", {"start": v(-52.05, -40.55) * mm, "end": v(-52.07, -40.75) * mm});
            skLineSegment(sketch, "E2759", {"start": v(-52.07, -40.75) * mm, "end": v(-52.1, -40.93) * mm});
            skLineSegment(sketch, "E2760", {"start": v(-52.1, -40.93) * mm, "end": v(-52.14, -41.12) * mm});
            skLineSegment(sketch, "E2761", {"start": v(-52.14, -41.12) * mm, "end": v(-52.2, -41.3) * mm});
            skLineSegment(sketch, "E2762", {"start": v(-52.2, -41.3) * mm, "end": v(-52.26, -41.47) * mm});
            skLineSegment(sketch, "E2763", {"start": v(-52.26, -41.47) * mm, "end": v(-52.33, -41.63) * mm});
            skLineSegment(sketch, "E2764", {"start": v(-52.33, -41.63) * mm, "end": v(-52.4, -41.8) * mm});
            skLineSegment(sketch, "E2765", {"start": v(-52.4, -41.8) * mm, "end": v(-52.5, -41.95) * mm});
            skLineSegment(sketch, "E2766", {"start": v(-52.5, -41.95) * mm, "end": v(-52.6, -42.1) * mm});
            skLineSegment(sketch, "E2767", {"start": v(-52.6, -42.1) * mm, "end": v(-52.7, -42.24) * mm});
            skLineSegment(sketch, "E2768", {"start": v(-52.7, -42.24) * mm, "end": v(-52.82, -42.38) * mm});
            skLineSegment(sketch, "E2769", {"start": v(-52.82, -42.38) * mm, "end": v(-52.95, -42.52) * mm});
            skLineSegment(sketch, "E2770", {"start": v(-52.95, -42.52) * mm, "end": v(-53.09, -42.64) * mm});
            skLineSegment(sketch, "E2771", {"start": v(-53.09, -42.64) * mm, "end": v(-53.23, -42.77) * mm});
            skLineSegment(sketch, "E2772", {"start": v(-53.23, -42.77) * mm, "end": v(-53.39, -42.88) * mm});
            skLineSegment(sketch, "E2773", {"start": v(-53.39, -42.88) * mm, "end": v(-53.55, -43) * mm});
            skLineSegment(sketch, "E2774", {"start": v(-53.55, -43) * mm, "end": v(-53.72, -43.1) * mm});
            skLineSegment(sketch, "E2775", {"start": v(-53.72, -43.1) * mm, "end": v(-53.9, -43.19) * mm});
            skLineSegment(sketch, "E2776", {"start": v(-53.9, -43.19) * mm, "end": v(-54.08, -43.27) * mm});
            skLineSegment(sketch, "E2777", {"start": v(-54.08, -43.27) * mm, "end": v(-54.26, -43.35) * mm});
            skLineSegment(sketch, "E2778", {"start": v(-54.26, -43.35) * mm, "end": v(-54.46, -43.42) * mm});
            skLineSegment(sketch, "E2779", {"start": v(-54.46, -43.42) * mm, "end": v(-54.66, -43.49) * mm});
            skLineSegment(sketch, "E2780", {"start": v(-54.66, -43.49) * mm, "end": v(-54.87, -43.54) * mm});
            skLineSegment(sketch, "E2781", {"start": v(-54.87, -43.54) * mm, "end": v(-55.09, -43.6) * mm});
            skLineSegment(sketch, "E2782", {"start": v(-55.09, -43.6) * mm, "end": v(-55.31, -43.63) * mm});
            skLineSegment(sketch, "E2783", {"start": v(-55.31, -43.63) * mm, "end": v(-55.54, -43.67) * mm});
            skLineSegment(sketch, "E2784", {"start": v(-55.54, -43.67) * mm, "end": v(-55.78, -43.7) * mm});
            skLineSegment(sketch, "E2785", {"start": v(-55.78, -43.7) * mm, "end": v(-56.02, -43.71) * mm});
            skLineSegment(sketch, "E2786", {"start": v(-56.02, -43.71) * mm, "end": v(-56.27, -43.72) * mm});
            skLineSegment(sketch, "E2787", {"start": v(-56.27, -43.72) * mm, "end": v(-56.53, -43.73) * mm});
            skLineSegment(sketch, "E2788", {"start": v(-56.53, -43.73) * mm, "end": v(-56.74, -43.73) * mm});
            skLineSegment(sketch, "E2789", {"start": v(-56.74, -43.73) * mm, "end": v(-56.95, -43.73) * mm});
            skLineSegment(sketch, "E2790", {"start": v(-56.95, -43.73) * mm, "end": v(-57.17, -43.73) * mm});
            skLineSegment(sketch, "E2791", {"start": v(-57.17, -43.73) * mm, "end": v(-57.38, -43.73) * mm});
            skLineSegment(sketch, "E2792", {"start": v(-57.38, -43.73) * mm, "end": v(-57.6, -43.73) * mm});
            skLineSegment(sketch, "E2793", {"start": v(-57.6, -43.73) * mm, "end": v(-57.8, -43.73) * mm});
            skLineSegment(sketch, "E2794", {"start": v(-57.8, -43.73) * mm, "end": v(-58.02, -43.73) * mm});
            skLineSegment(sketch, "E2795", {"start": v(-58.02, -43.73) * mm, "end": v(-58.23, -43.73) * mm});
            skLineSegment(sketch, "E2796", {"start": v(-58.23, -43.73) * mm, "end": v(-58.45, -43.73) * mm});
            skLineSegment(sketch, "E2797", {"start": v(-58.45, -43.73) * mm, "end": v(-58.66, -43.73) * mm});
            skLineSegment(sketch, "E2798", {"start": v(-58.66, -43.73) * mm, "end": v(-58.87, -43.73) * mm});
            skLineSegment(sketch, "E2799", {"start": v(-58.87, -43.73) * mm, "end": v(-59.09, -43.73) * mm});
            skLineSegment(sketch, "E2800", {"start": v(-59.09, -43.73) * mm, "end": v(-59.3, -43.73) * mm});
            skLineSegment(sketch, "E2801", {"start": v(-59.3, -43.73) * mm, "end": v(-59.51, -43.73) * mm});
            skLineSegment(sketch, "E2802", {"start": v(-59.51, -43.73) * mm, "end": v(-59.72, -43.73) * mm});
            skLineSegment(sketch, "E2803", {"start": v(-59.72, -43.73) * mm, "end": v(-59.94, -43.73) * mm});
            skLineSegment(sketch, "E2804", {"start": v(-59.94, -43.73) * mm, "end": v(-59.94, -43.3) * mm});
            skLineSegment(sketch, "E2805", {"start": v(-59.94, -43.3) * mm, "end": v(-59.94, -42.86) * mm});
            skLineSegment(sketch, "E2806", {"start": v(-59.94, -42.86) * mm, "end": v(-59.94, -42.42) * mm});
            skLineSegment(sketch, "E2807", {"start": v(-59.94, -42.42) * mm, "end": v(-59.94, -42) * mm});
            skLineSegment(sketch, "E2808", {"start": v(-59.94, -42) * mm, "end": v(-59.94, -41.56) * mm});
            skLineSegment(sketch, "E2809", {"start": v(-59.94, -41.56) * mm, "end": v(-59.94, -41.12) * mm});
            skLineSegment(sketch, "E2810", {"start": v(-59.94, -41.12) * mm, "end": v(-59.94, -40.69) * mm});
            skLineSegment(sketch, "E2811", {"start": v(-59.94, -40.69) * mm, "end": v(-59.94, -40.26) * mm});
            skLineSegment(sketch, "E2812", {"start": v(-59.94, -40.26) * mm, "end": v(-59.94, -39.82) * mm});
            skLineSegment(sketch, "E2813", {"start": v(-59.94, -39.82) * mm, "end": v(-59.94, -39.39) * mm});
            skLineSegment(sketch, "E2814", {"start": v(-59.94, -39.39) * mm, "end": v(-59.94, -38.95) * mm});
            skLineSegment(sketch, "E2815", {"start": v(-59.94, -38.95) * mm, "end": v(-59.94, -38.52) * mm});
            skLineSegment(sketch, "E2816", {"start": v(-59.94, -38.52) * mm, "end": v(-59.94, -38.09) * mm});
            skLineSegment(sketch, "E2817", {"start": v(-59.94, -38.09) * mm, "end": v(-59.94, -37.65) * mm});
            skLineSegment(sketch, "E2818", {"start": v(-59.94, -37.65) * mm, "end": v(-59.94, -37.22) * mm});
            skLineSegment(sketch, "E2819", {"start": v(-59.94, -37.22) * mm, "end": v(-59.94, -36.79) * mm});
            skLineSegment(sketch, "E2820", {"start": v(-59.94, -36.79) * mm, "end": v(-59.69, -36.79) * mm});
            skLineSegment(sketch, "E2821", {"start": v(-59.69, -36.79) * mm, "end": v(-59.43, -36.79) * mm});
            skLineSegment(sketch, "E2822", {"start": v(-59.43, -36.79) * mm, "end": v(-59.18, -36.79) * mm});
            skLineSegment(sketch, "E2823", {"start": v(-59.18, -36.79) * mm, "end": v(-58.93, -36.79) * mm});
            skLineSegment(sketch, "E2824", {"start": v(-58.93, -36.79) * mm, "end": v(-58.68, -36.79) * mm});
            skLineSegment(sketch, "E2825", {"start": v(-58.68, -36.79) * mm, "end": v(-58.43, -36.79) * mm});
            skLineSegment(sketch, "E2826", {"start": v(-58.43, -36.79) * mm, "end": v(-58.18, -36.79) * mm});
            skLineSegment(sketch, "E2827", {"start": v(-58.18, -36.79) * mm, "end": v(-57.92, -36.79) * mm});
            skLineSegment(sketch, "E2828", {"start": v(-57.92, -36.79) * mm, "end": v(-57.67, -36.79) * mm});
            skLineSegment(sketch, "E2829", {"start": v(-57.67, -36.79) * mm, "end": v(-57.42, -36.79) * mm});
            skLineSegment(sketch, "E2830", {"start": v(-57.42, -36.79) * mm, "end": v(-57.17, -36.79) * mm});
            skLineSegment(sketch, "E2831", {"start": v(-57.17, -36.79) * mm, "end": v(-56.92, -36.79) * mm});
            skLineSegment(sketch, "E2832", {"start": v(-56.92, -36.79) * mm, "end": v(-56.67, -36.79) * mm});
            skLineSegment(sketch, "E2833", {"start": v(-56.67, -36.79) * mm, "end": v(-56.41, -36.79) * mm});
            skLineSegment(sketch, "E2834", {"start": v(-56.41, -36.79) * mm, "end": v(-56.16, -36.79) * mm});
            skLineSegment(sketch, "E2835", {"start": v(-56.16, -36.79) * mm, "end": v(-55.91, -36.79) * mm});
            skLineSegment(sketch, "E2836", {"start": v(-55.91, -36.79) * mm, "end": v(-55.7, -36.79) * mm});
            skLineSegment(sketch, "E2837", {"start": v(-55.7, -36.79) * mm, "end": v(-55.48, -36.8) * mm});
            skLineSegment(sketch, "E2838", {"start": v(-55.48, -36.8) * mm, "end": v(-55.28, -36.82) * mm});
            skLineSegment(sketch, "E2839", {"start": v(-55.28, -36.82) * mm, "end": v(-55.08, -36.85) * mm});
            skLineSegment(sketch, "E2840", {"start": v(-55.08, -36.85) * mm, "end": v(-54.88, -36.88) * mm});
            skLineSegment(sketch, "E2841", {"start": v(-54.88, -36.88) * mm, "end": v(-54.7, -36.92) * mm});
            skLineSegment(sketch, "E2842", {"start": v(-54.7, -36.92) * mm, "end": v(-54.5, -36.97) * mm});
            skLineSegment(sketch, "E2843", {"start": v(-54.5, -36.97) * mm, "end": v(-54.33, -37.02) * mm});
            skLineSegment(sketch, "E2844", {"start": v(-54.33, -37.02) * mm, "end": v(-54.16, -37.09) * mm});
            skLineSegment(sketch, "E2845", {"start": v(-54.16, -37.09) * mm, "end": v(-53.99, -37.16) * mm});
            skLineSegment(sketch, "E2846", {"start": v(-53.99, -37.16) * mm, "end": v(-53.83, -37.23) * mm});
            skLineSegment(sketch, "E2847", {"start": v(-53.83, -37.23) * mm, "end": v(-53.67, -37.32) * mm});
            skLineSegment(sketch, "E2848", {"start": v(-53.67, -37.32) * mm, "end": v(-53.52, -37.41) * mm});
            skLineSegment(sketch, "E2849", {"start": v(-53.52, -37.41) * mm, "end": v(-53.37, -37.51) * mm});
            skLineSegment(sketch, "E2850", {"start": v(-53.37, -37.51) * mm, "end": v(-53.23, -37.62) * mm});
            skLineSegment(sketch, "E2851", {"start": v(-53.23, -37.62) * mm, "end": v(-53.1, -37.73) * mm});
            skLineSegment(sketch, "E2852", {"start": v(-53.1, -37.73) * mm, "end": v(-52.96, -37.85) * mm});
            skLineSegment(sketch, "E2853", {"start": v(-52.96, -37.85) * mm, "end": v(-52.84, -37.98) * mm});
            skLineSegment(sketch, "E2854", {"start": v(-52.84, -37.98) * mm, "end": v(-52.73, -38.1) * mm});
            skLineSegment(sketch, "E2855", {"start": v(-52.73, -38.1) * mm, "end": v(-52.63, -38.24) * mm});
            skLineSegment(sketch, "E2856", {"start": v(-52.63, -38.24) * mm, "end": v(-52.53, -38.38) * mm});
            skLineSegment(sketch, "E2857", {"start": v(-52.53, -38.38) * mm, "end": v(-52.44, -38.52) * mm});
            skLineSegment(sketch, "E2858", {"start": v(-52.44, -38.52) * mm, "end": v(-52.36, -38.66) * mm});
            skLineSegment(sketch, "E2859", {"start": v(-52.36, -38.66) * mm, "end": v(-52.3, -38.81) * mm});
            skLineSegment(sketch, "E2860", {"start": v(-52.3, -38.81) * mm, "end": v(-52.23, -38.96) * mm});
            skLineSegment(sketch, "E2861", {"start": v(-52.23, -38.96) * mm, "end": v(-52.18, -39.12) * mm});
            skLineSegment(sketch, "E2862", {"start": v(-52.18, -39.12) * mm, "end": v(-52.13, -39.28) * mm});
            skLineSegment(sketch, "E2863", {"start": v(-52.13, -39.28) * mm, "end": v(-52.1, -39.45) * mm});
            skLineSegment(sketch, "E2864", {"start": v(-52.1, -39.45) * mm, "end": v(-52.06, -39.62) * mm});
            skLineSegment(sketch, "E2865", {"start": v(-52.06, -39.62) * mm, "end": v(-52.04, -39.8) * mm});
            skLineSegment(sketch, "E2866", {"start": v(-52.04, -39.8) * mm, "end": v(-52.03, -39.97) * mm});
            skLineSegment(sketch, "E2867", {"start": v(-52.03, -39.97) * mm, "end": v(-52.03, -40.15) * mm});
            skLineSegment(sketch, "E2868", {"start": v(-52.03, -40.15) * mm, "end": v(-52.03, -40.35) * mm});
            skLineSegment(sketch, "E2869", {"start": v(-45.65, -33.5) * mm, "end": v(-45.9, -33.37) * mm});
            skLineSegment(sketch, "E2870", {"start": v(-45.9, -33.37) * mm, "end": v(-46.15, -33.25) * mm});
            skLineSegment(sketch, "E2871", {"start": v(-46.15, -33.25) * mm, "end": v(-46.4, -33.13) * mm});
            skLineSegment(sketch, "E2872", {"start": v(-46.4, -33.13) * mm, "end": v(-46.67, -33.03) * mm});
            skLineSegment(sketch, "E2873", {"start": v(-46.67, -33.03) * mm, "end": v(-46.93, -32.93) * mm});
            skLineSegment(sketch, "E2874", {"start": v(-46.93, -32.93) * mm, "end": v(-47.2, -32.83) * mm});
            skLineSegment(sketch, "E2875", {"start": v(-47.2, -32.83) * mm, "end": v(-47.47, -32.75) * mm});
            skLineSegment(sketch, "E2876", {"start": v(-47.47, -32.75) * mm, "end": v(-47.75, -32.67) * mm});
            skLineSegment(sketch, "E2877", {"start": v(-47.75, -32.67) * mm, "end": v(-48.03, -32.6) * mm});
            skLineSegment(sketch, "E2878", {"start": v(-48.03, -32.6) * mm, "end": v(-48.32, -32.53) * mm});
            skLineSegment(sketch, "E2879", {"start": v(-48.32, -32.53) * mm, "end": v(-48.6, -32.47) * mm});
            skLineSegment(sketch, "E2880", {"start": v(-48.6, -32.47) * mm, "end": v(-48.9, -32.42) * mm});
            skLineSegment(sketch, "E2881", {"start": v(-48.9, -32.42) * mm, "end": v(-49.2, -32.37) * mm});
            skLineSegment(sketch, "E2882", {"start": v(-49.2, -32.37) * mm, "end": v(-49.5, -32.33) * mm});
            skLineSegment(sketch, "E2883", {"start": v(-49.5, -32.33) * mm, "end": v(-49.5, -32.33) * mm});
            skLineSegment(sketch, "E2884", {"start": v(-49.5, -32.33) * mm, "end": v(-49.5, -32.32) * mm});
            skLineSegment(sketch, "E2885", {"start": v(-49.5, -32.32) * mm, "end": v(-49.5, -32.32) * mm});
            skLineSegment(sketch, "E2886", {"start": v(-49.5, -32.32) * mm, "end": v(-49.5, -32.3) * mm});
            skLineSegment(sketch, "E2887", {"start": v(-49.5, -32.3) * mm, "end": v(-49.5, -32.3) * mm});
            skLineSegment(sketch, "E2888", {"start": v(-49.5, -32.3) * mm, "end": v(-49.5, -32.29) * mm});
            skLineSegment(sketch, "E2889", {"start": v(-49.5, -32.29) * mm, "end": v(-49.5, -32.28) * mm});
            skLineSegment(sketch, "E2890", {"start": v(-49.5, -32.28) * mm, "end": v(-49.5, -32.27) * mm});
            skLineSegment(sketch, "E2891", {"start": v(-49.5, -32.27) * mm, "end": v(-49.5, -32.27) * mm});
            skLineSegment(sketch, "E2892", {"start": v(-49.5, -32.27) * mm, "end": v(-49.5, -32.26) * mm});
            skLineSegment(sketch, "E2893", {"start": v(-49.5, -32.26) * mm, "end": v(-49.5, -32.26) * mm});
            skLineSegment(sketch, "E2894", {"start": v(-49.5, -32.26) * mm, "end": v(-49.5, -32.25) * mm});
            skLineSegment(sketch, "E2895", {"start": v(-49.5, -32.25) * mm, "end": v(-49.5, -32.24) * mm});
            skLineSegment(sketch, "E2896", {"start": v(-49.5, -32.24) * mm, "end": v(-49.5, -32.24) * mm});
            skLineSegment(sketch, "E2897", {"start": v(-49.5, -32.24) * mm, "end": v(-49.23, -32.19) * mm});
            skLineSegment(sketch, "E2898", {"start": v(-49.23, -32.19) * mm, "end": v(-48.98, -32.13) * mm});
            skLineSegment(sketch, "E2899", {"start": v(-48.98, -32.13) * mm, "end": v(-48.72, -32.06) * mm});
            skLineSegment(sketch, "E2900", {"start": v(-48.72, -32.06) * mm, "end": v(-48.47, -32) * mm});
            skLineSegment(sketch, "E2901", {"start": v(-48.47, -32) * mm, "end": v(-48.22, -31.92) * mm});
            skLineSegment(sketch, "E2902", {"start": v(-48.22, -31.92) * mm, "end": v(-47.98, -31.84) * mm});
            skLineSegment(sketch, "E2903", {"start": v(-47.98, -31.84) * mm, "end": v(-47.73, -31.75) * mm});
            skLineSegment(sketch, "E2904", {"start": v(-47.73, -31.75) * mm, "end": v(-47.5, -31.66) * mm});
            skLineSegment(sketch, "E2905", {"start": v(-47.5, -31.66) * mm, "end": v(-47.26, -31.56) * mm});
            skLineSegment(sketch, "E2906", {"start": v(-47.26, -31.56) * mm, "end": v(-47.02, -31.46) * mm});
            skLineSegment(sketch, "E2907", {"start": v(-47.02, -31.46) * mm, "end": v(-46.79, -31.35) * mm});
            skLineSegment(sketch, "E2908", {"start": v(-46.79, -31.35) * mm, "end": v(-46.56, -31.23) * mm});
            skLineSegment(sketch, "E2909", {"start": v(-46.56, -31.23) * mm, "end": v(-46.33, -31.12) * mm});
            skLineSegment(sketch, "E2910", {"start": v(-46.33, -31.12) * mm, "end": v(-46.1, -30.99) * mm});
            skLineSegment(sketch, "E2911", {"start": v(-46.1, -30.99) * mm, "end": v(-45.89, -30.86) * mm});
            skLineSegment(sketch, "E2912", {"start": v(-45.89, -30.86) * mm, "end": v(-45.67, -30.72) * mm});
            skLineSegment(sketch, "E2913", {"start": v(-45.67, -30.72) * mm, "end": v(-45.45, -30.58) * mm});
            skLineSegment(sketch, "E2914", {"start": v(-45.45, -30.58) * mm, "end": v(-45.25, -30.44) * mm});
            skLineSegment(sketch, "E2915", {"start": v(-45.25, -30.44) * mm, "end": v(-45.05, -30.3) * mm});
            skLineSegment(sketch, "E2916", {"start": v(-45.05, -30.3) * mm, "end": v(-45.02, -30.27) * mm});
            skLineSegment(sketch, "E2917", {"start": v(-45.02, -30.27) * mm, "end": v(-45.03, -30.34) * mm});
            skLineSegment(sketch, "E2918", {"start": v(-45.03, -30.34) * mm, "end": v(-45.13, -30.95) * mm});
            skLineSegment(sketch, "E2919", {"start": v(-45.13, -30.95) * mm, "end": v(-45.2, -31.56) * mm});
            skLineSegment(sketch, "E2920", {"start": v(-45.2, -31.56) * mm, "end": v(-45.26, -32.18) * mm});
            skLineSegment(sketch, "E2921", {"start": v(-45.26, -32.18) * mm, "end": v(-45.3, -32.8) * mm});
            skLineSegment(sketch, "E2922", {"start": v(-45.3, -32.8) * mm, "end": v(-45.33, -33.44) * mm});
            skLineSegment(sketch, "E2923", {"start": v(-45.33, -33.44) * mm, "end": v(-45.34, -33.66) * mm});
            skLineSegment(sketch, "E2924", {"start": v(-45.34, -33.66) * mm, "end": v(-45.4, -33.63) * mm});
            skLineSegment(sketch, "E2925", {"start": v(-45.4, -33.63) * mm, "end": v(-45.65, -33.5) * mm});
            skLineSegment(sketch, "E2926", {"start": v(-22, -34.16) * mm, "end": v(-22, -34.48) * mm});
            skLineSegment(sketch, "E2927", {"start": v(-22, -34.48) * mm, "end": v(-22.02, -34.8) * mm});
            skLineSegment(sketch, "E2928", {"start": v(-22.02, -34.8) * mm, "end": v(-22.04, -35.12) * mm});
            skLineSegment(sketch, "E2929", {"start": v(-22.04, -35.12) * mm, "end": v(-22.06, -35.43) * mm});
            skLineSegment(sketch, "E2930", {"start": v(-22.06, -35.43) * mm, "end": v(-22.1, -35.73) * mm});
            skLineSegment(sketch, "E2931", {"start": v(-22.1, -35.73) * mm, "end": v(-22.14, -36.03) * mm});
            skLineSegment(sketch, "E2932", {"start": v(-22.14, -36.03) * mm, "end": v(-22.18, -36.32) * mm});
            skLineSegment(sketch, "E2933", {"start": v(-22.18, -36.32) * mm, "end": v(-22.24, -36.6) * mm});
            skLineSegment(sketch, "E2934", {"start": v(-22.24, -36.6) * mm, "end": v(-22.3, -36.88) * mm});
            skLineSegment(sketch, "E2935", {"start": v(-22.3, -36.88) * mm, "end": v(-22.36, -37.16) * mm});
            skLineSegment(sketch, "E2936", {"start": v(-22.36, -37.16) * mm, "end": v(-22.43, -37.43) * mm});
            skLineSegment(sketch, "E2937", {"start": v(-22.43, -37.43) * mm, "end": v(-22.5, -37.69) * mm});
            skLineSegment(sketch, "E2938", {"start": v(-22.5, -37.69) * mm, "end": v(-22.59, -37.95) * mm});
            skLineSegment(sketch, "E2939", {"start": v(-22.59, -37.95) * mm, "end": v(-22.67, -38.2) * mm});
            skLineSegment(sketch, "E2940", {"start": v(-22.67, -38.2) * mm, "end": v(-22.77, -38.44) * mm});
            skLineSegment(sketch, "E2941", {"start": v(-22.77, -38.44) * mm, "end": v(-22.87, -38.68) * mm});
            skLineSegment(sketch, "E2942", {"start": v(-22.87, -38.68) * mm, "end": v(-22.97, -38.92) * mm});
            skLineSegment(sketch, "E2943", {"start": v(-22.97, -38.92) * mm, "end": v(-23.08, -39.14) * mm});
            skLineSegment(sketch, "E2944", {"start": v(-23.08, -39.14) * mm, "end": v(-23.2, -39.36) * mm});
            skLineSegment(sketch, "E2945", {"start": v(-23.2, -39.36) * mm, "end": v(-23.32, -39.57) * mm});
            skLineSegment(sketch, "E2946", {"start": v(-23.32, -39.57) * mm, "end": v(-23.45, -39.77) * mm});
            skLineSegment(sketch, "E2947", {"start": v(-23.45, -39.77) * mm, "end": v(-23.58, -39.97) * mm});
            skLineSegment(sketch, "E2948", {"start": v(-23.58, -39.97) * mm, "end": v(-23.71, -40.16) * mm});
            skLineSegment(sketch, "E2949", {"start": v(-23.71, -40.16) * mm, "end": v(-23.85, -40.34) * mm});
            skLineSegment(sketch, "E2950", {"start": v(-23.85, -40.34) * mm, "end": v(-24, -40.52) * mm});
            skLineSegment(sketch, "E2951", {"start": v(-24, -40.52) * mm, "end": v(-24.15, -40.69) * mm});
            skLineSegment(sketch, "E2952", {"start": v(-24.15, -40.69) * mm, "end": v(-24.3, -40.85) * mm});
            skLineSegment(sketch, "E2953", {"start": v(-24.3, -40.85) * mm, "end": v(-24.46, -41) * mm});
            skLineSegment(sketch, "E2954", {"start": v(-24.46, -41) * mm, "end": v(-24.63, -41.15) * mm});
            skLineSegment(sketch, "E2955", {"start": v(-24.63, -41.15) * mm, "end": v(-24.8, -41.3) * mm});
            skLineSegment(sketch, "E2956", {"start": v(-24.8, -41.3) * mm, "end": v(-24.97, -41.43) * mm});
            skLineSegment(sketch, "E2957", {"start": v(-24.97, -41.43) * mm, "end": v(-25.15, -41.55) * mm});
            skLineSegment(sketch, "E2958", {"start": v(-25.15, -41.55) * mm, "end": v(-25.33, -41.67) * mm});
            skLineSegment(sketch, "E2959", {"start": v(-25.33, -41.67) * mm, "end": v(-25.52, -41.78) * mm});
            skLineSegment(sketch, "E2960", {"start": v(-25.52, -41.78) * mm, "end": v(-25.7, -41.88) * mm});
            skLineSegment(sketch, "E2961", {"start": v(-25.7, -41.88) * mm, "end": v(-25.9, -41.98) * mm});
            skLineSegment(sketch, "E2962", {"start": v(-25.9, -41.98) * mm, "end": v(-26.09, -42.06) * mm});
            skLineSegment(sketch, "E2963", {"start": v(-26.09, -42.06) * mm, "end": v(-26.28, -42.14) * mm});
            skLineSegment(sketch, "E2964", {"start": v(-26.28, -42.14) * mm, "end": v(-26.48, -42.21) * mm});
            skLineSegment(sketch, "E2965", {"start": v(-26.48, -42.21) * mm, "end": v(-26.68, -42.27) * mm});
            skLineSegment(sketch, "E2966", {"start": v(-26.68, -42.27) * mm, "end": v(-26.89, -42.32) * mm});
            skLineSegment(sketch, "E2967", {"start": v(-26.89, -42.32) * mm, "end": v(-27.1, -42.37) * mm});
            skLineSegment(sketch, "E2968", {"start": v(-27.1, -42.37) * mm, "end": v(-27.3, -42.4) * mm});
            skLineSegment(sketch, "E2969", {"start": v(-27.3, -42.4) * mm, "end": v(-27.52, -42.43) * mm});
            skLineSegment(sketch, "E2970", {"start": v(-27.52, -42.43) * mm, "end": v(-27.73, -42.45) * mm});
            skLineSegment(sketch, "E2971", {"start": v(-27.73, -42.45) * mm, "end": v(-27.95, -42.47) * mm});
            skLineSegment(sketch, "E2972", {"start": v(-27.95, -42.47) * mm, "end": v(-28.17, -42.47) * mm});
            skLineSegment(sketch, "E2973", {"start": v(-28.17, -42.47) * mm, "end": v(-28.53, -42.46) * mm});
            skLineSegment(sketch, "E2974", {"start": v(-28.53, -42.46) * mm, "end": v(-28.88, -42.43) * mm});
            skLineSegment(sketch, "E2975", {"start": v(-28.88, -42.43) * mm, "end": v(-29.22, -42.39) * mm});
            skLineSegment(sketch, "E2976", {"start": v(-29.22, -42.39) * mm, "end": v(-29.55, -42.33) * mm});
            skLineSegment(sketch, "E2977", {"start": v(-29.55, -42.33) * mm, "end": v(-29.87, -42.24) * mm});
            skLineSegment(sketch, "E2978", {"start": v(-29.87, -42.24) * mm, "end": v(-30.18, -42.14) * mm});
            skLineSegment(sketch, "E2979", {"start": v(-30.18, -42.14) * mm, "end": v(-30.49, -42.03) * mm});
            skLineSegment(sketch, "E2980", {"start": v(-30.49, -42.03) * mm, "end": v(-30.78, -41.9) * mm});
            skLineSegment(sketch, "E2981", {"start": v(-30.78, -41.9) * mm, "end": v(-31.06, -41.74) * mm});
            skLineSegment(sketch, "E2982", {"start": v(-31.06, -41.74) * mm, "end": v(-31.33, -41.56) * mm});
            skLineSegment(sketch, "E2983", {"start": v(-31.33, -41.56) * mm, "end": v(-31.6, -41.37) * mm});
            skLineSegment(sketch, "E2984", {"start": v(-31.6, -41.37) * mm, "end": v(-31.85, -41.16) * mm});
            skLineSegment(sketch, "E2985", {"start": v(-31.85, -41.16) * mm, "end": v(-32.1, -40.94) * mm});
            skLineSegment(sketch, "E2986", {"start": v(-32.1, -40.94) * mm, "end": v(-32.33, -40.7) * mm});
            skLineSegment(sketch, "E2987", {"start": v(-32.33, -40.7) * mm, "end": v(-32.56, -40.43) * mm});
            skLineSegment(sketch, "E2988", {"start": v(-32.56, -40.43) * mm, "end": v(-32.78, -40.15) * mm});
            skLineSegment(sketch, "E2989", {"start": v(-32.78, -40.15) * mm, "end": v(-32.98, -39.85) * mm});
            skLineSegment(sketch, "E2990", {"start": v(-32.98, -39.85) * mm, "end": v(-33.17, -39.54) * mm});
            skLineSegment(sketch, "E2991", {"start": v(-33.17, -39.54) * mm, "end": v(-33.35, -39.21) * mm});
            skLineSegment(sketch, "E2992", {"start": v(-33.35, -39.21) * mm, "end": v(-33.52, -38.87) * mm});
            skLineSegment(sketch, "E2993", {"start": v(-33.52, -38.87) * mm, "end": v(-33.67, -38.52) * mm});
            skLineSegment(sketch, "E2994", {"start": v(-33.67, -38.52) * mm, "end": v(-33.8, -38.15) * mm});
            skLineSegment(sketch, "E2995", {"start": v(-33.8, -38.15) * mm, "end": v(-33.93, -37.77) * mm});
            skLineSegment(sketch, "E2996", {"start": v(-33.93, -37.77) * mm, "end": v(-34.05, -37.37) * mm});
            skLineSegment(sketch, "E2997", {"start": v(-34.05, -37.37) * mm, "end": v(-34.15, -36.96) * mm});
            skLineSegment(sketch, "E2998", {"start": v(-34.15, -36.96) * mm, "end": v(-34.23, -36.54) * mm});
            skLineSegment(sketch, "E2999", {"start": v(-34.23, -36.54) * mm, "end": v(-34.3, -36.1) * mm});
            skLineSegment(sketch, "E3000", {"start": v(-34.3, -36.1) * mm, "end": v(-34.36, -35.64) * mm});
            skLineSegment(sketch, "E3001", {"start": v(-34.36, -35.64) * mm, "end": v(-34.41, -35.17) * mm});
            skLineSegment(sketch, "E3002", {"start": v(-34.41, -35.17) * mm, "end": v(-34.44, -34.7) * mm});
            skLineSegment(sketch, "E3003", {"start": v(-34.44, -34.7) * mm, "end": v(-34.46, -34.2) * mm});
            skLineSegment(sketch, "E3004", {"start": v(-34.46, -34.2) * mm, "end": v(-34.47, -33.68) * mm});
            skLineSegment(sketch, "E3005", {"start": v(-34.47, -33.68) * mm, "end": v(-34.46, -33.16) * mm});
            skLineSegment(sketch, "E3006", {"start": v(-34.46, -33.16) * mm, "end": v(-34.44, -32.65) * mm});
            skLineSegment(sketch, "E3007", {"start": v(-34.44, -32.65) * mm, "end": v(-34.4, -32.16) * mm});
            skLineSegment(sketch, "E3008", {"start": v(-34.4, -32.16) * mm, "end": v(-34.36, -31.68) * mm});
            skLineSegment(sketch, "E3009", {"start": v(-34.36, -31.68) * mm, "end": v(-34.3, -31.22) * mm});
            skLineSegment(sketch, "E3010", {"start": v(-34.3, -31.22) * mm, "end": v(-34.23, -30.77) * mm});
            skLineSegment(sketch, "E3011", {"start": v(-34.23, -30.77) * mm, "end": v(-34.14, -30.34) * mm});
            skLineSegment(sketch, "E3012", {"start": v(-34.14, -30.34) * mm, "end": v(-34.04, -29.92) * mm});
            skLineSegment(sketch, "E3013", {"start": v(-34.04, -29.92) * mm, "end": v(-33.93, -29.52) * mm});
            skLineSegment(sketch, "E3014", {"start": v(-33.93, -29.52) * mm, "end": v(-33.8, -29.13) * mm});
            skLineSegment(sketch, "E3015", {"start": v(-33.8, -29.13) * mm, "end": v(-33.66, -28.76) * mm});
            skLineSegment(sketch, "E3016", {"start": v(-33.66, -28.76) * mm, "end": v(-33.51, -28.4) * mm});
            skLineSegment(sketch, "E3017", {"start": v(-33.51, -28.4) * mm, "end": v(-33.34, -28.06) * mm});
            skLineSegment(sketch, "E3018", {"start": v(-33.34, -28.06) * mm, "end": v(-33.16, -27.73) * mm});
            skLineSegment(sketch, "E3019", {"start": v(-33.16, -27.73) * mm, "end": v(-32.97, -27.42) * mm});
            skLineSegment(sketch, "E3020", {"start": v(-32.97, -27.42) * mm, "end": v(-32.76, -27.12) * mm});
            skLineSegment(sketch, "E3021", {"start": v(-32.76, -27.12) * mm, "end": v(-32.55, -26.84) * mm});
            skLineSegment(sketch, "E3022", {"start": v(-32.55, -26.84) * mm, "end": v(-32.32, -26.58) * mm});
            skLineSegment(sketch, "E3023", {"start": v(-32.32, -26.58) * mm, "end": v(-32.08, -26.33) * mm});
            skLineSegment(sketch, "E3024", {"start": v(-32.08, -26.33) * mm, "end": v(-31.83, -26.1) * mm});
            skLineSegment(sketch, "E3025", {"start": v(-31.83, -26.1) * mm, "end": v(-31.57, -25.9) * mm});
            skLineSegment(sketch, "E3026", {"start": v(-31.57, -25.9) * mm, "end": v(-31.3, -25.7) * mm});
            skLineSegment(sketch, "E3027", {"start": v(-31.3, -25.7) * mm, "end": v(-31.01, -25.54) * mm});
            skLineSegment(sketch, "E3028", {"start": v(-31.01, -25.54) * mm, "end": v(-30.72, -25.38) * mm});
            skLineSegment(sketch, "E3029", {"start": v(-30.72, -25.38) * mm, "end": v(-30.42, -25.25) * mm});
            skLineSegment(sketch, "E3030", {"start": v(-30.42, -25.25) * mm, "end": v(-30.1, -25.13) * mm});
            skLineSegment(sketch, "E3031", {"start": v(-30.1, -25.13) * mm, "end": v(-29.78, -25.03) * mm});
            skLineSegment(sketch, "E3032", {"start": v(-29.78, -25.03) * mm, "end": v(-29.45, -24.95) * mm});
            skLineSegment(sketch, "E3033", {"start": v(-29.45, -24.95) * mm, "end": v(-29.1, -24.88) * mm});
            skLineSegment(sketch, "E3034", {"start": v(-29.1, -24.88) * mm, "end": v(-28.75, -24.84) * mm});
            skLineSegment(sketch, "E3035", {"start": v(-28.75, -24.84) * mm, "end": v(-28.38, -24.81) * mm});
            skLineSegment(sketch, "E3036", {"start": v(-28.38, -24.81) * mm, "end": v(-28, -24.8) * mm});
            skLineSegment(sketch, "E3037", {"start": v(-28, -24.8) * mm, "end": v(-27.66, -24.81) * mm});
            skLineSegment(sketch, "E3038", {"start": v(-27.66, -24.81) * mm, "end": v(-27.32, -24.84) * mm});
            skLineSegment(sketch, "E3039", {"start": v(-27.32, -24.84) * mm, "end": v(-27, -24.89) * mm});
            skLineSegment(sketch, "E3040", {"start": v(-27, -24.89) * mm, "end": v(-26.68, -24.95) * mm});
            skLineSegment(sketch, "E3041", {"start": v(-26.68, -24.95) * mm, "end": v(-26.37, -25.04) * mm});
            skLineSegment(sketch, "E3042", {"start": v(-26.37, -25.04) * mm, "end": v(-26.07, -25.14) * mm});
            skLineSegment(sketch, "E3043", {"start": v(-26.07, -25.14) * mm, "end": v(-25.79, -25.26) * mm});
            skLineSegment(sketch, "E3044", {"start": v(-25.79, -25.26) * mm, "end": v(-25.5, -25.4) * mm});
            skLineSegment(sketch, "E3045", {"start": v(-25.5, -25.4) * mm, "end": v(-25.23, -25.57) * mm});
            skLineSegment(sketch, "E3046", {"start": v(-25.23, -25.57) * mm, "end": v(-24.97, -25.75) * mm});
            skLineSegment(sketch, "E3047", {"start": v(-24.97, -25.75) * mm, "end": v(-24.72, -25.94) * mm});
            skLineSegment(sketch, "E3048", {"start": v(-24.72, -25.94) * mm, "end": v(-24.48, -26.16) * mm});
            skLineSegment(sketch, "E3049", {"start": v(-24.48, -26.16) * mm, "end": v(-24.24, -26.4) * mm});
            skLineSegment(sketch, "E3050", {"start": v(-24.24, -26.4) * mm, "end": v(-24.02, -26.65) * mm});
            skLineSegment(sketch, "E3051", {"start": v(-24.02, -26.65) * mm, "end": v(-23.8, -26.92) * mm});
            skLineSegment(sketch, "E3052", {"start": v(-23.8, -26.92) * mm, "end": v(-23.6, -27.22) * mm});
            skLineSegment(sketch, "E3053", {"start": v(-23.6, -27.22) * mm, "end": v(-23.4, -27.53) * mm});
            skLineSegment(sketch, "E3054", {"start": v(-23.4, -27.53) * mm, "end": v(-23.22, -27.85) * mm});
            skLineSegment(sketch, "E3055", {"start": v(-23.22, -27.85) * mm, "end": v(-23.05, -28.19) * mm});
            skLineSegment(sketch, "E3056", {"start": v(-23.05, -28.19) * mm, "end": v(-22.9, -28.54) * mm});
            skLineSegment(sketch, "E3057", {"start": v(-22.9, -28.54) * mm, "end": v(-22.75, -28.9) * mm});
            skLineSegment(sketch, "E3058", {"start": v(-22.75, -28.9) * mm, "end": v(-22.62, -29.28) * mm});
            skLineSegment(sketch, "E3059", {"start": v(-22.62, -29.28) * mm, "end": v(-22.5, -29.67) * mm});
            skLineSegment(sketch, "E3060", {"start": v(-22.5, -29.67) * mm, "end": v(-22.4, -30.08) * mm});
            skLineSegment(sketch, "E3061", {"start": v(-22.4, -30.08) * mm, "end": v(-22.3, -30.5) * mm});
            skLineSegment(sketch, "E3062", {"start": v(-22.3, -30.5) * mm, "end": v(-22.21, -30.93) * mm});
            skLineSegment(sketch, "E3063", {"start": v(-22.21, -30.93) * mm, "end": v(-22.15, -31.38) * mm});
            skLineSegment(sketch, "E3064", {"start": v(-22.15, -31.38) * mm, "end": v(-22.09, -31.84) * mm});
            skLineSegment(sketch, "E3065", {"start": v(-22.09, -31.84) * mm, "end": v(-22.04, -32.32) * mm});
            skLineSegment(sketch, "E3066", {"start": v(-22.04, -32.32) * mm, "end": v(-22.01, -32.8) * mm});
            skLineSegment(sketch, "E3067", {"start": v(-22.01, -32.8) * mm, "end": v(-22, -33.3) * mm});
            skLineSegment(sketch, "E3068", {"start": v(-22, -33.3) * mm, "end": v(-21.99, -33.83) * mm});
            skLineSegment(sketch, "E3069", {"start": v(-21.99, -33.83) * mm, "end": v(-22, -34.16) * mm});
            skLineSegment(sketch, "E3070", {"start": v(-12.74, -25.45) * mm, "end": v(-12.98, -24.94) * mm});
            skLineSegment(sketch, "E3071", {"start": v(-12.98, -24.94) * mm, "end": v(-13.24, -24.43) * mm});
            skLineSegment(sketch, "E3072", {"start": v(-13.24, -24.43) * mm, "end": v(-13.5, -23.94) * mm});
            skLineSegment(sketch, "E3073", {"start": v(-13.5, -23.94) * mm, "end": v(-13.79, -23.46) * mm});
            skLineSegment(sketch, "E3074", {"start": v(-13.79, -23.46) * mm, "end": v(-14.08, -23) * mm});
            skLineSegment(sketch, "E3075", {"start": v(-14.08, -23) * mm, "end": v(-14.4, -22.54) * mm});
            skLineSegment(sketch, "E3076", {"start": v(-14.4, -22.54) * mm, "end": v(-14.72, -22.1) * mm});
            skLineSegment(sketch, "E3077", {"start": v(-14.72, -22.1) * mm, "end": v(-15.05, -21.68) * mm});
            skLineSegment(sketch, "E3078", {"start": v(-15.05, -21.68) * mm, "end": v(-15.4, -21.28) * mm});
            skLineSegment(sketch, "E3079", {"start": v(-15.4, -21.28) * mm, "end": v(-15.77, -20.88) * mm});
            skLineSegment(sketch, "E3080", {"start": v(-15.77, -20.88) * mm, "end": v(-16.15, -20.5) * mm});
            skLineSegment(sketch, "E3081", {"start": v(-16.15, -20.5) * mm, "end": v(-16.54, -20.14) * mm});
            skLineSegment(sketch, "E3082", {"start": v(-16.54, -20.14) * mm, "end": v(-16.95, -19.79) * mm});
            skLineSegment(sketch, "E3083", {"start": v(-16.95, -19.79) * mm, "end": v(-17.37, -19.45) * mm});
            skLineSegment(sketch, "E3084", {"start": v(-17.37, -19.45) * mm, "end": v(-17.8, -19.13) * mm});
            skLineSegment(sketch, "E3085", {"start": v(-17.8, -19.13) * mm, "end": v(-18.25, -18.82) * mm});
            skLineSegment(sketch, "E3086", {"start": v(-18.25, -18.82) * mm, "end": v(-18.7, -18.53) * mm});
            skLineSegment(sketch, "E3087", {"start": v(-18.7, -18.53) * mm, "end": v(-19.18, -18.25) * mm});
            skLineSegment(sketch, "E3088", {"start": v(-19.18, -18.25) * mm, "end": v(-19.67, -18) * mm});
            skLineSegment(sketch, "E3089", {"start": v(-19.67, -18) * mm, "end": v(-20.16, -17.74) * mm});
            skLineSegment(sketch, "E3090", {"start": v(-20.16, -17.74) * mm, "end": v(-20.66, -17.52) * mm});
            skLineSegment(sketch, "E3091", {"start": v(-20.66, -17.52) * mm, "end": v(-21.17, -17.3) * mm});
            skLineSegment(sketch, "E3092", {"start": v(-21.17, -17.3) * mm, "end": v(-21.69, -17.1) * mm});
            skLineSegment(sketch, "E3093", {"start": v(-21.69, -17.1) * mm, "end": v(-22.21, -16.93) * mm});
            skLineSegment(sketch, "E3094", {"start": v(-22.21, -16.93) * mm, "end": v(-22.75, -16.77) * mm});
            skLineSegment(sketch, "E3095", {"start": v(-22.75, -16.77) * mm, "end": v(-23.29, -16.63) * mm});
            skLineSegment(sketch, "E3096", {"start": v(-23.29, -16.63) * mm, "end": v(-23.84, -16.5) * mm});
            skLineSegment(sketch, "E3097", {"start": v(-23.84, -16.5) * mm, "end": v(-24.4, -16.4) * mm});
            skLineSegment(sketch, "E3098", {"start": v(-24.4, -16.4) * mm, "end": v(-24.96, -16.3) * mm});
            skLineSegment(sketch, "E3099", {"start": v(-24.96, -16.3) * mm, "end": v(-25.53, -16.22) * mm});
            skLineSegment(sketch, "E3100", {"start": v(-25.53, -16.22) * mm, "end": v(-26.12, -16.16) * mm});
            skLineSegment(sketch, "E3101", {"start": v(-26.12, -16.16) * mm, "end": v(-26.7, -16.12) * mm});
            skLineSegment(sketch, "E3102", {"start": v(-26.7, -16.12) * mm, "end": v(-27.3, -16.1) * mm});
            skLineSegment(sketch, "E3103", {"start": v(-27.3, -16.1) * mm, "end": v(-27.9, -16.09) * mm});
            skLineSegment(sketch, "E3104", {"start": v(-27.9, -16.09) * mm, "end": v(-28.54, -16.1) * mm});
            skLineSegment(sketch, "E3105", {"start": v(-28.54, -16.1) * mm, "end": v(-29.16, -16.12) * mm});
            skLineSegment(sketch, "E3106", {"start": v(-29.16, -16.12) * mm, "end": v(-29.77, -16.16) * mm});
            skLineSegment(sketch, "E3107", {"start": v(-29.77, -16.16) * mm, "end": v(-30.38, -16.23) * mm});
            skLineSegment(sketch, "E3108", {"start": v(-30.38, -16.23) * mm, "end": v(-30.97, -16.3) * mm});
            skLineSegment(sketch, "E3109", {"start": v(-30.97, -16.3) * mm, "end": v(-31.56, -16.4) * mm});
            skLineSegment(sketch, "E3110", {"start": v(-31.56, -16.4) * mm, "end": v(-32.14, -16.52) * mm});
            skLineSegment(sketch, "E3111", {"start": v(-32.14, -16.52) * mm, "end": v(-32.7, -16.65) * mm});
            skLineSegment(sketch, "E3112", {"start": v(-32.7, -16.65) * mm, "end": v(-33.27, -16.8) * mm});
            skLineSegment(sketch, "E3113", {"start": v(-33.27, -16.8) * mm, "end": v(-33.82, -16.97) * mm});
            skLineSegment(sketch, "E3114", {"start": v(-33.82, -16.97) * mm, "end": v(-34.36, -17.15) * mm});
            skLineSegment(sketch, "E3115", {"start": v(-34.36, -17.15) * mm, "end": v(-34.9, -17.36) * mm});
            skLineSegment(sketch, "E3116", {"start": v(-34.9, -17.36) * mm, "end": v(-35.43, -17.58) * mm});
            skLineSegment(sketch, "E3117", {"start": v(-35.43, -17.58) * mm, "end": v(-35.94, -17.82) * mm});
            skLineSegment(sketch, "E3118", {"start": v(-35.94, -17.82) * mm, "end": v(-36.45, -18.07) * mm});
            skLineSegment(sketch, "E3119", {"start": v(-36.45, -18.07) * mm, "end": v(-36.96, -18.35) * mm});
            skLineSegment(sketch, "E3120", {"start": v(-36.96, -18.35) * mm, "end": v(-37.45, -18.64) * mm});
            skLineSegment(sketch, "E3121", {"start": v(-37.45, -18.64) * mm, "end": v(-37.92, -18.94) * mm});
            skLineSegment(sketch, "E3122", {"start": v(-37.92, -18.94) * mm, "end": v(-38.39, -19.26) * mm});
            skLineSegment(sketch, "E3123", {"start": v(-38.39, -19.26) * mm, "end": v(-38.84, -19.6) * mm});
            skLineSegment(sketch, "E3124", {"start": v(-38.84, -19.6) * mm, "end": v(-39.27, -19.94) * mm});
            skLineSegment(sketch, "E3125", {"start": v(-39.27, -19.94) * mm, "end": v(-39.7, -20.3) * mm});
            skLineSegment(sketch, "E3126", {"start": v(-39.7, -20.3) * mm, "end": v(-40.1, -20.69) * mm});
            skLineSegment(sketch, "E3127", {"start": v(-40.1, -20.69) * mm, "end": v(-40.5, -21.08) * mm});
            skLineSegment(sketch, "E3128", {"start": v(-40.5, -21.08) * mm, "end": v(-40.87, -21.49) * mm});
            skLineSegment(sketch, "E3129", {"start": v(-40.87, -21.49) * mm, "end": v(-41.24, -21.91) * mm});
            skLineSegment(sketch, "E3130", {"start": v(-41.24, -21.91) * mm, "end": v(-41.59, -22.35) * mm});
            skLineSegment(sketch, "E3131", {"start": v(-41.59, -22.35) * mm, "end": v(-41.93, -22.8) * mm});
            skLineSegment(sketch, "E3132", {"start": v(-41.93, -22.8) * mm, "end": v(-42.25, -23.27) * mm});
            skLineSegment(sketch, "E3133", {"start": v(-42.25, -23.27) * mm, "end": v(-42.35, -23.42) * mm});
            skLineSegment(sketch, "E3134", {"start": v(-42.35, -23.42) * mm, "end": v(-42.43, -22.95) * mm});
            skLineSegment(sketch, "E3135", {"start": v(-42.43, -22.95) * mm, "end": v(-42.7, -22.08) * mm});
            skLineSegment(sketch, "E3136", {"start": v(-42.7, -22.08) * mm, "end": v(-43.07, -21.28) * mm});
            skLineSegment(sketch, "E3137", {"start": v(-43.07, -21.28) * mm, "end": v(-43.54, -20.54) * mm});
            skLineSegment(sketch, "E3138", {"start": v(-43.54, -20.54) * mm, "end": v(-44.12, -19.86) * mm});
            skLineSegment(sketch, "E3139", {"start": v(-44.12, -19.86) * mm, "end": v(-44.81, -19.25) * mm});
            skLineSegment(sketch, "E3140", {"start": v(-44.81, -19.25) * mm, "end": v(-45.6, -18.7) * mm});
            skLineSegment(sketch, "E3141", {"start": v(-45.6, -18.7) * mm, "end": v(-46.5, -18.23) * mm});
            skLineSegment(sketch, "E3142", {"start": v(-46.5, -18.23) * mm, "end": v(-47.5, -17.8) * mm});
            skLineSegment(sketch, "E3143", {"start": v(-47.5, -17.8) * mm, "end": v(-48.61, -17.46) * mm});
            skLineSegment(sketch, "E3144", {"start": v(-48.61, -17.46) * mm, "end": v(-49.83, -17.17) * mm});
            skLineSegment(sketch, "E3145", {"start": v(-49.83, -17.17) * mm, "end": v(-51.15, -16.94) * mm});
            skLineSegment(sketch, "E3146", {"start": v(-51.15, -16.94) * mm, "end": v(-52.58, -16.78) * mm});
            skLineSegment(sketch, "E3147", {"start": v(-52.58, -16.78) * mm, "end": v(-54.1, -16.69) * mm});
            skLineSegment(sketch, "E3148", {"start": v(-54.1, -16.69) * mm, "end": v(-55.75, -16.65) * mm});
            skLineSegment(sketch, "E3149", {"start": v(-55.75, -16.65) * mm, "end": v(-56.65, -16.65) * mm});
            skLineSegment(sketch, "E3150", {"start": v(-56.65, -16.65) * mm, "end": v(-57.55, -16.65) * mm});
            skLineSegment(sketch, "E3151", {"start": v(-57.55, -16.65) * mm, "end": v(-58.19, -16.65) * mm});
            skLineSegment(sketch, "E3152", {"start": v(-58.19, -16.65) * mm, "end": v(-57.98, -15.88) * mm});
            skLineSegment(sketch, "E3153", {"start": v(-57.98, -15.88) * mm, "end": v(-57.67, -14.67) * mm});
            skLineSegment(sketch, "E3154", {"start": v(-57.67, -14.67) * mm, "end": v(-57.35, -13.46) * mm});
            skLineSegment(sketch, "E3155", {"start": v(-57.35, -13.46) * mm, "end": v(-57.03, -12.25) * mm});
            skLineSegment(sketch, "E3156", {"start": v(-57.03, -12.25) * mm, "end": v(-56.71, -11.04) * mm});
            skLineSegment(sketch, "E3157", {"start": v(-56.71, -11.04) * mm, "end": v(-56.4, -9.83) * mm});
            skLineSegment(sketch, "E3158", {"start": v(-56.4, -9.83) * mm, "end": v(-56.07, -8.62) * mm});
            skLineSegment(sketch, "E3159", {"start": v(-56.07, -8.62) * mm, "end": v(-55.76, -7.41) * mm});
            skLineSegment(sketch, "E3160", {"start": v(-55.76, -7.41) * mm, "end": v(-55.44, -6.2) * mm});
            skLineSegment(sketch, "E3161", {"start": v(-55.44, -6.2) * mm, "end": v(-55.12, -5) * mm});
            skLineSegment(sketch, "E3162", {"start": v(-55.12, -5) * mm, "end": v(-54.8, -3.79) * mm});
            skLineSegment(sketch, "E3163", {"start": v(-54.8, -3.79) * mm, "end": v(-54.48, -2.58) * mm});
            skLineSegment(sketch, "E3164", {"start": v(-54.48, -2.58) * mm, "end": v(-54.16, -1.37) * mm});
            skLineSegment(sketch, "E3165", {"start": v(-54.16, -1.37) * mm, "end": v(-53.85, -0.16) * mm});
            skLineSegment(sketch, "E3166", {"start": v(-53.85, -0.16) * mm, "end": v(-53.53, 1.05) * mm});
            skLineSegment(sketch, "E3167", {"start": v(-53.53, 1.05) * mm, "end": v(-53.2, 2.26) * mm});
            skLineSegment(sketch, "E3168", {"start": v(-53.2, 2.26) * mm, "end": v(-53.17, 2.42) * mm});
            skLineSegment(sketch, "E3169", {"start": v(-53.17, 2.42) * mm, "end": v(-53.13, 2.6) * mm});
            skLineSegment(sketch, "E3170", {"start": v(-53.13, 2.6) * mm, "end": v(-53.08, 2.77) * mm});
            skLineSegment(sketch, "E3171", {"start": v(-53.08, 2.77) * mm, "end": v(-53.04, 2.97) * mm});
            skLineSegment(sketch, "E3172", {"start": v(-53.04, 2.97) * mm, "end": v(-53, 3.18) * mm});
            skLineSegment(sketch, "E3173", {"start": v(-53, 3.18) * mm, "end": v(-52.96, 3.4) * mm});
            skLineSegment(sketch, "E3174", {"start": v(-52.96, 3.4) * mm, "end": v(-52.91, 3.65) * mm});
            skLineSegment(sketch, "E3175", {"start": v(-52.91, 3.65) * mm, "end": v(-52.87, 3.9) * mm});
            skLineSegment(sketch, "E3176", {"start": v(-52.87, 3.9) * mm, "end": v(-52.83, 4.16) * mm});
            skLineSegment(sketch, "E3177", {"start": v(-52.83, 4.16) * mm, "end": v(-52.79, 4.44) * mm});
            skLineSegment(sketch, "E3178", {"start": v(-52.79, 4.44) * mm, "end": v(-52.74, 4.73) * mm});
            skLineSegment(sketch, "E3179", {"start": v(-52.74, 4.73) * mm, "end": v(-52.7, 5.03) * mm});
            skLineSegment(sketch, "E3180", {"start": v(-52.7, 5.03) * mm, "end": v(-52.65, 5.35) * mm});
            skLineSegment(sketch, "E3181", {"start": v(-52.65, 5.35) * mm, "end": v(-52.61, 5.68) * mm});
            skLineSegment(sketch, "E3182", {"start": v(-52.61, 5.68) * mm, "end": v(-52.57, 6.03) * mm});
            skLineSegment(sketch, "E3183", {"start": v(-52.57, 6.03) * mm, "end": v(-52.52, 6.38) * mm});
            skLineSegment(sketch, "E3184", {"start": v(-52.52, 6.38) * mm, "end": v(-52.52, 6.38) * mm});
            skLineSegment(sketch, "E3185", {"start": v(-52.52, 6.38) * mm, "end": v(-52.51, 6.38) * mm});
            skLineSegment(sketch, "E3186", {"start": v(-52.51, 6.38) * mm, "end": v(-52.5, 6.38) * mm});
            skLineSegment(sketch, "E3187", {"start": v(-52.5, 6.38) * mm, "end": v(-52.5, 6.38) * mm});
            skLineSegment(sketch, "E3188", {"start": v(-52.5, 6.38) * mm, "end": v(-52.49, 6.38) * mm});
            skLineSegment(sketch, "E3189", {"start": v(-52.49, 6.38) * mm, "end": v(-52.48, 6.38) * mm});
            skLineSegment(sketch, "E3190", {"start": v(-52.48, 6.38) * mm, "end": v(-52.48, 6.38) * mm});
            skLineSegment(sketch, "E3191", {"start": v(-52.48, 6.38) * mm, "end": v(-52.47, 6.38) * mm});
            skLineSegment(sketch, "E3192", {"start": v(-52.47, 6.38) * mm, "end": v(-52.46, 6.38) * mm});
            skLineSegment(sketch, "E3193", {"start": v(-52.46, 6.38) * mm, "end": v(-52.46, 6.38) * mm});
            skLineSegment(sketch, "E3194", {"start": v(-52.46, 6.38) * mm, "end": v(-52.45, 6.38) * mm});
            skLineSegment(sketch, "E3195", {"start": v(-52.45, 6.38) * mm, "end": v(-52.45, 6.38) * mm});
            skLineSegment(sketch, "E3196", {"start": v(-52.45, 6.38) * mm, "end": v(-52.44, 6.38) * mm});
            skLineSegment(sketch, "E3197", {"start": v(-52.44, 6.38) * mm, "end": v(-52.43, 6.38) * mm});
            skLineSegment(sketch, "E3198", {"start": v(-52.43, 6.38) * mm, "end": v(-52.43, 6.38) * mm});
            skLineSegment(sketch, "E3199", {"start": v(-52.43, 6.38) * mm, "end": v(-52.4, 5.98) * mm});
            skLineSegment(sketch, "E3200", {"start": v(-52.4, 5.98) * mm, "end": v(-52.36, 5.6) * mm});
            skLineSegment(sketch, "E3201", {"start": v(-52.36, 5.6) * mm, "end": v(-52.33, 5.24) * mm});
            skLineSegment(sketch, "E3202", {"start": v(-52.33, 5.24) * mm, "end": v(-52.3, 4.9) * mm});
            skLineSegment(sketch, "E3203", {"start": v(-52.3, 4.9) * mm, "end": v(-52.27, 4.57) * mm});
            skLineSegment(sketch, "E3204", {"start": v(-52.27, 4.57) * mm, "end": v(-52.24, 4.26) * mm});
            skLineSegment(sketch, "E3205", {"start": v(-52.24, 4.26) * mm, "end": v(-52.2, 3.97) * mm});
            skLineSegment(sketch, "E3206", {"start": v(-52.2, 3.97) * mm, "end": v(-52.18, 3.7) * mm});
            skLineSegment(sketch, "E3207", {"start": v(-52.18, 3.7) * mm, "end": v(-52.15, 3.46) * mm});
            skLineSegment(sketch, "E3208", {"start": v(-52.15, 3.46) * mm, "end": v(-52.12, 3.23) * mm});
            skLineSegment(sketch, "E3209", {"start": v(-52.12, 3.23) * mm, "end": v(-52.1, 3.02) * mm});
            skLineSegment(sketch, "E3210", {"start": v(-52.1, 3.02) * mm, "end": v(-52.06, 2.83) * mm});
            skLineSegment(sketch, "E3211", {"start": v(-52.06, 2.83) * mm, "end": v(-52.04, 2.66) * mm});
            skLineSegment(sketch, "E3212", {"start": v(-52.04, 2.66) * mm, "end": v(-52, 2.5) * mm});
            skLineSegment(sketch, "E3213", {"start": v(-52, 2.5) * mm, "end": v(-51.98, 2.38) * mm});
            skLineSegment(sketch, "E3214", {"start": v(-51.98, 2.38) * mm, "end": v(-51.95, 2.26) * mm});
            skLineSegment(sketch, "E3215", {"start": v(-51.95, 2.26) * mm, "end": v(-51.66, 1.05) * mm});
            skLineSegment(sketch, "E3216", {"start": v(-51.66, 1.05) * mm, "end": v(-51.36, -0.16) * mm});
            skLineSegment(sketch, "E3217", {"start": v(-51.36, -0.16) * mm, "end": v(-51.07, -1.37) * mm});
            skLineSegment(sketch, "E3218", {"start": v(-51.07, -1.37) * mm, "end": v(-50.78, -2.58) * mm});
            skLineSegment(sketch, "E3219", {"start": v(-50.78, -2.58) * mm, "end": v(-50.48, -3.79) * mm});
            skLineSegment(sketch, "E3220", {"start": v(-50.48, -3.79) * mm, "end": v(-50.19, -5) * mm});
            skLineSegment(sketch, "E3221", {"start": v(-50.19, -5) * mm, "end": v(-49.9, -6.2) * mm});
            skLineSegment(sketch, "E3222", {"start": v(-49.9, -6.2) * mm, "end": v(-49.6, -7.41) * mm});
            skLineSegment(sketch, "E3223", {"start": v(-49.6, -7.41) * mm, "end": v(-49.3, -8.62) * mm});
            skLineSegment(sketch, "E3224", {"start": v(-49.3, -8.62) * mm, "end": v(-49, -9.83) * mm});
            skLineSegment(sketch, "E3225", {"start": v(-49, -9.83) * mm, "end": v(-48.71, -11.04) * mm});
            skLineSegment(sketch, "E3226", {"start": v(-48.71, -11.04) * mm, "end": v(-48.42, -12.25) * mm});
            skLineSegment(sketch, "E3227", {"start": v(-48.42, -12.25) * mm, "end": v(-48.12, -13.46) * mm});
            skLineSegment(sketch, "E3228", {"start": v(-48.12, -13.46) * mm, "end": v(-47.83, -14.67) * mm});
            skLineSegment(sketch, "E3229", {"start": v(-47.83, -14.67) * mm, "end": v(-47.54, -15.88) * mm});
            skLineSegment(sketch, "E3230", {"start": v(-47.54, -15.88) * mm, "end": v(-47.24, -17.09) * mm});
            skLineSegment(sketch, "E3231", {"start": v(-47.24, -17.09) * mm, "end": v(-46.56, -17.09) * mm});
            skLineSegment(sketch, "E3232", {"start": v(-46.56, -17.09) * mm, "end": v(-45.88, -17.09) * mm});
            skLineSegment(sketch, "E3233", {"start": v(-45.88, -17.09) * mm, "end": v(-45.2, -17.09) * mm});
            skLineSegment(sketch, "E3234", {"start": v(-45.2, -17.09) * mm, "end": v(-44.52, -17.09) * mm});
            skLineSegment(sketch, "E3235", {"start": v(-44.52, -17.09) * mm, "end": v(-43.84, -17.09) * mm});
            skLineSegment(sketch, "E3236", {"start": v(-43.84, -17.09) * mm, "end": v(-43.16, -17.09) * mm});
            skLineSegment(sketch, "E3237", {"start": v(-43.16, -17.09) * mm, "end": v(-42.48, -17.09) * mm});
            skLineSegment(sketch, "E3238", {"start": v(-42.48, -17.09) * mm, "end": v(-41.8, -17.09) * mm});
            skLineSegment(sketch, "E3239", {"start": v(-41.8, -17.09) * mm, "end": v(-41.13, -17.09) * mm});
            skLineSegment(sketch, "E3240", {"start": v(-41.13, -17.09) * mm, "end": v(-40.45, -17.09) * mm});
            skLineSegment(sketch, "E3241", {"start": v(-40.45, -17.09) * mm, "end": v(-39.77, -17.09) * mm});
            skLineSegment(sketch, "E3242", {"start": v(-39.77, -17.09) * mm, "end": v(-39.09, -17.09) * mm});
            skLineSegment(sketch, "E3243", {"start": v(-39.09, -17.09) * mm, "end": v(-38.4, -17.09) * mm});
            skLineSegment(sketch, "E3244", {"start": v(-38.4, -17.09) * mm, "end": v(-37.73, -17.09) * mm});
            skLineSegment(sketch, "E3245", {"start": v(-37.73, -17.09) * mm, "end": v(-37.05, -17.09) * mm});
            skLineSegment(sketch, "E3246", {"start": v(-37.05, -17.09) * mm, "end": v(-36.37, -17.09) * mm});
            skLineSegment(sketch, "E3247", {"start": v(-36.37, -17.09) * mm, "end": v(-35.83, -14.97) * mm});
            skLineSegment(sketch, "E3248", {"start": v(-35.83, -14.97) * mm, "end": v(-35.3, -12.84) * mm});
            skLineSegment(sketch, "E3249", {"start": v(-35.3, -12.84) * mm, "end": v(-34.76, -10.72) * mm});
            skLineSegment(sketch, "E3250", {"start": v(-34.76, -10.72) * mm, "end": v(-34.23, -8.6) * mm});
            skLineSegment(sketch, "E3251", {"start": v(-34.23, -8.6) * mm, "end": v(-33.69, -6.47) * mm});
            skLineSegment(sketch, "E3252", {"start": v(-33.69, -6.47) * mm, "end": v(-33.15, -4.35) * mm});
            skLineSegment(sketch, "E3253", {"start": v(-33.15, -4.35) * mm, "end": v(-32.62, -2.23) * mm});
            skLineSegment(sketch, "E3254", {"start": v(-32.62, -2.23) * mm, "end": v(-32.59, -2.1) * mm});
            skLineSegment(sketch, "E3255", {"start": v(-32.59, -2.1) * mm, "end": v(-32.57, -2.38) * mm});
            skLineSegment(sketch, "E3256", {"start": v(-32.57, -2.38) * mm, "end": v(-32.5, -2.97) * mm});
            skLineSegment(sketch, "E3257", {"start": v(-32.5, -2.97) * mm, "end": v(-32.43, -3.55) * mm});
            skLineSegment(sketch, "E3258", {"start": v(-32.43, -3.55) * mm, "end": v(-32.34, -4.12) * mm});
            skLineSegment(sketch, "E3259", {"start": v(-32.34, -4.12) * mm, "end": v(-32.23, -4.7) * mm});
            skLineSegment(sketch, "E3260", {"start": v(-32.23, -4.7) * mm, "end": v(-32.1, -5.25) * mm});
            skLineSegment(sketch, "E3261", {"start": v(-32.1, -5.25) * mm, "end": v(-31.95, -5.8) * mm});
            skLineSegment(sketch, "E3262", {"start": v(-31.95, -5.8) * mm, "end": v(-31.8, -6.34) * mm});
            skLineSegment(sketch, "E3263", {"start": v(-31.8, -6.34) * mm, "end": v(-31.61, -6.88) * mm});
            skLineSegment(sketch, "E3264", {"start": v(-31.61, -6.88) * mm, "end": v(-31.42, -7.4) * mm});
            skLineSegment(sketch, "E3265", {"start": v(-31.42, -7.4) * mm, "end": v(-31.2, -7.92) * mm});
            skLineSegment(sketch, "E3266", {"start": v(-31.2, -7.92) * mm, "end": v(-30.98, -8.43) * mm});
            skLineSegment(sketch, "E3267", {"start": v(-30.98, -8.43) * mm, "end": v(-30.73, -8.93) * mm});
            skLineSegment(sketch, "E3268", {"start": v(-30.73, -8.93) * mm, "end": v(-30.47, -9.43) * mm});
            skLineSegment(sketch, "E3269", {"start": v(-30.47, -9.43) * mm, "end": v(-30.19, -9.9) * mm});
            skLineSegment(sketch, "E3270", {"start": v(-30.19, -9.9) * mm, "end": v(-29.9, -10.38) * mm});
            skLineSegment(sketch, "E3271", {"start": v(-29.9, -10.38) * mm, "end": v(-29.59, -10.83) * mm});
            skLineSegment(sketch, "E3272", {"start": v(-29.59, -10.83) * mm, "end": v(-29.27, -11.28) * mm});
            skLineSegment(sketch, "E3273", {"start": v(-29.27, -11.28) * mm, "end": v(-28.93, -11.7) * mm});
            skLineSegment(sketch, "E3274", {"start": v(-28.93, -11.7) * mm, "end": v(-28.59, -12.12) * mm});
            skLineSegment(sketch, "E3275", {"start": v(-28.59, -12.12) * mm, "end": v(-28.23, -12.52) * mm});
            skLineSegment(sketch, "E3276", {"start": v(-28.23, -12.52) * mm, "end": v(-27.85, -12.9) * mm});
            skLineSegment(sketch, "E3277", {"start": v(-27.85, -12.9) * mm, "end": v(-27.46, -13.28) * mm});
            skLineSegment(sketch, "E3278", {"start": v(-27.46, -13.28) * mm, "end": v(-27.06, -13.64) * mm});
            skLineSegment(sketch, "E3279", {"start": v(-27.06, -13.64) * mm, "end": v(-26.65, -13.99) * mm});
            skLineSegment(sketch, "E3280", {"start": v(-26.65, -13.99) * mm, "end": v(-26.22, -14.32) * mm});
            skLineSegment(sketch, "E3281", {"start": v(-26.22, -14.32) * mm, "end": v(-25.78, -14.64) * mm});
            skLineSegment(sketch, "E3282", {"start": v(-25.78, -14.64) * mm, "end": v(-25.32, -14.94) * mm});
            skLineSegment(sketch, "E3283", {"start": v(-25.32, -14.94) * mm, "end": v(-24.85, -15.24) * mm});
            skLineSegment(sketch, "E3284", {"start": v(-24.85, -15.24) * mm, "end": v(-24.37, -15.51) * mm});
            skLineSegment(sketch, "E3285", {"start": v(-24.37, -15.51) * mm, "end": v(-23.87, -15.78) * mm});
            skLineSegment(sketch, "E3286", {"start": v(-23.87, -15.78) * mm, "end": v(-23.37, -16.02) * mm});
            skLineSegment(sketch, "E3287", {"start": v(-23.37, -16.02) * mm, "end": v(-22.87, -16.25) * mm});
            skLineSegment(sketch, "E3288", {"start": v(-22.87, -16.25) * mm, "end": v(-22.35, -16.46) * mm});
            skLineSegment(sketch, "E3289", {"start": v(-22.35, -16.46) * mm, "end": v(-21.83, -16.66) * mm});
            skLineSegment(sketch, "E3290", {"start": v(-21.83, -16.66) * mm, "end": v(-21.3, -16.83) * mm});
            skLineSegment(sketch, "E3291", {"start": v(-21.3, -16.83) * mm, "end": v(-20.77, -17) * mm});
            skLineSegment(sketch, "E3292", {"start": v(-20.77, -17) * mm, "end": v(-20.23, -17.14) * mm});
            skLineSegment(sketch, "E3293", {"start": v(-20.23, -17.14) * mm, "end": v(-19.68, -17.27) * mm});
            skLineSegment(sketch, "E3294", {"start": v(-19.68, -17.27) * mm, "end": v(-19.13, -17.38) * mm});
            skLineSegment(sketch, "E3295", {"start": v(-19.13, -17.38) * mm, "end": v(-18.57, -17.47) * mm});
            skLineSegment(sketch, "E3296", {"start": v(-18.57, -17.47) * mm, "end": v(-18, -17.55) * mm});
            skLineSegment(sketch, "E3297", {"start": v(-18, -17.55) * mm, "end": v(-17.43, -17.6) * mm});
            skLineSegment(sketch, "E3298", {"start": v(-17.43, -17.6) * mm, "end": v(-16.84, -17.65) * mm});
            skLineSegment(sketch, "E3299", {"start": v(-16.84, -17.65) * mm, "end": v(-16.26, -17.67) * mm});
            skLineSegment(sketch, "E3300", {"start": v(-16.26, -17.67) * mm, "end": v(-15.66, -17.68) * mm});
            skLineSegment(sketch, "E3301", {"start": v(-15.66, -17.68) * mm, "end": v(-15.05, -17.67) * mm});
            skLineSegment(sketch, "E3302", {"start": v(-15.05, -17.67) * mm, "end": v(-14.45, -17.65) * mm});
            skLineSegment(sketch, "E3303", {"start": v(-14.45, -17.65) * mm, "end": v(-13.86, -17.6) * mm});
            skLineSegment(sketch, "E3304", {"start": v(-13.86, -17.6) * mm, "end": v(-13.27, -17.54) * mm});
            skLineSegment(sketch, "E3305", {"start": v(-13.27, -17.54) * mm, "end": v(-12.7, -17.46) * mm});
            skLineSegment(sketch, "E3306", {"start": v(-12.7, -17.46) * mm, "end": v(-12.53, -17.44) * mm});
            skLineSegment(sketch, "E3307", {"start": v(-12.53, -17.44) * mm, "end": v(-12.53, -17.82) * mm});
            skLineSegment(sketch, "E3308", {"start": v(-12.53, -17.82) * mm, "end": v(-12.53, -18.98) * mm});
            skLineSegment(sketch, "E3309", {"start": v(-12.53, -18.98) * mm, "end": v(-12.53, -20.15) * mm});
            skLineSegment(sketch, "E3310", {"start": v(-12.53, -20.15) * mm, "end": v(-12.53, -21.31) * mm});
            skLineSegment(sketch, "E3311", {"start": v(-12.53, -21.31) * mm, "end": v(-12.53, -22.48) * mm});
            skLineSegment(sketch, "E3312", {"start": v(-12.53, -22.48) * mm, "end": v(-12.53, -23.64) * mm});
            skLineSegment(sketch, "E3313", {"start": v(-12.53, -23.64) * mm, "end": v(-12.53, -24.8) * mm});
            skLineSegment(sketch, "E3314", {"start": v(-12.53, -24.8) * mm, "end": v(-12.53, -25.96) * mm});
            skLineSegment(sketch, "E3315", {"start": v(-12.53, -25.96) * mm, "end": v(-12.74, -25.45) * mm});
            skLineSegment(sketch, "E3316", {"start": v(7.15, -19.06) * mm, "end": v(7.15, -20.26) * mm});
            skLineSegment(sketch, "E3317", {"start": v(7.15, -20.26) * mm, "end": v(7.15, -21.47) * mm});
            skLineSegment(sketch, "E3318", {"start": v(7.15, -21.47) * mm, "end": v(7.15, -22.67) * mm});
            skLineSegment(sketch, "E3319", {"start": v(7.15, -22.67) * mm, "end": v(7.15, -23.87) * mm});
            skLineSegment(sketch, "E3320", {"start": v(7.15, -23.87) * mm, "end": v(7.15, -25.08) * mm});
            skLineSegment(sketch, "E3321", {"start": v(7.15, -25.08) * mm, "end": v(7.15, -26.28) * mm});
            skLineSegment(sketch, "E3322", {"start": v(7.15, -26.28) * mm, "end": v(7.15, -27.49) * mm});
            skLineSegment(sketch, "E3323", {"start": v(7.15, -27.49) * mm, "end": v(7.15, -28.69) * mm});
            skLineSegment(sketch, "E3324", {"start": v(7.15, -28.69) * mm, "end": v(7.15, -29.9) * mm});
            skLineSegment(sketch, "E3325", {"start": v(7.15, -29.9) * mm, "end": v(7.15, -31.1) * mm});
            skLineSegment(sketch, "E3326", {"start": v(7.15, -31.1) * mm, "end": v(7.15, -32.3) * mm});
            skLineSegment(sketch, "E3327", {"start": v(7.15, -32.3) * mm, "end": v(7.15, -33.5) * mm});
            skLineSegment(sketch, "E3328", {"start": v(7.15, -33.5) * mm, "end": v(7.15, -34.7) * mm});
            skLineSegment(sketch, "E3329", {"start": v(7.15, -34.7) * mm, "end": v(7.15, -35.9) * mm});
            skLineSegment(sketch, "E3330", {"start": v(7.15, -35.9) * mm, "end": v(7.15, -36.3) * mm});
            skLineSegment(sketch, "E3331", {"start": v(7.15, -36.3) * mm, "end": v(7.13, -36.7) * mm});
            skLineSegment(sketch, "E3332", {"start": v(7.13, -36.7) * mm, "end": v(7.1, -37.07) * mm});
            skLineSegment(sketch, "E3333", {"start": v(7.1, -37.07) * mm, "end": v(7.08, -37.43) * mm});
            skLineSegment(sketch, "E3334", {"start": v(7.08, -37.43) * mm, "end": v(7.03, -37.78) * mm});
            skLineSegment(sketch, "E3335", {"start": v(7.03, -37.78) * mm, "end": v(6.98, -38.12) * mm});
            skLineSegment(sketch, "E3336", {"start": v(6.98, -38.12) * mm, "end": v(6.92, -38.45) * mm});
            skLineSegment(sketch, "E3337", {"start": v(6.92, -38.45) * mm, "end": v(6.85, -38.76) * mm});
            skLineSegment(sketch, "E3338", {"start": v(6.85, -38.76) * mm, "end": v(6.77, -39.06) * mm});
            skLineSegment(sketch, "E3339", {"start": v(6.77, -39.06) * mm, "end": v(6.68, -39.35) * mm});
            skLineSegment(sketch, "E3340", {"start": v(6.68, -39.35) * mm, "end": v(6.59, -39.62) * mm});
            skLineSegment(sketch, "E3341", {"start": v(6.59, -39.62) * mm, "end": v(6.48, -39.88) * mm});
            skLineSegment(sketch, "E3342", {"start": v(6.48, -39.88) * mm, "end": v(6.36, -40.14) * mm});
            skLineSegment(sketch, "E3343", {"start": v(6.36, -40.14) * mm, "end": v(6.23, -40.37) * mm});
            skLineSegment(sketch, "E3344", {"start": v(6.23, -40.37) * mm, "end": v(6.1, -40.6) * mm});
            skLineSegment(sketch, "E3345", {"start": v(6.1, -40.6) * mm, "end": v(5.95, -40.81) * mm});
            skLineSegment(sketch, "E3346", {"start": v(5.95, -40.81) * mm, "end": v(5.8, -41.01) * mm});
            skLineSegment(sketch, "E3347", {"start": v(5.8, -41.01) * mm, "end": v(5.64, -41.2) * mm});
            skLineSegment(sketch, "E3348", {"start": v(5.64, -41.2) * mm, "end": v(5.47, -41.38) * mm});
            skLineSegment(sketch, "E3349", {"start": v(5.47, -41.38) * mm, "end": v(5.29, -41.54) * mm});
            skLineSegment(sketch, "E3350", {"start": v(5.29, -41.54) * mm, "end": v(5.1, -41.69) * mm});
            skLineSegment(sketch, "E3351", {"start": v(5.1, -41.69) * mm, "end": v(4.9, -41.82) * mm});
            skLineSegment(sketch, "E3352", {"start": v(4.9, -41.82) * mm, "end": v(4.7, -41.95) * mm});
            skLineSegment(sketch, "E3353", {"start": v(4.7, -41.95) * mm, "end": v(4.48, -42.06) * mm});
            skLineSegment(sketch, "E3354", {"start": v(4.48, -42.06) * mm, "end": v(4.26, -42.15) * mm});
            skLineSegment(sketch, "E3355", {"start": v(4.26, -42.15) * mm, "end": v(4.03, -42.24) * mm});
            skLineSegment(sketch, "E3356", {"start": v(4.03, -42.24) * mm, "end": v(3.79, -42.3) * mm});
            skLineSegment(sketch, "E3357", {"start": v(3.79, -42.3) * mm, "end": v(3.54, -42.37) * mm});
            skLineSegment(sketch, "E3358", {"start": v(3.54, -42.37) * mm, "end": v(3.28, -42.41) * mm});
            skLineSegment(sketch, "E3359", {"start": v(3.28, -42.41) * mm, "end": v(3.02, -42.44) * mm});
            skLineSegment(sketch, "E3360", {"start": v(3.02, -42.44) * mm, "end": v(2.74, -42.46) * mm});
            skLineSegment(sketch, "E3361", {"start": v(2.74, -42.46) * mm, "end": v(2.46, -42.47) * mm});
            skLineSegment(sketch, "E3362", {"start": v(2.46, -42.47) * mm, "end": v(2.18, -42.46) * mm});
            skLineSegment(sketch, "E3363", {"start": v(2.18, -42.46) * mm, "end": v(1.9, -42.44) * mm});
            skLineSegment(sketch, "E3364", {"start": v(1.9, -42.44) * mm, "end": v(1.65, -42.4) * mm});
            skLineSegment(sketch, "E3365", {"start": v(1.65, -42.4) * mm, "end": v(1.39, -42.36) * mm});
            skLineSegment(sketch, "E3366", {"start": v(1.39, -42.36) * mm, "end": v(1.14, -42.3) * mm});
            skLineSegment(sketch, "E3367", {"start": v(1.14, -42.3) * mm, "end": v(0.9, -42.22) * mm});
            skLineSegment(sketch, "E3368", {"start": v(0.9, -42.22) * mm, "end": v(0.67, -42.13) * mm});
            skLineSegment(sketch, "E3369", {"start": v(0.67, -42.13) * mm, "end": v(0.45, -42.03) * mm});
            skLineSegment(sketch, "E3370", {"start": v(0.45, -42.03) * mm, "end": v(0.24, -41.91) * mm});
            skLineSegment(sketch, "E3371", {"start": v(0.24, -41.91) * mm, "end": v(0.03, -41.78) * mm});
            skLineSegment(sketch, "E3372", {"start": v(0.03, -41.78) * mm, "end": v(-0.17, -41.64) * mm});
            skLineSegment(sketch, "E3373", {"start": v(-0.17, -41.64) * mm, "end": v(-0.36, -41.48) * mm});
            skLineSegment(sketch, "E3374", {"start": v(-0.36, -41.48) * mm, "end": v(-0.54, -41.3) * mm});
            skLineSegment(sketch, "E3375", {"start": v(-0.54, -41.3) * mm, "end": v(-0.71, -41.12) * mm});
            skLineSegment(sketch, "E3376", {"start": v(-0.71, -41.12) * mm, "end": v(-0.88, -40.92) * mm});
            skLineSegment(sketch, "E3377", {"start": v(-0.88, -40.92) * mm, "end": v(-1.03, -40.7) * mm});
            skLineSegment(sketch, "E3378", {"start": v(-1.03, -40.7) * mm, "end": v(-1.18, -40.48) * mm});
            skLineSegment(sketch, "E3379", {"start": v(-1.18, -40.48) * mm, "end": v(-1.32, -40.24) * mm});
            skLineSegment(sketch, "E3380", {"start": v(-1.32, -40.24) * mm, "end": v(-1.45, -40) * mm});
            skLineSegment(sketch, "E3381", {"start": v(-1.45, -40) * mm, "end": v(-1.57, -39.73) * mm});
            skLineSegment(sketch, "E3382", {"start": v(-1.57, -39.73) * mm, "end": v(-1.68, -39.46) * mm});
            skLineSegment(sketch, "E3383", {"start": v(-1.68, -39.46) * mm, "end": v(-1.78, -39.17) * mm});
            skLineSegment(sketch, "E3384", {"start": v(-1.78, -39.17) * mm, "end": v(-1.87, -38.87) * mm});
            skLineSegment(sketch, "E3385", {"start": v(-1.87, -38.87) * mm, "end": v(-1.95, -38.57) * mm});
            skLineSegment(sketch, "E3386", {"start": v(-1.95, -38.57) * mm, "end": v(-2.02, -38.25) * mm});
            skLineSegment(sketch, "E3387", {"start": v(-2.02, -38.25) * mm, "end": v(-2.08, -37.91) * mm});
            skLineSegment(sketch, "E3388", {"start": v(-2.08, -37.91) * mm, "end": v(-2.13, -37.57) * mm});
            skLineSegment(sketch, "E3389", {"start": v(-2.13, -37.57) * mm, "end": v(-2.18, -37.21) * mm});
            skLineSegment(sketch, "E3390", {"start": v(-2.18, -37.21) * mm, "end": v(-2.2, -36.85) * mm});
            skLineSegment(sketch, "E3391", {"start": v(-2.2, -36.85) * mm, "end": v(-2.23, -36.47) * mm});
            skLineSegment(sketch, "E3392", {"start": v(-2.23, -36.47) * mm, "end": v(-2.25, -36.08) * mm});
            skLineSegment(sketch, "E3393", {"start": v(-2.25, -36.08) * mm, "end": v(-2.25, -35.67) * mm});
            skLineSegment(sketch, "E3394", {"start": v(-2.25, -35.67) * mm, "end": v(-2.25, -34.48) * mm});
            skLineSegment(sketch, "E3395", {"start": v(-2.25, -34.48) * mm, "end": v(-2.25, -33.3) * mm});
            skLineSegment(sketch, "E3396", {"start": v(-2.25, -33.3) * mm, "end": v(-2.25, -32.1) * mm});
            skLineSegment(sketch, "E3397", {"start": v(-2.25, -32.1) * mm, "end": v(-2.25, -30.92) * mm});
            skLineSegment(sketch, "E3398", {"start": v(-2.25, -30.92) * mm, "end": v(-2.25, -29.73) * mm});
            skLineSegment(sketch, "E3399", {"start": v(-2.25, -29.73) * mm, "end": v(-2.25, -28.54) * mm});
            skLineSegment(sketch, "E3400", {"start": v(-2.25, -28.54) * mm, "end": v(-2.25, -27.35) * mm});
            skLineSegment(sketch, "E3401", {"start": v(-2.25, -27.35) * mm, "end": v(-2.25, -26.16) * mm});
            skLineSegment(sketch, "E3402", {"start": v(-2.25, -26.16) * mm, "end": v(-2.25, -24.97) * mm});
            skLineSegment(sketch, "E3403", {"start": v(-2.25, -24.97) * mm, "end": v(-2.25, -23.79) * mm});
            skLineSegment(sketch, "E3404", {"start": v(-2.25, -23.79) * mm, "end": v(-2.25, -22.6) * mm});
            skLineSegment(sketch, "E3405", {"start": v(-2.25, -22.6) * mm, "end": v(-2.25, -21.4) * mm});
            skLineSegment(sketch, "E3406", {"start": v(-2.25, -21.4) * mm, "end": v(-2.25, -20.22) * mm});
            skLineSegment(sketch, "E3407", {"start": v(-2.25, -20.22) * mm, "end": v(-2.25, -19.03) * mm});
            skLineSegment(sketch, "E3408", {"start": v(-2.25, -19.03) * mm, "end": v(-2.25, -17.84) * mm});
            skLineSegment(sketch, "E3409", {"start": v(-2.25, -17.84) * mm, "end": v(-2.25, -16.65) * mm});
            skLineSegment(sketch, "E3410", {"start": v(-2.25, -16.65) * mm, "end": v(-2.9, -16.65) * mm});
            skLineSegment(sketch, "E3411", {"start": v(-2.9, -16.65) * mm, "end": v(-3.54, -16.65) * mm});
            skLineSegment(sketch, "E3412", {"start": v(-3.54, -16.65) * mm, "end": v(-4.18, -16.65) * mm});
            skLineSegment(sketch, "E3413", {"start": v(-4.18, -16.65) * mm, "end": v(-4.82, -16.65) * mm});
            skLineSegment(sketch, "E3414", {"start": v(-4.82, -16.65) * mm, "end": v(-5.46, -16.65) * mm});
            skLineSegment(sketch, "E3415", {"start": v(-5.46, -16.65) * mm, "end": v(-6.1, -16.65) * mm});
            skLineSegment(sketch, "E3416", {"start": v(-6.1, -16.65) * mm, "end": v(-6.75, -16.65) * mm});
            skLineSegment(sketch, "E3417", {"start": v(-6.75, -16.65) * mm, "end": v(-7.4, -16.65) * mm});
            skLineSegment(sketch, "E3418", {"start": v(-7.4, -16.65) * mm, "end": v(-8.03, -16.65) * mm});
            skLineSegment(sketch, "E3419", {"start": v(-8.03, -16.65) * mm, "end": v(-8.68, -16.65) * mm});
            skLineSegment(sketch, "E3420", {"start": v(-8.68, -16.65) * mm, "end": v(-9.32, -16.65) * mm});
            skLineSegment(sketch, "E3421", {"start": v(-9.32, -16.65) * mm, "end": v(-9.46, -16.65) * mm});
            skLineSegment(sketch, "E3422", {"start": v(-9.46, -16.65) * mm, "end": v(-9.37, -16.62) * mm});
            skLineSegment(sketch, "E3423", {"start": v(-9.37, -16.62) * mm, "end": v(-8.84, -16.42) * mm});
            skLineSegment(sketch, "E3424", {"start": v(-8.84, -16.42) * mm, "end": v(-8.32, -16.2) * mm});
            skLineSegment(sketch, "E3425", {"start": v(-8.32, -16.2) * mm, "end": v(-7.8, -15.97) * mm});
            skLineSegment(sketch, "E3426", {"start": v(-7.8, -15.97) * mm, "end": v(-7.3, -15.71) * mm});
            skLineSegment(sketch, "E3427", {"start": v(-7.3, -15.71) * mm, "end": v(-6.8, -15.44) * mm});
            skLineSegment(sketch, "E3428", {"start": v(-6.8, -15.44) * mm, "end": v(-6.32, -15.16) * mm});
            skLineSegment(sketch, "E3429", {"start": v(-6.32, -15.16) * mm, "end": v(-5.84, -14.85) * mm});
            skLineSegment(sketch, "E3430", {"start": v(-5.84, -14.85) * mm, "end": v(-5.38, -14.54) * mm});
            skLineSegment(sketch, "E3431", {"start": v(-5.38, -14.54) * mm, "end": v(-4.94, -14.21) * mm});
            skLineSegment(sketch, "E3432", {"start": v(-4.94, -14.21) * mm, "end": v(-4.5, -13.87) * mm});
            skLineSegment(sketch, "E3433", {"start": v(-4.5, -13.87) * mm, "end": v(-4.08, -13.51) * mm});
            skLineSegment(sketch, "E3434", {"start": v(-4.08, -13.51) * mm, "end": v(-3.68, -13.14) * mm});
            skLineSegment(sketch, "E3435", {"start": v(-3.68, -13.14) * mm, "end": v(-3.29, -12.75) * mm});
            skLineSegment(sketch, "E3436", {"start": v(-3.29, -12.75) * mm, "end": v(-2.9, -12.36) * mm});
            skLineSegment(sketch, "E3437", {"start": v(-2.9, -12.36) * mm, "end": v(-2.54, -11.94) * mm});
            skLineSegment(sketch, "E3438", {"start": v(-2.54, -11.94) * mm, "end": v(-2.2, -11.51) * mm});
            skLineSegment(sketch, "E3439", {"start": v(-2.2, -11.51) * mm, "end": v(-1.86, -11.07) * mm});
            skLineSegment(sketch, "E3440", {"start": v(-1.86, -11.07) * mm, "end": v(-1.53, -10.62) * mm});
            skLineSegment(sketch, "E3441", {"start": v(-1.53, -10.62) * mm, "end": v(-1.22, -10.15) * mm});
            skLineSegment(sketch, "E3442", {"start": v(-1.22, -10.15) * mm, "end": v(-0.93, -9.66) * mm});
            skLineSegment(sketch, "E3443", {"start": v(-0.93, -9.66) * mm, "end": v(-0.65, -9.17) * mm});
            skLineSegment(sketch, "E3444", {"start": v(-0.65, -9.17) * mm, "end": v(-0.43, -8.75) * mm});
            skLineSegment(sketch, "E3445", {"start": v(-0.43, -8.75) * mm, "end": v(-0.43, -10.72) * mm});
            skLineSegment(sketch, "E3446", {"start": v(-0.43, -10.72) * mm, "end": v(-0.43, -12.84) * mm});
            skLineSegment(sketch, "E3447", {"start": v(-0.43, -12.84) * mm, "end": v(-0.43, -14.97) * mm});
            skLineSegment(sketch, "E3448", {"start": v(-0.43, -14.97) * mm, "end": v(-0.43, -17.09) * mm});
            skLineSegment(sketch, "E3449", {"start": v(-0.43, -17.09) * mm, "end": v(0.21, -17.09) * mm});
            skLineSegment(sketch, "E3450", {"start": v(0.21, -17.09) * mm, "end": v(0.85, -17.09) * mm});
            skLineSegment(sketch, "E3451", {"start": v(0.85, -17.09) * mm, "end": v(1.5, -17.09) * mm});
            skLineSegment(sketch, "E3452", {"start": v(1.5, -17.09) * mm, "end": v(2.13, -17.09) * mm});
            skLineSegment(sketch, "E3453", {"start": v(2.13, -17.09) * mm, "end": v(2.77, -17.09) * mm});
            skLineSegment(sketch, "E3454", {"start": v(2.77, -17.09) * mm, "end": v(3.41, -17.09) * mm});
            skLineSegment(sketch, "E3455", {"start": v(3.41, -17.09) * mm, "end": v(4.05, -17.09) * mm});
            skLineSegment(sketch, "E3456", {"start": v(4.05, -17.09) * mm, "end": v(4.7, -17.09) * mm});
            skLineSegment(sketch, "E3457", {"start": v(4.7, -17.09) * mm, "end": v(5.33, -17.09) * mm});
            skLineSegment(sketch, "E3458", {"start": v(5.33, -17.09) * mm, "end": v(5.97, -17.09) * mm});
            skLineSegment(sketch, "E3459", {"start": v(5.97, -17.09) * mm, "end": v(6.6, -17.09) * mm});
            skLineSegment(sketch, "E3460", {"start": v(6.6, -17.09) * mm, "end": v(7.15, -17.09) * mm});
            skLineSegment(sketch, "E3461", {"start": v(7.15, -17.09) * mm, "end": v(7.15, -17.86) * mm});
            skLineSegment(sketch, "E3462", {"start": v(7.15, -17.86) * mm, "end": v(7.15, -19.06) * mm});
            skLineSegment(sketch, "E3463", {"start": v(16.17, -16.65) * mm, "end": v(15.52, -16.65) * mm});
            skLineSegment(sketch, "E3464", {"start": v(15.52, -16.65) * mm, "end": v(14.88, -16.65) * mm});
            skLineSegment(sketch, "E3465", {"start": v(14.88, -16.65) * mm, "end": v(14.23, -16.65) * mm});
            skLineSegment(sketch, "E3466", {"start": v(14.23, -16.65) * mm, "end": v(13.59, -16.65) * mm});
            skLineSegment(sketch, "E3467", {"start": v(13.59, -16.65) * mm, "end": v(12.95, -16.65) * mm});
            skLineSegment(sketch, "E3468", {"start": v(12.95, -16.65) * mm, "end": v(12.3, -16.65) * mm});
            skLineSegment(sketch, "E3469", {"start": v(12.3, -16.65) * mm, "end": v(11.66, -16.65) * mm});
            skLineSegment(sketch, "E3470", {"start": v(11.66, -16.65) * mm, "end": v(11.01, -16.65) * mm});
            skLineSegment(sketch, "E3471", {"start": v(11.01, -16.65) * mm, "end": v(10.37, -16.65) * mm});
            skLineSegment(sketch, "E3472", {"start": v(10.37, -16.65) * mm, "end": v(9.8, -16.65) * mm});
            skLineSegment(sketch, "E3473", {"start": v(9.8, -16.65) * mm, "end": v(9.8, -16.34) * mm});
            skLineSegment(sketch, "E3474", {"start": v(9.8, -16.34) * mm, "end": v(9.8, -15.6) * mm});
            skLineSegment(sketch, "E3475", {"start": v(9.8, -15.6) * mm, "end": v(9.8, -14.85) * mm});
            skLineSegment(sketch, "E3476", {"start": v(9.8, -14.85) * mm, "end": v(9.8, -14.1) * mm});
            skLineSegment(sketch, "E3477", {"start": v(9.8, -14.1) * mm, "end": v(9.8, -13.36) * mm});
            skLineSegment(sketch, "E3478", {"start": v(9.8, -13.36) * mm, "end": v(9.8, -12.61) * mm});
            skLineSegment(sketch, "E3479", {"start": v(9.8, -12.61) * mm, "end": v(9.8, -11.87) * mm});
            skLineSegment(sketch, "E3480", {"start": v(9.8, -11.87) * mm, "end": v(9.8, -11.12) * mm});
            skLineSegment(sketch, "E3481", {"start": v(9.8, -11.12) * mm, "end": v(9.8, -10.37) * mm});
            skLineSegment(sketch, "E3482", {"start": v(9.8, -10.37) * mm, "end": v(9.8, -9.63) * mm});
            skLineSegment(sketch, "E3483", {"start": v(9.8, -9.63) * mm, "end": v(9.8, -8.88) * mm});
            skLineSegment(sketch, "E3484", {"start": v(9.8, -8.88) * mm, "end": v(9.8, -8.14) * mm});
            skLineSegment(sketch, "E3485", {"start": v(9.8, -8.14) * mm, "end": v(9.8, -7.39) * mm});
            skLineSegment(sketch, "E3486", {"start": v(9.8, -7.39) * mm, "end": v(9.8, -6.64) * mm});
            skLineSegment(sketch, "E3487", {"start": v(9.8, -6.64) * mm, "end": v(9.8, -5.9) * mm});
            skLineSegment(sketch, "E3488", {"start": v(9.8, -5.9) * mm, "end": v(9.8, -5.15) * mm});
            skLineSegment(sketch, "E3489", {"start": v(9.8, -5.15) * mm, "end": v(9.83, -5.15) * mm});
            skLineSegment(sketch, "E3490", {"start": v(9.83, -5.15) * mm, "end": v(9.86, -5.15) * mm});
            skLineSegment(sketch, "E3491", {"start": v(9.86, -5.15) * mm, "end": v(9.88, -5.15) * mm});
            skLineSegment(sketch, "E3492", {"start": v(9.88, -5.15) * mm, "end": v(9.9, -5.15) * mm});
            skLineSegment(sketch, "E3493", {"start": v(9.9, -5.15) * mm, "end": v(9.93, -5.15) * mm});
            skLineSegment(sketch, "E3494", {"start": v(9.93, -5.15) * mm, "end": v(9.96, -5.15) * mm});
            skLineSegment(sketch, "E3495", {"start": v(9.96, -5.15) * mm, "end": v(9.98, -5.15) * mm});
            skLineSegment(sketch, "E3496", {"start": v(9.98, -5.15) * mm, "end": v(10, -5.15) * mm});
            skLineSegment(sketch, "E3497", {"start": v(10, -5.15) * mm, "end": v(10.03, -5.15) * mm});
            skLineSegment(sketch, "E3498", {"start": v(10.03, -5.15) * mm, "end": v(10.06, -5.15) * mm});
            skLineSegment(sketch, "E3499", {"start": v(10.06, -5.15) * mm, "end": v(10.08, -5.15) * mm});
            skLineSegment(sketch, "E3500", {"start": v(10.08, -5.15) * mm, "end": v(10.1, -5.15) * mm});
            skLineSegment(sketch, "E3501", {"start": v(10.1, -5.15) * mm, "end": v(10.13, -5.15) * mm});
            skLineSegment(sketch, "E3502", {"start": v(10.13, -5.15) * mm, "end": v(10.16, -5.15) * mm});
            skLineSegment(sketch, "E3503", {"start": v(10.16, -5.15) * mm, "end": v(10.18, -5.15) * mm});
            skLineSegment(sketch, "E3504", {"start": v(10.18, -5.15) * mm, "end": v(10.2, -5.15) * mm});
            skLineSegment(sketch, "E3505", {"start": v(10.2, -5.15) * mm, "end": v(10.38, -5.16) * mm});
            skLineSegment(sketch, "E3506", {"start": v(10.38, -5.16) * mm, "end": v(10.55, -5.17) * mm});
            skLineSegment(sketch, "E3507", {"start": v(10.55, -5.17) * mm, "end": v(10.72, -5.2) * mm});
            skLineSegment(sketch, "E3508", {"start": v(10.72, -5.2) * mm, "end": v(10.88, -5.23) * mm});
            skLineSegment(sketch, "E3509", {"start": v(10.88, -5.23) * mm, "end": v(11.05, -5.27) * mm});
            skLineSegment(sketch, "E3510", {"start": v(11.05, -5.27) * mm, "end": v(11.21, -5.32) * mm});
            skLineSegment(sketch, "E3511", {"start": v(11.21, -5.32) * mm, "end": v(11.37, -5.39) * mm});
            skLineSegment(sketch, "E3512", {"start": v(11.37, -5.39) * mm, "end": v(11.53, -5.46) * mm});
            skLineSegment(sketch, "E3513", {"start": v(11.53, -5.46) * mm, "end": v(11.7, -5.54) * mm});
            skLineSegment(sketch, "E3514", {"start": v(11.7, -5.54) * mm, "end": v(11.85, -5.63) * mm});
            skLineSegment(sketch, "E3515", {"start": v(11.85, -5.63) * mm, "end": v(12, -5.73) * mm});
            skLineSegment(sketch, "E3516", {"start": v(12, -5.73) * mm, "end": v(12.16, -5.84) * mm});
            skLineSegment(sketch, "E3517", {"start": v(12.16, -5.84) * mm, "end": v(12.3, -5.96) * mm});
            skLineSegment(sketch, "E3518", {"start": v(12.3, -5.96) * mm, "end": v(12.46, -6.1) * mm});
            skLineSegment(sketch, "E3519", {"start": v(12.46, -6.1) * mm, "end": v(12.6, -6.23) * mm});
            skLineSegment(sketch, "E3520", {"start": v(12.6, -6.23) * mm, "end": v(12.75, -6.38) * mm});
            skLineSegment(sketch, "E3521", {"start": v(12.75, -6.38) * mm, "end": v(12.9, -6.54) * mm});
            skLineSegment(sketch, "E3522", {"start": v(12.9, -6.54) * mm, "end": v(13.04, -6.7) * mm});
            skLineSegment(sketch, "E3523", {"start": v(13.04, -6.7) * mm, "end": v(13.18, -6.88) * mm});
            skLineSegment(sketch, "E3524", {"start": v(13.18, -6.88) * mm, "end": v(13.31, -7.06) * mm});
            skLineSegment(sketch, "E3525", {"start": v(13.31, -7.06) * mm, "end": v(13.44, -7.24) * mm});
            skLineSegment(sketch, "E3526", {"start": v(13.44, -7.24) * mm, "end": v(13.57, -7.44) * mm});
            skLineSegment(sketch, "E3527", {"start": v(13.57, -7.44) * mm, "end": v(13.7, -7.64) * mm});
            skLineSegment(sketch, "E3528", {"start": v(13.7, -7.64) * mm, "end": v(13.82, -7.85) * mm});
            skLineSegment(sketch, "E3529", {"start": v(13.82, -7.85) * mm, "end": v(13.94, -8.06) * mm});
            skLineSegment(sketch, "E3530", {"start": v(13.94, -8.06) * mm, "end": v(14.05, -8.28) * mm});
            skLineSegment(sketch, "E3531", {"start": v(14.05, -8.28) * mm, "end": v(14.16, -8.51) * mm});
            skLineSegment(sketch, "E3532", {"start": v(14.16, -8.51) * mm, "end": v(14.27, -8.75) * mm});
            skLineSegment(sketch, "E3533", {"start": v(14.27, -8.75) * mm, "end": v(14.37, -9) * mm});
            skLineSegment(sketch, "E3534", {"start": v(14.37, -9) * mm, "end": v(14.47, -9.25) * mm});
            skLineSegment(sketch, "E3535", {"start": v(14.47, -9.25) * mm, "end": v(14.57, -9.5) * mm});
            skLineSegment(sketch, "E3536", {"start": v(14.57, -9.5) * mm, "end": v(14.66, -9.77) * mm});
            skLineSegment(sketch, "E3537", {"start": v(14.66, -9.77) * mm, "end": v(14.82, -10.23) * mm});
            skLineSegment(sketch, "E3538", {"start": v(14.82, -10.23) * mm, "end": v(14.98, -10.68) * mm});
            skLineSegment(sketch, "E3539", {"start": v(14.98, -10.68) * mm, "end": v(15.14, -11.14) * mm});
            skLineSegment(sketch, "E3540", {"start": v(15.14, -11.14) * mm, "end": v(15.3, -11.6) * mm});
            skLineSegment(sketch, "E3541", {"start": v(15.3, -11.6) * mm, "end": v(15.45, -12.06) * mm});
            skLineSegment(sketch, "E3542", {"start": v(15.45, -12.06) * mm, "end": v(15.61, -12.51) * mm});
            skLineSegment(sketch, "E3543", {"start": v(15.61, -12.51) * mm, "end": v(15.77, -12.97) * mm});
            skLineSegment(sketch, "E3544", {"start": v(15.77, -12.97) * mm, "end": v(15.93, -13.43) * mm});
            skLineSegment(sketch, "E3545", {"start": v(15.93, -13.43) * mm, "end": v(16.09, -13.89) * mm});
            skLineSegment(sketch, "E3546", {"start": v(16.09, -13.89) * mm, "end": v(16.25, -14.34) * mm});
            skLineSegment(sketch, "E3547", {"start": v(16.25, -14.34) * mm, "end": v(16.4, -14.8) * mm});
            skLineSegment(sketch, "E3548", {"start": v(16.4, -14.8) * mm, "end": v(16.56, -15.26) * mm});
            skLineSegment(sketch, "E3549", {"start": v(16.56, -15.26) * mm, "end": v(16.72, -15.72) * mm});
            skLineSegment(sketch, "E3550", {"start": v(16.72, -15.72) * mm, "end": v(16.88, -16.17) * mm});
            skLineSegment(sketch, "E3551", {"start": v(16.88, -16.17) * mm, "end": v(17.04, -16.63) * mm});
            skLineSegment(sketch, "E3552", {"start": v(17.04, -16.63) * mm, "end": v(17.05, -16.65) * mm});
            skLineSegment(sketch, "E3553", {"start": v(17.05, -16.65) * mm, "end": v(16.8, -16.65) * mm});
            skLineSegment(sketch, "E3554", {"start": v(16.8, -16.65) * mm, "end": v(16.3, -16.65) * mm});
            skLineSegment(sketch, "E3555", {"start": v(16.3, -16.65) * mm, "end": v(16.17, -16.65) * mm});
            skLineSegment(sketch, "E3556", {"start": v(42.02, -16.65) * mm, "end": v(40.18, -16.65) * mm});
            skLineSegment(sketch, "E3557", {"start": v(40.18, -16.65) * mm, "end": v(38.34, -16.65) * mm});
            skLineSegment(sketch, "E3558", {"start": v(38.34, -16.65) * mm, "end": v(36.5, -16.65) * mm});
            skLineSegment(sketch, "E3559", {"start": v(36.5, -16.65) * mm, "end": v(36.1, -16.65) * mm});
            skLineSegment(sketch, "E3560", {"start": v(36.1, -16.65) * mm, "end": v(36.1, -16.34) * mm});
            skLineSegment(sketch, "E3561", {"start": v(36.1, -16.34) * mm, "end": v(36.1, -15.6) * mm});
            skLineSegment(sketch, "E3562", {"start": v(36.1, -15.6) * mm, "end": v(36.1, -14.85) * mm});
            skLineSegment(sketch, "E3563", {"start": v(36.1, -14.85) * mm, "end": v(36.1, -14.1) * mm});
            skLineSegment(sketch, "E3564", {"start": v(36.1, -14.1) * mm, "end": v(36.1, -13.36) * mm});
            skLineSegment(sketch, "E3565", {"start": v(36.1, -13.36) * mm, "end": v(36.1, -12.61) * mm});
            skLineSegment(sketch, "E3566", {"start": v(36.1, -12.61) * mm, "end": v(36.1, -11.87) * mm});
            skLineSegment(sketch, "E3567", {"start": v(36.1, -11.87) * mm, "end": v(36.1, -11.12) * mm});
            skLineSegment(sketch, "E3568", {"start": v(36.1, -11.12) * mm, "end": v(36.1, -10.37) * mm});
            skLineSegment(sketch, "E3569", {"start": v(36.1, -10.37) * mm, "end": v(36.1, -9.63) * mm});
            skLineSegment(sketch, "E3570", {"start": v(36.1, -9.63) * mm, "end": v(36.1, -8.88) * mm});
            skLineSegment(sketch, "E3571", {"start": v(36.1, -8.88) * mm, "end": v(36.1, -8.14) * mm});
            skLineSegment(sketch, "E3572", {"start": v(36.1, -8.14) * mm, "end": v(36.1, -7.39) * mm});
            skLineSegment(sketch, "E3573", {"start": v(36.1, -7.39) * mm, "end": v(36.1, -6.64) * mm});
            skLineSegment(sketch, "E3574", {"start": v(36.1, -6.64) * mm, "end": v(36.1, -5.9) * mm});
            skLineSegment(sketch, "E3575", {"start": v(36.1, -5.9) * mm, "end": v(36.1, -5.15) * mm});
            skLineSegment(sketch, "E3576", {"start": v(36.1, -5.15) * mm, "end": v(36.13, -5.15) * mm});
            skLineSegment(sketch, "E3577", {"start": v(36.13, -5.15) * mm, "end": v(36.15, -5.15) * mm});
            skLineSegment(sketch, "E3578", {"start": v(36.15, -5.15) * mm, "end": v(36.18, -5.15) * mm});
            skLineSegment(sketch, "E3579", {"start": v(36.18, -5.15) * mm, "end": v(36.2, -5.15) * mm});
            skLineSegment(sketch, "E3580", {"start": v(36.2, -5.15) * mm, "end": v(36.23, -5.15) * mm});
            skLineSegment(sketch, "E3581", {"start": v(36.23, -5.15) * mm, "end": v(36.25, -5.15) * mm});
            skLineSegment(sketch, "E3582", {"start": v(36.25, -5.15) * mm, "end": v(36.28, -5.15) * mm});
            skLineSegment(sketch, "E3583", {"start": v(36.28, -5.15) * mm, "end": v(36.3, -5.15) * mm});
            skLineSegment(sketch, "E3584", {"start": v(36.3, -5.15) * mm, "end": v(36.33, -5.15) * mm});
            skLineSegment(sketch, "E3585", {"start": v(36.33, -5.15) * mm, "end": v(36.35, -5.15) * mm});
            skLineSegment(sketch, "E3586", {"start": v(36.35, -5.15) * mm, "end": v(36.38, -5.15) * mm});
            skLineSegment(sketch, "E3587", {"start": v(36.38, -5.15) * mm, "end": v(36.4, -5.15) * mm});
            skLineSegment(sketch, "E3588", {"start": v(36.4, -5.15) * mm, "end": v(36.43, -5.15) * mm});
            skLineSegment(sketch, "E3589", {"start": v(36.43, -5.15) * mm, "end": v(36.46, -5.15) * mm});
            skLineSegment(sketch, "E3590", {"start": v(36.46, -5.15) * mm, "end": v(36.48, -5.15) * mm});
            skLineSegment(sketch, "E3591", {"start": v(36.48, -5.15) * mm, "end": v(36.5, -5.15) * mm});
            skLineSegment(sketch, "E3592", {"start": v(36.5, -5.15) * mm, "end": v(36.68, -5.16) * mm});
            skLineSegment(sketch, "E3593", {"start": v(36.68, -5.16) * mm, "end": v(36.85, -5.17) * mm});
            skLineSegment(sketch, "E3594", {"start": v(36.85, -5.17) * mm, "end": v(37.01, -5.2) * mm});
            skLineSegment(sketch, "E3595", {"start": v(37.01, -5.2) * mm, "end": v(37.18, -5.23) * mm});
            skLineSegment(sketch, "E3596", {"start": v(37.18, -5.23) * mm, "end": v(37.34, -5.27) * mm});
            skLineSegment(sketch, "E3597", {"start": v(37.34, -5.27) * mm, "end": v(37.5, -5.32) * mm});
            skLineSegment(sketch, "E3598", {"start": v(37.5, -5.32) * mm, "end": v(37.67, -5.39) * mm});
            skLineSegment(sketch, "E3599", {"start": v(37.67, -5.39) * mm, "end": v(37.83, -5.46) * mm});
            skLineSegment(sketch, "E3600", {"start": v(37.83, -5.46) * mm, "end": v(37.99, -5.54) * mm});
            skLineSegment(sketch, "E3601", {"start": v(37.99, -5.54) * mm, "end": v(38.14, -5.63) * mm});
            skLineSegment(sketch, "E3602", {"start": v(38.14, -5.63) * mm, "end": v(38.3, -5.73) * mm});
            skLineSegment(sketch, "E3603", {"start": v(38.3, -5.73) * mm, "end": v(38.45, -5.84) * mm});
            skLineSegment(sketch, "E3604", {"start": v(38.45, -5.84) * mm, "end": v(38.6, -5.96) * mm});
            skLineSegment(sketch, "E3605", {"start": v(38.6, -5.96) * mm, "end": v(38.76, -6.1) * mm});
            skLineSegment(sketch, "E3606", {"start": v(38.76, -6.1) * mm, "end": v(38.9, -6.23) * mm});
            skLineSegment(sketch, "E3607", {"start": v(38.9, -6.23) * mm, "end": v(39.05, -6.38) * mm});
            skLineSegment(sketch, "E3608", {"start": v(39.05, -6.38) * mm, "end": v(39.2, -6.54) * mm});
            skLineSegment(sketch, "E3609", {"start": v(39.2, -6.54) * mm, "end": v(39.34, -6.7) * mm});
            skLineSegment(sketch, "E3610", {"start": v(39.34, -6.7) * mm, "end": v(39.48, -6.88) * mm});
            skLineSegment(sketch, "E3611", {"start": v(39.48, -6.88) * mm, "end": v(39.61, -7.06) * mm});
            skLineSegment(sketch, "E3612", {"start": v(39.61, -7.06) * mm, "end": v(39.74, -7.24) * mm});
            skLineSegment(sketch, "E3613", {"start": v(39.74, -7.24) * mm, "end": v(39.87, -7.44) * mm});
            skLineSegment(sketch, "E3614", {"start": v(39.87, -7.44) * mm, "end": v(40, -7.64) * mm});
            skLineSegment(sketch, "E3615", {"start": v(40, -7.64) * mm, "end": v(40.11, -7.85) * mm});
            skLineSegment(sketch, "E3616", {"start": v(40.11, -7.85) * mm, "end": v(40.23, -8.06) * mm});
            skLineSegment(sketch, "E3617", {"start": v(40.23, -8.06) * mm, "end": v(40.35, -8.28) * mm});
            skLineSegment(sketch, "E3618", {"start": v(40.35, -8.28) * mm, "end": v(40.46, -8.51) * mm});
            skLineSegment(sketch, "E3619", {"start": v(40.46, -8.51) * mm, "end": v(40.56, -8.75) * mm});
            skLineSegment(sketch, "E3620", {"start": v(40.56, -8.75) * mm, "end": v(40.67, -9) * mm});
            skLineSegment(sketch, "E3621", {"start": v(40.67, -9) * mm, "end": v(40.77, -9.25) * mm});
            skLineSegment(sketch, "E3622", {"start": v(40.77, -9.25) * mm, "end": v(40.87, -9.5) * mm});
            skLineSegment(sketch, "E3623", {"start": v(40.87, -9.5) * mm, "end": v(40.96, -9.77) * mm});
            skLineSegment(sketch, "E3624", {"start": v(40.96, -9.77) * mm, "end": v(41.12, -10.23) * mm});
            skLineSegment(sketch, "E3625", {"start": v(41.12, -10.23) * mm, "end": v(41.28, -10.68) * mm});
            skLineSegment(sketch, "E3626", {"start": v(41.28, -10.68) * mm, "end": v(41.43, -11.14) * mm});
            skLineSegment(sketch, "E3627", {"start": v(41.43, -11.14) * mm, "end": v(41.6, -11.6) * mm});
            skLineSegment(sketch, "E3628", {"start": v(41.6, -11.6) * mm, "end": v(41.75, -12.06) * mm});
            skLineSegment(sketch, "E3629", {"start": v(41.75, -12.06) * mm, "end": v(41.9, -12.51) * mm});
            skLineSegment(sketch, "E3630", {"start": v(41.9, -12.51) * mm, "end": v(42.07, -12.97) * mm});
            skLineSegment(sketch, "E3631", {"start": v(42.07, -12.97) * mm, "end": v(42.23, -13.43) * mm});
            skLineSegment(sketch, "E3632", {"start": v(42.23, -13.43) * mm, "end": v(42.38, -13.89) * mm});
            skLineSegment(sketch, "E3633", {"start": v(42.38, -13.89) * mm, "end": v(42.54, -14.34) * mm});
            skLineSegment(sketch, "E3634", {"start": v(42.54, -14.34) * mm, "end": v(42.7, -14.8) * mm});
            skLineSegment(sketch, "E3635", {"start": v(42.7, -14.8) * mm, "end": v(42.86, -15.26) * mm});
            skLineSegment(sketch, "E3636", {"start": v(42.86, -15.26) * mm, "end": v(43.02, -15.72) * mm});
            skLineSegment(sketch, "E3637", {"start": v(43.02, -15.72) * mm, "end": v(43.18, -16.17) * mm});
            skLineSegment(sketch, "E3638", {"start": v(43.18, -16.17) * mm, "end": v(43.33, -16.63) * mm});
            skLineSegment(sketch, "E3639", {"start": v(43.33, -16.63) * mm, "end": v(43.34, -16.65) * mm});
            skLineSegment(sketch, "E3640", {"start": v(43.34, -16.65) * mm, "end": v(42.02, -16.65) * mm});
            skLineSegment(sketch, "E3641", {"start": v(59.3, -16.65) * mm, "end": v(58.66, -16.65) * mm});
            skLineSegment(sketch, "E3642", {"start": v(58.66, -16.65) * mm, "end": v(58.02, -16.65) * mm});
            skLineSegment(sketch, "E3643", {"start": v(58.02, -16.65) * mm, "end": v(57.38, -16.65) * mm});
            skLineSegment(sketch, "E3644", {"start": v(57.38, -16.65) * mm, "end": v(56.74, -16.65) * mm});
            skLineSegment(sketch, "E3645", {"start": v(56.74, -16.65) * mm, "end": v(56.1, -16.65) * mm});
            skLineSegment(sketch, "E3646", {"start": v(56.1, -16.65) * mm, "end": v(55.46, -16.65) * mm});
            skLineSegment(sketch, "E3647", {"start": v(55.46, -16.65) * mm, "end": v(54.86, -16.65) * mm});
            skLineSegment(sketch, "E3648", {"start": v(54.86, -16.65) * mm, "end": v(54.82, -16.55) * mm});
            skLineSegment(sketch, "E3649", {"start": v(54.82, -16.55) * mm, "end": v(54.61, -16) * mm});
            skLineSegment(sketch, "E3650", {"start": v(54.61, -16) * mm, "end": v(54.4, -15.47) * mm});
            skLineSegment(sketch, "E3651", {"start": v(54.4, -15.47) * mm, "end": v(54.2, -14.93) * mm});
            skLineSegment(sketch, "E3652", {"start": v(54.2, -14.93) * mm, "end": v(53.98, -14.39) * mm});
            skLineSegment(sketch, "E3653", {"start": v(53.98, -14.39) * mm, "end": v(53.78, -13.85) * mm});
            skLineSegment(sketch, "E3654", {"start": v(53.78, -13.85) * mm, "end": v(53.57, -13.3) * mm});
            skLineSegment(sketch, "E3655", {"start": v(53.57, -13.3) * mm, "end": v(53.36, -12.77) * mm});
            skLineSegment(sketch, "E3656", {"start": v(53.36, -12.77) * mm, "end": v(53.15, -12.23) * mm});
            skLineSegment(sketch, "E3657", {"start": v(53.15, -12.23) * mm, "end": v(52.94, -11.69) * mm});
            skLineSegment(sketch, "E3658", {"start": v(52.94, -11.69) * mm, "end": v(52.73, -11.15) * mm});
            skLineSegment(sketch, "E3659", {"start": v(52.73, -11.15) * mm, "end": v(52.52, -10.6) * mm});
            skLineSegment(sketch, "E3660", {"start": v(52.52, -10.6) * mm, "end": v(52.31, -10.06) * mm});
            skLineSegment(sketch, "E3661", {"start": v(52.31, -10.06) * mm, "end": v(52.1, -9.52) * mm});
            skLineSegment(sketch, "E3662", {"start": v(52.1, -9.52) * mm, "end": v(51.9, -8.98) * mm});
            skLineSegment(sketch, "E3663", {"start": v(51.9, -8.98) * mm, "end": v(51.69, -8.44) * mm});
            skLineSegment(sketch, "E3664", {"start": v(51.69, -8.44) * mm, "end": v(51.54, -8.08) * mm});
            skLineSegment(sketch, "E3665", {"start": v(51.54, -8.08) * mm, "end": v(51.4, -7.73) * mm});
            skLineSegment(sketch, "E3666", {"start": v(51.4, -7.73) * mm, "end": v(51.25, -7.4) * mm});
            skLineSegment(sketch, "E3667", {"start": v(51.25, -7.4) * mm, "end": v(51.1, -7.07) * mm});
            skLineSegment(sketch, "E3668", {"start": v(51.1, -7.07) * mm, "end": v(50.95, -6.75) * mm});
            skLineSegment(sketch, "E3669", {"start": v(50.95, -6.75) * mm, "end": v(50.8, -6.44) * mm});
            skLineSegment(sketch, "E3670", {"start": v(50.8, -6.44) * mm, "end": v(50.64, -6.15) * mm});
            skLineSegment(sketch, "E3671", {"start": v(50.64, -6.15) * mm, "end": v(50.48, -5.87) * mm});
            skLineSegment(sketch, "E3672", {"start": v(50.48, -5.87) * mm, "end": v(50.32, -5.6) * mm});
            skLineSegment(sketch, "E3673", {"start": v(50.32, -5.6) * mm, "end": v(50.15, -5.34) * mm});
            skLineSegment(sketch, "E3674", {"start": v(50.15, -5.34) * mm, "end": v(49.98, -5.09) * mm});
            skLineSegment(sketch, "E3675", {"start": v(49.98, -5.09) * mm, "end": v(49.82, -4.85) * mm});
            skLineSegment(sketch, "E3676", {"start": v(49.82, -4.85) * mm, "end": v(49.64, -4.62) * mm});
            skLineSegment(sketch, "E3677", {"start": v(49.64, -4.62) * mm, "end": v(49.47, -4.41) * mm});
            skLineSegment(sketch, "E3678", {"start": v(49.47, -4.41) * mm, "end": v(49.3, -4.2) * mm});
            skLineSegment(sketch, "E3679", {"start": v(49.3, -4.2) * mm, "end": v(49.12, -4.01) * mm});
            skLineSegment(sketch, "E3680", {"start": v(49.12, -4.01) * mm, "end": v(48.94, -3.83) * mm});
            skLineSegment(sketch, "E3681", {"start": v(48.94, -3.83) * mm, "end": v(48.75, -3.65) * mm});
            skLineSegment(sketch, "E3682", {"start": v(48.75, -3.65) * mm, "end": v(48.56, -3.48) * mm});
            skLineSegment(sketch, "E3683", {"start": v(48.56, -3.48) * mm, "end": v(48.36, -3.32) * mm});
            skLineSegment(sketch, "E3684", {"start": v(48.36, -3.32) * mm, "end": v(48.15, -3.16) * mm});
            skLineSegment(sketch, "E3685", {"start": v(48.15, -3.16) * mm, "end": v(47.94, -3.01) * mm});
            skLineSegment(sketch, "E3686", {"start": v(47.94, -3.01) * mm, "end": v(47.73, -2.87) * mm});
            skLineSegment(sketch, "E3687", {"start": v(47.73, -2.87) * mm, "end": v(47.5, -2.73) * mm});
            skLineSegment(sketch, "E3688", {"start": v(47.5, -2.73) * mm, "end": v(47.28, -2.6) * mm});
            skLineSegment(sketch, "E3689", {"start": v(47.28, -2.6) * mm, "end": v(47.04, -2.47) * mm});
            skLineSegment(sketch, "E3690", {"start": v(47.04, -2.47) * mm, "end": v(46.8, -2.35) * mm});
            skLineSegment(sketch, "E3691", {"start": v(46.8, -2.35) * mm, "end": v(46.56, -2.24) * mm});
            skLineSegment(sketch, "E3692", {"start": v(46.56, -2.24) * mm, "end": v(46.31, -2.14) * mm});
            skLineSegment(sketch, "E3693", {"start": v(46.31, -2.14) * mm, "end": v(46.06, -2.04) * mm});
            skLineSegment(sketch, "E3694", {"start": v(46.06, -2.04) * mm, "end": v(45.8, -1.95) * mm});
            skLineSegment(sketch, "E3695", {"start": v(45.8, -1.95) * mm, "end": v(45.53, -1.86) * mm});
            skLineSegment(sketch, "E3696", {"start": v(45.53, -1.86) * mm, "end": v(45.53, -1.85) * mm});
            skLineSegment(sketch, "E3697", {"start": v(45.53, -1.85) * mm, "end": v(45.53, -1.85) * mm});
            skLineSegment(sketch, "E3698", {"start": v(45.53, -1.85) * mm, "end": v(45.53, -1.84) * mm});
            skLineSegment(sketch, "E3699", {"start": v(45.53, -1.84) * mm, "end": v(45.53, -1.84) * mm});
            skLineSegment(sketch, "E3700", {"start": v(45.53, -1.84) * mm, "end": v(45.53, -1.83) * mm});
            skLineSegment(sketch, "E3701", {"start": v(45.53, -1.83) * mm, "end": v(45.53, -1.82) * mm});
            skLineSegment(sketch, "E3702", {"start": v(45.53, -1.82) * mm, "end": v(45.53, -1.82) * mm});
            skLineSegment(sketch, "E3703", {"start": v(45.53, -1.82) * mm, "end": v(45.53, -1.81) * mm});
            skLineSegment(sketch, "E3704", {"start": v(45.53, -1.81) * mm, "end": v(45.53, -1.8) * mm});
            skLineSegment(sketch, "E3705", {"start": v(45.53, -1.8) * mm, "end": v(45.53, -1.8) * mm});
            skLineSegment(sketch, "E3706", {"start": v(45.53, -1.8) * mm, "end": v(45.53, -1.79) * mm});
            skLineSegment(sketch, "E3707", {"start": v(45.53, -1.79) * mm, "end": v(45.53, -1.78) * mm});
            skLineSegment(sketch, "E3708", {"start": v(45.53, -1.78) * mm, "end": v(45.53, -1.78) * mm});
            skLineSegment(sketch, "E3709", {"start": v(45.53, -1.78) * mm, "end": v(45.53, -1.77) * mm});
            skLineSegment(sketch, "E3710", {"start": v(45.53, -1.77) * mm, "end": v(45.53, -1.76) * mm});
            skLineSegment(sketch, "E3711", {"start": v(45.53, -1.76) * mm, "end": v(46.01, -1.63) * mm});
            skLineSegment(sketch, "E3712", {"start": v(46.01, -1.63) * mm, "end": v(46.48, -1.48) * mm});
            skLineSegment(sketch, "E3713", {"start": v(46.48, -1.48) * mm, "end": v(46.93, -1.32) * mm});
            skLineSegment(sketch, "E3714", {"start": v(46.93, -1.32) * mm, "end": v(47.36, -1.15) * mm});
            skLineSegment(sketch, "E3715", {"start": v(47.36, -1.15) * mm, "end": v(47.78, -0.97) * mm});
            skLineSegment(sketch, "E3716", {"start": v(47.78, -0.97) * mm, "end": v(48.19, -0.78) * mm});
            skLineSegment(sketch, "E3717", {"start": v(48.19, -0.78) * mm, "end": v(48.58, -0.58) * mm});
            skLineSegment(sketch, "E3718", {"start": v(48.58, -0.58) * mm, "end": v(48.96, -0.37) * mm});
            skLineSegment(sketch, "E3719", {"start": v(48.96, -0.37) * mm, "end": v(49.32, -0.15) * mm});
            skLineSegment(sketch, "E3720", {"start": v(49.32, -0.15) * mm, "end": v(49.66, 0.08) * mm});
            skLineSegment(sketch, "E3721", {"start": v(49.66, 0.08) * mm, "end": v(50, 0.32) * mm});
            skLineSegment(sketch, "E3722", {"start": v(50, 0.32) * mm, "end": v(50.3, 0.57) * mm});
            skLineSegment(sketch, "E3723", {"start": v(50.3, 0.57) * mm, "end": v(50.6, 0.83) * mm});
            skLineSegment(sketch, "E3724", {"start": v(50.6, 0.83) * mm, "end": v(50.9, 1.1) * mm});
            skLineSegment(sketch, "E3725", {"start": v(50.9, 1.1) * mm, "end": v(51.16, 1.38) * mm});
            skLineSegment(sketch, "E3726", {"start": v(51.16, 1.38) * mm, "end": v(51.42, 1.67) * mm});
            skLineSegment(sketch, "E3727", {"start": v(51.42, 1.67) * mm, "end": v(51.65, 1.97) * mm});
            skLineSegment(sketch, "E3728", {"start": v(51.65, 1.97) * mm, "end": v(51.88, 2.28) * mm});
            skLineSegment(sketch, "E3729", {"start": v(51.88, 2.28) * mm, "end": v(52.09, 2.6) * mm});
            skLineSegment(sketch, "E3730", {"start": v(52.09, 2.6) * mm, "end": v(52.28, 2.93) * mm});
            skLineSegment(sketch, "E3731", {"start": v(52.28, 2.93) * mm, "end": v(52.46, 3.26) * mm});
            skLineSegment(sketch, "E3732", {"start": v(52.46, 3.26) * mm, "end": v(52.62, 3.6) * mm});
            skLineSegment(sketch, "E3733", {"start": v(52.62, 3.6) * mm, "end": v(52.77, 3.96) * mm});
            skLineSegment(sketch, "E3734", {"start": v(52.77, 3.96) * mm, "end": v(52.9, 4.32) * mm});
            skLineSegment(sketch, "E3735", {"start": v(52.9, 4.32) * mm, "end": v(53.01, 4.7) * mm});
            skLineSegment(sketch, "E3736", {"start": v(53.01, 4.7) * mm, "end": v(53.12, 5.07) * mm});
            skLineSegment(sketch, "E3737", {"start": v(53.12, 5.07) * mm, "end": v(53.2, 5.46) * mm});
            skLineSegment(sketch, "E3738", {"start": v(53.2, 5.46) * mm, "end": v(53.27, 5.86) * mm});
            skLineSegment(sketch, "E3739", {"start": v(53.27, 5.86) * mm, "end": v(53.32, 6.27) * mm});
            skLineSegment(sketch, "E3740", {"start": v(53.32, 6.27) * mm, "end": v(53.36, 6.69) * mm});
            skLineSegment(sketch, "E3741", {"start": v(53.36, 6.69) * mm, "end": v(53.39, 7.11) * mm});
            skLineSegment(sketch, "E3742", {"start": v(53.39, 7.11) * mm, "end": v(53.4, 7.54) * mm});
            skLineSegment(sketch, "E3743", {"start": v(53.4, 7.54) * mm, "end": v(53.38, 8.12) * mm});
            skLineSegment(sketch, "E3744", {"start": v(53.38, 8.12) * mm, "end": v(53.34, 8.67) * mm});
            skLineSegment(sketch, "E3745", {"start": v(53.34, 8.67) * mm, "end": v(53.27, 9.21) * mm});
            skLineSegment(sketch, "E3746", {"start": v(53.27, 9.21) * mm, "end": v(53.2, 9.63) * mm});
            skLineSegment(sketch, "E3747", {"start": v(53.2, 9.63) * mm, "end": v(53.72, 8.5) * mm});
            skLineSegment(sketch, "E3748", {"start": v(53.72, 8.5) * mm, "end": v(54.38, 7.11) * mm});
            skLineSegment(sketch, "E3749", {"start": v(54.38, 7.11) * mm, "end": v(55.03, 5.72) * mm});
            skLineSegment(sketch, "E3750", {"start": v(55.03, 5.72) * mm, "end": v(55.69, 4.33) * mm});
            skLineSegment(sketch, "E3751", {"start": v(55.69, 4.33) * mm, "end": v(56.34, 2.93) * mm});
            skLineSegment(sketch, "E3752", {"start": v(56.34, 2.93) * mm, "end": v(57, 1.54) * mm});
            skLineSegment(sketch, "E3753", {"start": v(57, 1.54) * mm, "end": v(57.65, 0.14) * mm});
            skLineSegment(sketch, "E3754", {"start": v(57.65, 0.14) * mm, "end": v(58.3, -1.25) * mm});
            skLineSegment(sketch, "E3755", {"start": v(58.3, -1.25) * mm, "end": v(58.96, -2.65) * mm});
            skLineSegment(sketch, "E3756", {"start": v(58.96, -2.65) * mm, "end": v(59.61, -4.04) * mm});
            skLineSegment(sketch, "E3757", {"start": v(59.61, -4.04) * mm, "end": v(60.27, -5.44) * mm});
            skLineSegment(sketch, "E3758", {"start": v(60.27, -5.44) * mm, "end": v(60.27, -6.16) * mm});
            skLineSegment(sketch, "E3759", {"start": v(60.27, -6.16) * mm, "end": v(60.27, -6.9) * mm});
            skLineSegment(sketch, "E3760", {"start": v(60.27, -6.9) * mm, "end": v(60.27, -7.62) * mm});
            skLineSegment(sketch, "E3761", {"start": v(60.27, -7.62) * mm, "end": v(60.27, -8.35) * mm});
            skLineSegment(sketch, "E3762", {"start": v(60.27, -8.35) * mm, "end": v(60.27, -9.08) * mm});
            skLineSegment(sketch, "E3763", {"start": v(60.27, -9.08) * mm, "end": v(60.27, -9.8) * mm});
            skLineSegment(sketch, "E3764", {"start": v(60.27, -9.8) * mm, "end": v(60.27, -10.53) * mm});
            skLineSegment(sketch, "E3765", {"start": v(60.27, -10.53) * mm, "end": v(60.27, -11.26) * mm});
            skLineSegment(sketch, "E3766", {"start": v(60.27, -11.26) * mm, "end": v(60.27, -12) * mm});
            skLineSegment(sketch, "E3767", {"start": v(60.27, -12) * mm, "end": v(60.27, -12.72) * mm});
            skLineSegment(sketch, "E3768", {"start": v(60.27, -12.72) * mm, "end": v(60.27, -13.45) * mm});
            skLineSegment(sketch, "E3769", {"start": v(60.27, -13.45) * mm, "end": v(60.27, -14.18) * mm});
            skLineSegment(sketch, "E3770", {"start": v(60.27, -14.18) * mm, "end": v(60.27, -14.9) * mm});
            skLineSegment(sketch, "E3771", {"start": v(60.27, -14.9) * mm, "end": v(60.27, -15.63) * mm});
            skLineSegment(sketch, "E3772", {"start": v(60.27, -15.63) * mm, "end": v(60.27, -16.36) * mm});
            skLineSegment(sketch, "E3773", {"start": v(60.27, -16.36) * mm, "end": v(60.27, -16.65) * mm});
            skLineSegment(sketch, "E3774", {"start": v(60.27, -16.65) * mm, "end": v(59.94, -16.65) * mm});
            skLineSegment(sketch, "E3775", {"start": v(59.94, -16.65) * mm, "end": v(59.3, -16.65) * mm});
            skLineSegment(sketch, "E3776", {"start": v(102.76, -46.14) * mm, "end": v(102.74, -45.9) * mm});
            skLineSegment(sketch, "E3777", {"start": v(102.74, -45.9) * mm, "end": v(102.71, -45.65) * mm});
            skLineSegment(sketch, "E3778", {"start": v(102.71, -45.65) * mm, "end": v(102.67, -45.4) * mm});
            skLineSegment(sketch, "E3779", {"start": v(102.67, -45.4) * mm, "end": v(102.62, -45.18) * mm});
            skLineSegment(sketch, "E3780", {"start": v(102.62, -45.18) * mm, "end": v(102.55, -44.95) * mm});
            skLineSegment(sketch, "E3781", {"start": v(102.55, -44.95) * mm, "end": v(102.47, -44.73) * mm});
            skLineSegment(sketch, "E3782", {"start": v(102.47, -44.73) * mm, "end": v(102.38, -44.52) * mm});
            skLineSegment(sketch, "E3783", {"start": v(102.38, -44.52) * mm, "end": v(102.28, -44.3) * mm});
            skLineSegment(sketch, "E3784", {"start": v(102.28, -44.3) * mm, "end": v(102.16, -44.1) * mm});
            skLineSegment(sketch, "E3785", {"start": v(102.16, -44.1) * mm, "end": v(102.03, -43.91) * mm});
            skLineSegment(sketch, "E3786", {"start": v(102.03, -43.91) * mm, "end": v(101.9, -43.72) * mm});
            skLineSegment(sketch, "E3787", {"start": v(101.9, -43.72) * mm, "end": v(101.74, -43.54) * mm});
            skLineSegment(sketch, "E3788", {"start": v(101.74, -43.54) * mm, "end": v(101.58, -43.36) * mm});
            skLineSegment(sketch, "E3789", {"start": v(101.58, -43.36) * mm, "end": v(101.4, -43.2) * mm});
            skLineSegment(sketch, "E3790", {"start": v(101.4, -43.2) * mm, "end": v(101.22, -43.03) * mm});
            skLineSegment(sketch, "E3791", {"start": v(101.22, -43.03) * mm, "end": v(101.02, -42.87) * mm});
            skLineSegment(sketch, "E3792", {"start": v(101.02, -42.87) * mm, "end": v(100.81, -42.72) * mm});
            skLineSegment(sketch, "E3793", {"start": v(100.81, -42.72) * mm, "end": v(100.6, -42.59) * mm});
            skLineSegment(sketch, "E3794", {"start": v(100.6, -42.59) * mm, "end": v(100.38, -42.46) * mm});
            skLineSegment(sketch, "E3795", {"start": v(100.38, -42.46) * mm, "end": v(100.15, -42.35) * mm});
            skLineSegment(sketch, "E3796", {"start": v(100.15, -42.35) * mm, "end": v(99.92, -42.24) * mm});
            skLineSegment(sketch, "E3797", {"start": v(99.92, -42.24) * mm, "end": v(99.67, -42.14) * mm});
            skLineSegment(sketch, "E3798", {"start": v(99.67, -42.14) * mm, "end": v(99.42, -42.06) * mm});
            skLineSegment(sketch, "E3799", {"start": v(99.42, -42.06) * mm, "end": v(99.17, -41.98) * mm});
            skLineSegment(sketch, "E3800", {"start": v(99.17, -41.98) * mm, "end": v(98.9, -41.92) * mm});
            skLineSegment(sketch, "E3801", {"start": v(98.9, -41.92) * mm, "end": v(98.63, -41.86) * mm});
            skLineSegment(sketch, "E3802", {"start": v(98.63, -41.86) * mm, "end": v(98.35, -41.82) * mm});
            skLineSegment(sketch, "E3803", {"start": v(98.35, -41.82) * mm, "end": v(98.06, -41.78) * mm});
            skLineSegment(sketch, "E3804", {"start": v(98.06, -41.78) * mm, "end": v(97.77, -41.76) * mm});
            skLineSegment(sketch, "E3805", {"start": v(97.77, -41.76) * mm, "end": v(97.46, -41.74) * mm});
            skLineSegment(sketch, "E3806", {"start": v(97.46, -41.74) * mm, "end": v(97.15, -41.74) * mm});
            skLineSegment(sketch, "E3807", {"start": v(97.15, -41.74) * mm, "end": v(96.83, -41.74) * mm});
            skLineSegment(sketch, "E3808", {"start": v(96.83, -41.74) * mm, "end": v(96.52, -41.76) * mm});
            skLineSegment(sketch, "E3809", {"start": v(96.52, -41.76) * mm, "end": v(96.22, -41.78) * mm});
            skLineSegment(sketch, "E3810", {"start": v(96.22, -41.78) * mm, "end": v(95.93, -41.82) * mm});
            skLineSegment(sketch, "E3811", {"start": v(95.93, -41.82) * mm, "end": v(95.64, -41.86) * mm});
            skLineSegment(sketch, "E3812", {"start": v(95.64, -41.86) * mm, "end": v(95.37, -41.92) * mm});
            skLineSegment(sketch, "E3813", {"start": v(95.37, -41.92) * mm, "end": v(95.1, -41.98) * mm});
            skLineSegment(sketch, "E3814", {"start": v(95.1, -41.98) * mm, "end": v(94.84, -42.06) * mm});
            skLineSegment(sketch, "E3815", {"start": v(94.84, -42.06) * mm, "end": v(94.58, -42.14) * mm});
            skLineSegment(sketch, "E3816", {"start": v(94.58, -42.14) * mm, "end": v(94.34, -42.24) * mm});
            skLineSegment(sketch, "E3817", {"start": v(94.34, -42.24) * mm, "end": v(94.1, -42.35) * mm});
            skLineSegment(sketch, "E3818", {"start": v(94.1, -42.35) * mm, "end": v(93.87, -42.46) * mm});
            skLineSegment(sketch, "E3819", {"start": v(93.87, -42.46) * mm, "end": v(93.65, -42.59) * mm});
            skLineSegment(sketch, "E3820", {"start": v(93.65, -42.59) * mm, "end": v(93.44, -42.72) * mm});
            skLineSegment(sketch, "E3821", {"start": v(93.44, -42.72) * mm, "end": v(93.24, -42.87) * mm});
            skLineSegment(sketch, "E3822", {"start": v(93.24, -42.87) * mm, "end": v(93.04, -43.03) * mm});
            skLineSegment(sketch, "E3823", {"start": v(93.04, -43.03) * mm, "end": v(92.86, -43.2) * mm});
            skLineSegment(sketch, "E3824", {"start": v(92.86, -43.2) * mm, "end": v(92.69, -43.36) * mm});
            skLineSegment(sketch, "E3825", {"start": v(92.69, -43.36) * mm, "end": v(92.53, -43.54) * mm});
            skLineSegment(sketch, "E3826", {"start": v(92.53, -43.54) * mm, "end": v(92.38, -43.72) * mm});
            skLineSegment(sketch, "E3827", {"start": v(92.38, -43.72) * mm, "end": v(92.24, -43.91) * mm});
            skLineSegment(sketch, "E3828", {"start": v(92.24, -43.91) * mm, "end": v(92.11, -44.1) * mm});
            skLineSegment(sketch, "E3829", {"start": v(92.11, -44.1) * mm, "end": v(92, -44.3) * mm});
            skLineSegment(sketch, "E3830", {"start": v(92, -44.3) * mm, "end": v(91.9, -44.52) * mm});
            skLineSegment(sketch, "E3831", {"start": v(91.9, -44.52) * mm, "end": v(91.8, -44.73) * mm});
            skLineSegment(sketch, "E3832", {"start": v(91.8, -44.73) * mm, "end": v(91.73, -44.95) * mm});
            skLineSegment(sketch, "E3833", {"start": v(91.73, -44.95) * mm, "end": v(91.67, -45.18) * mm});
            skLineSegment(sketch, "E3834", {"start": v(91.67, -45.18) * mm, "end": v(91.61, -45.4) * mm});
            skLineSegment(sketch, "E3835", {"start": v(91.61, -45.4) * mm, "end": v(91.57, -45.65) * mm});
            skLineSegment(sketch, "E3836", {"start": v(91.57, -45.65) * mm, "end": v(91.54, -45.9) * mm});
            skLineSegment(sketch, "E3837", {"start": v(91.54, -45.9) * mm, "end": v(91.52, -46.14) * mm});
            skLineSegment(sketch, "E3838", {"start": v(91.52, -46.14) * mm, "end": v(91.52, -46.4) * mm});
            skLineSegment(sketch, "E3839", {"start": v(91.52, -46.4) * mm, "end": v(91.52, -46.66) * mm});
            skLineSegment(sketch, "E3840", {"start": v(91.52, -46.66) * mm, "end": v(91.54, -46.9) * mm});
            skLineSegment(sketch, "E3841", {"start": v(91.54, -46.9) * mm, "end": v(91.57, -47.15) * mm});
            skLineSegment(sketch, "E3842", {"start": v(91.57, -47.15) * mm, "end": v(91.61, -47.39) * mm});
            skLineSegment(sketch, "E3843", {"start": v(91.61, -47.39) * mm, "end": v(91.67, -47.62) * mm});
            skLineSegment(sketch, "E3844", {"start": v(91.67, -47.62) * mm, "end": v(91.74, -47.85) * mm});
            skLineSegment(sketch, "E3845", {"start": v(91.74, -47.85) * mm, "end": v(91.82, -48.07) * mm});
            skLineSegment(sketch, "E3846", {"start": v(91.82, -48.07) * mm, "end": v(91.91, -48.3) * mm});
            skLineSegment(sketch, "E3847", {"start": v(91.91, -48.3) * mm, "end": v(92.01, -48.5) * mm});
            skLineSegment(sketch, "E3848", {"start": v(92.01, -48.5) * mm, "end": v(92.13, -48.7) * mm});
            skLineSegment(sketch, "E3849", {"start": v(92.13, -48.7) * mm, "end": v(92.26, -48.91) * mm});
            skLineSegment(sketch, "E3850", {"start": v(92.26, -48.91) * mm, "end": v(92.4, -49.1) * mm});
            skLineSegment(sketch, "E3851", {"start": v(92.4, -49.1) * mm, "end": v(92.56, -49.3) * mm});
            skLineSegment(sketch, "E3852", {"start": v(92.56, -49.3) * mm, "end": v(92.72, -49.48) * mm});
            skLineSegment(sketch, "E3853", {"start": v(92.72, -49.48) * mm, "end": v(92.9, -49.66) * mm});
            skLineSegment(sketch, "E3854", {"start": v(92.9, -49.66) * mm, "end": v(93.1, -49.84) * mm});
            skLineSegment(sketch, "E3855", {"start": v(93.1, -49.84) * mm, "end": v(93.3, -50) * mm});
            skLineSegment(sketch, "E3856", {"start": v(93.3, -50) * mm, "end": v(93.5, -50.16) * mm});
            skLineSegment(sketch, "E3857", {"start": v(93.5, -50.16) * mm, "end": v(93.71, -50.3) * mm});
            skLineSegment(sketch, "E3858", {"start": v(93.71, -50.3) * mm, "end": v(93.94, -50.44) * mm});
            skLineSegment(sketch, "E3859", {"start": v(93.94, -50.44) * mm, "end": v(94.17, -50.56) * mm});
            skLineSegment(sketch, "E3860", {"start": v(94.17, -50.56) * mm, "end": v(94.4, -50.67) * mm});
            skLineSegment(sketch, "E3861", {"start": v(94.4, -50.67) * mm, "end": v(94.64, -50.78) * mm});
            skLineSegment(sketch, "E3862", {"start": v(94.64, -50.78) * mm, "end": v(94.9, -50.87) * mm});
            skLineSegment(sketch, "E3863", {"start": v(94.9, -50.87) * mm, "end": v(95.15, -50.95) * mm});
            skLineSegment(sketch, "E3864", {"start": v(95.15, -50.95) * mm, "end": v(95.42, -51.02) * mm});
            skLineSegment(sketch, "E3865", {"start": v(95.42, -51.02) * mm, "end": v(95.69, -51.08) * mm});
            skLineSegment(sketch, "E3866", {"start": v(95.69, -51.08) * mm, "end": v(95.97, -51.12) * mm});
            skLineSegment(sketch, "E3867", {"start": v(95.97, -51.12) * mm, "end": v(96.25, -51.16) * mm});
            skLineSegment(sketch, "E3868", {"start": v(96.25, -51.16) * mm, "end": v(96.55, -51.19) * mm});
            skLineSegment(sketch, "E3869", {"start": v(96.55, -51.19) * mm, "end": v(96.85, -51.2) * mm});
            skLineSegment(sketch, "E3870", {"start": v(96.85, -51.2) * mm, "end": v(97.15, -51.21) * mm});
            skLineSegment(sketch, "E3871", {"start": v(97.15, -51.21) * mm, "end": v(97.47, -51.2) * mm});
            skLineSegment(sketch, "E3872", {"start": v(97.47, -51.2) * mm, "end": v(97.78, -51.19) * mm});
            skLineSegment(sketch, "E3873", {"start": v(97.78, -51.19) * mm, "end": v(98.08, -51.16) * mm});
            skLineSegment(sketch, "E3874", {"start": v(98.08, -51.16) * mm, "end": v(98.37, -51.13) * mm});
            skLineSegment(sketch, "E3875", {"start": v(98.37, -51.13) * mm, "end": v(98.65, -51.08) * mm});
            skLineSegment(sketch, "E3876", {"start": v(98.65, -51.08) * mm, "end": v(98.93, -51.02) * mm});
            skLineSegment(sketch, "E3877", {"start": v(98.93, -51.02) * mm, "end": v(99.2, -50.95) * mm});
            skLineSegment(sketch, "E3878", {"start": v(99.2, -50.95) * mm, "end": v(99.45, -50.87) * mm});
            skLineSegment(sketch, "E3879", {"start": v(99.45, -50.87) * mm, "end": v(99.7, -50.78) * mm});
            skLineSegment(sketch, "E3880", {"start": v(99.7, -50.78) * mm, "end": v(99.95, -50.68) * mm});
            skLineSegment(sketch, "E3881", {"start": v(99.95, -50.68) * mm, "end": v(100.18, -50.57) * mm});
            skLineSegment(sketch, "E3882", {"start": v(100.18, -50.57) * mm, "end": v(100.41, -50.45) * mm});
            skLineSegment(sketch, "E3883", {"start": v(100.41, -50.45) * mm, "end": v(100.63, -50.32) * mm});
            skLineSegment(sketch, "E3884", {"start": v(100.63, -50.32) * mm, "end": v(100.84, -50.18) * mm});
            skLineSegment(sketch, "E3885", {"start": v(100.84, -50.18) * mm, "end": v(101.04, -50.02) * mm});
            skLineSegment(sketch, "E3886", {"start": v(101.04, -50.02) * mm, "end": v(101.24, -49.86) * mm});
            skLineSegment(sketch, "E3887", {"start": v(101.24, -49.86) * mm, "end": v(101.42, -49.69) * mm});
            skLineSegment(sketch, "E3888", {"start": v(101.42, -49.69) * mm, "end": v(101.6, -49.51) * mm});
            skLineSegment(sketch, "E3889", {"start": v(101.6, -49.51) * mm, "end": v(101.76, -49.33) * mm});
            skLineSegment(sketch, "E3890", {"start": v(101.76, -49.33) * mm, "end": v(101.9, -49.14) * mm});
            skLineSegment(sketch, "E3891", {"start": v(101.9, -49.14) * mm, "end": v(102.04, -48.94) * mm});
            skLineSegment(sketch, "E3892", {"start": v(102.04, -48.94) * mm, "end": v(102.17, -48.74) * mm});
            skLineSegment(sketch, "E3893", {"start": v(102.17, -48.74) * mm, "end": v(102.28, -48.53) * mm});
            skLineSegment(sketch, "E3894", {"start": v(102.28, -48.53) * mm, "end": v(102.39, -48.32) * mm});
            skLineSegment(sketch, "E3895", {"start": v(102.39, -48.32) * mm, "end": v(102.47, -48.1) * mm});
            skLineSegment(sketch, "E3896", {"start": v(102.47, -48.1) * mm, "end": v(102.55, -47.88) * mm});
            skLineSegment(sketch, "E3897", {"start": v(102.55, -47.88) * mm, "end": v(102.62, -47.65) * mm});
            skLineSegment(sketch, "E3898", {"start": v(102.62, -47.65) * mm, "end": v(102.67, -47.4) * mm});
            skLineSegment(sketch, "E3899", {"start": v(102.67, -47.4) * mm, "end": v(102.71, -47.17) * mm});
            skLineSegment(sketch, "E3900", {"start": v(102.71, -47.17) * mm, "end": v(102.74, -46.92) * mm});
            skLineSegment(sketch, "E3901", {"start": v(102.74, -46.92) * mm, "end": v(102.76, -46.66) * mm});
            skLineSegment(sketch, "E3902", {"start": v(102.76, -46.66) * mm, "end": v(102.77, -46.4) * mm});
            skLineSegment(sketch, "E3903", {"start": v(102.77, -46.4) * mm, "end": v(102.76, -46.14) * mm});
            skSolve(sketch);
        }
        {
            var Q0;
            Q0 = qSketchRegion(id + "F1", true);
            extrude(context, id + "F2", {"entities" : qUnion([Q0]), "depth" : 25.4 * mm});
        }
        {
            var Q0;
            Q0=qCreatedBy(id+"F0.planeOp",FACE);
            var sketch = newSketch(context, id + "F3", { "sketchPlane" : qUnion([Q0])});
            skLineSegment(sketch, "E3904.bottom", {"start": v(36.09, 47.13) * mm, "end": v(46.1, 47.13) * mm});
            skLineSegment(sketch, "E3904.top", {"start": v(36.09, 45.85) * mm, "end": v(46.1, 45.85) * mm});
            skLineSegment(sketch, "E3904.left", {"start": v(36.09, 47.13) * mm, "end": v(36.09, 45.85) * mm});
            skLineSegment(sketch, "E3904.right", {"start": v(46.1, 47.13) * mm, "end": v(46.1, 45.85) * mm});
            skSolve(sketch);
        }
        {
            var Q0;
            Q0 = qSketchRegion(id + "F3", true);
            extrude(context, id + "F4", {"entities" : qUnion([Q0]), "endBound" : BoundingType.SYMMETRIC, "depth" : 12.7 * mm});
        }
        {
            var Q0;
            Q0=qCreatedBy(id+"F0.planeOp",FACE);
            var sketch = newSketch(context, id + "F5", { "sketchPlane" : qUnion([Q0])});
            skLineSegment(sketch, "E3905.bottom", {"start": v(96.2, -34.03) * mm, "end": v(97.48, -34.03) * mm});
            skLineSegment(sketch, "E3905.top", {"start": v(96.2, -47.39) * mm, "end": v(97.48, -47.39) * mm});
            skLineSegment(sketch, "E3905.left", {"start": v(96.2, -34.03) * mm, "end": v(96.2, -47.39) * mm});
            skLineSegment(sketch, "E3905.right", {"start": v(97.48, -34.03) * mm, "end": v(97.48, -47.39) * mm});
            skSolve(sketch);
        }
        {
            var Q0;
            Q0=makeQuery(id+"F5.imprint","IMPRINT",FACE,{"disambiguationData":[TD([[makeQuery(id+"F5.imprint","IMPRINT",EDGE,{"derivedFrom":sQuery(id+"F5.wireOp",EDGE,"E3905.bottom")}),-1.0]])]});
            extrude(context, id + "F6", {"entities" : qUnion([Q0]), "endBound" : BoundingType.SYMMETRIC, "depth" : 6.35 * mm});
        }
    });
